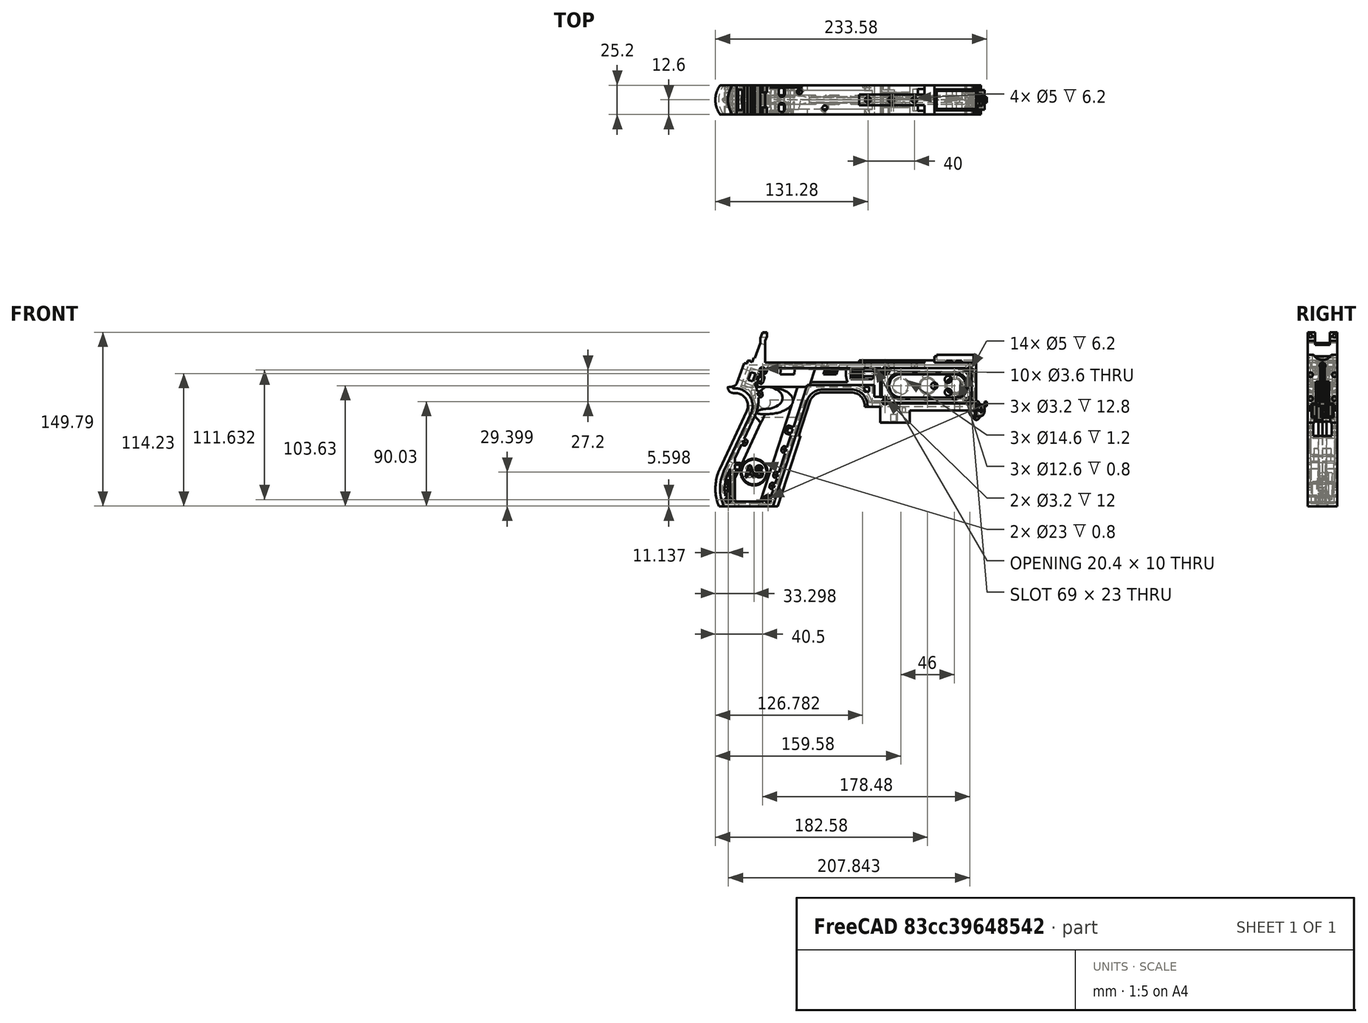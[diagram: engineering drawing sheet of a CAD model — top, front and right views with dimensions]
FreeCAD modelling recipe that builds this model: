
FCSTD DOCUMENT  (FreeCAD 1.0R39319 (Git))
Label: PICON-OF_ver_55
License: All rights reserved
LicenseURL: https://en.wikipedia.org/wiki/All_rights_reserved
objects: Sketcher::SketchObject×124, Part::Extrusion×63, Part::Cut×48, PartDesign::Pad×29, PartDesign::Pocket×21, PartDesign::Chamfer×15, PartDesign::Body×10, PartDesign::Fillet×6, Part::MultiFuse×5, Part::Part2DObjectPython×4, PartDesign::SubtractivePipe×4, PartDesign::SubtractiveLoft×4, PartDesign::Plane×3, PartDesign::SubShapeBinder×2, Part::Sweep×1, PartDesign::ShapeBinder×1, Mesh::Feature×1, PartDesign::Point×1, PartDesign::Groove×1
note: 626 computed .brp shape members not serialized (recipe doc carries the construction recipe); baked Part::Feature solids carry a one-line shape summary decoded from their .brp

FEATURE [Sketcher::SketchObject] Sketch  label="corpo principale"
  ArcFitTolerance = 1e-06
  AttacherType = Attacher::AttachEngine3D
  AttachmentSupport = -> [XZ_Plane]
  FullyConstrained = true
  MakeInternals = false
  MapMode = 5
  Placement = pos=(0,0,0) rot=(1,0,0;1.5708rad)
  sketch-geometry (65):
    g0: LineSegment StartX=0 StartY=0 StartZ=0 EndX=-57.2 EndY=0 EndZ=0
    g1: LineSegment StartX=-57.2 StartY=0 StartZ=0 EndX=-57.2 EndY=-10.4 EndZ=0
    g2: LineSegment StartX=-57.2 StartY=-10.4 StartZ=0 EndX=-82.8 EndY=-10.4 EndZ=0
    g3: LineSegment StartX=-82.8 StartY=-10.4 StartZ=0 EndX=-82.8 EndY=3.2 EndZ=0
    g4: LineSegment StartX=-82.8 StartY=3.2 StartZ=0 EndX=-93.6 EndY=3.2 EndZ=0
    g5: LineSegment StartX=-93.6 StartY=3.2 StartZ=0 EndX=-93.6 EndY=4 EndZ=0
    g6: LineSegment StartX=-107.6 StartY=18 StartZ=0 EndX=-132.428 EndY=18 EndZ=0
    g7: LineSegment StartX=-145.743 StartY=8.32624 StartZ=0 EndX=-175.232 EndY=-82.4316 EndZ=0
    g8: LineSegment StartX=-175.232 StartY=-82.4316 StartZ=0 EndX=-217.232 EndY=-82.4316 EndZ=0
    g9: LineSegment StartX=-217.232 StartY=-52.1862 StartZ=0 EndX=-193.988 EndY=-2.33927 EndZ=0
    g10: LineSegment StartX=-206.196 StartY=23.0857 StartZ=0 EndX=-199.861 EndY=40.4914 EndZ=0
    g11: LineSegment StartX=-199.861 StartY=40.4914 StartZ=0 EndX=-197.061 EndY=40.4914 EndZ=0
    g12: LineSegment StartX=-197.061 StartY=40.4914 StartZ=0 EndX=-197.061 EndY=42.8914 EndZ=0
    g13: LineSegment StartX=-197.061 StartY=42.8914 StartZ=0 EndX=-194.261 EndY=42.8914 EndZ=0
    g14: LineSegment StartX=-194.261 StartY=42.8914 StartZ=0 EndX=-194.535 EndY=42.1397 EndZ=0
    g15: LineSegment StartX=-194.535 StartY=42.1397 StartZ=0 EndX=-193.031 EndY=41.5924 EndZ=0
    g16: LineSegment StartX=-193.031 StartY=41.5924 StartZ=0 EndX=-191.663 EndY=45.3512 EndZ=0
    g17: LineSegment StartX=-191.663 StartY=45.3512 StartZ=0 EndX=-190.536 EndY=44.9408 EndZ=0
    g18: LineSegment StartX=-190.536 StartY=44.9408 StartZ=0 EndX=-185.747 EndY=58.0965 EndZ=0
    g19: LineSegment StartX=-185.747 StartY=58.0965 StartZ=0 EndX=-185.747 EndY=62.0965 EndZ=0
    g20: LineSegment StartX=-185.747 StartY=62.0965 StartZ=0 EndX=-183.832 EndY=67.3588 EndZ=0
    g21: LineSegment StartX=-183.832 StartY=67.3588 StartZ=0 EndX=-180.232 EndY=67.3588 EndZ=0
    g22: LineSegment StartX=-180.232 StartY=67.3588 StartZ=0 EndX=-180.232 EndY=63.7588 EndZ=0
    g23: LineSegment StartX=-180.232 StartY=63.7588 StartZ=0 EndX=-181.6 EndY=60 EndZ=0
    g24: LineSegment StartX=-181.6 StartY=60 StartZ=0 EndX=-181.6 EndY=41.2 EndZ=0
    g25: LineSegment StartX=-181.6 StartY=41.2 StartZ=0 EndX=-100.8 EndY=41.2 EndZ=0
    g26: LineSegment StartX=-36 StartY=43.2 StartZ=0 EndX=-36 EndY=41.2 EndZ=0
    g27: LineSegment StartX=0 StartY=48 StartZ=0 EndX=0 EndY=0 EndZ=0
    g28: LineSegment StartX=-209.901 StartY=19.85 StartZ=0 EndX=-209.901 EndY=20.1 EndZ=0
    g29: LineSegment StartX=-208.001 StartY=22 StartZ=0 EndX=-207.747 EndY=22 EndZ=0
    g30: LineSegment StartX=-207.583 StartY=19 StartZ=0 EndX=-209.051 EndY=19 EndZ=0
    g31: ArcOfCircle CenterX=-208.001 CenterY=20.1 CenterZ=0 NormalX=0 NormalY=0 NormalZ=1 AngleXU=0 Radius=1.9 StartAngle=1.5708 EndAngle=3.14159
    g32: GeomPoint [constr] X=-209.901 Y=22 Z=0
    g33: ArcOfCircle CenterX=-209.051 CenterY=19.85 CenterZ=0 NormalX=0 NormalY=0 NormalZ=1 AngleXU=0 Radius=0.85 StartAngle=3.14159 EndAngle=4.71239
    g34: GeomPoint [constr] X=-209.901 Y=19 Z=0
    g35: ArcOfCircle CenterX=-207.747 CenterY=23.65 CenterZ=0 NormalX=0 NormalY=0 NormalZ=1 AngleXU=0 Radius=1.65 StartAngle=4.71239 EndAngle=5.93412
    g36: GeomPoint [constr] X=-206.591 Y=22 Z=0
    g37: LineSegment StartX=-4 StartY=6 StartZ=0 EndX=-4 EndY=36.4 EndZ=0
    g38: LineSegment StartX=-4 StartY=36.4 StartZ=0 EndX=-185.2 EndY=36.4 EndZ=0
    g39: LineSegment StartX=-185.2 StartY=36.4 StartZ=0 EndX=-190.441 EndY=22 EndZ=0
    g40: LineSegment StartX=-214.575 StartY=-78.4316 StartZ=0 EndX=-178.142 EndY=-78.4316 EndZ=0
    g41: LineSegment StartX=-178.142 StartY=-78.4316 StartZ=0 EndX=-145.51 EndY=22 EndZ=0
    g42: LineSegment StartX=-145.51 StartY=22 StartZ=0 EndX=-87.91 EndY=22 EndZ=0
    g43: LineSegment StartX=-87.91 StartY=22 StartZ=0 EndX=-87.91 EndY=11.6 EndZ=0
    g44: LineSegment StartX=-87.91 StartY=11.6 StartZ=0 EndX=-80.11 EndY=11.6 EndZ=0
    g45: LineSegment StartX=-80.11 StartY=11.6 StartZ=0 EndX=-80.11 EndY=6 EndZ=0
    g46: LineSegment StartX=-80.11 StartY=6 StartZ=0 EndX=-4 EndY=6 EndZ=0
    g47: LineSegment StartX=-190.363 StartY=-4.02975 StartZ=0 EndX=-213.607 EndY=-53.8767 EndZ=0
    g48: ArcOfCircle CenterX=-132.428 CenterY=4 CenterZ=0 NormalX=0 NormalY=0 NormalZ=1 AngleXU=0 Radius=14 StartAngle=1.5708 EndAngle=2.82743
    g49: GeomPoint [constr] X=-142.6 Y=18 Z=0
    g50: ArcOfCircle CenterX=-107.6 CenterY=4 CenterZ=0 NormalX=0 NormalY=0 NormalZ=1 AngleXU=0 Radius=14 StartAngle=0 EndAngle=1.5708
    g51: GeomPoint [constr] X=-93.6 Y=18 Z=0
    g52: ArcOfCircle CenterX=-184.801 CenterY=-67.3089 CenterZ=0 NormalX=0 NormalY=0 NormalZ=1 AngleXU=0 Radius=35.7833 StartAngle=2.70526 EndAngle=3.57792
    g53: ArcOfCircle CenterX=-207.583 CenterY=4 CenterZ=0 NormalX=0 NormalY=0 NormalZ=1 AngleXU=0 Radius=15 StartAngle=5.84685 EndAngle=7.85398
    g54: LineSegment [constr] StartX=-213.607 StartY=-53.8767 StartZ=0 EndX=-217.232 EndY=-52.1862 EndZ=0
    g55: ArcOfCircle CenterX=-184.801 CenterY=-67.3089 CenterZ=0 NormalX=0 NormalY=0 NormalZ=1 AngleXU=0 Radius=31.7833 StartAngle=2.70526 EndAngle=3.49911
    g56: ArcOfCircle CenterX=-218.095 CenterY=8.90192 CenterZ=0 NormalX=0 NormalY=0 NormalZ=1 AngleXU=0 Radius=30.5989 StartAngle=5.84685 EndAngle=6.72553
    g57: LineSegment StartX=-44.6 StartY=43.2 StartZ=0 EndX=-36 EndY=43.2 EndZ=0
    g58: LineSegment StartX=-100.8 StartY=41.2 StartZ=0 EndX=-44.6 EndY=41.2 EndZ=0
    g59: LineSegment StartX=-44.6 StartY=41.2 StartZ=0 EndX=-44.6 EndY=43.2 EndZ=0
    g60: LineSegment StartX=-2.4 StartY=48 StartZ=0 EndX=0 EndY=48 EndZ=0
    g61: LineSegment StartX=-36 StartY=41.2 StartZ=0 EndX=-2.4 EndY=41.2 EndZ=0
    g62: LineSegment StartX=-2.4 StartY=41.2 StartZ=0 EndX=-2.4 EndY=48 EndZ=0
    g63: LineSegment [constr] StartX=-181.6 StartY=36.4 StartZ=0 EndX=-152.209 EndY=36.4 EndZ=0
    g64: LineSegment [constr] StartX=-181.6 StartY=36.4 StartZ=0 EndX=-130.41 EndY=36.4 EndZ=0
  constraints (183):
    c: Coincident(g-1,g0)
    c: PointOnObject(g0,g-1)
    c: Coincident(g0,g1)
    c: Vertical(g1)
    c: Coincident(g1,g2)
    c: Horizontal(g2)
    c: Coincident(g2,g3)
    c: Vertical(g3)
    c: Coincident(g3,g4)
    c: Coincident(g4,g5)
    c: Vertical(g5)
    c: Horizontal(g6)
    c: Coincident(g7,g8)
    c: Horizontal(g8)
    c: Coincident(g10,g11)
    c: Horizontal(g11)
    c: Coincident(g11,g12)
    c: Vertical(g12)
    c: Coincident(g12,g13)
    c: Horizontal(g13)
    c: Coincident(g13,g14)
    c: Coincident(g14,g15)
    c: Coincident(g15,g16)
    c: Coincident(g16,g17)
    c: Coincident(g17,g18)
    c: Coincident(g18,g19)
    c: Vertical(g19)
    c: Coincident(g19,g20)
    c: Coincident(g20,g21)
    c: Horizontal(g21)
    c: Coincident(g21,g22)
    c: Vertical(g22)
    c: Coincident(g22,g23)
    c: Coincident(g23,g24)
    c: Vertical(g24)
    c: Coincident(g24,g25)
    c: Horizontal(g25)
    c: Coincident(g57,g26)
    c: Vertical(g26)
    c: Coincident(g26,g61)
    c: PointOnObject(g60,g-2)
    c: Coincident(g60,g27)
    c: Coincident(g27,g0)
    c: DistanceY(g27,g27) = 48
    c: DistanceY(g1,g1) = 10.4
    c: DistanceX(g0,g0) = 57.2
    c: DistanceX(g2,g2) = 25.6
    c: Horizontal(g4)
    c: DistanceY(g3,g3) = 13.6
    c: DistanceX(g4,g4) = 10.8
    c: DistanceY(g5,g51) = 14.8
    c: DistanceX(g49,g51) = 49
    c: Distance(g7,g49) = 105.6
    c: DistanceX(g61,g60) = 36
    c: DistanceX(g25,g25) = 80.8
    c: DistanceY(g24,g24) = 18.8
    c: DistanceY(g22,g22) = 3.6
    c: Distance(g23) = 4
    c: Angle(g-1,g23) = 1.22173
    c: DistanceX(g21,g21) = 3.6
    c: Distance(g20) = 5.6
    c: Angle(g-1,g20) = 1.22173
    c: DistanceY(g19,g19) = 4
    c: Distance(g18) = 14
    c: Angle(g-1,g18) = 1.22173
    c: Distance(g17) = 1.2
    c: Distance(g16) = 4
    c: Angle(g16) = 1.22173
    c: Perpendicular(g18,g17)
    c: Distance(g15) = 1.6
    c: Perpendicular(g16,g15)
    c: Distance(g14) = 0.8
    c: DistanceX(g13,g13) = 2.8
    c: Perpendicular(g15,g14)
    c: DistanceY(g12,g12) = 2.4
    c: DistanceX(g11,g11) = 2.8
    c: Distance(g9) = 55
    c: Angle(g9,g-1) = 2.00713
    c: Horizontal(g29)
    c: Vertical(g28)
    c: Horizontal(g30)
    c: PointOnObject(g32,g29)
    c: PointOnObject(g32,g28)
    c: Tangent(g29,g31) = 1.5708
    c: Tangent(g28,g31) = 1.5708
    c: PointOnObject(g34,g28)
    c: PointOnObject(g34,g30)
    c: Tangent(g28,g33) = 1.5708
    c: Tangent(g30,g33) = 1.5708
    c: PointOnObject(g36,g29)
    c: PointOnObject(g36,g10)
    c: Tangent(g29,g35) = -1.5708
    c: Tangent(g10,g35) = -1.5708
    c: Angle(g-1,g10) = 1.22173
    c: Radius(g35) = 1.65
    c: Vertical(g37)
    c: Coincident(g37,g38)
    c: Horizontal(g38)
    c: Coincident(g38,g39)
    c: Horizontal(g40)
    c: Coincident(g40,g41)
    c: Coincident(g41,g42)
    c: Horizontal(g42)
    c: Coincident(g42,g43)
    c: Vertical(g43)
    c: Coincident(g43,g44)
    c: Horizontal(g44)
    c: Coincident(g44,g45)
    c: Vertical(g45)
    c: Coincident(g45,g46)
    c: Coincident(g46,g37)
    c: Horizontal(g46)
    c: DistanceY(g0,g37) = 6
    c: DistanceX(g37,g0) = 4
    c: DistanceY(g37,g25) = 4.8
    c: DistanceX(g38,g38) = 181.2
    c: DistanceX(g42,g42) = 57.6
    c: DistanceY(g49,g41) = 4
    c: DistanceX(g41,g49) = 2.91
    c: DistanceY(g43,g43) = 10.4
    c: DistanceX(g44,g44) = 7.8
    c: DistanceY(g7,g40) = 4
    c: Distance(g47) = 55
    c: Angle(g-1,g39) = 1.22173
    c: PointOnObject(g49,g7)
    c: PointOnObject(g49,g6)
    c: Tangent(g7,g48) = -1.5708
    c: Tangent(g6,g48) = -1.5708
    c: PointOnObject(g51,g5)
    c: PointOnObject(g51,g6)
    c: Tangent(g5,g50) = -1.5708
    c: Tangent(g6,g50) = -1.5708
    c: Radius(g50) = 14
    c: Radius(g48) = 14
    c: DistanceX(g8,g8) = 42
    c: Angle(g7,g-1) = 1.88496
    c: Parallel(g41,g7)
    c: Parallel(g47,g9)
    c: Coincident(g52,g8)
    c: Tangent(g52,g9) = 1.5708
    c: DistanceX(g9,g8) = 0
    c: Tangent(g53,g9) = -1.5708
    c: Tangent(g53,g30) = -1.5708
    c: Diameter(g53) = 30
    c: DistanceY(g53,g0) = -4
    c: Coincident(g54,g47)
    c: Distance(g54) = 4
    c: Coincident(g54,g9)
    c: Coincident(g55,g40)
    c: Tangent(g55,g47) = -1.5708
    c: Coincident(g52,g55)
    c: Coincident(g56,g39)
    c: Tangent(g56,g47) = 1.5708
    c: Horizontal(g57)
    c: DistanceX(g57,g57) = 8.6
    c: Coincident(g58,g25)
    c: Horizontal(g58)
    c: Coincident(g59,g58)
    c: Vertical(g59)
    c: DistanceY(g58,g57) = 2
    c: DistanceX(g58,g58) = 56.2
    c: Coincident(g59,g57)
    c: DistanceY(g41,g36) = 0
    c: DistanceY(g36,g39) = 0
    c: DistanceY(g28,g28) = 0.25
    c: DistanceX(g30,g36) = 2.46
    c: DistanceX(g28,g29) = 1.9
    c: Coincident(g62,g60)
    c: Horizontal(g60)
    c: DistanceX(g62,g27) = 2.4
    c: Coincident(g61,g62)
    c: DistanceY(g26,g26) = 2
    c: Vertical(g62)
    c: DistanceY(g61,g60) = 6.8
    c: Horizontal(g61)
    c: Distance(g63) = 29.391
    c: PointOnObject(g63,g38)
    c: PointOnObject(g63,g38)
    c: Distance(g64) = 51.19
    c: PointOnObject(g64,g38)
    c: PointOnObject(g64,g38)
    c: DistanceX(g24,g63) = 0
    c: DistanceX(g24,g64) = 0
FEATURE [Part::Extrusion] Extrude  label="Extrude corpo principale"
  Base = -> Sketch
  Dir = (0,-1,2e-16)
  DirMode = 2
  FaceMakerClass = Part::FaceMakerBullseye
  FaceMakerMode = 3
  LengthFwd = 25.2
  LengthRev = 12.6
  Solid = true
  Symmetric = true
FEATURE [Sketcher::SketchObject] Sketch002  label="scavo grilletto"
  ArcFitTolerance = 1e-06
  AttachmentSupport = -> [XZ_Plane]
  ExternalGeometry = -> [Sketch]
  FullyConstrained = true
  MakeInternals = false
  MapMode = 5
  Placement = pos=(0,0,0) rot=(1,0,0;1.5708rad)
  sketch-geometry (4):
    g0: LineSegment StartX=-89.51 StartY=22 StartZ=0 EndX=-152.71 EndY=22 EndZ=0
    g1: LineSegment StartX=-152.71 StartY=22 StartZ=0 EndX=-167.006 EndY=-22 EndZ=0
    g2: LineSegment StartX=-167.006 StartY=-22 StartZ=0 EndX=-89.51 EndY=-22 EndZ=0
    g3: LineSegment StartX=-89.51 StartY=-22 StartZ=0 EndX=-89.51 EndY=22 EndZ=0
  constraints (12):
    c: Horizontal(g0)
    c: Coincident(g0,g1)
    c: Coincident(g1,g2)
    c: Horizontal(g2)
    c: Coincident(g2,g3)
    c: Coincident(g3,g0)
    c: Vertical(g3)
    c: Angle(g1,g0) = 1.88496
    c: DistanceY(g3,g3) = 44
    c: DistanceX(g0,g0) = 63.2
    c: DistanceX(g0,g-3) = 1.6
    c: DistanceY(g-3,g0) = 0
FEATURE [Sketcher::SketchObject] Sketch004  label="traiettoria arrotondamento impugnatura anteriore"
  ArcFitTolerance = 1e-06
  AttachmentSupport = -> [XZ_Plane]
  ExternalGeometry = -> [Sketch]
  FullyConstrained = true
  MakeInternals = false
  MapMode = 5
  Placement = pos=(0,0,0) rot=(1,0,0;1.5708rad)
  sketch-geometry (13):
    g0: LineSegment StartX=-175.232 StartY=-82.4316 StartZ=0 EndX=-145.743 EndY=8.32624 EndZ=0
    g1: LineSegment StartX=-93.6 StartY=3.2 StartZ=0 EndX=-93.6 EndY=4 EndZ=0
    g2: LineSegment StartX=-132.428 StartY=18 StartZ=0 EndX=-107.6 EndY=18 EndZ=0
    g3: ArcOfCircle CenterX=-132.428 CenterY=4 CenterZ=0 NormalX=0 NormalY=0 NormalZ=1 AngleXU=0 Radius=14 StartAngle=1.5708 EndAngle=2.82743
    g4: ArcOfCircle CenterX=-107.6 CenterY=4 CenterZ=0 NormalX=0 NormalY=0 NormalZ=1 AngleXU=0 Radius=14 StartAngle=0 EndAngle=1.5708
    g5: LineSegment StartX=-175.232 StartY=-82.4316 StartZ=0 EndX=-217.232 EndY=-82.4316 EndZ=0
    g6: LineSegment StartX=-217.232 StartY=-52.1862 StartZ=0 EndX=-193.988 EndY=-2.33927 EndZ=0
    g7: LineSegment StartX=-209.051 StartY=19 StartZ=0 EndX=-207.583 EndY=19 EndZ=0
    g8: LineSegment StartX=-209.901 StartY=20.1 StartZ=0 EndX=-209.901 EndY=19.85 EndZ=0
    g9: ArcOfCircle CenterX=-184.801 CenterY=-67.3089 CenterZ=0 NormalX=0 NormalY=0 NormalZ=1 AngleXU=0 Radius=35.7833 StartAngle=2.70526 EndAngle=3.57792
    g10: ArcOfCircle CenterX=-207.583 CenterY=4 CenterZ=0 NormalX=0 NormalY=0 NormalZ=1 AngleXU=0 Radius=15 StartAngle=5.84685 EndAngle=7.85398
    g11: ArcOfCircle CenterX=-209.051 CenterY=19.85 CenterZ=0 NormalX=0 NormalY=0 NormalZ=1 AngleXU=0 Radius=0.85 StartAngle=3.14159 EndAngle=4.71239
    g12: ArcOfCircle CenterX=-208.001 CenterY=20.1 CenterZ=0 NormalX=0 NormalY=0 NormalZ=1 AngleXU=0 Radius=1.9 StartAngle=1.5708 EndAngle=3.14159
  constraints (26):
    c: Coincident(g0,g-3)
    c: Coincident(g0,g-6)
    c: Coincident(g1,g-8)
    c: Coincident(g1,g-7)
    c: Coincident(g2,g-5)
    c: Coincident(g2,g-4)
    c: Coincident(g3,g2)
    c: Tangent(g3,g0) = 1.5708
    c: Coincident(g4,g1)
    c: Tangent(g4,g2) = 1.5708
    c: Coincident(g5,g0)
    c: Coincident(g5,g-9)
    c: Coincident(g6,g-12)
    c: Coincident(g6,g-11)
    c: Coincident(g7,g-15)
    c: Coincident(g7,g-14)
    c: Coincident(g8,g-16)
    c: Coincident(g8,g-17)
    c: Tangent(g9,g6) = 1.5708
    c: Coincident(g9,g5)
    c: Coincident(g10,g7)
    c: Tangent(g10,g6) = -1.5708
    c: Tangent(g11,g7) = -1.5708
    c: Coincident(g11,g8)
    c: Tangent(g12,g8) = -1.5708
    c: Coincident(g12,g-17)
FEATURE [PartDesign::Plane] DatumPlane  label="Piano per disegno arrotondamento impugnatura"
  AttachmentSupport = -> [Sketch]
  Length = 73.6581
  MapMode = 7
  Placement = pos=(-145.743,1.8e-15,8.32624) rot=(0.154555,0.154555,0.97582;1.59527rad)
  ResizeMode = 0
  Width = 303.511
FEATURE [Sketcher::SketchObject] Sketch005  label="forma arrotondamento impugnatura anteriore"
  ArcFitTolerance = 1e-06
  AttachmentSupport = -> [DatumPlane]
  FullyConstrained = true
  MakeInternals = false
  MapMode = 5
  Placement = pos=(-145.743,1.8e-15,8.32624) rot=(0.154555,0.154555,0.97582;1.59527rad)
  sketch-geometry (5):
    g0: GeomPoint [constr] X=0 Y=-4 Z=0
    g1: GeomPoint [constr] X=-12.6 Y=7.1e-15 Z=0
    g2: GeomPoint [constr] X=12.6 Y=4.97e-14 Z=0
    g3: LineSegment StartX=-12.6 StartY=7.1e-15 StartZ=0 EndX=12.6 EndY=4.97e-14 EndZ=0
    g4: ArcOfCircle CenterX=-3.88e-14 CenterY=17.845 CenterZ=0 NormalX=0 NormalY=0 NormalZ=1 AngleXU=0 Radius=21.845 StartAngle=4.09759 EndAngle=5.32718
  constraints (11):
    c: DistanceY(g0,g-1) = 4
    c: DistanceX(g-1,g0) = 0
    c: DistanceX(g1,g-1) = 12.6
    c: DistanceX(g-1,g2) = 12.6
    c: DistanceY(g-1,g2) = 0
    c: DistanceY(g-1,g1) = 0
    c: Coincident(g3,g1)
    c: Coincident(g3,g2)
    c: Coincident(g4,g1)
    c: Coincident(g4,g2)
    c: PointOnObject(g0,g4)
FEATURE [Part::Sweep] Sweep  label="Sweep impugnatura"
  Frenet = true
  Sections = -> [Sketch005]
  Solid = true
  Spine = -> Sketch [Edge32,Edge33,Edge34,Edge35,Edge36,Edge37,Edge38,Edge39,Edge40,Edge41,Edge42,Edge43,Edge44]
  Transition = 1
FEATURE [Sketcher::SketchObject] Sketch008  label="buchi e pulizie varie"
  ArcFitTolerance = 1e-06
  AttachmentSupport = -> [XZ_Plane]
  ExternalGeometry = -> [Sketch]
  FullyConstrained = true
  MakeInternals = false
  MapMode = 5
  Placement = pos=(0,0,0) rot=(1,0,0;1.5708rad)
  sketch-geometry (26):
    g0: LineSegment StartX=-96.278 StartY=20.155 StartZ=0 EndX=-92.278 EndY=20.155 EndZ=0
    g1: LineSegment StartX=-92.278 StartY=20.155 StartZ=0 EndX=-92.278 EndY=16.155 EndZ=0
    g2: LineSegment StartX=-92.278 StartY=16.155 StartZ=0 EndX=-96.278 EndY=16.155 EndZ=0
    g3: LineSegment StartX=-96.278 StartY=16.155 StartZ=0 EndX=-96.278 EndY=20.155 EndZ=0
    g4: LineSegment StartX=-222.232 StartY=-82.4316 StartZ=0 EndX=-170.232 EndY=-82.4316 EndZ=0
    g5: LineSegment StartX=-170.232 StartY=-82.4316 StartZ=0 EndX=-170.232 EndY=-86.4316 EndZ=0
    g6: LineSegment StartX=-170.232 StartY=-86.4316 StartZ=0 EndX=-222.232 EndY=-86.4316 EndZ=0
    g7: LineSegment StartX=-222.232 StartY=-86.4316 StartZ=0 EndX=-222.232 EndY=-82.4316 EndZ=0
    g8: LineSegment StartX=-213.901 StartY=20.1 StartZ=0 EndX=-213.901 EndY=26 EndZ=0
    g9: LineSegment StartX=-213.901 StartY=26 StartZ=0 EndX=-206.196 EndY=26 EndZ=0
    g10: LineSegment StartX=-17.4 StartY=42.8 StartZ=0 EndX=-12.4 EndY=42.8 EndZ=0
    g11: LineSegment StartX=-12.4 StartY=42.8 StartZ=0 EndX=-12.4 EndY=41.2 EndZ=0
    g12: LineSegment StartX=-12.4 StartY=41.2 StartZ=0 EndX=-17.4 EndY=41.2 EndZ=0
    g13: LineSegment StartX=-17.4 StartY=41.2 StartZ=0 EndX=-17.4 EndY=42.8 EndZ=0
    g14: LineSegment StartX=-25.9 StartY=42.8 StartZ=0 EndX=-20.9 EndY=42.8 EndZ=0
    g15: LineSegment StartX=-20.9 StartY=42.8 StartZ=0 EndX=-20.9 EndY=41.2 EndZ=0
    g16: LineSegment StartX=-20.9 StartY=41.2 StartZ=0 EndX=-25.9 EndY=41.2 EndZ=0
    g17: LineSegment StartX=-25.9 StartY=41.2 StartZ=0 EndX=-25.9 EndY=42.8 EndZ=0
    g18: GeomPoint [constr] X=-206.196 Y=23.0857 Z=0
    g19: GeomPoint [constr] X=-213.901 Y=20.1 Z=0
    g20: BSplineCurve PolesCount=4 KnotsCount=2 Degree=3 IsPeriodic=0
    g21-g24: Circle [constr] x4 (B-spline internal-alignment scaffolding for g20; pole/knot coordinates omitted)
    g25: LineSegment StartX=-206.196 StartY=26 StartZ=0 EndX=-206.196 EndY=23.0857 EndZ=0
  constraints (73):
    c: Horizontal(g0)
    c: Coincident(g1,g0)
    c: Vertical(g1)
    c: Coincident(g2,g1)
    c: Horizontal(g2)
    c: Coincident(g3,g2)
    c: Coincident(g3,g0)
    c: Vertical(g3)
    c: DistanceX(g0,g-4) = 4.368
    c: DistanceY(g0,g-4) = 1.845
    c: DistanceY(g1,g1) = 4
    c: DistanceX(g2,g2) = 4
    c: Horizontal(g4)
    c: Coincident(g5,g4)
    c: Vertical(g5)
    c: Coincident(g6,g5)
    c: Horizontal(g6)
    c: Coincident(g7,g6)
    c: Coincident(g7,g4)
    c: Vertical(g7)
    c: DistanceY(g7,g7) = 4
    c: DistanceX(g4,g-5) = 5
    c: DistanceX(g-5,g4) = 5
    c: DistanceY(g4,g-5) = 0
    c: Coincident(g9,g8)
    c: Parallel(g9,g-6)
    c: DistanceX(g8,g-8) = 4
    c: Horizontal(g10)
    c: Coincident(g11,g10)
    c: Vertical(g11)
    c: Coincident(g12,g11)
    c: Horizontal(g12)
    c: Coincident(g13,g12)
    c: Coincident(g13,g10)
    c: Vertical(g13)
    c: Horizontal(g14)
    c: Coincident(g15,g14)
    c: Vertical(g15)
    c: Coincident(g16,g15)
    c: Horizontal(g16)
    c: Coincident(g17,g16)
    c: Coincident(g17,g14)
    c: Vertical(g17)
    c: DistanceY(g11,g10) = 1.6
    c: DistanceX(g10,g10) = 5
    c: DistanceY(g15,g14) = 1.6
    c: DistanceX(g14,g14) = 5
    c: DistanceX(g15,g12) = 3.5
    c: DistanceX(g11,g-9) = 10
    c: DistanceY(g-9,g11) = 0
    c: DistanceY(g-9,g15) = 0
    c: Perpendicular(g8,g9)
    c: DistanceY(g-7,g9) = 4
    c: DistanceY(g8,g-8) = 0
    c: InternalAlignment(g18,g20)
    c: InternalAlignment(g19,g20)
    c: InternalAlignment(g21,g20)
    c: Weight(g21) = 1
    c: InternalAlignment(g22,g20)
    c: Equal(g22,g21)
    c: InternalAlignment(g23,g20)
    c: Equal(g23,g21)
    c: InternalAlignment(g24,g20)
    c: Equal(g24,g21)
    c: Coincident(g18,g-12)
    c: Coincident(g19,g8)
    c: Coincident(g25,g9)
    c: Coincident(g25,g20)
    c: Vertical(g25)
    c: DistanceY(g20,g23) = 0
    c: DistanceY(g22,g18) = 2.26
    c: DistanceX(g22,g18) = 0.93
    c: DistanceX(g20,g23) = 2.9
FEATURE [Part::Extrusion] Extrude004  label="Extrude Buchi e pulizie varie"
  Base = -> Sketch008
  Dir = (0,-1,2e-16)
  DirMode = 2
  FaceMakerClass = Part::FaceMakerBullseye
  FaceMakerMode = 3
  LengthFwd = 25.2
  LengthRev = 0
  Solid = true
  Symmetric = true
FEATURE [Sketcher::SketchObject] Sketch009  label="rinforzi"
  ArcFitTolerance = 1e-06
  AttachmentSupport = -> [XZ_Plane]
  ExternalGeometry = -> [Sketch]
  FullyConstrained = true
  MakeInternals = false
  MapMode = 5
  Placement = pos=(0,0,0) rot=(1,0,0;1.5708rad)
  sketch-geometry (9):
    g0: LineSegment StartX=-87.91 StartY=22 StartZ=0 EndX=-87.91 EndY=36.4 EndZ=0
    g1: LineSegment StartX=-87.91 StartY=36.4 StartZ=0 EndX=-97.91 EndY=36.4 EndZ=0
    g2: LineSegment StartX=-97.91 StartY=36.4 StartZ=0 EndX=-97.91 EndY=22 EndZ=0
    g3: LineSegment StartX=-97.91 StartY=22 StartZ=0 EndX=-87.91 EndY=22 EndZ=0
    g4: LineSegment StartX=-149.713 StartY=9.06563 StartZ=0 EndX=-154.586 EndY=-5.93437 EndZ=0
    g5: LineSegment StartX=-154.586 StartY=-5.93437 StartZ=0 EndX=-191.863 EndY=-5.93437 EndZ=0
    g6: LineSegment StartX=-191.863 StartY=-5.93437 StartZ=0 EndX=-191.863 EndY=9.06563 EndZ=0
    g7: LineSegment StartX=-191.863 StartY=9.06563 StartZ=0 EndX=-149.713 EndY=9.06563 EndZ=0
    g8: LineSegment [constr] StartX=-145.51 StartY=22 StartZ=0 EndX=-149.713 EndY=9.06563 EndZ=0
  constraints (25):
    c: Vertical(g0)
    c: Coincident(g1,g0)
    c: Horizontal(g1)
    c: Coincident(g2,g1)
    c: Vertical(g2)
    c: Coincident(g3,g2)
    c: Coincident(g3,g0)
    c: Horizontal(g3)
    c: Coincident(g0,g-4)
    c: DistanceX(g3,g3) = 10
    c: DistanceY(g0,g-3) = 0
    c: Coincident(g5,g4)
    c: Horizontal(g5)
    c: Coincident(g6,g5)
    c: Vertical(g6)
    c: Coincident(g7,g6)
    c: Coincident(g7,g4)
    c: Horizontal(g7)
    c: Distance(g8) = 13.6
    c: Parallel(g-6,g8)
    c: Coincident(g-6,g8)
    c: Parallel(g4,g-6)
    c: DistanceY(g4,g4) = 15
    c: Coincident(g4,g8)
    c: DistanceX(g-5,g5) = -1.5
FEATURE [Part::Extrusion] Extrude001  label="Extrude scavo grilletto"
  Base = -> Sketch002
  Dir = (0,-1,2e-16)
  DirMode = 2
  FaceMakerClass = Part::FaceMakerBullseye
  FaceMakerMode = 3
  LengthFwd = 16
  LengthRev = 0
  Solid = true
  Symmetric = true
FEATURE [Part::Extrusion] Extrude005  label="Extrude Rinforzi"
  Base = -> Sketch009
  Dir = (0,-1,2e-16)
  DirMode = 2
  FaceMakerClass = Part::FaceMakerBullseye
  FaceMakerMode = 3
  LengthFwd = 2
  LengthRev = 0
  Placement = pos=(0,12.6,0) rot=(0,0,1;0rad)
  Solid = true
  Symmetric = false
FEATURE [PartDesign::ShapeBinder] CopyCut
  TraceSupport = false
FEATURE [PartDesign::Plane] DatumPlane001
  AttachmentSupport = -> [CopyCut]
  Length = 283.944
  MapMode = 5
  Placement = pos=(0,12.6,0) rot=(0,0.707107,0.707107;3.14159rad)
  ResizeMode = 0
  Width = 188.15
FEATURE [Sketcher::SketchObject] Sketch010  label="buco neopixel"
  ArcFitTolerance = 1e-06
  AttachmentSupport = -> [XZ_Plane]
  ExternalGeometry = -> [Sketch]
  FullyConstrained = true
  MakeInternals = false
  MapMode = 5
  Placement = pos=(0,0,0) rot=(1,0,0;1.5708rad)
  sketch-geometry (5):
    g0: LineSegment [constr] StartX=-199.861 StartY=40.4914 StartZ=0 EndX=-201.368 EndY=36.3521 EndZ=0
    g1: LineSegment StartX=-201.368 StartY=36.3521 StartZ=0 EndX=-204.932 EndY=26.5605 EndZ=0
    g2: LineSegment StartX=-201.368 StartY=36.3521 StartZ=0 EndX=-180.2 EndY=28.6477 EndZ=0
    g3: LineSegment StartX=-180.2 StartY=28.6477 StartZ=0 EndX=-183.764 EndY=18.8561 EndZ=0
    g4: LineSegment StartX=-183.764 StartY=18.8561 StartZ=0 EndX=-204.932 EndY=26.5605 EndZ=0
  constraints (14):
    c: Parallel(g0,g-3)
    c: Distance(g0) = 4.405
    c: Coincident(g0,g-3)
    c: Coincident(g2,g1)
    c: Coincident(g3,g2)
    c: Coincident(g4,g3)
    c: Coincident(g4,g1)
    c: Parallel(g1,g-3)
    c: Distance(g1) = 10.42
    c: Coincident(g1,g0)
    c: Parallel(g2,g4)
    c: Perpendicular(g1,g2)
    c: DistanceX(g-4,g2) = 5
    c: Parallel(g3,g1)
FEATURE [Part::Extrusion] Extrude006  label="Extrude buco neopixel"
  Base = -> Sketch010
  Dir = (0,-1,2e-16)
  DirMode = 2
  FaceMakerClass = Part::FaceMakerBullseye
  FaceMakerMode = 3
  LengthFwd = 17.2
  LengthRev = 0
  Solid = true
  Symmetric = true
FEATURE [Sketcher::SketchObject] Sketch011  label="fermo grilletto"
  ArcFitTolerance = 1e-06
  AttachmentSupport = -> [XZ_Plane]
  ExternalGeometry = -> [Sketch]
  FullyConstrained = true
  MakeInternals = false
  MapMode = 5
  Placement = pos=(0,0,0) rot=(1,0,0;1.5708rad)
  sketch-geometry (18):
    g0: LineSegment [constr] StartX=-145.51 StartY=22 StartZ=0 EndX=-157.347 EndY=-14.4293 EndZ=0
    g1: LineSegment [constr] StartX=-157.347 StartY=-14.4293 StartZ=0 EndX=-157.841 EndY=-15.951 EndZ=0
    g2: LineSegment StartX=-161.151 StartY=-13.1932 StartZ=0 EndX=-155.825 EndY=-14.9237 EndZ=0
    g3: LineSegment StartX=-163.167 StartY=-14.2205 StartZ=0 EndX=-164.403 EndY=-18.0247 EndZ=0
    g4: LineSegment StartX=-163.376 StartY=-20.0408 StartZ=0 EndX=-158.05 EndY=-21.7713 EndZ=0
    g5: LineSegment StartX=-158.05 StartY=-21.7713 StartZ=0 EndX=-155.825 EndY=-14.9237 EndZ=0
    g6: LineSegment StartX=-161.645 StartY=-14.7149 StartZ=0 EndX=-157.841 EndY=-15.951 EndZ=0
    g7: LineSegment StartX=-157.841 StartY=-15.951 StartZ=0 EndX=-159.077 EndY=-19.7552 EndZ=0
    g8: LineSegment StartX=-159.077 StartY=-19.7552 StartZ=0 EndX=-162.881 EndY=-18.5191 EndZ=0
    g9: LineSegment StartX=-162.881 StartY=-18.5191 StartZ=0 EndX=-161.645 EndY=-14.7149 EndZ=0
    g10: LineSegment [constr] StartX=-161.645 StartY=-14.7149 StartZ=0 EndX=-161.151 EndY=-13.1932 EndZ=0
    g11: LineSegment [constr] StartX=-159.077 StartY=-19.7552 StartZ=0 EndX=-157.555 EndY=-20.2496 EndZ=0
    g12: LineSegment [constr] StartX=-159.077 StartY=-19.7552 StartZ=0 EndX=-159.572 EndY=-21.2769 EndZ=0
    g13: LineSegment [constr] StartX=-161.645 StartY=-14.7149 StartZ=0 EndX=-163.167 EndY=-14.2205 EndZ=0
    g14: ArcOfCircle CenterX=-161.645 CenterY=-14.7149 CenterZ=0 NormalX=0 NormalY=0 NormalZ=1 AngleXU=0 Radius=1.6 StartAngle=1.25664 EndAngle=2.82743
    g15: GeomPoint [constr] X=-162.673 Y=-12.6988 Z=0
    g16: ArcOfCircle CenterX=-162.881 CenterY=-18.5191 CenterZ=0 NormalX=0 NormalY=0 NormalZ=1 AngleXU=0 Radius=1.6 StartAngle=2.82743 EndAngle=4.39823
    g17: GeomPoint [constr] X=-164.897 Y=-19.5464 Z=0
  constraints (48):
    c: Parallel(g0,g-3)
    c: Distance(g0) = 38.304
    c: Coincident(g0,g-3)
    c: Parallel(g1,g-3)
    c: Distance(g1) = 1.6
    c: Coincident(g1,g0)
    c: Coincident(g5,g4)
    c: Coincident(g5,g2)
    c: Coincident(g7,g6)
    c: Coincident(g8,g7)
    c: Coincident(g9,g8)
    c: Coincident(g9,g6)
    c: Parallel(g7,g-3)
    c: Parallel(g9,g7)
    c: Perpendicular(g6,g7)
    c: Parallel(g6,g8)
    c: Distance(g6) = 4
    c: Distance(g9) = 4
    c: Parallel(g5,g7)
    c: Parallel(g9,g3)
    c: Parallel(g2,g6)
    c: Parallel(g4,g8)
    c: Parallel(g13,g6)
    c: Parallel(g10,g9)
    c: Parallel(g11,g8)
    c: Parallel(g12,g7)
    c: Distance(g10) = 1.6
    c: Distance(g13) = 1.6
    c: Distance(g12) = 1.6
    c: Distance(g11) = 1.6
    c: Coincident(g10,g6)
    c: Coincident(g13,g6)
    c: Coincident(g12,g7)
    c: Coincident(g11,g7)
    c: Distance(g10,g15) = 1.6
    c: Distance(g15,g13) = 1.6
    c: Distance(g4,g12) = 1.6
    c: Distance(g4,g11) = 1.6
    c: PointOnObject(g15,g2)
    c: Tangent(g3,g14) = -1.5708
    c: Tangent(g2,g14) = 1.5708
    c: PointOnObject(g17,g4)
    c: PointOnObject(g17,g3)
    c: Tangent(g4,g16) = -1.5708
    c: Tangent(g3,g16) = -1.5708
    c: Equal(g16,g14)
    c: Coincident(g16,g8)
    c: Coincident(g6,g1)
FEATURE [Part::Extrusion] Extrude007  label="Extrude fermo grilletto"
  Base = -> Sketch011
  Dir = (0,-1,2e-16)
  DirMode = 2
  FaceMakerClass = Part::FaceMakerBullseye
  FaceMakerMode = 3
  LengthFwd = 25.2
  LengthRev = 0
  Solid = true
  Symmetric = true
FEATURE [Sketcher::SketchObject] Sketch012  label="buco oled"
  ArcFitTolerance = 1e-06
  AttachmentSupport = -> [XZ_Plane]
  ExternalGeometry = -> [Sketch]
  FullyConstrained = true
  MakeInternals = false
  MapMode = 5
  Placement = pos=(0,0,0) rot=(1,0,0;1.5708rad)
  sketch-geometry (4):
    g0: LineSegment StartX=-185.747 StartY=58.0965 StartZ=0 EndX=-180.232 EndY=56.0891 EndZ=0
    g1: LineSegment StartX=-185.747 StartY=58.0965 StartZ=0 EndX=-185.747 EndY=67.3588 EndZ=0
    g2: LineSegment StartX=-185.747 StartY=67.3588 StartZ=0 EndX=-180.232 EndY=67.3588 EndZ=0
    g3: LineSegment StartX=-180.232 StartY=67.3588 StartZ=0 EndX=-180.232 EndY=56.0891 EndZ=0
  constraints (10):
    c: Coincident(g1,g0)
    c: Coincident(g2,g1)
    c: Coincident(g3,g2)
    c: Coincident(g3,g0)
    c: Parallel(g1,g-5)
    c: Perpendicular(g-3,g0)
    c: Parallel(g2,g-6)
    c: Parallel(g3,g-4)
    c: Coincident(g0,g-5)
    c: Coincident(g2,g-6)
FEATURE [Part::Extrusion] Extrude008  label="Extrude buco oled"
  Base = -> Sketch012
  Dir = (0,-1,2e-16)
  DirMode = 2
  FaceMakerClass = Part::FaceMakerBullseye
  FaceMakerMode = 3
  LengthFwd = 12.8
  LengthRev = 0
  Solid = true
  Symmetric = true
FEATURE [Sketcher::SketchObject] Sketch013  label="buco pompa"
  ArcFitTolerance = 1e-06
  AttachmentSupport = -> [XZ_Plane]
  ExternalGeometry = -> [Sketch]
  FullyConstrained = true
  MakeInternals = false
  MapMode = 5
  Placement = pos=(0,0,0) rot=(1,0,0;1.5708rad)
  sketch-geometry (8):
    g0: LineSegment StartX=-82.8 StartY=-10.4 StartZ=0 EndX=-82.8 EndY=-9.6 EndZ=0
    g1: LineSegment StartX=-82.8 StartY=-9.6 StartZ=0 EndX=-67.9 EndY=-9.6 EndZ=0
    g2: LineSegment StartX=-67.9 StartY=-9.6 StartZ=0 EndX=-67.9 EndY=6 EndZ=0
    g3: LineSegment StartX=-67.9 StartY=6 StartZ=0 EndX=-65.9 EndY=6 EndZ=0
    g4: LineSegment StartX=-65.9 StartY=6 StartZ=0 EndX=-65.9 EndY=-1.7 EndZ=0
    g5: LineSegment StartX=-65.9 StartY=-1.7 StartZ=0 EndX=-57.2 EndY=-1.7 EndZ=0
    g6: LineSegment StartX=-57.2 StartY=-1.7 StartZ=0 EndX=-57.2 EndY=-10.4 EndZ=0
    g7: LineSegment StartX=-57.2 StartY=-10.4 StartZ=0 EndX=-82.8 EndY=-10.4 EndZ=0
  constraints (22):
    c: Vertical(g0)
    c: Coincident(g1,g0)
    c: Horizontal(g1)
    c: Coincident(g2,g1)
    c: Vertical(g2)
    c: Coincident(g3,g2)
    c: Horizontal(g3)
    c: Coincident(g4,g3)
    c: Vertical(g4)
    c: Coincident(g5,g4)
    c: Horizontal(g5)
    c: Coincident(g6,g5)
    c: Vertical(g6)
    c: Coincident(g7,g6)
    c: Coincident(g7,g0)
    c: DistanceY(g0,g0) = 0.8
    c: DistanceY(g6,g6) = 8.7
    c: DistanceX(g1,g1) = 14.9
    c: DistanceX(g3,g3) = 2
    c: Coincident(g0,g-4)
    c: DistanceY(g2,g-6) = 0
    c: Coincident(g6,g-5)
FEATURE [Part::Extrusion] Extrude009  label="Extrude buco pompa"
  Base = -> Sketch013
  Dir = (0,-1,2e-16)
  DirMode = 2
  FaceMakerClass = Part::FaceMakerBullseye
  FaceMakerMode = 3
  LengthFwd = 13.2
  LengthRev = 0
  Solid = true
  Symmetric = true
FEATURE [Sketcher::SketchObject] Sketch014  label="buco frontale"
  ArcFitTolerance = 1e-06
  AttachmentSupport = -> [XZ_Plane]
  ExternalGeometry = -> [Sketch]
  FullyConstrained = true
  MakeInternals = false
  MapMode = 5
  Placement = pos=(0,0,0) rot=(1,0,0;1.5708rad)
  sketch-geometry (10):
    g0: LineSegment StartX=0 StartY=0 StartZ=0 EndX=0 EndY=24.671 EndZ=0
    g1: LineSegment StartX=0 StartY=24.671 StartZ=0 EndX=-4 EndY=24.671 EndZ=0
    g2: LineSegment StartX=-4 StartY=24.671 StartZ=0 EndX=-4 EndY=16 EndZ=0
    g3: LineSegment StartX=-4 StartY=16 StartZ=0 EndX=-2.4 EndY=16 EndZ=0
    g4: LineSegment StartX=-2.4 StartY=16 StartZ=0 EndX=-2.4 EndY=10 EndZ=0
    g5: LineSegment StartX=-2.4 StartY=10 StartZ=0 EndX=-12 EndY=10 EndZ=0
    g6: LineSegment StartX=-12 StartY=10 StartZ=0 EndX=-12 EndY=6 EndZ=0
    g7: LineSegment StartX=-12 StartY=6 StartZ=0 EndX=-2.4 EndY=6 EndZ=0
    g8: LineSegment StartX=-2.4 StartY=6 StartZ=0 EndX=-2.4 EndY=0 EndZ=0
    g9: LineSegment StartX=-2.4 StartY=0 StartZ=0 EndX=0 EndY=0 EndZ=0
  constraints (29):
    c: Vertical(g0)
    c: Coincident(g1,g0)
    c: Horizontal(g1)
    c: Coincident(g2,g1)
    c: Vertical(g2)
    c: Coincident(g3,g2)
    c: Horizontal(g3)
    c: Coincident(g4,g3)
    c: Vertical(g4)
    c: Coincident(g5,g4)
    c: Horizontal(g5)
    c: Coincident(g6,g5)
    c: Vertical(g6)
    c: Coincident(g7,g6)
    c: Coincident(g8,g7)
    c: Vertical(g8)
    c: Coincident(g9,g8)
    c: Coincident(g9,g0)
    c: Horizontal(g9)
    c: DistanceY(g0,g0) = 24.671
    c: Horizontal(g7)
    c: DistanceY(g6,g6) = 4
    c: DistanceY(g4,g4) = 6
    c: DistanceX(g9,g9) = 2.4
    c: Coincident(g0,g-1)
    c: DistanceY(g-3,g7) = 0
    c: DistanceX(g8,g4) = 0
    c: DistanceX(g-3,g1) = 0
    c: DistanceX(g6,g-3) = 8
FEATURE [Part::Extrusion] Extrude010  label="Extrude buco frontale"
  Base = -> Sketch014
  Dir = (0,-1,2e-16)
  DirMode = 2
  FaceMakerClass = Part::FaceMakerBullseye
  FaceMakerMode = 3
  LengthFwd = 11.2
  LengthRev = 0
  Solid = true
  Symmetric = true
FEATURE [Sketcher::SketchObject] Sketch015  label="guida rail"
  ArcFitTolerance = 1e-06
  AttachmentSupport = -> [XZ_Plane]
  ExternalGeometry = -> [Sketch]
  FullyConstrained = true
  MakeInternals = false
  MapMode = 5
  Placement = pos=(0,0,0) rot=(1,0,0;1.5708rad)
  sketch-geometry (4):
    g0: LineSegment StartX=-100.8 StartY=43.2 StartZ=0 EndX=-44.6 EndY=43.2 EndZ=0
    g1: LineSegment StartX=-44.6 StartY=43.2 StartZ=0 EndX=-44.6 EndY=41.2 EndZ=0
    g2: LineSegment StartX=-44.6 StartY=41.2 StartZ=0 EndX=-100.8 EndY=41.2 EndZ=0
    g3: LineSegment StartX=-100.8 StartY=41.2 StartZ=0 EndX=-100.8 EndY=43.2 EndZ=0
  constraints (9):
    c: Horizontal(g0)
    c: Coincident(g1,g0)
    c: Coincident(g2,g1)
    c: Coincident(g3,g2)
    c: Coincident(g3,g0)
    c: Vertical(g3)
    c: Coincident(g2,g-3)
    c: Coincident(g1,g-3)
    c: Coincident(g0,g-4)
FEATURE [Part::Extrusion] Extrude011  label="Extrude guida rail"
  Base = -> Sketch015
  Dir = (0,-1,2e-16)
  DirMode = 2
  FaceMakerClass = Part::FaceMakerBullseye
  FaceMakerMode = 3
  LengthFwd = 9
  LengthRev = 0
  Solid = true
  Symmetric = true
FEATURE [Sketcher::SketchObject] Sketch016  label="guide per coperture laterali"
  ArcFitTolerance = 1e-06
  AttachmentSupport = -> [XZ_Plane]
  ExternalGeometry = -> [Sketch]
  FullyConstrained = true
  MakeInternals = false
  MapMode = 5
  Placement = pos=(0,0,0) rot=(1,0,0;1.5708rad)
  sketch-geometry (14):
    g0: Circle CenterX=-5.6 CenterY=7.6 CenterZ=0 NormalX=0 NormalY=0 NormalZ=1 AngleXU=0 Radius=1.6
    g1: Circle CenterX=-5.6 CenterY=7.6 CenterZ=0 NormalX=0 NormalY=0 NormalZ=1 AngleXU=0 Radius=4
    g2: Circle CenterX=-5.6 CenterY=34.8 CenterZ=0 NormalX=0 NormalY=0 NormalZ=1 AngleXU=0 Radius=1.6
    g3: Circle CenterX=-5.6 CenterY=34.8 CenterZ=0 NormalX=0 NormalY=0 NormalZ=1 AngleXU=0 Radius=4
    g4: Circle CenterX=-184.08 CenterY=34.8 CenterZ=0 NormalX=0 NormalY=0 NormalZ=1 AngleXU=0 Radius=1.6
    g5: Circle CenterX=-184.08 CenterY=34.8 CenterZ=0 NormalX=0 NormalY=0 NormalZ=1 AngleXU=0 Radius=4
    g6: Circle CenterX=-179.305 CenterY=-76.8316 CenterZ=0 NormalX=0 NormalY=0 NormalZ=1 AngleXU=0 Radius=1.6
    g7: Circle CenterX=-179.305 CenterY=-76.8316 CenterZ=0 NormalX=0 NormalY=0 NormalZ=1 AngleXU=0 Radius=4
    g8: Circle CenterX=-213.443 CenterY=-76.8316 CenterZ=0 NormalX=0 NormalY=0 NormalZ=1 AngleXU=0 Radius=1.6
    g9: Circle CenterX=-213.443 CenterY=-76.8316 CenterZ=0 NormalX=0 NormalY=0 NormalZ=1 AngleXU=0 Radius=4
    g10: Circle CenterX=-78.51 CenterY=7.6 CenterZ=0 NormalX=0 NormalY=0 NormalZ=1 AngleXU=0 Radius=1.6
    g11: Circle CenterX=-78.51 CenterY=7.6 CenterZ=0 NormalX=0 NormalY=0 NormalZ=1 AngleXU=0 Radius=4
    g12: Circle CenterX=-78.51 CenterY=34.8 CenterZ=0 NormalX=0 NormalY=0 NormalZ=1 AngleXU=0 Radius=1.6
    g13: Circle CenterX=-78.51 CenterY=34.8 CenterZ=0 NormalX=0 NormalY=0 NormalZ=1 AngleXU=0 Radius=4
  constraints (35):
    c: Diameter(g0) = 3.2
    c: Diameter(g1) = 8
    c: Coincident(g0,g1)
    c: Diameter(g2) = 3.2
    c: Diameter(g3) = 8
    c: Coincident(g3,g2)
    c: Tangent(g2,g-7)
    c: Diameter(g4) = 3.2
    c: Diameter(g5) = 8
    c: Coincident(g5,g4)
    c: Tangent(g4,g-7)
    c: Tangent(g4,g-8)
    c: Diameter(g6) = 3.2
    c: Diameter(g7) = 8
    c: Coincident(g7,g6)
    c: Tangent(g6,g-9)
    c: Tangent(g6,g-10)
    c: Diameter(g8) = 3.2
    c: Diameter(g9) = 8
    c: Coincident(g9,g8)
    c: Tangent(g8,g-10)
    c: Tangent(g8,g-11)
    c: Diameter(g10) = 3.2
    c: Diameter(g11) = 8
    c: Diameter(g12) = 3.2
    c: Diameter(g13) = 8
    c: Coincident(g12,g13)
    c: Coincident(g10,g11)
    c: Tangent(g12,g-7)
    c: DistanceX(g12,g10) = 0
    c: Tangent(g2,g-6)
    c: Tangent(g0,g-6)
    c: Tangent(g0,g-3)
    c: Tangent(g10,g-3)
    c: Tangent(g10,g-4)
FEATURE [Part::Extrusion] Extrude012  label="extrude guide per coperture laterali"
  Base = -> Sketch016
  Dir = (0,-1,2e-16)
  DirMode = 2
  FaceMakerClass = Part::FaceMakerBullseye
  FaceMakerMode = 3
  LengthFwd = 25.2
  LengthRev = 0
  Solid = true
  Symmetric = true
FEATURE [Sketcher::SketchObject] Sketch017  label="supporto CAM"
  ArcFitTolerance = 1e-06
  AttachmentSupport = -> [XZ_Plane]
  ExternalGeometry = -> [Sketch]
  FullyConstrained = true
  MakeInternals = false
  MapMode = 5
  Placement = pos=(0,0,0) rot=(1,0,0;1.5708rad)
  sketch-geometry (6):
    g0: LineSegment StartX=-2.4 StartY=48 StartZ=0 EndX=-2.4 EndY=41.2 EndZ=0
    g1: LineSegment StartX=-2.4 StartY=48 StartZ=0 EndX=-34 EndY=48 EndZ=0
    g2: LineSegment StartX=-34 StartY=48 StartZ=0 EndX=-34 EndY=46.72 EndZ=0
    g3: LineSegment StartX=-34 StartY=46.72 StartZ=0 EndX=-36 EndY=46.72 EndZ=0
    g4: LineSegment StartX=-36 StartY=46.72 StartZ=0 EndX=-36 EndY=41.2 EndZ=0
    g5: LineSegment StartX=-36 StartY=41.2 StartZ=0 EndX=-2.4 EndY=41.2 EndZ=0
  constraints (15):
    c: Coincident(g1,g0)
    c: Horizontal(g1)
    c: Coincident(g2,g1)
    c: Vertical(g2)
    c: Coincident(g3,g2)
    c: Horizontal(g3)
    c: Coincident(g4,g3)
    c: Coincident(g5,g4)
    c: DistanceX(g1,g0) = 31.6
    c: Coincident(g5,g0)
    c: Vertical(g4)
    c: DistanceY(g2,g1) = 1.28
    c: Coincident(g0,g-3)
    c: Coincident(g0,g-3)
    c: Coincident(g4,g-4)
FEATURE [Part::Extrusion] Extrude013  label="Extrude supporto CAM"
  Base = -> Sketch017
  Dir = (0,-1,2e-16)
  DirMode = 2
  FaceMakerClass = Part::FaceMakerBullseye
  FaceMakerMode = 3
  LengthFwd = 17.8
  LengthRev = 0
  Solid = true
  Symmetric = true
FEATURE [Sketcher::SketchObject] Sketch018  label="Scavo CAM"
  ArcFitTolerance = 1e-06
  AttachmentSupport = -> [YZ_Plane]
  ExternalGeometry = -> [Sketch]
  FullyConstrained = true
  MakeInternals = false
  MapMode = 5
  Placement = pos=(0,0,0) rot=(0.57735,0.57735,0.57735;2.0944rad)
  sketch-geometry (4):
    g0: LineSegment StartX=-7.73 StartY=48 StartZ=0 EndX=7.73 EndY=48 EndZ=0
    g1: LineSegment [constr] StartX=1.07e-14 StartY=48 StartZ=0 EndX=0 EndY=43.5155 EndZ=0
    g2: ArcOfCircle CenterX=9e-15 CenterY=52.42 CenterZ=0 NormalX=0 NormalY=0 NormalZ=1 AngleXU=0 Radius=8.90445 StartAngle=3.66102 EndAngle=5.76376
    g3: Circle [constr] CenterX=9e-15 CenterY=52.42 CenterZ=0 NormalX=0 NormalY=0 NormalZ=1 AngleXU=0 Radius=8.9
  constraints (13):
    c: Horizontal(g0)
    c: DistanceY(g-3,g0) = 0
    c: DistanceX(g0,g0) = 15.46
    c: DistanceX(g0,g-3) = 7.73
    c: DistanceX(g-3) = 0
    c: Coincident(g1,g-3)
    c: PointOnObject(g1,g-2)
    c: Coincident(g2,g0)
    c: Coincident(g2,g0)
    c: PointOnObject(g1,g2)
    c: Diameter(g3) = 17.8
    c: DistanceY(g1,g3) = 4.42
    c: Coincident(g2,g3)
FEATURE [Part::Extrusion] Extrude014  label="Extrude Scavo CAM"
  Base = -> Sketch018
  Dir = (1,0,0)
  DirMode = 2
  FaceMakerClass = Part::FaceMakerBullseye
  FaceMakerMode = 3
  LengthFwd = -34
  LengthRev = 0
  Solid = true
  Symmetric = false
FEATURE [Sketcher::SketchObject] Sketch019  label="scavo rumble"
  ArcFitTolerance = 1e-06
  AttachmentSupport = -> [XZ_Plane]
  ExternalGeometry = -> [Sketch]
  FullyConstrained = true
  MakeInternals = false
  MapMode = 5
  Placement = pos=(0,0,0) rot=(1,0,0;1.5708rad)
  sketch-geometry (6):
    g0: LineSegment StartX=-169.087 StartY=-38.264 StartZ=0 EndX=-163.951 EndY=-39.9327 EndZ=0
    g1: LineSegment StartX=-163.951 StartY=-39.9327 StartZ=0 EndX=-171.058 EndY=-61.807 EndZ=0
    g2: LineSegment StartX=-171.058 StartY=-61.807 StartZ=0 EndX=-176.194 EndY=-60.1383 EndZ=0
    g3: LineSegment StartX=-176.194 StartY=-60.1383 StartZ=0 EndX=-169.087 EndY=-38.264 EndZ=0
    g4: LineSegment [constr] StartX=-145.51 StartY=22 StartZ=0 EndX=-165.472 EndY=-39.4383 EndZ=0
    g5: LineSegment [constr] StartX=-163.951 StartY=-39.9327 StartZ=0 EndX=-165.472 EndY=-39.4383 EndZ=0
  constraints (17):
    c: Coincident(g1,g0)
    c: Coincident(g2,g1)
    c: Coincident(g3,g2)
    c: Coincident(g3,g0)
    c: Parallel(g3,g-3)
    c: Parallel(g3,g1)
    c: Perpendicular(g3,g0)
    c: Perpendicular(g2,g3)
    c: Distance(g2,g0) = 23
    c: Parallel(g4,g-3)
    c: Distance(g4) = 64.6
    c: Coincident(g4,g-3)
    c: Parallel(g5,g0)
    c: Coincident(g5,g0)
    c: Coincident(g5,g4)
    c: Distance(g4,g0) = 3.8
    c: Distance(g4,g0) = 1.6
FEATURE [Part::Extrusion] Extrude015  label="scavo rumble001"
  Base = -> Sketch019
  Dir = (0,-1,2e-16)
  DirMode = 2
  FaceMakerClass = Part::FaceMakerBullseye
  FaceMakerMode = 3
  LengthFwd = 21
  LengthRev = 0
  Solid = true
  Symmetric = true
FEATURE [Sketcher::SketchObject] Sketch020  label="fermo rumble"
  ArcFitTolerance = 1e-06
  AttachmentSupport = -> [XZ_Plane]
  ExternalGeometry = -> [Sketch019,Sketch]
  FullyConstrained = true
  MakeInternals = false
  MapMode = 5
  Placement = pos=(0,0,0) rot=(1,0,0;1.5708rad)
  sketch-geometry (16):
    g0: LineSegment [constr] StartX=-171.22 StartY=-57.1279 StartZ=0 EndX=-172.58 EndY=-61.3126 EndZ=0
    g1: LineSegment [constr] StartX=-172.58 StartY=-61.3126 StartZ=0 EndX=-171.058 EndY=-61.807 EndZ=0
    g2: LineSegment StartX=-172.633 StartY=-54.3557 StartZ=0 EndX=-170.54 EndY=-55.0356 EndZ=0
    g3: LineSegment StartX=-170.54 StartY=-55.0356 StartZ=0 EndX=-171.22 EndY=-57.1279 EndZ=0
    g4: LineSegment StartX=-171.22 StartY=-57.1279 StartZ=0 EndX=-173.313 EndY=-56.4481 EndZ=0
    g5: LineSegment StartX=-173.313 StartY=-56.4481 StartZ=0 EndX=-172.633 EndY=-54.3557 EndZ=0
    g6: LineSegment StartX=-172.138 StartY=-52.8341 StartZ=0 EndX=-168.714 EndY=-53.9465 EndZ=0
    g7: LineSegment StartX=-168.714 StartY=-53.9465 StartZ=0 EndX=-170.321 EndY=-58.892 EndZ=0
    g8: LineSegment StartX=-170.321 StartY=-58.892 StartZ=0 EndX=-173.745 EndY=-57.7795 EndZ=0
    g9: LineSegment StartX=-174.772 StartY=-55.7634 StartZ=0 EndX=-174.154 EndY=-53.8613 EndZ=0
    g10: LineSegment [constr] StartX=-174.154 StartY=-53.8613 StartZ=0 EndX=-173.66 EndY=-52.3396 EndZ=0
    g11: LineSegment [constr] StartX=-173.66 StartY=-52.3396 StartZ=0 EndX=-172.138 EndY=-52.8341 EndZ=0
    g12: ArcOfCircle CenterX=-173.251 CenterY=-56.2579 CenterZ=0 NormalX=0 NormalY=0 NormalZ=1 AngleXU=0 Radius=1.6 StartAngle=2.82743 EndAngle=4.39823
    g13: GeomPoint [constr] X=-175.267 Y=-57.2851 Z=0
    g14: ArcOfCircle CenterX=-172.633 CenterY=-54.3557 CenterZ=0 NormalX=0 NormalY=0 NormalZ=1 AngleXU=0 Radius=1.6 StartAngle=1.25664 EndAngle=2.82743
    g15: GeomPoint [constr] X=-173.66 Y=-52.3396 Z=0
  constraints (42):
    c: Parallel(g0,g-4)
    c: Distance(g0) = 4.4
    c: Coincident(g1,g0)
    c: Perpendicular(g0,g1)
    c: Distance(g1) = 1.6
    c: Coincident(g1,g-5)
    c: Coincident(g3,g2)
    c: Coincident(g4,g3)
    c: Coincident(g5,g4)
    c: Coincident(g5,g2)
    c: Parallel(g3,g-4)
    c: Parallel(g3,g5)
    c: Perpendicular(g2,g3)
    c: Parallel(g4,g2)
    c: Distance(g2) = 2.2
    c: Distance(g3) = 2.2
    c: Coincident(g7,g6)
    c: Coincident(g8,g7)
    c: Parallel(g7,g-4)
    c: Parallel(g7,g9)
    c: Perpendicular(g6,g7)
    c: Parallel(g6,g8)
    c: Distance(g6,g15) = 5.2
    c: Distance(g7) = 5.2
    c: Coincident(g11,g10)
    c: Parallel(g10,g9)
    c: Parallel(g11,g6)
    c: Distance(g10) = 1.6
    c: Distance(g11) = 1.6
    c: Coincident(g10,g15)
    c: Distance(g11,g2) = 1.6
    c: Distance(g2,g10) = 1.6
    c: PointOnObject(g13,g8)
    c: PointOnObject(g13,g9)
    c: Tangent(g8,g12) = 1.5708
    c: Tangent(g9,g12) = 1.5708
    c: PointOnObject(g15,g9)
    c: Tangent(g6,g14) = 1.5708
    c: Tangent(g9,g14) = 1.5708
    c: Equal(g12,g14)
    c: Coincident(g6,g11)
    c: Coincident(g3,g0)
FEATURE [Part::Extrusion] Extrude016  label="Extrude fermo rumble"
  Base = -> Sketch020
  Dir = (0,-1,2e-16)
  DirMode = 2
  FaceMakerClass = Part::FaceMakerBullseye
  FaceMakerMode = 3
  LengthFwd = 25.2
  LengthRev = 0
  Solid = true
  Symmetric = true
FEATURE [Sketcher::SketchObject] Sketch021  label="perno fermo rumble001"
  ArcFitTolerance = 1e-06
  AttachmentSupport = -> [XZ_Plane001]
  FullyConstrained = true
  MakeInternals = false
  MapMode = 5
  Placement = pos=(0,0,0) rot=(1,0,0;1.5708rad)
  sketch-geometry (16):
    g0: LineSegment StartX=0 StartY=0.45 StartZ=0 EndX=0 EndY=1.55 EndZ=0
    g1: LineSegment StartX=0.45 StartY=2 StartZ=0 EndX=1.55 EndY=2 EndZ=0
    g2: LineSegment StartX=2 StartY=1.55 StartZ=0 EndX=2 EndY=0.45 EndZ=0
    g3: LineSegment StartX=1.55 StartY=0 StartZ=0 EndX=0.45 EndY=0 EndZ=0
    g4: ArcOfCircle [constr] CenterX=0.45 CenterY=1.55 CenterZ=0 NormalX=0 NormalY=0 NormalZ=1 AngleXU=0 Radius=0.45 StartAngle=1.5708 EndAngle=3.14159
    g5: GeomPoint [constr] X=0 Y=2 Z=0
    g6: LineSegment StartX=0.45 StartY=2 StartZ=0 EndX=0 EndY=1.55 EndZ=0
    g7: ArcOfCircle [constr] CenterX=1.55 CenterY=1.55 CenterZ=0 NormalX=0 NormalY=0 NormalZ=1 AngleXU=0 Radius=0.45 StartAngle=0 EndAngle=1.5708
    g8: GeomPoint [constr] X=2 Y=2 Z=0
    g9: LineSegment StartX=2 StartY=1.55 StartZ=0 EndX=1.55 EndY=2 EndZ=0
    g10: ArcOfCircle [constr] CenterX=1.55 CenterY=0.45 CenterZ=0 NormalX=0 NormalY=0 NormalZ=1 AngleXU=0 Radius=0.45 StartAngle=4.71239 EndAngle=6.28319
    g11: GeomPoint [constr] X=2 Y=0 Z=0
    g12: LineSegment StartX=1.55 StartY=0 StartZ=0 EndX=2 EndY=0.45 EndZ=0
    g13: ArcOfCircle [constr] CenterX=0.45 CenterY=0.45 CenterZ=0 NormalX=0 NormalY=0 NormalZ=1 AngleXU=0 Radius=0.45 StartAngle=3.14159 EndAngle=4.71239
    g14: GeomPoint [constr] X=0 Y=0 Z=0
    g15: LineSegment StartX=0 StartY=0.45 StartZ=0 EndX=0.45 EndY=0 EndZ=0
  constraints (35):
    c: Coincident(g14,g-1)
    c: PointOnObject(g5,g-2)
    c: Horizontal(g1)
    c: Vertical(g2)
    c: Horizontal(g3)
    c: DistanceX(g5,g8) = 2
    c: DistanceY(g11,g8) = 2
    c: PointOnObject(g5,g0)
    c: PointOnObject(g5,g1)
    c: Tangent(g0,g4) = 1.5708
    c: Tangent(g1,g4) = 1.5708
    c: Coincident(g6,g0)
    c: Coincident(g6,g1)
    c: PointOnObject(g8,g2)
    c: PointOnObject(g8,g1)
    c: Tangent(g2,g7) = 1.5708
    c: Tangent(g1,g7) = 1.5708
    c: Coincident(g9,g2)
    c: Coincident(g9,g1)
    c: PointOnObject(g11,g2)
    c: PointOnObject(g11,g3)
    c: Tangent(g2,g10) = 1.5708
    c: Tangent(g3,g10) = 1.5708
    c: Coincident(g12,g2)
    c: Coincident(g12,g3)
    c: PointOnObject(g14,g0)
    c: PointOnObject(g14,g3)
    c: Tangent(g0,g13) = 1.5708
    c: Tangent(g3,g13) = 1.5708
    c: Coincident(g15,g0)
    c: Coincident(g15,g3)
    c: Equal(g6,g9)
    c: Equal(g9,g12)
    c: Equal(g12,g15)
    c: DistanceX(g14,g3) = 0.45
FEATURE [Sketcher::SketchObject] Sketch022  label="fori per M3x5(OD)x6(L)"
  ArcFitTolerance = 1e-06
  AttachmentSupport = -> [XZ_Plane]
  ExternalGeometry = -> [Sketch016]
  FullyConstrained = true
  MakeInternals = false
  MapMode = 5
  Placement = pos=(0,0,0) rot=(1,0,0;1.5708rad)
  sketch-geometry (7):
    g0: Circle CenterX=-5.6 CenterY=34.8 CenterZ=0 NormalX=0 NormalY=0 NormalZ=1 AngleXU=0 Radius=2.5
    g1: Circle CenterX=-5.6 CenterY=7.6 CenterZ=0 NormalX=0 NormalY=0 NormalZ=1 AngleXU=0 Radius=2.5
    g2: Circle CenterX=-78.51 CenterY=34.8 CenterZ=0 NormalX=0 NormalY=0 NormalZ=1 AngleXU=0 Radius=2.5
    g3: Circle CenterX=-78.51 CenterY=7.6 CenterZ=0 NormalX=0 NormalY=0 NormalZ=1 AngleXU=0 Radius=2.5
    g4: Circle CenterX=-184.08 CenterY=34.8 CenterZ=0 NormalX=0 NormalY=0 NormalZ=1 AngleXU=0 Radius=2.5
    g5: Circle CenterX=-179.305 CenterY=-76.8316 CenterZ=0 NormalX=0 NormalY=0 NormalZ=1 AngleXU=0 Radius=2.5
    g6: Circle CenterX=-213.443 CenterY=-76.8316 CenterZ=0 NormalX=0 NormalY=0 NormalZ=1 AngleXU=0 Radius=2.5
  constraints (14):
    c: Diameter(g0) = 5
    c: Diameter(g1) = 5
    c: Diameter(g2) = 5
    c: Diameter(g3) = 5
    c: Diameter(g4) = 5
    c: Diameter(g5) = 5
    c: Diameter(g6) = 5
    c: Coincident(g0,g-8)
    c: Coincident(g1,g-9)
    c: Coincident(g2,g-6)
    c: Coincident(g3,g-7)
    c: Coincident(g4,g-5)
    c: Coincident(g5,g-4)
    c: Coincident(g6,g-3)
FEATURE [Part::Extrusion] Extrude018  label="Extrude fori M3x5x6 - dx"
  Base = -> Sketch022
  Dir = (0,-1,2e-16)
  DirMode = 2
  FaceMakerClass = Part::FaceMakerBullseye
  FaceMakerMode = 3
  LengthFwd = 6.2
  LengthRev = 0
  Placement = pos=(0,-9.5,0) rot=(0,0,1;0rad)
  Solid = true
  Symmetric = true
FEATURE [Part::Extrusion] Extrude019  label="Extrude fori M3x5x6 - sx"
  Base = -> Sketch022
  Dir = (0,-1,2e-16)
  DirMode = 2
  FaceMakerClass = Part::FaceMakerBullseye
  FaceMakerMode = 3
  LengthFwd = 6.2
  LengthRev = 0
  Placement = pos=(0,9.5,0) rot=(0,0,1;0rad)
  Solid = true
  Symmetric = true
FEATURE [Sketcher::SketchObject] Sketch023  label="foro anteriore M3x5x6"
  ArcFitTolerance = 1e-06
  AttachmentSupport = -> [YZ_Plane]
  FullyConstrained = true
  MakeInternals = false
  MapMode = 5
  Placement = pos=(0,0,0) rot=(0.57735,0.57735,0.57735;2.0944rad)
  sketch-geometry (2):
    g0: LineSegment [constr] StartX=0 StartY=0 StartZ=0 EndX=0 EndY=38.6 EndZ=0
    g1: Circle CenterX=0 CenterY=38.6 CenterZ=0 NormalX=0 NormalY=0 NormalZ=1 AngleXU=0 Radius=2.5
  constraints (5):
    c: Coincident(g0,g-1)
    c: PointOnObject(g0,g-2)
    c: DistanceY(g0,g0) = 38.6
    c: Diameter(g1) = 5
    c: Coincident(g1,g0)
FEATURE [Part::Extrusion] Extrude020  label="Extrude foro anteriore M3x5x6"
  Base = -> Sketch023
  Dir = (1,0,0)
  DirMode = 2
  FaceMakerClass = Part::FaceMakerBullseye
  FaceMakerMode = 3
  LengthFwd = -6.2
  LengthRev = 0
  Solid = true
  Symmetric = false
FEATURE [Sketcher::SketchObject] Sketch024  label="fori per viti frontale"
  ArcFitTolerance = 1e-06
  AttachmentSupport = -> [YZ_Plane]
  FullyConstrained = true
  MakeInternals = false
  MapMode = 5
  Placement = pos=(0,0,0) rot=(0.57735,0.57735,0.57735;2.0944rad)
  sketch-geometry (9):
    g0: LineSegment [constr] StartX=-10.3 StartY=30.721 StartZ=0 EndX=10.3 EndY=30.721 EndZ=0
    g1: LineSegment [constr] StartX=10.3 StartY=30.721 StartZ=0 EndX=10.3 EndY=10.121 EndZ=0
    g2: LineSegment [constr] StartX=10.3 StartY=10.121 StartZ=0 EndX=-10.3 EndY=10.121 EndZ=0
    g3: LineSegment [constr] StartX=-10.3 StartY=10.121 StartZ=0 EndX=-10.3 EndY=30.721 EndZ=0
    g4: LineSegment [constr] StartX=0 StartY=0 StartZ=0 EndX=0 EndY=10.121 EndZ=0
    g5: Circle CenterX=-10.3 CenterY=30.721 CenterZ=0 NormalX=0 NormalY=0 NormalZ=1 AngleXU=0 Radius=2
    g6: Circle CenterX=10.3 CenterY=30.721 CenterZ=0 NormalX=0 NormalY=0 NormalZ=1 AngleXU=0 Radius=2
    g7: Circle CenterX=-10.3 CenterY=10.121 CenterZ=0 NormalX=0 NormalY=0 NormalZ=1 AngleXU=0 Radius=2
    g8: Circle CenterX=10.3 CenterY=10.121 CenterZ=0 NormalX=0 NormalY=0 NormalZ=1 AngleXU=0 Radius=2
  constraints (22):
    c: Horizontal(g0)
    c: Coincident(g1,g0)
    c: Vertical(g1)
    c: Coincident(g2,g1)
    c: Horizontal(g2)
    c: Coincident(g3,g2)
    c: Coincident(g3,g0)
    c: Vertical(g3)
    c: DistanceX(g0,g0) = 20.6
    c: DistanceY(g3,g3) = 20.6
    c: Coincident(g4,g-1)
    c: PointOnObject(g4,g-2)
    c: DistanceY(g4,g4) = 10.121
    c: Symmetric(g2,g2,g4)
    c: Diameter(g5) = 4
    c: Diameter(g6) = 4
    c: Diameter(g7) = 4
    c: Diameter(g8) = 4
    c: Coincident(g5,g0)
    c: Coincident(g6,g0)
    c: Coincident(g7,g2)
    c: Coincident(g8,g1)
FEATURE [Part::Extrusion] Extrude021  label="Extrude fori per viti frontale"
  Base = -> Sketch024
  Dir = (1,0,0)
  DirMode = 2
  FaceMakerClass = Part::FaceMakerBullseye
  FaceMakerMode = 3
  LengthFwd = -2.4
  LengthRev = 0
  Solid = true
  Symmetric = false
FEATURE [Sketcher::SketchObject] Sketch025  label="foro per filo CAM"
  ArcFitTolerance = 1e-06
  AttachmentSupport = -> [XZ_Plane]
  ExternalGeometry = -> [Sketch]
  FullyConstrained = true
  MakeInternals = false
  MapMode = 5
  Placement = pos=(0,0,0) rot=(1,0,0;1.5708rad)
  sketch-geometry (4):
    g0: LineSegment StartX=-44.6 StartY=41.2 StartZ=0 EndX=-44.6 EndY=36.4 EndZ=0
    g1: LineSegment StartX=-44.6 StartY=36.4 StartZ=0 EndX=-54.6 EndY=36.4 EndZ=0
    g2: LineSegment StartX=-54.6 StartY=36.4 StartZ=0 EndX=-50.4 EndY=41.2 EndZ=0
    g3: LineSegment StartX=-50.4 StartY=41.2 StartZ=0 EndX=-44.6 EndY=41.2 EndZ=0
  constraints (11):
    c: Vertical(g0)
    c: Coincident(g1,g0)
    c: Horizontal(g1)
    c: Coincident(g2,g1)
    c: Coincident(g3,g2)
    c: Coincident(g3,g0)
    c: Horizontal(g3)
    c: Coincident(g0,g-3)
    c: DistanceY(g0,g-4) = 0
    c: DistanceX(g3,g3) = 5.8
    c: DistanceX(g1,g1) = 10
FEATURE [Part::Extrusion] Extrude022  label="Extrude foro per filo CAM dx"
  Base = -> Sketch025
  Dir = (0,-1,2e-16)
  DirMode = 2
  FaceMakerClass = Part::FaceMakerBullseye
  FaceMakerMode = 3
  LengthFwd = 4.9
  LengthRev = 0
  Placement = pos=(0,6.95,0) rot=(0,0,1;0rad)
  Solid = true
  Symmetric = true
FEATURE [Part::Extrusion] Extrude023  label="Extrude foro per filo CAM sx"
  Base = -> Sketch025
  Dir = (0,-1,2e-16)
  DirMode = 2
  FaceMakerClass = Part::FaceMakerBullseye
  FaceMakerMode = 3
  LengthFwd = 4.9
  LengthRev = 0
  Placement = pos=(0,-6.95,0) rot=(0,0,1;0rad)
  Solid = true
  Symmetric = true
FEATURE [Sketcher::SketchObject] Sketch026  label="foro sotto anteriore M3x5x6"
  ArcFitTolerance = 1e-06
  AttachmentSupport = -> [XY_Plane]
  FullyConstrained = true
  MakeInternals = false
  MapMode = 5
  sketch-geometry (2):
    g0: LineSegment [constr] StartX=0 StartY=0 StartZ=0 EndX=-16.5 EndY=0 EndZ=0
    g1: Circle CenterX=-16.5 CenterY=0 CenterZ=0 NormalX=0 NormalY=0 NormalZ=1 AngleXU=0 Radius=2.5
  constraints (5):
    c: Distance(g0) = 16.5
    c: Coincident(g0,g-1)
    c: PointOnObject(g0,g-1)
    c: Diameter(g1) = 5
    c: Coincident(g0,g1)
FEATURE [Sketcher::SketchObject] Sketch027  label="foro sotto posteriore M3x5x6"
  ArcFitTolerance = 1e-06
  AttachmentSupport = -> [XY_Plane]
  ExternalGeometry = -> [Sketch]
  FullyConstrained = true
  MakeInternals = false
  MapMode = 5
  sketch-geometry (2):
    g0: LineSegment [constr] StartX=-82.8 StartY=2e-16 StartZ=0 EndX=-71.3 EndY=2e-16 EndZ=0
    g1: Circle CenterX=-71.3 CenterY=2e-16 CenterZ=0 NormalX=0 NormalY=0 NormalZ=1 AngleXU=0 Radius=2.5
  constraints (5):
    c: Distance(g0) = 11.5
    c: Coincident(g0,g-3)
    c: PointOnObject(g0,g-3)
    c: Diameter(g1) = 5
    c: Coincident(g1,g0)
FEATURE [Sketcher::SketchObject] Sketch029  label="fori sotto impugnatura"
  ArcFitTolerance = 1e-06
  AttachmentSupport = -> [XY_Plane]
  ExternalGeometry = -> [Sketch]
  FullyConstrained = true
  MakeInternals = false
  MapMode = 5
  sketch-geometry (15):
    g0: LineSegment [constr] StartX=-175.232 StartY=-1.83e-14 StartZ=0 EndX=-191.232 EndY=0 EndZ=0
    g1: Circle CenterX=-191.232 CenterY=0 CenterZ=0 NormalX=0 NormalY=0 NormalZ=1 AngleXU=0 Radius=3.95
    g2: LineSegment [constr] StartX=-175.232 StartY=-1.83e-14 StartZ=0 EndX=-204.275 EndY=0 EndZ=0
    g3: LineSegment StartX=-204.275 StartY=3.525 StartZ=0 EndX=-204.275 EndY=-3.525 EndZ=0
    g4: LineSegment StartX=-205.4 StartY=-4.65 StartZ=0 EndX=-206.65 EndY=-4.65 EndZ=0
    g5: LineSegment StartX=-207.775 StartY=-3.525 StartZ=0 EndX=-207.775 EndY=3.525 EndZ=0
    g6: LineSegment StartX=-206.65 StartY=4.65 StartZ=0 EndX=-205.4 EndY=4.65 EndZ=0
    g7: ArcOfCircle CenterX=-206.65 CenterY=3.525 CenterZ=0 NormalX=0 NormalY=0 NormalZ=1 AngleXU=0 Radius=1.125 StartAngle=1.5708 EndAngle=3.14159
    g8: GeomPoint [constr] X=-207.775 Y=4.65 Z=0
    g9: ArcOfCircle CenterX=-205.4 CenterY=3.525 CenterZ=0 NormalX=0 NormalY=0 NormalZ=1 AngleXU=0 Radius=1.125 StartAngle=0 EndAngle=1.5708
    g10: GeomPoint [constr] X=-204.275 Y=4.65 Z=0
    g11: ArcOfCircle CenterX=-205.4 CenterY=-3.525 CenterZ=0 NormalX=0 NormalY=0 NormalZ=1 AngleXU=0 Radius=1.125 StartAngle=4.71239 EndAngle=6.28319
    g12: GeomPoint [constr] X=-204.275 Y=-4.65 Z=0
    g13: ArcOfCircle CenterX=-206.65 CenterY=-3.525 CenterZ=0 NormalX=0 NormalY=0 NormalZ=1 AngleXU=0 Radius=1.125 StartAngle=3.14159 EndAngle=4.71239
    g14: GeomPoint [constr] X=-207.775 Y=-4.65 Z=0
  constraints (35):
    c: Distance(g0) = 16
    c: Coincident(g0,g-3)
    c: PointOnObject(g0,g-1)
    c: Diameter(g1) = 7.9
    c: Coincident(g1,g0)
    c: Coincident(g2,g0)
    c: PointOnObject(g2,g-1)
    c: Vertical(g3)
    c: Horizontal(g4)
    c: Vertical(g5)
    c: Horizontal(g6)
    c: DistanceY(g12,g10) = 9.3
    c: DistanceX(g8,g10) = 3.5
    c: Symmetric(g10,g12,g2)
    c: PointOnObject(g8,g5)
    c: PointOnObject(g8,g6)
    c: Tangent(g5,g7) = 1.5708
    c: Tangent(g6,g7) = 1.5708
    c: PointOnObject(g10,g3)
    c: PointOnObject(g10,g6)
    c: Tangent(g3,g9) = 1.5708
    c: Tangent(g6,g9) = 1.5708
    c: PointOnObject(g12,g3)
    c: PointOnObject(g12,g4)
    c: Tangent(g3,g11) = 1.5708
    c: Tangent(g4,g11) = 1.5708
    c: PointOnObject(g14,g4)
    c: PointOnObject(g14,g5)
    c: Tangent(g4,g13) = 1.5708
    c: Tangent(g5,g13) = 1.5708
    c: Equal(g7,g9)
    c: Equal(g9,g11)
    c: Equal(g11,g13)
    c: DistanceX(g6,g6) = 1.25
    c: DistanceX(g-5,g5) = 6.8
FEATURE [Sketcher::SketchObject] Sketch030  label="fori superiori per solenoide e oled"
  ArcFitTolerance = 1e-06
  AttachmentSupport = -> [XY_Plane]
  ExternalGeometry = -> [Sketch]
  FullyConstrained = true
  MakeInternals = false
  MapMode = 5
  sketch-geometry (33):
    g0: LineSegment [constr] StartX=-181.6 StartY=1.12e-14 StartZ=0 EndX=-169.91 EndY=0 EndZ=0
    g1: LineSegment [constr] StartX=-169.91 StartY=0 StartZ=0 EndX=-169.91 EndY=-2.6 EndZ=0
    g2: LineSegment [constr] StartX=-169.91 StartY=0 StartZ=0 EndX=-169.91 EndY=2.6 EndZ=0
    g3: LineSegment StartX=-169.91 StartY=4.975 StartZ=0 EndX=-169.91 EndY=8.225 EndZ=0
    g4: LineSegment StartX=-167.535 StartY=10.6 StartZ=0 EndX=-167.285 EndY=10.6 EndZ=0
    g5: LineSegment StartX=-164.91 StartY=8.225 StartZ=0 EndX=-164.91 EndY=4.975 EndZ=0
    g6: LineSegment StartX=-167.285 StartY=2.6 StartZ=0 EndX=-167.535 EndY=2.6 EndZ=0
    g7: LineSegment StartX=-169.91 StartY=-4.975 StartZ=0 EndX=-169.91 EndY=-8.225 EndZ=0
    g8: LineSegment StartX=-167.535 StartY=-10.6 StartZ=0 EndX=-167.285 EndY=-10.6 EndZ=0
    g9: LineSegment StartX=-164.91 StartY=-8.225 StartZ=0 EndX=-164.91 EndY=-4.975 EndZ=0
    g10: LineSegment StartX=-167.285 StartY=-2.6 StartZ=0 EndX=-167.535 EndY=-2.6 EndZ=0
    g11: ArcOfCircle CenterX=-167.535 CenterY=8.225 CenterZ=0 NormalX=0 NormalY=0 NormalZ=1 AngleXU=0 Radius=2.375 StartAngle=1.5708 EndAngle=3.14159
    g12: GeomPoint [constr] X=-169.91 Y=10.6 Z=0
    g13: ArcOfCircle CenterX=-167.285 CenterY=8.225 CenterZ=0 NormalX=0 NormalY=0 NormalZ=1 AngleXU=0 Radius=2.375 StartAngle=0 EndAngle=1.5708
    g14: GeomPoint [constr] X=-164.91 Y=10.6 Z=0
    g15: ArcOfCircle CenterX=-167.285 CenterY=4.975 CenterZ=0 NormalX=0 NormalY=0 NormalZ=1 AngleXU=0 Radius=2.375 StartAngle=4.71239 EndAngle=6.28319
    g16: GeomPoint [constr] X=-164.91 Y=2.6 Z=0
    g17: ArcOfCircle CenterX=-167.535 CenterY=4.975 CenterZ=0 NormalX=0 NormalY=0 NormalZ=1 AngleXU=0 Radius=2.375 StartAngle=3.14159 EndAngle=4.71239
    g18: GeomPoint [constr] X=-169.91 Y=2.6 Z=0
    g19: ArcOfCircle CenterX=-167.535 CenterY=-4.975 CenterZ=0 NormalX=0 NormalY=0 NormalZ=1 AngleXU=0 Radius=2.375 StartAngle=1.5708 EndAngle=3.14159
    g20: GeomPoint [constr] X=-169.91 Y=-2.6 Z=0
    g21: ArcOfCircle CenterX=-167.285 CenterY=-4.975 CenterZ=0 NormalX=0 NormalY=0 NormalZ=1 AngleXU=0 Radius=2.375 StartAngle=0 EndAngle=1.5708
    g22: GeomPoint [constr] X=-164.91 Y=-2.6 Z=0
    g23: ArcOfCircle CenterX=-167.285 CenterY=-8.225 CenterZ=0 NormalX=0 NormalY=0 NormalZ=1 AngleXU=0 Radius=2.375 StartAngle=4.71239 EndAngle=6.28319
    g24: GeomPoint [constr] X=-164.91 Y=-10.6 Z=0
    g25: ArcOfCircle CenterX=-167.535 CenterY=-8.225 CenterZ=0 NormalX=0 NormalY=0 NormalZ=1 AngleXU=0 Radius=2.375 StartAngle=3.14159 EndAngle=4.71239
    g26: GeomPoint [constr] X=-169.91 Y=-10.6 Z=0
    g27: LineSegment [constr] StartX=-181.6 StartY=1.12e-14 StartZ=0 EndX=-152.209 EndY=0 EndZ=0
    g28: LineSegment [constr] StartX=-181.6 StartY=1.12e-14 StartZ=0 EndX=-130.41 EndY=0 EndZ=0
    g29: LineSegment [constr] StartX=-152.209 StartY=0 StartZ=0 EndX=-152.209 EndY=6.95 EndZ=0
    g30: LineSegment [constr] StartX=-130.41 StartY=0 StartZ=0 EndX=-130.41 EndY=-6.95 EndZ=0
    g31: Circle CenterX=-152.209 CenterY=6.95 CenterZ=0 NormalX=0 NormalY=0 NormalZ=1 AngleXU=0 Radius=2.1
    g32: Circle CenterX=-130.41 CenterY=-6.95 CenterZ=0 NormalX=0 NormalY=0 NormalZ=1 AngleXU=0 Radius=2.1
  constraints (79):
    c: Distance(g0) = 11.69
    c: PointOnObject(g0,g-1)
    c: Coincident(g-4,g0)
    c: Distance(g1) = 2.6
    c: Coincident(g1,g0)
    c: Vertical(g1)
    c: Distance(g2) = 2.6
    c: Coincident(g2,g0)
    c: Vertical(g2)
    c: Distance(g18,g12) = 8
    c: Coincident(g18,g2)
    c: Vertical(g3)
    c: Distance(g14,g12) = 5
    c: Horizontal(g4)
    c: Distance(g16,g14) = 8
    c: Vertical(g5)
    c: Distance(g26,g20) = 8
    c: Coincident(g20,g1)
    c: Vertical(g7)
    c: Distance(g26,g24) = 5
    c: Horizontal(g8)
    c: Distance(g24,g22) = 8
    c: Vertical(g9)
    c: PointOnObject(g12,g3)
    c: PointOnObject(g12,g4)
    c: Tangent(g3,g11) = 1.5708
    c: Tangent(g4,g11) = 1.5708
    c: PointOnObject(g14,g5)
    c: PointOnObject(g14,g4)
    c: Tangent(g5,g13) = 1.5708
    c: Tangent(g4,g13) = 1.5708
    c: PointOnObject(g16,g5)
    c: PointOnObject(g16,g6)
    c: Tangent(g5,g15) = 1.5708
    c: Tangent(g6,g15) = 1.5708
    c: PointOnObject(g18,g3)
    c: PointOnObject(g18,g6)
    c: Tangent(g3,g17) = 1.5708
    c: Tangent(g6,g17) = 1.5708
    c: Equal(g11,g13)
    c: Equal(g13,g15)
    c: Equal(g15,g17)
    c: DistanceX(g4,g4) = 0.25
    c: PointOnObject(g20,g7)
    c: PointOnObject(g20,g10)
    c: Tangent(g7,g19) = -1.5708
    c: Tangent(g10,g19) = -1.5708
    c: PointOnObject(g22,g9)
    c: PointOnObject(g22,g10)
    c: Tangent(g9,g21) = -1.5708
    c: Tangent(g10,g21) = -1.5708
    c: PointOnObject(g24,g9)
    c: PointOnObject(g24,g8)
    c: Tangent(g9,g23) = -1.5708
    c: Tangent(g8,g23) = -1.5708
    c: PointOnObject(g26,g8)
    c: PointOnObject(g26,g7)
    c: Tangent(g8,g25) = -1.5708
    c: Tangent(g7,g25) = -1.5708
    c: Equal(g19,g21)
    c: Equal(g21,g23)
    c: Equal(g23,g25)
    c: DistanceX(g10,g10) = 0.25
    c: Distance(g27) = 29.391
    c: Coincident(g27,g0)
    c: PointOnObject(g27,g-1)
    c: Distance(g28) = 51.19
    c: Coincident(g28,g0)
    c: PointOnObject(g28,g-1)
    c: Distance(g29) = 6.95
    c: Coincident(g29,g27)
    c: Vertical(g29)
    c: Distance(g30) = 6.95
    c: Coincident(g30,g28)
    c: Vertical(g30)
    c: Diameter(g31) = 4.2
    c: Diameter(g32) = 4.2
    c: Coincident(g32,g30)
    c: Coincident(g31,g29)
FEATURE [Sketcher::SketchObject] Sketch031  label="fori inferiori switch pompa"
  ArcFitTolerance = 1e-06
  AttachmentSupport = -> [XY_Plane]
  ExternalGeometry = -> [Sketch]
  FullyConstrained = true
  MakeInternals = false
  MapMode = 5
  sketch-geometry (4):
    g0: LineSegment [constr] StartX=-57.2 StartY=1.9e-15 StartZ=0 EndX=-62.45 EndY=1.9e-15 EndZ=0
    g1: LineSegment [constr] StartX=-62.45 StartY=3.25 StartZ=0 EndX=-62.45 EndY=-3.25 EndZ=0
    g2: Circle CenterX=-62.45 CenterY=3.25 CenterZ=0 NormalX=0 NormalY=0 NormalZ=1 AngleXU=0 Radius=1.6
    g3: Circle CenterX=-62.45 CenterY=-3.25 CenterZ=0 NormalX=0 NormalY=0 NormalZ=1 AngleXU=0 Radius=1.6
  constraints (10):
    c: Distance(g0) = 5.25
    c: Coincident(g0,g-3)
    c: PointOnObject(g0,g-3)
    c: Vertical(g1)
    c: DistanceY(g1,g1) = 6.5
    c: Symmetric(g1,g1,g0)
    c: Diameter(g2) = 3.2
    c: Diameter(g3) = 3.2
    c: Coincident(g2,g1)
    c: Coincident(g3,g1)
FEATURE [Sketcher::SketchObject] Sketch032  label="spazio per PILA 18650"
  ArcFitTolerance = 1e-06
  AttachmentSupport = -> [XY_Plane]
  ExternalGeometry = -> [Sketch]
  FullyConstrained = true
  MakeInternals = false
  MapMode = 5
  sketch-geometry (2):
    g0: LineSegment [constr] StartX=-178.142 StartY=-1.74e-14 StartZ=0 EndX=-191.142 EndY=-1.83e-14 EndZ=0
    g1: Circle CenterX=-191.142 CenterY=-1.83e-14 CenterZ=0 NormalX=0 NormalY=0 NormalZ=1 AngleXU=0 Radius=10.5
  constraints (5):
    c: Distance(g0) = 13
    c: Coincident(g0,g-3)
    c: PointOnObject(g0,g-4)
    c: Diameter(g1) = 21
    c: Coincident(g1,g0)
FEATURE [Part::Extrusion] Extrude030  label="Extrude spazio per PILA 18650"
  Base = -> Sketch032
  Dir = (0,0,1)
  DirLink = -> Sketch [Edge45]
  DirMode = 2
  FaceMakerClass = Part::FaceMakerBullseye
  FaceMakerMode = 3
  LengthFwd = 76
  LengthRev = 0
  Placement = pos=(6,0,-72) rot=(0,0,1;0rad)
  Solid = true
  Symmetric = false
FEATURE [Sketcher::SketchObject] Sketch033  label="fermo per scheda micro"
  ArcFitTolerance = 1e-06
  AttachmentSupport = -> [XZ_Plane]
  ExternalGeometry = -> [Sketch]
  FullyConstrained = true
  MakeInternals = false
  MapMode = 5
  Placement = pos=(0,0,0) rot=(1,0,0;1.5708rad)
  sketch-geometry (12):
    g0: LineSegment StartX=-11.6 StartY=6 StartZ=0 EndX=-4 EndY=6 EndZ=0
    g1: LineSegment StartX=-4 StartY=6 StartZ=0 EndX=-4 EndY=36.4 EndZ=0
    g2: LineSegment StartX=-4 StartY=36.4 StartZ=0 EndX=-11.6 EndY=36.4 EndZ=0
    g3: LineSegment StartX=-11.6 StartY=36.4 StartZ=0 EndX=-11.6 EndY=6 EndZ=0
    g4: LineSegment StartX=-80.11 StartY=11.6 StartZ=0 EndX=-70.51 EndY=11.6 EndZ=0
    g5: LineSegment StartX=-70.51 StartY=11.6 StartZ=0 EndX=-70.51 EndY=6 EndZ=0
    g6: LineSegment StartX=-70.51 StartY=6 StartZ=0 EndX=-80.11 EndY=6 EndZ=0
    g7: LineSegment StartX=-80.11 StartY=6 StartZ=0 EndX=-80.11 EndY=11.6 EndZ=0
    g8: LineSegment StartX=-78.51 StartY=36.4 StartZ=0 EndX=-70.51 EndY=36.4 EndZ=0
    g9: LineSegment StartX=-70.51 StartY=36.4 StartZ=0 EndX=-70.51 EndY=30.8 EndZ=0
    g10: LineSegment StartX=-70.51 StartY=30.8 StartZ=0 EndX=-78.51 EndY=30.8 EndZ=0
    g11: LineSegment StartX=-78.51 StartY=30.8 StartZ=0 EndX=-78.51 EndY=36.4 EndZ=0
  constraints (33):
    c: Horizontal(g0)
    c: Coincident(g1,g0)
    c: Coincident(g2,g1)
    c: Horizontal(g2)
    c: Coincident(g3,g2)
    c: Coincident(g3,g0)
    c: Vertical(g3)
    c: DistanceX(g2,g2) = 7.6
    c: Coincident(g1,g-3)
    c: Coincident(g0,g-3)
    c: Horizontal(g4)
    c: Coincident(g5,g4)
    c: Vertical(g5)
    c: Coincident(g6,g5)
    c: Horizontal(g6)
    c: Coincident(g7,g6)
    c: Coincident(g7,g4)
    c: Vertical(g7)
    c: DistanceY(g5,g5) = 5.6
    c: DistanceX(g4,g4) = 9.6
    c: Coincident(g9,g8)
    c: Vertical(g9)
    c: Coincident(g10,g9)
    c: Horizontal(g10)
    c: Coincident(g11,g10)
    c: Coincident(g11,g8)
    c: Vertical(g11)
    c: DistanceY(g9,g9) = 5.6
    c: DistanceX(g10,g10) = 8
    c: Coincident(g4,g-4)
    c: DistanceX(g4,g10) = 1.6
    c: Horizontal(g8)
    c: DistanceY(g8,g1) = 0
FEATURE [Sketcher::SketchObject] Sketch034  label="buchi guida rail"
  ArcFitTolerance = 1e-06
  AttachmentSupport = -> [XY_Plane]
  ExternalGeometry = -> [Sketch]
  FullyConstrained = true
  MakeInternals = false
  MapMode = 5
  sketch-geometry (6):
    g0: LineSegment [constr] StartX=-100.8 StartY=9.1e-15 StartZ=0 EndX=-93.3 EndY=0 EndZ=0
    g1: LineSegment [constr] StartX=-93.3 StartY=0 StartZ=0 EndX=-73.3 EndY=0 EndZ=0
    g2: LineSegment [constr] StartX=-73.3 StartY=0 StartZ=0 EndX=-53.3 EndY=0 EndZ=0
    g3: Circle CenterX=-93.3 CenterY=0 CenterZ=0 NormalX=0 NormalY=0 NormalZ=1 AngleXU=0 Radius=2.5
    g4: Circle CenterX=-73.3 CenterY=0 CenterZ=0 NormalX=0 NormalY=0 NormalZ=1 AngleXU=0 Radius=2.5
    g5: Circle CenterX=-53.3 CenterY=0 CenterZ=0 NormalX=0 NormalY=0 NormalZ=1 AngleXU=0 Radius=2.5
  constraints (15):
    c: Distance(g0) = 7.5
    c: Coincident(g0,g-3)
    c: PointOnObject(g0,g-1)
    c: Distance(g1) = 20
    c: Coincident(g1,g0)
    c: PointOnObject(g1,g-1)
    c: Distance(g2) = 20
    c: Coincident(g2,g1)
    c: PointOnObject(g2,g-1)
    c: Diameter(g3) = 5
    c: Diameter(g4) = 5
    c: Diameter(g5) = 5
    c: Coincident(g3,g0)
    c: Coincident(g4,g1)
    c: Coincident(g5,g2)
FEATURE [Part::Extrusion] Extrude032  label="Extrude buchi guida rail"
  Base = -> Sketch034
  Dir = (0,0,1)
  DirMode = 2
  FaceMakerClass = Part::FaceMakerBullseye
  FaceMakerMode = 3
  LengthFwd = -6.2
  LengthRev = 0
  Placement = pos=(0,0,43.2) rot=(0,0,1;0rad)
  Solid = true
  Symmetric = false
FEATURE [Part::Extrusion] Extrude033  label="Extrude fori superiori per solenoide e oled001"
  Base = -> Sketch030
  Dir = (0,0,1)
  DirMode = 2
  FaceMakerClass = Part::FaceMakerBullseye
  FaceMakerMode = 3
  LengthFwd = -4.8
  LengthRev = 0
  Placement = pos=(0,0,41.2) rot=(0,0,1;0rad)
  Solid = true
  Symmetric = false
FEATURE [Part::Extrusion] Extrude034  label="Extrude fori sotto impugnatura001"
  Base = -> Sketch029
  Dir = (0,0,1)
  DirMode = 2
  FaceMakerClass = Part::FaceMakerBullseye
  FaceMakerMode = 3
  LengthFwd = 5
  LengthRev = 0
  Placement = pos=(0,0,-83) rot=(0,0,1;0rad)
  Solid = true
  Symmetric = false
FEATURE [Part::Extrusion] Extrude035  label="Extrude fori inferiori switch pompa001"
  Base = -> Sketch031
  Dir = (0,0,1)
  DirMode = 2
  FaceMakerClass = Part::FaceMakerBullseye
  FaceMakerMode = 3
  LengthFwd = 4
  LengthRev = 0
  Placement = pos=(0,0,-1.7) rot=(0,0,1;0rad)
  Solid = true
  Symmetric = false
FEATURE [Part::Extrusion] Extrude036  label="Extrude foro sotto posteriore M3x5x007"
  Base = -> Sketch027
  Dir = (0,0,1)
  DirMode = 2
  FaceMakerClass = Part::FaceMakerBullseye
  FaceMakerMode = 3
  LengthFwd = 6.2
  LengthRev = 0
  Placement = pos=(0,0,-9.6) rot=(0,0,1;0rad)
  Solid = true
  Symmetric = false
FEATURE [Part::Extrusion] Extrude037  label="Extrude foro sotto anteriore M3x5x007"
  Base = -> Sketch026
  Dir = (0,0,1)
  DirMode = 2
  FaceMakerClass = Part::FaceMakerBullseye
  FaceMakerMode = 3
  LengthFwd = 6.2
  LengthRev = 0
  Solid = true
  Symmetric = false
FEATURE [Sketcher::SketchObject] Sketch035  label="foro per fissaggio micro"
  ArcFitTolerance = 1e-06
  AttachmentSupport = -> [XZ_Plane]
  ExternalGeometry = -> [Sketch,Sketch033]
  FullyConstrained = true
  MakeInternals = false
  MapMode = 5
  Placement = pos=(0,0,0) rot=(1,0,0;1.5708rad)
  sketch-geometry (3):
    g0: Circle CenterX=-7.8 CenterY=21.2 CenterZ=0 NormalX=0 NormalY=0 NormalZ=1 AngleXU=0 Radius=1.6
    g1: GeomPoint [constr] X=-4 Y=21.2 Z=0
    g2: LineSegment [constr] StartX=-4 StartY=21.2 StartZ=0 EndX=-11.6 EndY=21.2 EndZ=0
  constraints (6):
    c: Diameter(g0) = 3.2
    c: Symmetric(g-3,g-3,g1)
    c: Coincident(g2,g1)
    c: Horizontal(g2)
    c: DistanceX(g-4,g2) = 0
    c: Symmetric(g2,g1,g0)
FEATURE [Part::Extrusion] Extrude038  label="Extrude foro per fissaggio micro"
  Base = -> Sketch035
  Dir = (0,-1,2e-16)
  DirMode = 2
  FaceMakerClass = Part::FaceMakerBullseye
  FaceMakerMode = 3
  LengthFwd = 3
  LengthRev = 0
  Placement = pos=(0,8.6,0) rot=(0,0,1;0rad)
  Solid = true
  Symmetric = false
FEATURE [Sketcher::SketchObject] Sketch036  label="supporto per alimentatore"
  ArcFitTolerance = 1e-06
  AttachmentSupport = -> [XZ_Plane]
  ExternalGeometry = -> [Sketch,Sketch016,Sketch022]
  FullyConstrained = true
  MakeInternals = false
  MapMode = 5
  Placement = pos=(0,0,0) rot=(1,0,0;1.5708rad)
  sketch-geometry (5):
    g0: LineSegment StartX=-211.843 StartY=-50.0944 StartZ=0 EndX=-211.843 EndY=-80.4316 EndZ=0
    g1: LineSegment StartX=-211.843 StartY=-50.0944 StartZ=0 EndX=-207.775 EndY=-41.3701 EndZ=0
    g2: LineSegment [constr] StartX=-209.443 StartY=-50.0944 StartZ=0 EndX=-209.443 EndY=-80.4316 EndZ=0
    g3: LineSegment StartX=-207.775 StartY=-41.3701 StartZ=0 EndX=-207.775 EndY=-80.4316 EndZ=0
    g4: LineSegment StartX=-211.843 StartY=-80.4316 StartZ=0 EndX=-207.775 EndY=-80.4316 EndZ=0
  constraints (15):
    c: Vertical(g0)
    c: Coincident(g1,g0)
    c: Vertical(g2)
    c: Tangent(g2,g-5)
    c: Coincident(g3,g1)
    c: Vertical(g3)
    c: DistanceY(g-3,g3) = -2
    c: Tangent(g1,g-8)
    c: DistanceY(g-3,g0) = -2
    c: Coincident(g4,g0)
    c: Coincident(g4,g3)
    c: Tangent(g0,g-6)
    c: DistanceY(g-3,g2) = -2
    c: DistanceY(g2,g0) = 0
    c: DistanceX(g-3,g3) = 6.8
FEATURE [Part::Extrusion] Extrude039  label="Extrude039 supporto alimentatore"
  Base = -> Sketch036
  Dir = (0,-1,2e-16)
  DirMode = 2
  FaceMakerClass = Part::FaceMakerBullseye
  FaceMakerMode = 3
  LengthFwd = 25.2
  LengthRev = 0
  Solid = true
  Symmetric = true
FEATURE [Sketcher::SketchObject] Sketch037  label="scavo per alimentatore"
  ArcFitTolerance = 1e-06
  AttachmentSupport = -> [XZ_Plane]
  ExternalGeometry = -> [Sketch036]
  FullyConstrained = true
  MakeInternals = false
  MapMode = 5
  Placement = pos=(0,0,0) rot=(1,0,0;1.5708rad)
  sketch-geometry (4):
    g0: LineSegment StartX=-209.575 StartY=-50.4316 StartZ=0 EndX=-209.575 EndY=-80.4316 EndZ=0
    g1: LineSegment StartX=-209.575 StartY=-50.4316 StartZ=0 EndX=-207.775 EndY=-50.4316 EndZ=0
    g2: LineSegment StartX=-207.775 StartY=-50.4316 StartZ=0 EndX=-207.775 EndY=-80.4316 EndZ=0
    g3: LineSegment StartX=-207.775 StartY=-80.4316 StartZ=0 EndX=-209.575 EndY=-80.4316 EndZ=0
  constraints (11):
    c: Vertical(g0)
    c: Coincident(g1,g0)
    c: Horizontal(g1)
    c: Coincident(g2,g1)
    c: Vertical(g2)
    c: Coincident(g3,g2)
    c: Coincident(g3,g0)
    c: Horizontal(g3)
    c: DistanceX(g1,g1) = 1.8
    c: Coincident(g2,g-3)
    c: DistanceY(g2,g2) = 30
FEATURE [Part::Extrusion] Extrude040  label="Extrude040 scavo alimentatore"
  Base = -> Sketch037
  Dir = (0,-1,2e-16)
  DirMode = 2
  FaceMakerClass = Part::FaceMakerBullseye
  FaceMakerMode = 3
  LengthFwd = 19.5
  LengthRev = 0
  Solid = true
  Symmetric = true
FEATURE [Part::Extrusion] Extrude031  label="Extrude fermo per scheda micro"
  Base = -> Sketch033
  Dir = (0,-1,2e-16)
  DirMode = 2
  FaceMakerClass = Part::FaceMakerBullseye
  FaceMakerMode = 3
  LengthFwd = 3
  LengthRev = 0
  Placement = pos=(0,8.6,0) rot=(0,0,1;0rad)
  Solid = true
  Symmetric = false
FEATURE [Sketcher::SketchObject] Sketch038  label="scavo driver solenoide"
  ArcFitTolerance = 1e-06
  AttachmentSupport = -> [XZ_Plane]
  ExternalGeometry = -> [Sketch,Sketch036]
  FullyConstrained = true
  MakeInternals = false
  MapMode = 5
  Placement = pos=(0,0,0) rot=(1,0,0;1.5708rad)
  sketch-geometry (7):
    g0: LineSegment StartX=-192.222 StartY=-8.0175 StartZ=0 EndX=-194.941 EndY=-6.74965 EndZ=0
    g1: LineSegment StartX=-194.941 StartY=-6.74965 StartZ=0 EndX=-212.269 EndY=-43.9083 EndZ=0
    g2: LineSegment StartX=-192.222 StartY=-8.0175 StartZ=0 EndX=-188.779 EndY=-9.62345 EndZ=0
    g3: LineSegment StartX=-188.779 StartY=-9.62345 StartZ=0 EndX=-205.357 EndY=-45.1761 EndZ=0
    g4: LineSegment StartX=-205.357 StartY=-45.1761 StartZ=0 EndX=-209.55 EndY=-45.1761 EndZ=0
    g5: LineSegment [constr] StartX=-212.269 StartY=-43.9083 StartZ=0 EndX=-209.55 EndY=-45.1761 EndZ=0
    g6: LineSegment StartX=-212.269 StartY=-43.9083 StartZ=0 EndX=-209.55 EndY=-45.1761 EndZ=0
  constraints (20):
    c: Coincident(g1,g0)
    c: Coincident(g3,g2)
    c: Coincident(g4,g3)
    c: Distance(g2) = 3.8
    c: Distance(g1) = 41
    c: Coincident(g5,g1)
    c: Distance(g5) = 3
    c: Perpendicular(g5,g-3)
    c: Parallel(g1,g-3)
    c: Perpendicular(g1,g0)
    c: Distance(g0) = 3
    c: Coincident(g6,g1)
    c: Parallel(g3,g-3)
    c: Perpendicular(g2,g3)
    c: Coincident(g2,g0)
    c: Perpendicular(g-4,g4)
    c: PointOnObject(g5,g-3)
    c: Distance(g-3,g5) = 9.6
    c: Coincident(g4,g5)
    c: Coincident(g6,g4)
FEATURE [Part::Extrusion] Extrude041  label="Extrude scavo driver solenoide"
  Base = -> Sketch038
  Dir = (0,-1,2e-16)
  DirMode = 2
  FaceMakerClass = Part::FaceMakerBullseye
  FaceMakerMode = 3
  LengthFwd = 20.6
  LengthRev = 0
  Solid = true
  Symmetric = true
FEATURE [Sketcher::SketchObject] Sketch039  label="scavo per cavo usb per micro"
  ArcFitTolerance = 1e-06
  AttachmentSupport = -> [XZ_Plane]
  ExternalGeometry = -> [Sketch,Sketch016]
  FullyConstrained = true
  MakeInternals = false
  MapMode = 5
  Placement = pos=(0,0,0) rot=(1,0,0;1.5708rad)
  sketch-geometry (4):
    g0: LineSegment StartX=-82.51 StartY=36.4 StartZ=0 EndX=-74.51 EndY=36.4 EndZ=0
    g1: LineSegment StartX=-74.51 StartY=36.4 StartZ=0 EndX=-74.51 EndY=30.8 EndZ=0
    g2: LineSegment StartX=-74.51 StartY=30.8 StartZ=0 EndX=-82.51 EndY=30.8 EndZ=0
    g3: LineSegment StartX=-82.51 StartY=30.8 StartZ=0 EndX=-82.51 EndY=36.4 EndZ=0
  constraints (11):
    c: Coincident(g1,g0)
    c: Vertical(g1)
    c: Coincident(g2,g1)
    c: Horizontal(g2)
    c: Coincident(g3,g2)
    c: Coincident(g3,g0)
    c: Vertical(g3)
    c: Tangent(g0,g-3)
    c: Tangent(g2,g-4)
    c: Tangent(g3,g-4)
    c: Tangent(g1,g-4)
FEATURE [Part::Extrusion] Extrude042  label="Extrude scavo per cavo usb per micro"
  Base = -> Sketch039
  Dir = (0,-1,2e-16)
  DirMode = 2
  FaceMakerClass = Part::FaceMakerBullseye
  FaceMakerMode = 3
  LengthFwd = 11.2
  LengthRev = 0
  Solid = true
  Symmetric = true
FEATURE [Sketcher::SketchObject] Sketch040  label="scavo saldature alimentatore connettore 5v"
  ArcFitTolerance = 1e-06
  AttachmentSupport = -> [XZ_Plane]
  ExternalGeometry = -> [Sketch037]
  FullyConstrained = true
  MakeInternals = false
  MapMode = 5
  Placement = pos=(0,0,0) rot=(1,0,0;1.5708rad)
  sketch-geometry (4):
    g0: LineSegment StartX=-211.175 StartY=-52.4316 StartZ=0 EndX=-211.175 EndY=-56.4316 EndZ=0
    g1: LineSegment StartX=-211.175 StartY=-52.4316 StartZ=0 EndX=-209.575 EndY=-52.4316 EndZ=0
    g2: LineSegment StartX=-209.575 StartY=-52.4316 StartZ=0 EndX=-209.575 EndY=-56.4316 EndZ=0
    g3: LineSegment StartX=-209.575 StartY=-56.4316 StartZ=0 EndX=-211.175 EndY=-56.4316 EndZ=0
  constraints (11):
    c: Vertical(g0)
    c: Coincident(g1,g0)
    c: Horizontal(g1)
    c: Coincident(g2,g1)
    c: Coincident(g3,g2)
    c: Coincident(g3,g0)
    c: Horizontal(g3)
    c: DistanceX(g1,g1) = 1.6
    c: DistanceY(g2,g2) = 4
    c: Tangent(g2,g-3)
    c: DistanceY(g1,g-3) = 2
FEATURE [Part::Extrusion] Extrude043  label="Extrude scavo saldature alimentatore connettore 5v"
  Base = -> Sketch040
  Dir = (0,-1,2e-16)
  DirMode = 2
  FaceMakerClass = Part::FaceMakerBullseye
  FaceMakerMode = 3
  LengthFwd = 8
  LengthRev = 0
  Solid = true
  Symmetric = true
FEATURE [Sketcher::SketchObject] Sketch041  label="scavo saldature alimentatore connettore 5v verticali"
  ArcFitTolerance = 1e-06
  AttachmentSupport = -> [XZ_Plane]
  ExternalGeometry = -> [Sketch037]
  FullyConstrained = true
  MakeInternals = false
  MapMode = 5
  Placement = pos=(0,0,0) rot=(1,0,0;1.5708rad)
  sketch-geometry (4):
    g0: LineSegment StartX=-211.175 StartY=-53.6316 StartZ=0 EndX=-209.575 EndY=-53.6316 EndZ=0
    g1: LineSegment StartX=-209.575 StartY=-53.6316 StartZ=0 EndX=-209.575 EndY=-76.6316 EndZ=0
    g2: LineSegment StartX=-209.575 StartY=-76.6316 StartZ=0 EndX=-211.175 EndY=-76.6316 EndZ=0
    g3: LineSegment StartX=-211.175 StartY=-76.6316 StartZ=0 EndX=-211.175 EndY=-53.6316 EndZ=0
  constraints (11):
    c: Horizontal(g0)
    c: Coincident(g1,g0)
    c: Coincident(g2,g1)
    c: Horizontal(g2)
    c: Coincident(g3,g2)
    c: Coincident(g3,g0)
    c: Vertical(g3)
    c: DistanceY(g3,g3) = 23
    c: DistanceX(g0,g0) = 1.6
    c: Tangent(g1,g-3)
    c: DistanceY(g0,g-3) = 3.2
FEATURE [Part::Extrusion] Extrude044  label="Extrude scavo saldature alimentatore connettore 5v verticali"
  Base = -> Sketch041
  Dir = (0,-1,2e-16)
  DirMode = 2
  FaceMakerClass = Part::FaceMakerBullseye
  FaceMakerMode = 3
  LengthFwd = 3.2
  LengthRev = 0
  Placement = pos=(0,8.3,0) rot=(0,0,1;0rad)
  Solid = true
  Symmetric = false
FEATURE [Sketcher::SketchObject] Sketch042  label="fermi per driver solenoide e alimentatore"
  ArcFitTolerance = 1e-06
  AttachmentSupport = -> [XZ_Plane]
  ExternalGeometry = -> [Sketch036,Sketch037,Sketch,Sketch038]
  FullyConstrained = true
  MakeInternals = false
  MapMode = 5
  Placement = pos=(0,0,0) rot=(1,0,0;1.5708rad)
  sketch-geometry (27):
    g0: LineSegment StartX=-200.506 StartY=-25.7811 StartZ=0 EndX=-201.436 EndY=-27.775 EndZ=0
    g1: LineSegment StartX=-201.436 StartY=-27.775 StartZ=0 EndX=-199.442 EndY=-28.7048 EndZ=0
    g2: LineSegment StartX=-199.442 StartY=-28.7048 StartZ=0 EndX=-198.512 EndY=-26.7109 EndZ=0
    g3: LineSegment StartX=-198.512 StartY=-26.7109 StartZ=0 EndX=-200.506 EndY=-25.7811 EndZ=0
    g4: LineSegment StartX=-201.28 StartY=-23.6549 StartZ=0 EndX=-203.562 EndY=-28.5489 EndZ=0
    g5: LineSegment StartX=-203.562 StartY=-28.5489 StartZ=0 EndX=-200.118 EndY=-30.1549 EndZ=0
    g6: LineSegment StartX=-197.992 StartY=-29.381 StartZ=0 EndX=-197.062 EndY=-27.3871 EndZ=0
    g7: LineSegment StartX=-197.836 StartY=-25.2608 StartZ=0 EndX=-201.28 EndY=-23.6549 EndZ=0
    g8: LineSegment [constr] StartX=-198.668 StartY=-30.8311 StartZ=0 EndX=-197.992 EndY=-29.381 EndZ=0
    g9: LineSegment [constr] StartX=-198.668 StartY=-30.8311 StartZ=0 EndX=-200.118 EndY=-30.1549 EndZ=0
    g10: ArcOfCircle CenterX=-198.512 CenterY=-26.7109 CenterZ=0 NormalX=0 NormalY=0 NormalZ=1 AngleXU=0 Radius=1.6 StartAngle=5.84685 EndAngle=7.41765
    g11: GeomPoint [constr] X=-196.386 Y=-25.937 Z=0
    g12: ArcOfCircle CenterX=-199.442 CenterY=-28.7048 CenterZ=0 NormalX=0 NormalY=0 NormalZ=1 AngleXU=0 Radius=1.6 StartAngle=4.27606 EndAngle=5.84685
    g13: GeomPoint [constr] X=-198.668 Y=-30.8311 Z=0
    g14: LineSegment StartX=-207.775 StartY=-46.8316 StartZ=0 EndX=-207.775 EndY=-50.8316 EndZ=0
    g15: LineSegment StartX=-207.775 StartY=-46.8316 StartZ=0 EndX=-203.775 EndY=-46.8316 EndZ=0
    g16: LineSegment StartX=-203.775 StartY=-46.8316 StartZ=0 EndX=-203.775 EndY=-50.8316 EndZ=0
    g17: LineSegment StartX=-207.775 StartY=-50.8316 StartZ=0 EndX=-203.775 EndY=-50.8316 EndZ=0
    g18: LineSegment StartX=-209.375 StartY=-52.4316 StartZ=0 EndX=-203.775 EndY=-52.4316 EndZ=0
    g19: LineSegment StartX=-202.175 StartY=-50.8316 StartZ=0 EndX=-202.175 EndY=-46.8316 EndZ=0
    g20: LineSegment StartX=-203.775 StartY=-45.2316 StartZ=0 EndX=-209.375 EndY=-45.2316 EndZ=0
    g21: LineSegment StartX=-209.375 StartY=-45.2316 StartZ=0 EndX=-209.375 EndY=-52.4316 EndZ=0
    g22: ArcOfCircle CenterX=-203.775 CenterY=-46.8316 CenterZ=0 NormalX=0 NormalY=0 NormalZ=1 AngleXU=0 Radius=1.6 StartAngle=1.8e-15 EndAngle=1.5708
    g23: GeomPoint [constr] X=-202.175 Y=-45.2316 Z=0
    g24: ArcOfCircle CenterX=-203.775 CenterY=-50.8316 CenterZ=0 NormalX=0 NormalY=0 NormalZ=1 AngleXU=0 Radius=1.6 StartAngle=4.71239 EndAngle=6.28319
    g25: GeomPoint [constr] X=-202.175 Y=-52.4316 Z=0
    g26: LineSegment [constr] StartX=-207.775 StartY=-50.4316 StartZ=0 EndX=-207.775 EndY=-50.8316 EndZ=0
  constraints (69):
    c: Coincident(g1,g0)
    c: Coincident(g2,g1)
    c: Coincident(g3,g2)
    c: Coincident(g3,g0)
    c: Parallel(g0,g2)
    c: Perpendicular(g3,g0)
    c: Perpendicular(g1,g0)
    c: Coincident(g5,g4)
    c: Coincident(g7,g4)
    c: Distance(g3) = 2.2
    c: Distance(g2) = 2.2
    c: Parallel(g6,g2)
    c: Parallel(g6,g4)
    c: Perpendicular(g5,g6)
    c: Perpendicular(g7,g6)
    c: Distance(g13,g11) = 5.4
    c: Distance(g5,g13) = 5.4
    c: Coincident(g9,g8)
    c: Distance(g8) = 1.6
    c: Distance(g9) = 1.6
    c: Perpendicular(g9,g8)
    c: Parallel(g8,g6)
    c: Coincident(g8,g13)
    c: Distance(g8,g1) = 1.6
    c: Distance(g9,g1) = 1.6
    c: Tangent(g0,g-5)
    c: Distance(g0,g-6) = 19.2
    c: PointOnObject(g11,g7)
    c: PointOnObject(g11,g6)
    c: Tangent(g7,g10) = -1.5708
    c: Tangent(g6,g10) = -1.5708
    c: PointOnObject(g13,g5)
    c: Tangent(g5,g12) = -1.5708
    c: Tangent(g6,g12) = -1.5708
    c: Equal(g10,g12)
    c: Coincident(g10,g2)
    c: Vertical(g14)
    c: Coincident(g15,g14)
    c: Horizontal(g15)
    c: Coincident(g16,g15)
    c: Vertical(g16)
    c: Coincident(g17,g14)
    c: Coincident(g17,g16)
    c: Horizontal(g17)
    c: Distance(g16) = 4
    c: Distance(g15) = 4
    c: Horizontal(g18)
    c: Vertical(g19)
    c: Horizontal(g20)
    c: Coincident(g21,g20)
    c: Coincident(g21,g18)
    c: Vertical(g21)
    c: Distance(g20,g23) = 7.2
    c: Distance(g25,g23) = 7.2
    c: DistanceY(g18,g14) = 1.6
    c: DistanceX(g18,g14) = 1.6
    c: PointOnObject(g23,g20)
    c: PointOnObject(g23,g19)
    c: Tangent(g20,g22) = -1.5708
    c: Tangent(g19,g22) = -1.5708
    c: PointOnObject(g25,g19)
    c: Tangent(g18,g24) = -1.5708
    c: Tangent(g19,g24) = -1.5708
    c: Equal(g22,g24)
    c: Coincident(g22,g15)
    c: Vertical(g26)
    c: Distance(g26) = 0.4
    c: Coincident(g26,g-4)
    c: Coincident(g14,g26)
FEATURE [Part::Extrusion] Extrude045  label="Extrude fermi per driver solenoide e alimentatore"
  Base = -> Sketch042
  Dir = (0,-1,2e-16)
  DirMode = 2
  FaceMakerClass = Part::FaceMakerBullseye
  FaceMakerMode = 3
  LengthFwd = 25.2
  LengthRev = 0
  Solid = true
  Symmetric = true
FEATURE [Sketcher::SketchObject] Sketch043  label="scavo pulizia fermo alimentatore"
  ArcFitTolerance = 1e-06
  AttachmentSupport = -> [XZ_Plane]
  ExternalGeometry = -> [Sketch042,Sketch036,Sketch037]
  FullyConstrained = true
  MakeInternals = false
  MapMode = 5
  Placement = pos=(0,0,0) rot=(1,0,0;1.5708rad)
  sketch-geometry (6):
    g0: LineSegment StartX=-209.375 StartY=-52.4316 StartZ=0 EndX=-209.375 EndY=-50.4316 EndZ=0
    g1: LineSegment StartX=-209.375 StartY=-50.4316 StartZ=0 EndX=-207.775 EndY=-50.4316 EndZ=0
    g2: LineSegment StartX=-207.775 StartY=-50.4316 StartZ=0 EndX=-207.775 EndY=-45.2316 EndZ=0
    g3: LineSegment StartX=-207.775 StartY=-45.2316 StartZ=0 EndX=-202.175 EndY=-45.2316 EndZ=0
    g4: LineSegment StartX=-202.175 StartY=-45.2316 StartZ=0 EndX=-202.175 EndY=-52.4316 EndZ=0
    g5: LineSegment StartX=-202.175 StartY=-52.4316 StartZ=0 EndX=-209.375 EndY=-52.4316 EndZ=0
  constraints (13):
    c: Vertical(g0)
    c: Coincident(g1,g0)
    c: Coincident(g2,g1)
    c: Coincident(g3,g2)
    c: Coincident(g4,g3)
    c: Coincident(g5,g4)
    c: Coincident(g5,g0)
    c: Horizontal(g5)
    c: Coincident(g0,g-6)
    c: Tangent(g1,g-8)
    c: Tangent(g2,g-4)
    c: Tangent(g3,g-7)
    c: Tangent(g4,g-3)
FEATURE [Part::Extrusion] Extrude046  label="Extrude scavo pulizia fermo alimentatore"
  Base = -> Sketch043
  Dir = (0,-1,2e-16)
  DirMode = 2
  FaceMakerClass = Part::FaceMakerBullseye
  FaceMakerMode = 3
  LengthFwd = 19.5
  LengthRev = 0
  Solid = true
  Symmetric = true
FEATURE [Sketcher::SketchObject] Sketch044  label="buchini per fissaggio oled"
  ArcFitTolerance = 1e-06
  AttachmentSupport = -> [YZ_Plane]
  ExternalGeometry = -> [Sketch]
  FullyConstrained = true
  MakeInternals = false
  MapMode = 5
  Placement = pos=(0,0,0) rot=(0.57735,0.57735,0.57735;2.0944rad)
  sketch-geometry (5):
    g0: LineSegment [constr] StartX=1.5e-14 StartY=67.3588 StartZ=0 EndX=0 EndY=64.3588 EndZ=0
    g1: LineSegment [constr] StartX=0 StartY=64.3588 StartZ=0 EndX=10.4 EndY=64.3588 EndZ=0
    g2: LineSegment [constr] StartX=0 StartY=64.3588 StartZ=0 EndX=-10.4 EndY=64.3588 EndZ=0
    g3: Circle CenterX=10.4 CenterY=64.3588 CenterZ=0 NormalX=0 NormalY=0 NormalZ=1 AngleXU=0 Radius=1.5
    g4: Circle CenterX=-10.4 CenterY=64.3588 CenterZ=0 NormalX=0 NormalY=0 NormalZ=1 AngleXU=0 Radius=1.5
  constraints (13):
    c: Distance(g0) = 3
    c: PointOnObject(g0,g-2)
    c: Coincident(g1,g0)
    c: Horizontal(g1)
    c: Coincident(g2,g0)
    c: Horizontal(g2)
    c: DistanceX(g1,g1) = 10.4
    c: Coincident(g3,g1)
    c: Diameter(g4) = 3
    c: Coincident(g4,g2)
    c: Coincident(g0,g-7)
    c: Equal(g1,g2)
    c: Equal(g4,g3)
FEATURE [Part::Extrusion] Extrude047  label="Extrude buchini per fissaggio oled"
  Base = -> Sketch044
  Dir = (1,0,0)
  DirMode = 2
  FaceMakerClass = Part::FaceMakerBullseye
  FaceMakerMode = 3
  LengthFwd = 10
  LengthRev = 0
  Placement = pos=(-186,0,0) rot=(0,0,1;0rad)
  Solid = true
  Symmetric = false
FEATURE [Sketcher::SketchObject] Sketch046  label="scavo 5x5 neopixel"
  ArcFitTolerance = 1e-06
  AttachmentSupport = -> [YZ_Plane002]
  FullyConstrained = true
  MakeInternals = false
  MapMode = 5
  Placement = pos=(0,0,0) rot=(0.57735,0.57735,0.57735;2.0944rad)
  sketch-geometry (4):
    g0: LineSegment StartX=-2.7 StartY=2.7 StartZ=0 EndX=2.7 EndY=2.7 EndZ=0
    g1: LineSegment StartX=2.7 StartY=2.7 StartZ=0 EndX=2.7 EndY=-2.7 EndZ=0
    g2: LineSegment StartX=2.7 StartY=-2.7 StartZ=0 EndX=-2.7 EndY=-2.7 EndZ=0
    g3: LineSegment StartX=-2.7 StartY=-2.7 StartZ=0 EndX=-2.7 EndY=2.7 EndZ=0
  constraints (11):
    c: Horizontal(g0)
    c: Coincident(g1,g0)
    c: Vertical(g1)
    c: Coincident(g2,g1)
    c: Horizontal(g2)
    c: Coincident(g3,g2)
    c: Coincident(g3,g0)
    c: Vertical(g3)
    c: DistanceX(g0,g0) = 5.4
    c: DistanceY(g1,g1) = 5.4
    c: Symmetric(g0,g1,g-1)
FEATURE [Sketcher::SketchObject] Sketch047  label="scavo 10x10 neopixel corpo"
  ArcFitTolerance = 1e-06
  AttachmentOffset = pos=(0,0,1) rot=(0,0,1;0rad)
  AttachmentSupport = -> [YZ_Plane002]
  FullyConstrained = true
  MakeInternals = false
  MapMode = 5
  Placement = pos=(1,0,0) rot=(0.57735,0.57735,0.57735;2.0944rad)
  sketch-geometry (4):
    g0: LineSegment StartX=-5 StartY=5.1 StartZ=0 EndX=5 EndY=5.1 EndZ=0
    g1: LineSegment StartX=5 StartY=5.1 StartZ=0 EndX=5 EndY=-5.1 EndZ=0
    g2: LineSegment StartX=5 StartY=-5.1 StartZ=0 EndX=-5 EndY=-5.1 EndZ=0
    g3: LineSegment StartX=-5 StartY=-5.1 StartZ=0 EndX=-5 EndY=5.1 EndZ=0
  constraints (11):
    c: Horizontal(g0)
    c: Coincident(g1,g0)
    c: Vertical(g1)
    c: Coincident(g2,g1)
    c: Horizontal(g2)
    c: Coincident(g3,g2)
    c: Coincident(g3,g0)
    c: Vertical(g3)
    c: DistanceX(g0,g0) = 10
    c: DistanceY(g1,g1) = 10.2
    c: Symmetric(g0,g2,g-1)
FEATURE [Sketcher::SketchObject] Sketch048  label="buco per perno blocco neopixel"
  ArcFitTolerance = 1e-06
  AttachmentSupport = -> [XZ_Plane002]
  FullyConstrained = true
  MakeInternals = false
  MapMode = 5
  Placement = pos=(0,0,0) rot=(1,0,0;1.5708rad)
  sketch-geometry (4):
    g0: LineSegment StartX=3 StartY=1.2 StartZ=0 EndX=3 EndY=-1.2 EndZ=0
    g1: LineSegment StartX=3 StartY=-1.2 StartZ=0 EndX=5.4 EndY=-1.2 EndZ=0
    g2: LineSegment StartX=5.4 StartY=-1.2 StartZ=0 EndX=5.4 EndY=1.2 EndZ=0
    g3: LineSegment StartX=5.4 StartY=1.2 StartZ=0 EndX=3 EndY=1.2 EndZ=0
  constraints (11):
    c: Coincident(g1,g0)
    c: Horizontal(g1)
    c: Coincident(g2,g1)
    c: Vertical(g2)
    c: Coincident(g3,g2)
    c: Coincident(g3,g0)
    c: Horizontal(g3)
    c: DistanceX(g1,g1) = 2.4
    c: DistanceY(g2,g2) = 2.4
    c: Symmetric(g0,g0,g-1)
    c: DistanceX(g-1,g0) = 3
FEATURE [Sketcher::SketchObject] Sketch045  label="blocco principale per neopixel"
  ArcFitTolerance = 1e-06
  AttachmentSupport = -> [XZ_Plane002]
  ExternalGeometry = -> [Sketch048]
  FullyConstrained = true
  MakeInternals = false
  MapMode = 5
  Placement = pos=(0,0,0) rot=(1,0,0;1.5708rad)
  sketch-geometry (6):
    g0: LineSegment StartX=0 StartY=5.1 StartZ=0 EndX=0 EndY=-5.1 EndZ=0
    g1: LineSegment StartX=0 StartY=-5.1 StartZ=0 EndX=3 EndY=-5.1 EndZ=0
    g2: LineSegment StartX=7 StartY=-1.1 StartZ=0 EndX=7 EndY=5.1 EndZ=0
    g3: LineSegment StartX=7 StartY=5.1 StartZ=0 EndX=0 EndY=5.1 EndZ=0
    g4: ArcOfCircle CenterX=3 CenterY=-1.1 CenterZ=0 NormalX=0 NormalY=0 NormalZ=1 AngleXU=0 Radius=4 StartAngle=4.71239 EndAngle=6.28319
    g5: GeomPoint [constr] X=7 Y=-5.1 Z=0
  constraints (15):
    c: Vertical(g0)
    c: Coincident(g1,g0)
    c: Horizontal(g1)
    c: Vertical(g2)
    c: Coincident(g3,g2)
    c: Coincident(g3,g0)
    c: Horizontal(g3)
    c: DistanceY(g0,g0) = 10.2
    c: Symmetric(g0,g0,g-1)
    c: DistanceX(g3,g3) = 7
    c: PointOnObject(g5,g2)
    c: PointOnObject(g5,g1)
    c: Tangent(g2,g4) = -1.5708
    c: Tangent(g1,g4) = -1.5708
    c: DistanceX(g-3,g1) = 0
FEATURE [Sketcher::SketchObject] Sketch049  label="rinforzi esterni per corpo neopoixel"
  ArcFitTolerance = 1e-06
  AttachmentSupport = -> [XZ_Plane002]
  ExternalGeometry = -> [Sketch045]
  FullyConstrained = true
  MakeInternals = false
  MapMode = 5
  Placement = pos=(0,0,0) rot=(1,0,0;1.5708rad)
  sketch-geometry (8):
    g0: LineSegment StartX=1 StartY=-4.1 StartZ=0 EndX=2 EndY=-4.1 EndZ=0
    g1: LineSegment StartX=2 StartY=-4.1 StartZ=0 EndX=2 EndY=-5.1 EndZ=0
    g2: LineSegment StartX=2 StartY=-5.1 StartZ=0 EndX=1 EndY=-5.1 EndZ=0
    g3: LineSegment StartX=1 StartY=-5.1 StartZ=0 EndX=1 EndY=-4.1 EndZ=0
    g4: LineSegment StartX=1 StartY=5.1 StartZ=0 EndX=2 EndY=5.1 EndZ=0
    g5: LineSegment StartX=2 StartY=5.1 StartZ=0 EndX=2 EndY=4.1 EndZ=0
    g6: LineSegment StartX=2 StartY=4.1 StartZ=0 EndX=1 EndY=4.1 EndZ=0
    g7: LineSegment StartX=1 StartY=4.1 StartZ=0 EndX=1 EndY=5.1 EndZ=0
  constraints (24):
    c: Horizontal(g0)
    c: Coincident(g1,g0)
    c: Vertical(g1)
    c: Coincident(g2,g1)
    c: Horizontal(g2)
    c: Coincident(g3,g2)
    c: Coincident(g3,g0)
    c: Vertical(g3)
    c: Horizontal(g4)
    c: Coincident(g5,g4)
    c: Vertical(g5)
    c: Coincident(g6,g5)
    c: Horizontal(g6)
    c: Coincident(g7,g6)
    c: Coincident(g7,g4)
    c: Vertical(g7)
    c: DistanceX(g4,g4) = 1
    c: DistanceY(g5,g5) = 1
    c: DistanceX(g0,g0) = 1
    c: DistanceY(g1,g1) = 1
    c: DistanceX(g-3,g4) = 1
    c: DistanceY(g-3,g4) = 0
    c: DistanceX(g-4,g2) = 1
    c: DistanceY(g2,g-4) = 0
FEATURE [Sketcher::SketchObject] Sketch052  label="scavo saldature driver solenoide"
  ArcFitTolerance = 1e-06
  AttachmentSupport = -> [XZ_Plane]
  ExternalGeometry = -> [Sketch038]
  FullyConstrained = true
  MakeInternals = false
  MapMode = 5
  Placement = pos=(0,0,0) rot=(1,0,0;1.5708rad)
  sketch-geometry (4):
    g0: LineSegment StartX=-195.304 StartY=-6.5806 StartZ=0 EndX=-196.994 EndY=-10.2058 EndZ=0
    g1: LineSegment StartX=-196.994 StartY=-10.2058 StartZ=0 EndX=-196.632 EndY=-10.3749 EndZ=0
    g2: LineSegment StartX=-196.632 StartY=-10.3749 StartZ=0 EndX=-194.941 EndY=-6.74965 EndZ=0
    g3: LineSegment StartX=-194.941 StartY=-6.74965 StartZ=0 EndX=-195.304 EndY=-6.5806 EndZ=0
  constraints (11):
    c: Coincident(g1,g0)
    c: Coincident(g2,g1)
    c: Coincident(g3,g2)
    c: Coincident(g3,g0)
    c: Parallel(g2,g0)
    c: Perpendicular(g2,g3)
    c: Perpendicular(g1,g2,g1) = 1.5708
    c: Parallel(g2,g-3)
    c: Distance(g2) = 4
    c: Distance(g3) = 0.4
    c: Coincident(g2,g-3)
FEATURE [Part::Extrusion] Extrude055  label="Extrude scavo saldature driver solenoide"
  Base = -> Sketch052
  Dir = (0,-1,2e-16)
  DirMode = 2
  FaceMakerClass = Part::FaceMakerBullseye
  FaceMakerMode = 3
  LengthFwd = 6
  LengthRev = 0
  Solid = true
  Symmetric = true
FEATURE [Sketcher::SketchObject] Sketch053  label="scavo saldature rumble"
  ArcFitTolerance = 1e-06
  AttachmentSupport = -> [XZ_Plane]
  ExternalGeometry = -> [Sketch019]
  FullyConstrained = true
  MakeInternals = false
  MapMode = 5
  Placement = pos=(0,0,0) rot=(1,0,0;1.5708rad)
  sketch-geometry (4):
    g0: LineSegment StartX=-169.822 StartY=-58.0028 StartZ=0 EndX=-171.058 EndY=-61.807 EndZ=0
    g1: LineSegment StartX=-171.058 StartY=-61.807 StartZ=0 EndX=-169.917 EndY=-62.1778 EndZ=0
    g2: LineSegment StartX=-169.917 StartY=-62.1778 StartZ=0 EndX=-168.681 EndY=-58.3736 EndZ=0
    g3: LineSegment StartX=-168.681 StartY=-58.3736 StartZ=0 EndX=-169.822 EndY=-58.0028 EndZ=0
  constraints (11):
    c: Coincident(g1,g0)
    c: Coincident(g2,g1)
    c: Coincident(g3,g2)
    c: Coincident(g3,g0)
    c: Parallel(g0,g2)
    c: Perpendicular(g3,g0)
    c: Perpendicular(g1,g0)
    c: Parallel(g0,g-3)
    c: Distance(g0) = 4
    c: Coincident(g0,g-3)
    c: Distance(g1) = 1.2
FEATURE [Part::Extrusion] Extrude056  label="Extrude scavo saldature rumble"
  Base = -> Sketch053
  Dir = (0,-1,2e-16)
  DirMode = 2
  FaceMakerClass = Part::FaceMakerBullseye
  FaceMakerMode = 3
  LengthFwd = 8.4
  LengthRev = 0
  Solid = true
  Symmetric = true
FEATURE [Sketcher::SketchObject] Sketch054  label="scavo saldature alimentatore connettore USB"
  ArcFitTolerance = 1e-06
  AttachmentSupport = -> [XZ_Plane]
  ExternalGeometry = -> [Sketch037]
  FullyConstrained = true
  MakeInternals = false
  MapMode = 5
  Placement = pos=(0,0,0) rot=(1,0,0;1.5708rad)
  sketch-geometry (4):
    g0: LineSegment StartX=-209.575 StartY=-80.4316 StartZ=0 EndX=-210.375 EndY=-80.4316 EndZ=0
    g1: LineSegment StartX=-210.375 StartY=-80.4316 StartZ=0 EndX=-210.375 EndY=-72.4316 EndZ=0
    g2: LineSegment StartX=-210.375 StartY=-72.4316 StartZ=0 EndX=-209.575 EndY=-72.4316 EndZ=0
    g3: LineSegment StartX=-209.575 StartY=-72.4316 StartZ=0 EndX=-209.575 EndY=-80.4316 EndZ=0
  constraints (11):
    c: Horizontal(g0)
    c: Coincident(g1,g0)
    c: Vertical(g1)
    c: Coincident(g2,g1)
    c: Horizontal(g2)
    c: Coincident(g3,g2)
    c: Coincident(g3,g0)
    c: Vertical(g3)
    c: DistanceX(g0,g0) = 0.8
    c: DistanceY(g3,g3) = 8
    c: Coincident(g0,g-4)
FEATURE [Part::Extrusion] Extrude057  label="Extrude scavo saldature alimentatore connettore USB"
  Base = -> Sketch054
  Dir = (0,-1,2e-16)
  DirMode = 2
  FaceMakerClass = Part::FaceMakerBullseye
  FaceMakerMode = 3
  LengthFwd = 11
  LengthRev = 0
  Solid = true
  Symmetric = true
FEATURE [Sketcher::SketchObject] Sketch055  label="buco interno per micro switch"
  ArcFitTolerance = 1e-06
  AttachmentSupport = -> [XZ_Plane]
  ExternalGeometry = -> [Sketch]
  FullyConstrained = true
  MakeInternals = false
  MapMode = 5
  Placement = pos=(0,0,0) rot=(1,0,0;1.5708rad)
  sketch-geometry (11):
    g0: LineSegment [constr] StartX=-194.483 StartY=34.2854 StartZ=0 EndX=-196.022 EndY=30.0568 EndZ=0
    g1: LineSegment [constr] StartX=-196.022 StartY=30.0568 StartZ=0 EndX=-197.561 EndY=25.8282 EndZ=0
    g2: LineSegment [constr] StartX=-196.022 StartY=30.0568 StartZ=0 EndX=-194.143 EndY=29.3727 EndZ=0
    g3: LineSegment [constr] StartX=-196.022 StartY=30.0568 StartZ=0 EndX=-197.902 EndY=30.7408 EndZ=0
    g4: LineSegment StartX=-196.362 StartY=34.9694 StartZ=0 EndX=-192.604 EndY=33.6014 EndZ=0
    g5: LineSegment StartX=-199.441 StartY=26.5122 StartZ=0 EndX=-195.682 EndY=25.1441 EndZ=0
    g6: LineSegment StartX=-192.604 StartY=33.6014 StartZ=0 EndX=-195.682 EndY=25.1441 EndZ=0
    g7: LineSegment StartX=-196.362 StartY=34.9694 StartZ=0 EndX=-199.441 EndY=26.5122 EndZ=0
    g8: GeomPoint [constr] X=-187.821 Y=29.2 Z=0
    g9: LineSegment [constr] StartX=-188.505 StartY=27.3206 StartZ=0 EndX=-196.022 EndY=30.0568 EndZ=0
    g10: LineSegment [constr] StartX=-187.821 StartY=29.2 StartZ=0 EndX=-188.505 EndY=27.3206 EndZ=0
  constraints (27):
    c: Coincident(g2,g0)
    c: Parallel(g0,g-3)
    c: Tangent(g1,g0) = -1.5708
    c: Perpendicular(g0,g2)
    c: Tangent(g2,g3)
    c: Distance(g0,g1) = 9
    c: Equal(g0,g1)
    c: Distance(g3,g2) = 4
    c: Equal(g2,g3)
    c: Parallel(g3,g4)
    c: Symmetric(g4,g4,g0)
    c: Parallel(g6,g1)
    c: Parallel(g7,g1)
    c: Symmetric(g6,g6,g2)
    c: Symmetric(g5,g5,g1)
    c: Symmetric(g7,g7,g3)
    c: Coincident(g7,g4)
    c: Coincident(g6,g4)
    c: Coincident(g5,g6)
    c: Symmetric(g-3,g-3,g8)
    c: Perpendicular(g-3,g9)
    c: Distance(g9) = 8
    c: Coincident(g3,g9)
    c: Coincident(g10,g8)
    c: Parallel(g10,g-3)
    c: Distance(g10) = 2
    c: Coincident(g10,g9)
FEATURE [Sketcher::SketchObject] Sketch056  label="buco esterno per micro switch"
  ArcFitTolerance = 1e-06
  AttachmentSupport = -> [XZ_Plane]
  ExternalGeometry = -> [Sketch055]
  FullyConstrained = true
  MakeInternals = false
  MapMode = 5
  Placement = pos=(0,0,0) rot=(1,0,0;1.5708rad)
  sketch-geometry (17):
    g0: GeomPoint [constr] X=-194.143 Y=29.3727 Z=0
    g1: GeomPoint [constr] X=-194.483 Y=34.2854 Z=0
    g2: GeomPoint [constr] X=-197.902 Y=30.7408 Z=0
    g3: GeomPoint [constr] X=-197.561 Y=25.8282 Z=0
    g4: GeomPoint [constr] X=-196.022 Y=30.0568 Z=0
    g5: LineSegment [constr] StartX=-194.483 StartY=34.2854 StartZ=0 EndX=-196.022 EndY=30.0568 EndZ=0
    g6: LineSegment [constr] StartX=-196.022 StartY=30.0568 StartZ=0 EndX=-197.561 EndY=25.8282 EndZ=0
    g7: LineSegment [constr] StartX=-197.902 StartY=30.7408 StartZ=0 EndX=-196.022 EndY=30.0568 EndZ=0
    g8: LineSegment [constr] StartX=-196.022 StartY=30.0568 StartZ=0 EndX=-194.143 EndY=29.3727 EndZ=0
    g9: LineSegment [constr] StartX=-195.338 StartY=31.9362 StartZ=0 EndX=-196.022 EndY=30.0568 EndZ=0
    g10: LineSegment [constr] StartX=-196.022 StartY=30.0568 StartZ=0 EndX=-196.706 EndY=28.1774 EndZ=0
    g11: LineSegment [constr] StartX=-196.022 StartY=30.0568 StartZ=0 EndX=-196.821 EndY=30.3475 EndZ=0
    g12: LineSegment [constr] StartX=-196.022 StartY=30.0568 StartZ=0 EndX=-195.223 EndY=29.7661 EndZ=0
    g13: LineSegment StartX=-194.539 StartY=31.6454 StartZ=0 EndX=-195.907 EndY=27.8867 EndZ=0
    g14: LineSegment StartX=-196.137 StartY=32.2269 StartZ=0 EndX=-197.505 EndY=28.4681 EndZ=0
    g15: LineSegment StartX=-196.137 StartY=32.2269 StartZ=0 EndX=-194.539 EndY=31.6454 EndZ=0
    g16: LineSegment StartX=-197.505 StartY=28.4681 StartZ=0 EndX=-195.907 EndY=27.8867 EndZ=0
  constraints (34):
    c: Symmetric(g-5,g-5,g1)
    c: Symmetric(g-5,g-6,g0)
    c: Symmetric(g-6,g-6,g3)
    c: Symmetric(g-5,g-6,g2)
    c: Coincident(g5,g1)
    c: Coincident(g5,g4)
    c: Coincident(g6,g4)
    c: Coincident(g6,g3)
    c: Equal(g5,g6)
    c: Coincident(g7,g2)
    c: Coincident(g7,g4)
    c: Coincident(g8,g4)
    c: Coincident(g8,g0)
    c: Equal(g7,g8)
    c: Coincident(g11,g9)
    c: Coincident(g12,g9)
    c: Tangent(g10,g9) = -1.5708
    c: Perpendicular(g11,g9)
    c: Parallel(g9,g-4)
    c: Equal(g9,g10)
    c: Parallel(g12,g11)
    c: Equal(g11,g12)
    c: Distance(g11,g12) = 1.7
    c: Distance(g9,g10) = 4
    c: Symmetric(g13,g13,g12)
    c: Parallel(g13,g9)
    c: Symmetric(g14,g14,g11)
    c: Symmetric(g15,g15,g9)
    c: Parallel(g15,g11)
    c: Symmetric(g16,g16,g10)
    c: Coincident(g16,g14)
    c: Coincident(g15,g14)
    c: Coincident(g13,g15)
    c: Coincident(g9,g4)
FEATURE [Sketcher::SketchObject] Sketch057  label="buco interno per SWITCH"
  ArcFitTolerance = 1e-06
  AttachmentSupport = -> [XZ_Plane]
  ExternalGeometry = -> [Sketch]
  FullyConstrained = true
  MakeInternals = false
  MapMode = 5
  Placement = pos=(0,0,0) rot=(1,0,0;1.5708rad)
  sketch-geometry (10):
    g0: GeomPoint [constr] X=-187.821 Y=29.2 Z=0
    g1: LineSegment [constr] StartX=-188.505 StartY=27.3206 StartZ=0 EndX=-193.203 EndY=29.0307 EndZ=0
    g2: LineSegment [constr] StartX=-190.809 StartY=35.6086 StartZ=0 EndX=-195.597 EndY=22.4529 EndZ=0
    g3: GeomPoint [constr] X=-193.203 Y=29.0307 Z=0
    g4: LineSegment [constr] StartX=-196.492 StartY=30.2278 StartZ=0 EndX=-189.914 EndY=27.8336 EndZ=0
    g5: LineSegment StartX=-194.098 StartY=36.8056 StartZ=0 EndX=-187.52 EndY=34.4115 EndZ=0
    g6: LineSegment StartX=-194.098 StartY=36.8056 StartZ=0 EndX=-198.886 EndY=23.6499 EndZ=0
    g7: LineSegment StartX=-187.52 StartY=34.4115 StartZ=0 EndX=-192.308 EndY=21.2558 EndZ=0
    g8: LineSegment StartX=-198.886 StartY=23.6499 StartZ=0 EndX=-192.308 EndY=21.2558 EndZ=0
    g9: LineSegment [constr] StartX=-187.821 StartY=29.2 StartZ=0 EndX=-188.505 EndY=27.3206 EndZ=0
  constraints (23):
    c: Symmetric(g-3,g-3,g0)
    c: Perpendicular(g1,g-3)
    c: Parallel(g2,g-3)
    c: Symmetric(g2,g2,g3)
    c: Perpendicular(g2,g4)
    c: Symmetric(g4,g4,g3)
    c: Distance(g2) = 14
    c: Distance(g4) = 7
    c: Distance(g1) = 5
    c: Parallel(g5,g4)
    c: Parallel(g7,g2)
    c: Symmetric(g5,g5,g2)
    c: Symmetric(g6,g6,g4)
    c: Symmetric(g7,g7,g4)
    c: Symmetric(g8,g8,g2)
    c: Coincident(g6,g5)
    c: Coincident(g7,g5)
    c: Coincident(g8,g7)
    c: Coincident(g3,g1)
    c: Coincident(g9,g0)
    c: Parallel(g9,g-3)
    c: Distance(g9) = 2
    c: Coincident(g1,g9)
FEATURE [Sketcher::SketchObject] Sketch058  label="buco esterno per SWITCH"
  ArcFitTolerance = 1e-06
  AttachmentSupport = -> [XZ_Plane]
  ExternalGeometry = -> [Sketch057]
  FullyConstrained = true
  MakeInternals = false
  MapMode = 5
  Placement = pos=(0,0,0) rot=(1,0,0;1.5708rad)
  sketch-geometry (12):
    g0: GeomPoint [constr] X=-190.809 Y=35.6086 Z=0
    g1: GeomPoint [constr] X=-196.492 Y=30.2278 Z=0
    g2: GeomPoint [constr] X=-189.914 Y=27.8336 Z=0
    g3: GeomPoint [constr] X=-195.597 Y=22.4529 Z=0
    g4: GeomPoint [constr] X=-193.203 Y=29.0307 Z=0
    g5: LineSegment [constr] StartX=-192.006 StartY=32.3196 StartZ=0 EndX=-194.4 EndY=25.7418 EndZ=0
    g6: GeomPoint [constr] X=-193.203 Y=29.0307 Z=0
    g7: LineSegment [constr] StartX=-195.082 StartY=29.7148 StartZ=0 EndX=-191.324 EndY=28.3467 EndZ=0
    g8: LineSegment StartX=-193.885 StartY=33.0037 StartZ=0 EndX=-190.127 EndY=31.6356 EndZ=0
    g9: LineSegment StartX=-190.127 StartY=31.6356 StartZ=0 EndX=-192.521 EndY=25.0578 EndZ=0
    g10: LineSegment StartX=-196.28 StartY=26.4258 StartZ=0 EndX=-192.521 EndY=25.0578 EndZ=0
    g11: LineSegment StartX=-193.885 StartY=33.0037 StartZ=0 EndX=-196.28 EndY=26.4258 EndZ=0
  constraints (21):
    c: Symmetric(g-6,g-6,g3)
    c: Symmetric(g-4,g-6,g2)
    c: Symmetric(g-5,g-4,g0)
    c: Symmetric(g-5,g-6,g1)
    c: Symmetric(g1,g2,g4)
    c: Parallel(g5,g-4)
    c: Symmetric(g5,g5,g6)
    c: Perpendicular(g7,g5)
    c: Symmetric(g7,g7,g6)
    c: Distance(g5) = 7
    c: Distance(g7) = 4
    c: Parallel(g8,g7)
    c: Parallel(g11,g5)
    c: Symmetric(g8,g8,g5)
    c: Symmetric(g9,g9,g7)
    c: Symmetric(g10,g10,g5)
    c: Symmetric(g11,g11,g7)
    c: Coincident(g11,g8)
    c: Coincident(g9,g8)
    c: Coincident(g9,g10)
    c: Coincident(g6,g4)
FEATURE [Part::Extrusion] Extrude060  label="Extrude buco interno per SWITCH destro"
  Base = -> Sketch057
  Dir = (0,-1,2e-16)
  DirMode = 2
  FaceMakerClass = Part::FaceMakerBullseye
  FaceMakerMode = 3
  LengthFwd = 13.2
  LengthRev = 0
  Placement = pos=(0,2.6,0) rot=(0,0,1;0rad)
  Solid = true
  Symmetric = false
FEATURE [Part::Extrusion] Extrude061  label="Extrude buco esterno per SWITCH destro"
  Base = -> Sketch058
  Dir = (0,-1,2e-16)
  DirMode = 2
  FaceMakerClass = Part::FaceMakerBullseye
  FaceMakerMode = 3
  LengthFwd = 2
  LengthRev = 0
  Placement = pos=(0,-10.6,0) rot=(0,0,1;0rad)
  Solid = true
  Symmetric = false
FEATURE [Sketcher::SketchObject] Sketch059  label="buco per spazio introduzione SWITCH"
  ArcFitTolerance = 1e-06
  AttachmentSupport = -> [XZ_Plane]
  ExternalGeometry = -> [Sketch057,Sketch010]
  FullyConstrained = true
  MakeInternals = false
  MapMode = 5
  Placement = pos=(0,0,0) rot=(1,0,0;1.5708rad)
  sketch-geometry (8):
    g0: LineSegment [constr] StartX=-201.368 StartY=36.3521 StartZ=0 EndX=-195.094 EndY=34.0687 EndZ=0
    g1: LineSegment [constr] StartX=-194.098 StartY=36.8056 StartZ=0 EndX=-195.094 EndY=34.0687 EndZ=0
    g2: LineSegment StartX=-198.658 StartY=24.2771 StartZ=0 EndX=-199.654 EndY=21.5401 EndZ=0
    g3: LineSegment StartX=-199.654 StartY=21.5401 StartZ=0 EndX=-181.196 EndY=14.822 EndZ=0
    g4: LineSegment StartX=-181.196 StartY=14.822 StartZ=0 EndX=-180.2 EndY=17.559 EndZ=0
    g5: LineSegment StartX=-180.2 StartY=17.559 StartZ=0 EndX=-198.658 EndY=24.2771 EndZ=0
    g6: LineSegment [constr] StartX=-204.932 StartY=26.5605 StartZ=0 EndX=-198.658 EndY=24.2771 EndZ=0
    g7: LineSegment [constr] StartX=-198.658 StartY=24.2771 StartZ=0 EndX=-199.654 EndY=21.5401 EndZ=0
  constraints (20):
    c: Parallel(g1,g-3)
    c: Parallel(g0,g-4)
    c: Coincident(g0,g-4)
    c: Coincident(g1,g-3)
    c: Coincident(g0,g1)
    c: Coincident(g3,g2)
    c: Coincident(g4,g3)
    c: Coincident(g5,g4)
    c: Coincident(g5,g2)
    c: Parallel(g5,g-5)
    c: Parallel(g3,g-5)
    c: Parallel(g4,g-6)
    c: DistanceX(g-6,g4) = 0
    c: Coincident(g6,g-5)
    c: Equal(g6,g0)
    c: Coincident(g7,g6)
    c: Equal(g7,g1)
    c: Tangent(g7,g-3)
    c: Coincident(g2,g6)
    c: Coincident(g2,g7)
FEATURE [Part::Extrusion] Extrude062  label="Extrude buco per spazio introduzione SWITCH"
  Base = -> Sketch059
  Dir = (0,-1,2e-16)
  DirMode = 2
  FaceMakerClass = Part::FaceMakerBullseye
  FaceMakerMode = 3
  LengthFwd = 13.2
  LengthRev = 0
  Solid = true
  Symmetric = true
FEATURE [Part::Extrusion] Extrude063  label="Extrude buco interno per SWITCH sinistro"
  Base = -> Sketch057
  Dir = (0,-1,2e-16)
  DirMode = 2
  FaceMakerClass = Part::FaceMakerBullseye
  FaceMakerMode = 3
  LengthFwd = 13.2
  LengthRev = 0
  Placement = pos=(0,10.6,0) rot=(0,0,1;0rad)
  Solid = true
  Symmetric = false
FEATURE [Part::Extrusion] Extrude064  label="Extrude buco esterno per SWITCH sinistro"
  Base = -> Sketch058
  Dir = (0,-1,2e-16)
  DirMode = 2
  FaceMakerClass = Part::FaceMakerBullseye
  FaceMakerMode = 3
  LengthFwd = 2
  LengthRev = 0
  Placement = pos=(0,12.6,0) rot=(0,0,1;0rad)
  Solid = true
  Symmetric = false
FEATURE [Sketcher::SketchObject] Sketch061  label="struttura esterna blocco switch"
  ArcFitTolerance = 1e-06
  AttachmentSupport = -> [XZ_Plane003]
  FullyConstrained = true
  MakeInternals = false
  MapMode = 5
  Placement = pos=(0,0,0) rot=(1,0,0;1.5708rad)
  sketch-geometry (5):
    g0: LineSegment StartX=-1 StartY=-5.1 StartZ=0 EndX=1 EndY=-5.1 EndZ=0
    g1: LineSegment StartX=1 StartY=-5.1 StartZ=0 EndX=1 EndY=5.1 EndZ=0
    g2: LineSegment StartX=1 StartY=5.1 StartZ=0 EndX=-1 EndY=5.1 EndZ=0
    g3: LineSegment StartX=-1 StartY=5.1 StartZ=0 EndX=-1 EndY=-5.1 EndZ=0
    g4: GeomPoint [constr] X=0 Y=0 Z=0
  constraints (12):
    c: Coincident(g0,g1)
    c: Coincident(g1,g2)
    c: Coincident(g2,g3)
    c: Coincident(g3,g0)
    c: Horizontal(g0)
    c: Horizontal(g2)
    c: Vertical(g1)
    c: Vertical(g3)
    c: Symmetric(g2,g0,g4)
    c: Distance(g1,g3) = 2
    c: Distance(g0,g2) = 10.2
    c: Coincident(g4,g-1)
FEATURE [Sketcher::SketchObject] Sketch062  label="struttura interna blocco switch"
  ArcFitTolerance = 1e-06
  AttachmentSupport = -> [XZ_Plane003]
  ExternalGeometry = -> [Sketch061]
  FullyConstrained = true
  MakeInternals = false
  MapMode = 5
  Placement = pos=(0,0,0) rot=(1,0,0;1.5708rad)
  sketch-geometry (5):
    g0: LineSegment StartX=-1 StartY=3.1 StartZ=0 EndX=-1 EndY=-3.1 EndZ=0
    g1: LineSegment StartX=-1 StartY=-3.1 StartZ=0 EndX=1 EndY=-3.1 EndZ=0
    g2: LineSegment StartX=1 StartY=-3.1 StartZ=0 EndX=1 EndY=3.1 EndZ=0
    g3: LineSegment StartX=1 StartY=3.1 StartZ=0 EndX=-1 EndY=3.1 EndZ=0
    g4: GeomPoint [constr] X=0 Y=0 Z=0
  constraints (12):
    c: Coincident(g0,g1)
    c: Coincident(g1,g2)
    c: Coincident(g2,g3)
    c: Coincident(g3,g0)
    c: Vertical(g0)
    c: Vertical(g2)
    c: Horizontal(g1)
    c: Horizontal(g3)
    c: Symmetric(g2,g0,g4)
    c: Coincident(g4,g-1)
    c: Distance(g0) = 6.2
    c: Equal(g3,g-3)
FEATURE [Sketcher::SketchObject] Sketch063  label="blocchi tra switch"
  ArcFitTolerance = 1e-06
  AttachmentSupport = -> [XZ_Plane003]
  ExternalGeometry = -> [Sketch061,Sketch062]
  FullyConstrained = true
  MakeInternals = false
  MapMode = 5
  Placement = pos=(0,0,0) rot=(1,0,0;1.5708rad)
  sketch-geometry (8):
    g0: LineSegment StartX=-3 StartY=5.1 StartZ=0 EndX=-1 EndY=5.1 EndZ=0
    g1: LineSegment StartX=-1 StartY=5.1 StartZ=0 EndX=-1 EndY=3.1 EndZ=0
    g2: LineSegment StartX=-1 StartY=3.1 StartZ=0 EndX=-3 EndY=3.1 EndZ=0
    g3: LineSegment StartX=-3 StartY=3.1 StartZ=0 EndX=-3 EndY=5.1 EndZ=0
    g4: LineSegment StartX=-3 StartY=-3.1 StartZ=0 EndX=-1 EndY=-3.1 EndZ=0
    g5: LineSegment StartX=-1 StartY=-3.1 StartZ=0 EndX=-1 EndY=-5.1 EndZ=0
    g6: LineSegment StartX=-1 StartY=-5.1 StartZ=0 EndX=-3 EndY=-5.1 EndZ=0
    g7: LineSegment StartX=-3 StartY=-5.1 StartZ=0 EndX=-3 EndY=-3.1 EndZ=0
  constraints (20):
    c: Horizontal(g0)
    c: Coincident(g1,g0)
    c: Coincident(g2,g1)
    c: Horizontal(g2)
    c: Coincident(g3,g2)
    c: Coincident(g3,g0)
    c: Vertical(g3)
    c: Horizontal(g4)
    c: Coincident(g5,g4)
    c: Coincident(g6,g5)
    c: Horizontal(g6)
    c: Coincident(g7,g6)
    c: Coincident(g7,g4)
    c: Vertical(g7)
    c: Coincident(g0,g-4)
    c: Coincident(g1,g-5)
    c: Coincident(g4,g-6)
    c: Coincident(g5,g-7)
    c: Distance(g0) = 2
    c: Distance(g4) = 2
FEATURE [Sketcher::SketchObject] Sketch066  label="piano per rampino"
  ArcFitTolerance = 1e-06
  AttachmentSupport = -> [XZ_Plane002]
  ExternalGeometry = -> [Sketch045]
  FullyConstrained = true
  MakeInternals = false
  MapMode = 5
  Placement = pos=(0,0,0) rot=(1,0,0;1.5708rad)
  sketch-geometry (4):
    g0: LineSegment StartX=5.4 StartY=5.1 StartZ=0 EndX=5.4 EndY=3.9 EndZ=0
    g1: LineSegment StartX=5.4 StartY=3.9 StartZ=0 EndX=7 EndY=3.9 EndZ=0
    g2: LineSegment StartX=7 StartY=3.9 StartZ=0 EndX=7 EndY=5.1 EndZ=0
    g3: LineSegment StartX=7 StartY=5.1 StartZ=0 EndX=5.4 EndY=5.1 EndZ=0
  constraints (11):
    c: Coincident(g0,g1)
    c: Coincident(g1,g2)
    c: Coincident(g2,g3)
    c: Coincident(g3,g0)
    c: Vertical(g0)
    c: Vertical(g2)
    c: Horizontal(g1)
    c: Horizontal(g3)
    c: Distance(g0,g2) = 1.6
    c: Distance(g1,g3) = 1.2
    c: Coincident(g2,g-3)
FEATURE [Sketcher::SketchObject] Sketch064  label="rampini_per_serraggio_struttura"
  ArcFitTolerance = 1e-06
  AttachmentSupport = -> [XZ_Plane002]
  ExternalGeometry = -> [Sketch066,Sketch045]
  FullyConstrained = true
  MakeInternals = false
  MapMode = 5
  Placement = pos=(0,0,0) rot=(1,0,0;1.5708rad)
  sketch-geometry (7):
    g0: LineSegment StartX=7 StartY=5.1 StartZ=0 EndX=7 EndY=3.9 EndZ=0
    g1: LineSegment StartX=7 StartY=3.9 StartZ=0 EndX=9 EndY=3.9 EndZ=0
    g2: LineSegment StartX=7 StartY=5.1 StartZ=0 EndX=7 EndY=5.1 EndZ=0
    g3: LineSegment StartX=7 StartY=5.1 StartZ=0 EndX=7 EndY=7.5 EndZ=0
    g4: LineSegment StartX=9 StartY=5.1 StartZ=0 EndX=9 EndY=3.9 EndZ=0
    g5: LineSegment StartX=7 StartY=7.5 StartZ=0 EndX=9 EndY=7.5 EndZ=0
    g6: LineSegment StartX=9 StartY=7.5 StartZ=0 EndX=9 EndY=5.1 EndZ=0
  constraints (20):
    c: Vertical(g0)
    c: Coincident(g1,g0)
    c: Horizontal(g1)
    c: Coincident(g2,g0)
    c: Horizontal(g2)
    c: Coincident(g3,g2)
    c: Vertical(g3)
    c: Coincident(g5,g3)
    c: Coincident(g4,g6)
    c: Coincident(g4,g1)
    c: Vertical(g4)
    c: Coincident(g0,g-3)
    c: DistanceY(g-4,g3) = 2.4
    c: DistanceX(g1,g1) = 2
    c: DistanceY(g2,g6) = 0
    c: DistanceX(g2,g2) = 0
    c: DistanceY(g0,g0) = 1.2
    c: Coincident(g5,g6)
    c: Horizontal(g5)
    c: Vertical(g6)
FEATURE [Sketcher::SketchObject] Sketch067  label="perno per blocco switch"
  ArcFitTolerance = 1e-06
  AttachmentSupport = -> [XZ_Plane]
  ExternalGeometry = -> [Sketch,Sketch010]
  FullyConstrained = true
  MakeInternals = false
  MapMode = 5
  Placement = pos=(0,0,0) rot=(1,0,0;1.5708rad)
  sketch-geometry (14):
    g0: LineSegment StartX=-191.073 StartY=24.9429 StartZ=0 EndX=-185.81 EndY=23.0276 EndZ=0
    g1: LineSegment StartX=-183.76 StartY=23.9839 StartZ=0 EndX=-182.392 EndY=27.7427 EndZ=0
    g2: LineSegment StartX=-183.348 StartY=29.7934 StartZ=0 EndX=-188.61 EndY=31.7087 EndZ=0
    g3: LineSegment StartX=-188.61 StartY=31.7087 StartZ=0 EndX=-191.073 EndY=24.9429 EndZ=0
    g4: GeomPoint [constr] X=-186.459 Y=27.0946 Z=0
    g5: LineSegment StartX=-189.022 StartY=25.8992 StartZ=0 EndX=-185.263 EndY=24.5311 EndZ=0
    g6: LineSegment StartX=-185.263 StartY=24.5311 StartZ=0 EndX=-183.895 EndY=28.2899 EndZ=0
    g7: LineSegment StartX=-183.895 StartY=28.2899 StartZ=0 EndX=-187.654 EndY=29.658 EndZ=0
    g8: LineSegment StartX=-187.654 StartY=29.658 StartZ=0 EndX=-189.022 EndY=25.8992 EndZ=0
    g9: GeomPoint [constr] X=-186.459 Y=27.0946 Z=0
    g10: ArcOfCircle CenterX=-185.263 CenterY=24.5311 CenterZ=0 NormalX=0 NormalY=0 NormalZ=1 AngleXU=0 Radius=1.6 StartAngle=4.36332 EndAngle=5.93412
    g11: GeomPoint [constr] X=-184.307 Y=22.4804 Z=0
    g12: ArcOfCircle CenterX=-183.895 CenterY=28.2899 CenterZ=0 NormalX=0 NormalY=0 NormalZ=1 AngleXU=0 Radius=1.6 StartAngle=5.93412 EndAngle=7.50492
    g13: GeomPoint [constr] X=-181.844 Y=29.2462 Z=0
  constraints (30):
    c: Coincident(g2,g3)
    c: Coincident(g3,g0)
    c: Symmetric(g13,g0,g4)
    c: Distance(g11,g3) = 7.2
    c: Distance(g0,g2) = 7.2
    c: Parallel(g3,g1)
    c: Parallel(g2,g0)
    c: Perpendicular(g2,g3)
    c: Coincident(g5,g6)
    c: Coincident(g6,g7)
    c: Coincident(g7,g8)
    c: Coincident(g8,g5)
    c: Symmetric(g7,g5,g9)
    c: Distance(g6,g8) = 4
    c: Distance(g5,g7) = 4
    c: Coincident(g9,g4)
    c: Parallel(g8,g6)
    c: Parallel(g7,g5)
    c: Perpendicular(g7,g8)
    c: Tangent(g8,g-3)
    c: Tangent(g2,g-4)
    c: PointOnObject(g11,g1)
    c: PointOnObject(g11,g0)
    c: Tangent(g1,g10) = -1.5708
    c: Tangent(g0,g10) = -1.5708
    c: PointOnObject(g13,g1)
    c: Tangent(g1,g12) = -1.5708
    c: Tangent(g2,g12) = -1.5708
    c: Equal(g10,g12)
    c: Coincident(g10,g5)
FEATURE [Part::Extrusion] Extrude072  label="Extrude perno per blocco switch"
  Base = -> Sketch067
  Dir = (0,-1,2e-16)
  DirMode = 2
  FaceMakerClass = Part::FaceMakerBullseye
  FaceMakerMode = 3
  LengthFwd = 25.2
  LengthRev = 0
  Solid = true
  Symmetric = true
FEATURE [Part::MultiFuse] Fusion
  Refine = true
  Shapes = -> [Extrude,Sweep,Extrude007,Extrude011,Extrude005,Extrude012,Extrude013,Extrude016,Extrude031,Extrude039,Extrude045,Extrude072]
FEATURE [Part::Cut] Cut
  Base = -> Fusion
  Refine = true
  Tool = -> Extrude001
FEATURE [Part::Cut] Cut001
  Base = -> Cut
  Refine = true
  Tool = -> Extrude004
FEATURE [Part::Cut] Cut002
  Base = -> Cut001
  Refine = true
  Tool = -> Extrude006
FEATURE [Part::Cut] Cut003
  Base = -> Cut002
  Refine = true
  Tool = -> Extrude008
FEATURE [Part::Cut] Cut004
  Base = -> Cut003
  Refine = true
  Tool = -> Extrude009
FEATURE [Part::Cut] Cut005
  Base = -> Cut004
  Refine = true
  Tool = -> Extrude010
FEATURE [Part::Cut] Cut006
  Base = -> Cut005
  Refine = true
  Tool = -> Extrude014
FEATURE [Part::Cut] Cut007
  Base = -> Cut006
  Refine = true
  Tool = -> Extrude015
FEATURE [Part::Cut] Cut008
  Base = -> Cut007
  Refine = true
  Tool = -> Extrude018
FEATURE [Part::Cut] Cut009
  Base = -> Cut008
  Refine = true
  Tool = -> Extrude019
FEATURE [Part::Cut] Cut010
  Base = -> Cut009
  Refine = true
  Tool = -> Extrude020
FEATURE [Part::Cut] Cut011
  Base = -> Cut010
  Refine = true
  Tool = -> Extrude021
FEATURE [Part::Cut] Cut012
  Base = -> Cut011
  Refine = true
  Tool = -> Extrude022
FEATURE [Part::Cut] Cut013
  Base = -> Cut012
  Refine = true
  Tool = -> Extrude023
FEATURE [Part::Cut] Cut014
  Base = -> Cut013
  Refine = true
  Tool = -> Extrude032
FEATURE [Part::Cut] Cut015
  Base = -> Cut014
  Refine = true
  Tool = -> Extrude033
FEATURE [Part::Cut] Cut016
  Base = -> Cut015
  Refine = true
  Tool = -> Extrude034
FEATURE [Part::Cut] Cut017
  Base = -> Cut016
  Refine = true
  Tool = -> Extrude035
FEATURE [Part::Cut] Cut018
  Base = -> Cut017
  Refine = true
  Tool = -> Extrude036
FEATURE [Part::Cut] Cut019
  Base = -> Cut018
  Refine = true
  Tool = -> Extrude037
FEATURE [Part::Cut] Cut020
  Base = -> Cut019
  Refine = true
  Tool = -> Extrude030
FEATURE [Part::Cut] Cut022
  Base = -> Cut020
  Refine = true
  Tool = -> Extrude038
FEATURE [Part::Cut] Cut023
  Base = -> Cut022
  Refine = true
  Tool = -> Extrude041
FEATURE [Part::Cut] Cut024
  Base = -> Cut023
  Refine = true
  Tool = -> Extrude040
FEATURE [Part::Cut] Cut025
  Base = -> Cut024
  Refine = true
  Tool = -> Extrude042
FEATURE [Part::Cut] Cut026
  Base = -> Cut025
  Refine = true
  Tool = -> Extrude043
FEATURE [Part::Cut] Cut027
  Base = -> Cut026
  Refine = true
  Tool = -> Extrude044
FEATURE [Part::Cut] Cut028
  Base = -> Cut027
  Refine = true
  Tool = -> Extrude046
FEATURE [Part::Cut] Cut029
  Base = -> Cut028
  Refine = true
  Tool = -> Extrude047
FEATURE [Part::Cut] Cut033
  Base = -> Cut029
  Refine = true
  Tool = -> Extrude055
FEATURE [Part::Cut] Cut034
  Base = -> Cut033
  Refine = true
  Tool = -> Extrude056
FEATURE [Part::Cut] Cut035
  Base = -> Cut034
  Refine = true
  Tool = -> Extrude057
FEATURE [Part::Cut] Cut037
  Base = -> Cut035
  Refine = true
  Tool = -> Extrude060
FEATURE [Part::Cut] Cut038
  Base = -> Cut037
  Refine = true
  Tool = -> Extrude061
FEATURE [Part::Cut] Cut039
  Base = -> Cut038
  Refine = true
  Tool = -> Extrude063
FEATURE [Part::Cut] Cut040
  Base = -> Cut039
  Refine = true
  Tool = -> Extrude064
FEATURE [Part::Cut] Cut041
  Base = -> Cut040
  Refine = true
  Tool = -> Extrude062
FEATURE [Sketcher::SketchObject] Sketch068  label="base con smusso sopra neopixel"
  ArcFitTolerance = 1e-06
  AttachmentSupport = -> [YZ_Plane002]
  FullyConstrained = true
  MakeInternals = false
  MapMode = 5
  Placement = pos=(0,0,0) rot=(0.57735,0.57735,0.57735;2.0944rad)
  sketch-geometry (5):
    g0: LineSegment StartX=-9.5 StartY=-6.1 StartZ=0 EndX=9.5 EndY=-6.1 EndZ=0
    g1: LineSegment StartX=9.5 StartY=-6.1 StartZ=0 EndX=9.5 EndY=6.1 EndZ=0
    g2: LineSegment StartX=9.5 StartY=6.1 StartZ=0 EndX=-9.5 EndY=6.1 EndZ=0
    g3: LineSegment StartX=-9.5 StartY=6.1 StartZ=0 EndX=-9.5 EndY=-6.1 EndZ=0
    g4: GeomPoint [constr] X=0 Y=0 Z=0
  constraints (12):
    c: Coincident(g0,g1)
    c: Coincident(g1,g2)
    c: Coincident(g2,g3)
    c: Coincident(g3,g0)
    c: Horizontal(g0)
    c: Horizontal(g2)
    c: Vertical(g1)
    c: Vertical(g3)
    c: Symmetric(g2,g0,g4)
    c: Distance(g1,g3) = 19
    c: Distance(g0,g2) = 12.2
    c: Coincident(g4,g-1)
FEATURE [Sketcher::SketchObject] Sketch069  label="cilindro minore"
  ArcFitTolerance = 1e-06
  AttachmentSupport = -> [XZ_Plane004]
  FullyConstrained = true
  MakeInternals = false
  MapMode = 5
  Placement = pos=(0,0,0) rot=(1,0,0;1.5708rad)
  sketch-geometry (1):
    g0: Circle CenterX=0 CenterY=0 CenterZ=0 NormalX=0 NormalY=0 NormalZ=1 AngleXU=0 Radius=5.8
  constraints (2):
    c: Diameter(g0) = 11.6
    c: Coincident(g0,g-1)
FEATURE [Sketcher::SketchObject] Sketch070  label="cilindro maggiore"
  ArcFitTolerance = 1e-06
  AttachmentSupport = -> [XZ_Plane004]
  ExternalGeometry = -> [Sketch069]
  FullyConstrained = true
  MakeInternals = false
  MapMode = 5
  Placement = pos=(0,0,0) rot=(1,0,0;1.5708rad)
  sketch-geometry (1):
    g0: Circle CenterX=0 CenterY=0 CenterZ=0 NormalX=0 NormalY=0 NormalZ=1 AngleXU=0 Radius=6.5
  constraints (2):
    c: Coincident(g0,g-1)
    c: Diameter(g0) = 13
FEATURE [Sketcher::SketchObject] Sketch071  label="buco interno"
  ArcFitTolerance = 1e-06
  AttachmentSupport = -> [XZ_Plane004]
  ExternalGeometry = -> [Sketch069]
  FullyConstrained = true
  MakeInternals = false
  MapMode = 5
  Placement = pos=(0,0,0) rot=(1,0,0;1.5708rad)
  sketch-geometry (1):
    g0: Circle CenterX=0 CenterY=0 CenterZ=0 NormalX=0 NormalY=0 NormalZ=1 AngleXU=0 Radius=5
  constraints (2):
    c: Coincident(g0,g-1)
    c: Diameter(g0) = 10
FEATURE [PartDesign::Pad] Pad
  Direction = (0,-1,2e-16)
  Length = 1.2
  Length2 = 10
  Placement = pos=(0,0,0) rot=(1,0,0;1.5708rad)
  Profile = -> Sketch070
  ReferenceAxis = -> Sketch070 [N_Axis]
  Refine = true
  Suppressed = false
  Type = 0
FEATURE [PartDesign::Pad] Pad001
  BaseFeature = -> Pad
  Direction = (0,-1,2e-16)
  Length = 5.6
  Length2 = 10
  Placement = pos=(0,0,0) rot=(1,0,0;1.5708rad)
  Profile = -> Sketch069
  ReferenceAxis = -> Sketch069 [N_Axis]
  Refine = true
  Suppressed = false
  Type = 0
FEATURE [PartDesign::Pocket] Pocket
  BaseFeature = -> Pad001
  Direction = (0,1,-2e-16)
  Length = 7
  Length2 = 5
  Midplane = true
  Placement = pos=(0,0,0) rot=(1,0,0;1.5708rad)
  Profile = -> Sketch071
  ReferenceAxis = -> Sketch071 [N_Axis]
  Refine = true
  Suppressed = false
  Type = 0
FEATURE [PartDesign::Fillet] Fillet
  Base = -> Pocket [Face7]
  BaseFeature = -> Pocket
  Placement = pos=(0,0,0) rot=(1,0,0;1.5708rad)
  Radius = 1
  Refine = true
  SupportTransform = false
  Suppressed = false
  UseAllEdges = false
FEATURE [PartDesign::Body] Body004  label="pulsanti lato sinistro"
  AllowCompound = false
  Group = -> [Sketch069,Sketch070,Sketch071,Pad,Pad001,Pocket,Fillet]
  Origin = -> Origin004
  Tip = -> Fillet
FEATURE [Sketcher::SketchObject] Sketch072  label="buco per saldature e diodo driver solenoide"
  ArcFitTolerance = 1e-06
  AttachmentSupport = -> [XZ_Plane]
  ExternalGeometry = -> [Sketch038]
  FullyConstrained = true
  MakeInternals = false
  MapMode = 5
  Placement = pos=(0,0,0) rot=(1,0,0;1.5708rad)
  sketch-geometry (4):
    g0: LineSegment StartX=-212.269 StartY=-43.9083 StartZ=0 EndX=-207.197 EndY=-33.0326 EndZ=0
    g1: LineSegment StartX=-207.197 StartY=-33.0326 StartZ=0 EndX=-207.56 EndY=-32.8635 EndZ=0
    g2: LineSegment StartX=-207.56 StartY=-32.8635 StartZ=0 EndX=-212.631 EndY=-43.7392 EndZ=0
    g3: LineSegment StartX=-212.631 StartY=-43.7392 StartZ=0 EndX=-212.269 EndY=-43.9083 EndZ=0
  constraints (11):
    c: Coincident(g1,g0)
    c: Coincident(g2,g1)
    c: Coincident(g3,g2)
    c: Coincident(g3,g0)
    c: Parallel(g-3,g0)
    c: Parallel(g0,g2)
    c: Perpendicular(g0,g3)
    c: Perpendicular(g1,g0)
    c: Distance(g3) = 0.4
    c: Distance(g2) = 12
    c: Coincident(g0,g-3)
FEATURE [Part::Extrusion] Extrude074  label="Extrude buco per saldature e diodo driver solenoide"
  Base = -> Sketch072
  Dir = (0,-1,2e-16)
  DirMode = 2
  FaceMakerClass = Part::FaceMakerBullseye
  FaceMakerMode = 3
  LengthFwd = 14.6
  LengthRev = 0
  Solid = true
  Symmetric = true
FEATURE [Part::Cut] Cut042
  Base = -> Cut041
  Refine = true
  Tool = -> Extrude074
FEATURE [Sketcher::SketchObject] Sketch073  label="fori slargati blocco solenoide"
  ArcFitTolerance = 1e-06
  AttachmentSupport = -> [XY_Plane]
  ExternalGeometry = -> [Sketch030]
  FullyConstrained = true
  MakeInternals = false
  MapMode = 5
  sketch-geometry (2):
    g0: Circle CenterX=-152.209 CenterY=6.95 CenterZ=0 NormalX=0 NormalY=0 NormalZ=1 AngleXU=0 Radius=3.7
    g1: Circle CenterX=-130.41 CenterY=-6.95 CenterZ=0 NormalX=0 NormalY=0 NormalZ=1 AngleXU=0 Radius=3.7
  constraints (4):
    c: Diameter(g0) = 7.4
    c: Coincident(g0,g-3)
    c: Diameter(g1) = 7.4
    c: Coincident(g1,g-4)
FEATURE [Part::Extrusion] Extrude075  label="Extrude fori slargati blocco solenoide"
  Base = -> Sketch073
  Dir = (0,0,1)
  DirMode = 2
  FaceMakerClass = Part::FaceMakerBullseye
  FaceMakerMode = 3
  LengthFwd = 1.5
  LengthRev = 0
  Placement = pos=(0,0,36.4) rot=(0,0,1;0rad)
  Solid = true
  Symmetric = false
FEATURE [Part::Cut] Cut043
  Base = -> Cut042
  Refine = true
  Tool = -> Extrude075
FEATURE [Sketcher::SketchObject] Sketch074  label="lato sx pistola"
  ArcFitTolerance = 1e-06
  AttachmentSupport = -> [XZ_Plane]
  ExternalGeometry = -> [Sketch016,Sketch,Sketch058]
  FullyConstrained = true
  MakeInternals = false
  MapMode = 5
  Placement = pos=(0,0,0) rot=(1,0,0;1.5708rad)
  sketch-geometry (37):
    g0: LineSegment StartX=-82.8 StartY=3.2 StartZ=0 EndX=0 EndY=3.2 EndZ=0
    g1: LineSegment StartX=-82.8 StartY=3.2 StartZ=0 EndX=-82.8 EndY=6.2 EndZ=0
    g2: LineSegment [constr] StartX=-107.6 StartY=18 StartZ=0 EndX=-107.6 EndY=20 EndZ=0
    g3: LineSegment [constr] StartX=-132.428 StartY=18 StartZ=0 EndX=-132.428 EndY=20 EndZ=0
    g4: LineSegment StartX=-132.428 StartY=20 StartZ=0 EndX=-107.6 EndY=20 EndZ=0
    g5: ArcOfCircle CenterX=-107.6 CenterY=4 CenterZ=0 NormalX=0 NormalY=0 NormalZ=1 AngleXU=0 Radius=16 StartAngle=0.137937 EndAngle=1.5708
    g6: LineSegment StartX=-82.8 StartY=6.2 StartZ=0 EndX=-91.752 EndY=6.2 EndZ=0
    g7: LineSegment [constr] StartX=-145.743 StartY=8.32624 StartZ=0 EndX=-147.645 EndY=8.94427 EndZ=0
    g8: ArcOfCircle CenterX=-132.428 CenterY=4 CenterZ=0 NormalX=0 NormalY=0 NormalZ=1 AngleXU=0 Radius=16 StartAngle=1.5708 EndAngle=2.82743
    g9: LineSegment StartX=-215.932 StartY=-80.4316 StartZ=0 EndX=-176.685 EndY=-80.4316 EndZ=0
    g10: LineSegment StartX=-147.645 StartY=8.94427 StartZ=0 EndX=-176.685 EndY=-80.4316 EndZ=0
    g11: LineSegment [constr] StartX=-193.988 StartY=-2.33927 StartZ=0 EndX=-192.176 EndY=-3.18451 EndZ=0
    g12: LineSegment [constr] StartX=-217.232 StartY=-52.1862 StartZ=0 EndX=-215.42 EndY=-53.0314 EndZ=0
    g13: LineSegment StartX=-192.176 StartY=-3.18451 StartZ=0 EndX=-215.42 EndY=-53.0314 EndZ=0
    g14: ArcOfCircle CenterX=-184.801 CenterY=-67.3089 CenterZ=0 NormalX=0 NormalY=0 NormalZ=1 AngleXU=0 Radius=33.7833 StartAngle=2.70526 EndAngle=3.54053
    g15: ArcOfCircle CenterX=-207.583 CenterY=4 CenterZ=0 NormalX=0 NormalY=0 NormalZ=1 AngleXU=0 Radius=17 StartAngle=5.84685 EndAngle=7.56663
    g16: LineSegment StartX=-202.765 StartY=20.303 StartZ=0 EndX=-195.887 EndY=39.2 EndZ=0
    g17: LineSegment [constr] StartX=-193.885 StartY=33.0037 StartZ=0 EndX=-197.644 EndY=34.3718 EndZ=0
    g18: LineSegment StartX=-195.887 StartY=39.2 StartZ=0 EndX=0 EndY=39.2 EndZ=0
    g19: LineSegment StartX=0 StartY=3.2 StartZ=0 EndX=0 EndY=39.2 EndZ=0
    g20: LineSegment StartX=-189.939 StartY=31.5672 StartZ=0 EndX=-192.333 EndY=24.9893 EndZ=0
    g21: LineSegment StartX=-196.467 StartY=26.4942 StartZ=0 EndX=-194.073 EndY=33.0721 EndZ=0
    g22: Circle CenterX=-213.443 CenterY=-76.8316 CenterZ=0 NormalX=0 NormalY=0 NormalZ=1 AngleXU=0 Radius=1.8
    g23: Circle CenterX=-179.305 CenterY=-76.8316 CenterZ=0 NormalX=0 NormalY=0 NormalZ=1 AngleXU=0 Radius=1.8
    g24: Circle CenterX=-184.08 CenterY=34.8 CenterZ=0 NormalX=0 NormalY=0 NormalZ=1 AngleXU=0 Radius=1.8
    g25: Circle CenterX=-78.51 CenterY=34.8 CenterZ=0 NormalX=0 NormalY=0 NormalZ=1 AngleXU=0 Radius=1.8
    g26: Circle CenterX=-78.51 CenterY=7.6 CenterZ=0 NormalX=0 NormalY=0 NormalZ=1 AngleXU=0 Radius=1.8
    g27: Circle CenterX=-5.6 CenterY=34.8 CenterZ=0 NormalX=0 NormalY=0 NormalZ=1 AngleXU=0 Radius=1.8
    g28: Circle CenterX=-5.6 CenterY=7.6 CenterZ=0 NormalX=0 NormalY=0 NormalZ=1 AngleXU=0 Radius=1.8
    g29: LineSegment StartX=-190.127 StartY=31.6356 StartZ=0 EndX=-189.939 EndY=31.5672 EndZ=0
    g30: LineSegment StartX=-194.073 StartY=33.0721 StartZ=0 EndX=-193.885 EndY=33.0037 EndZ=0
    g31: LineSegment StartX=-193.885 StartY=33.0037 StartZ=0 EndX=-190.127 EndY=31.6356 EndZ=0
    g32: LineSegment StartX=-196.467 StartY=26.4942 StartZ=0 EndX=-192.333 EndY=24.9893 EndZ=0
    g33: Circle CenterX=-19 CenterY=21.2 CenterZ=0 NormalX=0 NormalY=0 NormalZ=1 AngleXU=0 Radius=6.3
    g34: Circle CenterX=-42 CenterY=21.2 CenterZ=0 NormalX=0 NormalY=0 NormalZ=1 AngleXU=0 Radius=6.3
    g35: Circle CenterX=-65 CenterY=21.2 CenterZ=0 NormalX=0 NormalY=0 NormalZ=1 AngleXU=0 Radius=6.3
    g36: LineSegment [constr] StartX=-4 StartY=21.2 StartZ=0 EndX=-65 EndY=21.2 EndZ=0
  constraints (96):
    c: Coincident(g0,g-41)
    c: Horizontal(g0)
    c: PointOnObject(g0,g-39)
    c: Coincident(g1,g0)
    c: Vertical(g1)
    c: DistanceY(g1,g1) = 3
    c: Coincident(g2,g-17)
    c: Vertical(g2)
    c: Coincident(g3,g-16)
    c: Vertical(g3)
    c: DistanceY(g2,g2) = 2
    c: DistanceY(g3,g3) = 2
    c: Coincident(g4,g3)
    c: Coincident(g4,g2)
    c: Coincident(g5,g-17)
    c: Coincident(g5,g2)
    c: Coincident(g6,g1)
    c: Horizontal(g6)
    c: Coincident(g6,g5)
    c: Coincident(g7,g-15)
    c: Coincident(g8,g7)
    c: Coincident(g8,g3)
    c: Coincident(g8,g-15)
    c: Horizontal(g9)
    c: DistanceY(g-13,g9) = 2
    c: Coincident(g10,g7)
    c: Parallel(g10,g-14)
    c: Coincident(g9,g10)
    c: Distance(g11) = 2
    c: Coincident(g11,g-11)
    c: Perpendicular(g-11,g11)
    c: Distance(g12) = 2
    c: Coincident(g12,g-12)
    c: Perpendicular(g-11,g12)
    c: Coincident(g13,g11)
    c: Coincident(g13,g12)
    c: Coincident(g14,g-32)
    c: Coincident(g14,g12)
    c: Coincident(g14,g9)
    c: Coincident(g15,g-10)
    c: Coincident(g15,g11)
    c: Parallel(g16,g-22)
    c: Distance(g17) = 4
    c: PointOnObject(g17,g16)
    c: Coincident(g15,g16)
    c: Horizontal(g18)
    c: Coincident(g18,g16)
    c: Coincident(g19,g0)
    c: PointOnObject(g19,g-39)
    c: DistanceY(g19,g-36) = 2
    c: Coincident(g18,g19)
    c: Diameter(g22) = 3.6
    c: Coincident(g22,g-9)
    c: Diameter(g23) = 3.6
    c: Coincident(g23,g-8)
    c: Diameter(g24) = 3.6
    c: Diameter(g25) = 3.6
    c: Diameter(g26) = 3.6
    c: Diameter(g27) = 3.6
    c: Diameter(g28) = 3.6
    c: Coincident(g27,g-4)
    c: Coincident(g28,g-3)
    c: Coincident(g25,g-6)
    c: Coincident(g26,g-5)
    c: Coincident(g24,g-7)
    c: Parallel(g20,g-21)
    c: Equal(g20,g-21)
    c: Parallel(g21,g-19)
    c: Equal(g21,g-19)
    c: Distance(g29) = 0.2
    c: Distance(g30) = 0.2
    c: Parallel(g29,g-20)
    c: Parallel(g31,g-20)
    c: Equal(g31,g-20)
    c: Coincident(g30,g31)
    c: Coincident(g31,g29)
    c: Coincident(g29,g-21)
    c: Parallel(g30,g31)
    c: Coincident(g17,g30)
    c: Coincident(g20,g29)
    c: Coincident(g21,g30)
    c: Perpendicular(g16,g17)
    c: Coincident(g32,g21)
    c: Coincident(g32,g20)
    c: Perpendicular(g10,g7)
    c: Diameter(g33) = 12.6
    c: Diameter(g34) = 12.6
    c: Diameter(g35) = 12.6
    c: Horizontal(g36)
    c: PointOnObject(g33,g36)
    c: PointOnObject(g34,g36)
    c: DistanceX(g34,g33) = 23
    c: DistanceX(g35,g34) = 23
    c: DistanceX(g33,g36) = 15
    c: Symmetric(g-24,g-24,g36)
    c: Coincident(g36,g35)
FEATURE [Sketcher::SketchObject] Sketch075  label="lato dx pistola"
  ArcFitTolerance = 1e-06
  AttachmentSupport = -> [XZ_Plane]
  ExternalGeometry = -> [Sketch016,Sketch,Sketch058,Sketch074]
  FullyConstrained = true
  MakeInternals = false
  MapMode = 5
  Placement = pos=(0,0,0) rot=(1,0,0;1.5708rad)
  sketch-geometry (61):
    g0: LineSegment StartX=-82.8 StartY=3.2 StartZ=0 EndX=0 EndY=3.2 EndZ=0
    g1: LineSegment StartX=-82.8 StartY=3.2 StartZ=0 EndX=-82.8 EndY=6.2 EndZ=0
    g2: LineSegment [constr] StartX=-107.6 StartY=18 StartZ=0 EndX=-107.6 EndY=20 EndZ=0
    g3: LineSegment [constr] StartX=-132.428 StartY=18 StartZ=0 EndX=-132.428 EndY=20 EndZ=0
    g4: LineSegment StartX=-132.428 StartY=20 StartZ=0 EndX=-107.6 EndY=20 EndZ=0
    g5: ArcOfCircle CenterX=-107.6 CenterY=4 CenterZ=0 NormalX=0 NormalY=0 NormalZ=1 AngleXU=0 Radius=16 StartAngle=0.137937 EndAngle=1.5708
    g6: LineSegment StartX=-82.8 StartY=6.2 StartZ=0 EndX=-91.752 EndY=6.2 EndZ=0
    g7: LineSegment [constr] StartX=-145.743 StartY=8.32624 StartZ=0 EndX=-147.645 EndY=8.94427 EndZ=0
    g8: ArcOfCircle CenterX=-132.428 CenterY=4 CenterZ=0 NormalX=0 NormalY=0 NormalZ=1 AngleXU=0 Radius=16 StartAngle=1.5708 EndAngle=2.82743
    g9: LineSegment StartX=-215.932 StartY=-80.4316 StartZ=0 EndX=-176.685 EndY=-80.4316 EndZ=0
    g10: LineSegment StartX=-147.645 StartY=8.94427 StartZ=0 EndX=-176.685 EndY=-80.4316 EndZ=0
    g11: LineSegment [constr] StartX=-193.988 StartY=-2.33927 StartZ=0 EndX=-192.176 EndY=-3.18451 EndZ=0
    g12: LineSegment [constr] StartX=-217.232 StartY=-52.1862 StartZ=0 EndX=-215.42 EndY=-53.0314 EndZ=0
    g13: LineSegment StartX=-192.176 StartY=-3.18451 StartZ=0 EndX=-215.42 EndY=-53.0314 EndZ=0
    g14: ArcOfCircle CenterX=-184.801 CenterY=-67.3089 CenterZ=0 NormalX=0 NormalY=0 NormalZ=1 AngleXU=0 Radius=33.7833 StartAngle=2.70526 EndAngle=3.54053
    g15: ArcOfCircle CenterX=-207.583 CenterY=4 CenterZ=0 NormalX=0 NormalY=0 NormalZ=1 AngleXU=0 Radius=17 StartAngle=5.84685 EndAngle=7.56663
    g16: LineSegment StartX=-202.765 StartY=20.303 StartZ=0 EndX=-195.887 EndY=39.2 EndZ=0
    g17: LineSegment [constr] StartX=-193.885 StartY=33.0037 StartZ=0 EndX=-197.644 EndY=34.3718 EndZ=0
    g18: LineSegment StartX=-195.887 StartY=39.2 StartZ=0 EndX=0 EndY=39.2 EndZ=0
    g19: LineSegment StartX=0 StartY=3.2 StartZ=0 EndX=0 EndY=39.2 EndZ=0
    g20: LineSegment StartX=-189.939 StartY=31.5672 StartZ=0 EndX=-192.333 EndY=24.9893 EndZ=0
    g21: LineSegment StartX=-196.467 StartY=26.4942 StartZ=0 EndX=-194.073 EndY=33.0721 EndZ=0
    g22: Circle CenterX=-213.443 CenterY=-76.8316 CenterZ=0 NormalX=0 NormalY=0 NormalZ=1 AngleXU=0 Radius=1.8
    g23: Circle CenterX=-179.305 CenterY=-76.8316 CenterZ=0 NormalX=0 NormalY=0 NormalZ=1 AngleXU=0 Radius=1.8
    g24: Circle CenterX=-184.08 CenterY=34.8 CenterZ=0 NormalX=0 NormalY=0 NormalZ=1 AngleXU=0 Radius=1.8
    g25: Circle CenterX=-78.51 CenterY=34.8 CenterZ=0 NormalX=0 NormalY=0 NormalZ=1 AngleXU=0 Radius=1.8
    g26: Circle CenterX=-78.51 CenterY=7.6 CenterZ=0 NormalX=0 NormalY=0 NormalZ=1 AngleXU=0 Radius=1.8
    g27: Circle CenterX=-5.6 CenterY=34.8 CenterZ=0 NormalX=0 NormalY=0 NormalZ=1 AngleXU=0 Radius=1.8
    g28: Circle CenterX=-5.6 CenterY=7.6 CenterZ=0 NormalX=0 NormalY=0 NormalZ=1 AngleXU=0 Radius=1.8
    g29: LineSegment StartX=-190.127 StartY=31.6356 StartZ=0 EndX=-189.939 EndY=31.5672 EndZ=0
    g30: LineSegment StartX=-194.073 StartY=33.0721 StartZ=0 EndX=-193.885 EndY=33.0037 EndZ=0
    g31: LineSegment StartX=-193.885 StartY=33.0037 StartZ=0 EndX=-190.127 EndY=31.6356 EndZ=0
    g32: LineSegment StartX=-196.467 StartY=26.4942 StartZ=0 EndX=-192.333 EndY=24.9893 EndZ=0
    g33: LineSegment [constr] StartX=-4 StartY=21.2 StartZ=0 EndX=-87.91 EndY=21.2 EndZ=0
    g34: GeomPoint [constr] X=-4 Y=21.2 Z=0
    g35: LineSegment [constr] StartX=-15.2 StartY=33.7 StartZ=0 EndX=-15.2 EndY=8.7 EndZ=0
    g36: LineSegment [constr] StartX=-15.2 StartY=33.7 StartZ=0 EndX=-56.2 EndY=33.7 EndZ=0
    g37: LineSegment [constr] StartX=-15.2 StartY=8.7 StartZ=0 EndX=-56.2 EndY=8.7 EndZ=0
    g38: LineSegment [constr] StartX=-56.2 StartY=33.7 StartZ=0 EndX=-56.2 EndY=8.7 EndZ=0
    g39: Circle CenterX=-18.6 CenterY=30.3 CenterZ=0 NormalX=0 NormalY=0 NormalZ=1 AngleXU=0 Radius=3.4
    g40: Circle CenterX=-18.6 CenterY=12.1 CenterZ=0 NormalX=0 NormalY=0 NormalZ=1 AngleXU=0 Radius=3.4
    g41: Circle CenterX=-43.2 CenterY=30.3 CenterZ=0 NormalX=0 NormalY=0 NormalZ=1 AngleXU=0 Radius=3.4
    g42: Circle CenterX=-43.2 CenterY=12.1 CenterZ=0 NormalX=0 NormalY=0 NormalZ=1 AngleXU=0 Radius=3.4
    g43: LineSegment [constr] StartX=-4 StartY=21.2 StartZ=0 EndX=-15.2 EndY=21.2 EndZ=0
    g44: LineSegment [constr] StartX=-15.2 StartY=21.2 StartZ=0 EndX=-36.2 EndY=21.2 EndZ=0
    g45: LineSegment [constr] StartX=-41.5 StartY=16.2 StartZ=0 EndX=-30.9 EndY=16.2 EndZ=0
    g46: LineSegment [constr] StartX=-30.9 StartY=16.2 StartZ=0 EndX=-30.9 EndY=26.2 EndZ=0
    g47: LineSegment [constr] StartX=-30.9 StartY=26.2 StartZ=0 EndX=-41.5 EndY=26.2 EndZ=0
    g48: LineSegment [constr] StartX=-41.5 StartY=26.2 StartZ=0 EndX=-41.5 EndY=16.2 EndZ=0
    g49: GeomPoint [constr] X=-36.2 Y=21.2 Z=0
    g50: Circle CenterX=-36.2 CenterY=21.2 CenterZ=0 NormalX=0 NormalY=0 NormalZ=1 AngleXU=0 Radius=2.8
    g51: LineSegment [constr] StartX=-24.2 StartY=26.7 StartZ=0 EndX=-24.2 EndY=15.7 EndZ=0
    g52: Circle CenterX=-24.2 CenterY=26.7 CenterZ=0 NormalX=0 NormalY=0 NormalZ=1 AngleXU=0 Radius=3
    g53: Circle CenterX=-24.2 CenterY=15.7 CenterZ=0 NormalX=0 NormalY=0 NormalZ=1 AngleXU=0 Radius=3
    g54: GeomPoint X=-18.6 Y=30.3 Z=0
    g55: GeomPoint X=-18.6 Y=12.1 Z=0
    g56: GeomPoint X=-43.2 Y=12.1 Z=0
    g57: GeomPoint X=-43.2 Y=30.3 Z=0
    g58: Circle CenterX=-65 CenterY=21.2 CenterZ=0 NormalX=0 NormalY=0 NormalZ=1 AngleXU=0 Radius=1.5
    g59: Circle CenterX=-42 CenterY=21.2 CenterZ=0 NormalX=0 NormalY=0 NormalZ=1 AngleXU=0 Radius=1.5
    g60: Circle CenterX=-19 CenterY=21.2 CenterZ=0 NormalX=0 NormalY=0 NormalZ=1 AngleXU=0 Radius=1.5
  constraints (149):
    c: Coincident(g0,g-41)
    c: Horizontal(g0)
    c: PointOnObject(g0,g-39)
    c: Coincident(g1,g0)
    c: Vertical(g1)
    c: DistanceY(g1,g1) = 3
    c: Coincident(g2,g-17)
    c: Vertical(g2)
    c: Coincident(g3,g-16)
    c: Vertical(g3)
    c: DistanceY(g2,g2) = 2
    c: DistanceY(g3,g3) = 2
    c: Coincident(g4,g3)
    c: Coincident(g4,g2)
    c: Coincident(g5,g-17)
    c: Coincident(g5,g2)
    c: Coincident(g6,g1)
    c: Horizontal(g6)
    c: Coincident(g6,g5)
    c: Coincident(g7,g-15)
    c: Coincident(g8,g7)
    c: Coincident(g8,g3)
    c: Coincident(g8,g-15)
    c: Horizontal(g9)
    c: DistanceY(g-13,g9) = 2
    c: Coincident(g10,g7)
    c: Parallel(g10,g-14)
    c: Coincident(g9,g10)
    c: Distance(g11) = 2
    c: Coincident(g11,g-11)
    c: Perpendicular(g-11,g11)
    c: Distance(g12) = 2
    c: Coincident(g12,g-12)
    c: Perpendicular(g-11,g12)
    c: Coincident(g13,g11)
    c: Coincident(g13,g12)
    c: Coincident(g14,g-32)
    c: Coincident(g14,g12)
    c: Coincident(g14,g9)
    c: Coincident(g15,g-10)
    c: Coincident(g15,g11)
    c: Parallel(g16,g-22)
    c: Distance(g17) = 4
    c: PointOnObject(g17,g16)
    c: Coincident(g15,g16)
    c: Horizontal(g18)
    c: Coincident(g18,g16)
    c: Coincident(g19,g0)
    c: PointOnObject(g19,g-39)
    c: DistanceY(g19,g-36) = 2
    c: Coincident(g18,g19)
    c: Diameter(g22) = 3.6
    c: Coincident(g22,g-9)
    c: Diameter(g23) = 3.6
    c: Coincident(g23,g-8)
    c: Diameter(g24) = 3.6
    c: Diameter(g25) = 3.6
    c: Diameter(g26) = 3.6
    c: Diameter(g27) = 3.6
    c: Diameter(g28) = 3.6
    c: Coincident(g27,g-4)
    c: Coincident(g28,g-3)
    c: Coincident(g25,g-6)
    c: Coincident(g26,g-5)
    c: Coincident(g24,g-7)
    c: Parallel(g20,g-21)
    c: Equal(g20,g-21)
    c: Parallel(g21,g-19)
    c: Equal(g21,g-19)
    c: Distance(g29) = 0.2
    c: Distance(g30) = 0.2
    c: Parallel(g29,g-20)
    c: Parallel(g31,g-20)
    c: Equal(g31,g-20)
    c: Coincident(g30,g31)
    c: Coincident(g31,g29)
    c: Coincident(g29,g-21)
    c: Parallel(g30,g31)
    c: Coincident(g17,g30)
    c: Coincident(g20,g29)
    c: Coincident(g21,g30)
    c: Perpendicular(g16,g17)
    c: Coincident(g32,g21)
    c: Coincident(g32,g20)
    c: Perpendicular(g10,g7)
    c: Horizontal(g33)
    c: Symmetric(g-24,g-24,g33)
    c: PointOnObject(g33,g-28)
    c: Symmetric(g-24,g-24,g34)
    c: DistanceY(g35,g35) = 25
    c: Symmetric(g35,g35,g33)
    c: Distance(g36) = 41
    c: Coincident(g36,g35)
    c: Horizontal(g36)
    c: Coincident(g37,g35)
    c: Horizontal(g37)
    c: Coincident(g38,g36)
    c: Vertical(g38)
    c: Coincident(g37,g38)
    c: Diameter(g39) = 6.8
    c: Diameter(g40) = 6.8
    c: Tangent(g39,g36)
    c: Tangent(g40,g37)
    c: Tangent(g39,g35)
    c: Tangent(g40,g35)
    c: Diameter(g41) = 6.8
    c: Diameter(g42) = 6.8
    c: Tangent(g41,g36)
    c: Tangent(g42,g37)
    c: DistanceX(g41,g39) = 24.6
    c: DistanceX(g42,g40) = 24.6
    c: Distance(g43) = 11.2
    c: Coincident(g43,g33)
    c: PointOnObject(g43,g33)
    c: PointOnObject(g43,g35)
    c: Distance(g44) = 21
    c: Coincident(g44,g43)
    c: PointOnObject(g44,g33)
    c: Coincident(g45,g46)
    c: Coincident(g46,g47)
    c: Coincident(g47,g48)
    c: Coincident(g48,g45)
    c: Horizontal(g45)
    c: Horizontal(g47)
    c: Vertical(g46)
    c: Vertical(g48)
    c: Symmetric(g47,g45,g49)
    c: Distance(g46,g48) = 10.6
    c: Distance(g45,g47) = 10
    c: Coincident(g49,g44)
    c: Diameter(g50) = 5.6
    c: Coincident(g50,g44)
    c: Distance(g51) = 11
    c: Symmetric(g51,g51,g33)
    c: DistanceX(g51,g43) = 9
    c: Diameter(g52) = 6
    c: Coincident(g52,g51)
    c: Diameter(g53) = 6
    c: Coincident(g53,g51)
    c: Coincident(g40,g55)
    c: Coincident(g39,g54)
    c: Coincident(g41,g57)
    c: Coincident(g42,g56)
    c: Diameter(g58) = 3
    c: Diameter(g59) = 3
    c: Diameter(g60) = 3
    c: Coincident(g58,g-44)
    c: Coincident(g59,g-46)
    c: Coincident(g60,g-45)
FEATURE [Sketcher::SketchObject] Sketch078
  ArcFitTolerance = 1e-06
  AttachmentSupport = -> [XZ_Plane005]
  FullyConstrained = true
  MakeInternals = false
  MapMode = 5
  Placement = pos=(0,0,0) rot=(1,0,0;1.5708rad)
  sketch-geometry (5):
    g0: LineSegment [constr] StartX=0 StartY=5.5 StartZ=0 EndX=0 EndY=-5.5 EndZ=0
    g1: ArcOfCircle CenterX=0 CenterY=5.5 CenterZ=0 NormalX=0 NormalY=0 NormalZ=1 AngleXU=0 Radius=2.7 StartAngle=0 EndAngle=3.14159
    g2: ArcOfCircle CenterX=0 CenterY=-5.5 CenterZ=0 NormalX=0 NormalY=0 NormalZ=1 AngleXU=0 Radius=2.7 StartAngle=3.1416 EndAngle=6.28318
    g3: LineSegment StartX=-2.7 StartY=5.5 StartZ=0 EndX=-2.7 EndY=-5.50001 EndZ=0
    g4: LineSegment StartX=2.7 StartY=5.5 StartZ=0 EndX=2.7 EndY=-5.50001 EndZ=0
  constraints (13):
    c: Distance(g0) = 11
    c: Vertical(g0)
    c: Symmetric(g0,g0,g-1)
    c: Radius(g1) = 2.7
    c: Coincident(g1,g0)
    c: Radius(g2) = 2.7
    c: Coincident(g2,g0)
    c: Vertical(g3)
    c: Vertical(g4)
    c: Coincident(g2,g4)
    c: Coincident(g2,g3)
    c: Tangent(g3,g1) = -1.5708
    c: Tangent(g4,g1) = 1.5708
FEATURE [PartDesign::Pad] Pad002
  Direction = (0,-1,2e-16)
  Length = 0.8
  Length2 = 10
  Placement = pos=(0,0,0) rot=(1,0,0;1.5708rad)
  Profile = -> Sketch078
  ReferenceAxis = -> Sketch078 [N_Axis]
  Refine = true
  Suppressed = false
  Type = 0
FEATURE [Sketcher::SketchObject] Sketch079
  ArcFitTolerance = 1e-06
  AttachmentSupport = -> [XZ_Plane005]
  ExternalGeometry = -> [Sketch078]
  FullyConstrained = true
  MakeInternals = false
  MapMode = 5
  Placement = pos=(0,0,0) rot=(1,0,0;1.5708rad)
  sketch-geometry (2):
    g0: Circle CenterX=-1e-16 CenterY=5.5 CenterZ=0 NormalX=0 NormalY=0 NormalZ=1 AngleXU=0 Radius=2.7
    g1: Circle CenterX=0 CenterY=-5.5 CenterZ=0 NormalX=0 NormalY=0 NormalZ=1 AngleXU=0 Radius=2.7
  constraints (4):
    c: Coincident(g0,g-3)
    c: PointOnObject(g-3,g0)
    c: Coincident(g1,g-4)
    c: Equal(g1,g-4)
FEATURE [PartDesign::Pad] Pad003
  BaseFeature = -> Pad002
  Direction = (0,-1,2e-16)
  Length = 5
  Length2 = 10
  Placement = pos=(0,0,0) rot=(1,0,0;1.5708rad)
  Profile = -> Sketch079
  ReferenceAxis = -> Sketch079 [N_Axis]
  Refine = true
  Suppressed = false
  Type = 0
FEATURE [PartDesign::Fillet] Fillet001
  Base = -> Pad003 [Edge16,Edge14]
  BaseFeature = -> Pad003
  Placement = pos=(0,0,0) rot=(1,0,0;1.5708rad)
  Radius = 0.4
  Refine = true
  SupportTransform = false
  Suppressed = false
  UseAllEdges = false
FEATURE [PartDesign::Body] Body005  label="pulsanti lato destro"
  AllowCompound = false
  Group = -> [Sketch078,Pad002,Sketch079,Pad003,Fillet001]
  Origin = -> Origin005
  Tip = -> Fillet001
FEATURE [PartDesign::SubShapeBinder] Binder
  BindCopyOnChange = 0
  BindMode = 0
  ClaimChildren = false
  Context = -> Body006 [Binder.]
  Fuse = false
  MakeFace = true
  OffsetFill = false
  OffsetIntersection = false
  OffsetJoinType = 0
  OffsetOpenResult = false
  PartialLoad = false
  Refine = true
  Relative = true
  Support = -> [Body[Sketch074.]]
  _Version = 2
FEATURE [PartDesign::SubShapeBinder] Binder001
  BindCopyOnChange = 0
  BindMode = 0
  ClaimChildren = false
  Context = -> Body007 [Binder001.]
  Fuse = false
  MakeFace = true
  OffsetFill = false
  OffsetIntersection = false
  OffsetJoinType = 0
  OffsetOpenResult = false
  PartialLoad = false
  Refine = true
  Relative = true
  Support = -> [Body[Sketch075.]]
  _Version = 2
FEATURE [Mesh::Feature] logo_per_PCB_definitivo_positivo
  Placement = pos=(-191,17,-66) rot=(0,1,1;0rad)
FEATURE [Sketcher::SketchObject] Sketch114  label="Sketch114 - base lato DX"
  ArcFitTolerance = 1e-06
  AttachmentSupport = -> [Binder001]
  ExternalGeometry = -> [Binder001]
  FullyConstrained = true
  MakeInternals = false
  MapMode = 5
  Placement = pos=(0,1e-15,0) rot=(0,0.707107,0.707107;3.14159rad)
  sketch-geometry (30):
    g0: Circle CenterX=5.6 CenterY=34.8 CenterZ=0 NormalX=0 NormalY=0 NormalZ=1 AngleXU=0 Radius=1.8
    g1: Circle CenterX=5.6 CenterY=7.6 CenterZ=0 NormalX=0 NormalY=0 NormalZ=1 AngleXU=0 Radius=1.8
    g2: Circle CenterX=24.2 CenterY=26.7 CenterZ=0 NormalX=0 NormalY=0 NormalZ=1 AngleXU=0 Radius=3
    g3: Circle CenterX=24.2 CenterY=15.7 CenterZ=0 NormalX=0 NormalY=0 NormalZ=1 AngleXU=0 Radius=3
    g4: Circle CenterX=36.2 CenterY=21.2 CenterZ=0 NormalX=0 NormalY=0 NormalZ=1 AngleXU=0 Radius=2.8
    g5: Circle CenterX=78.51 CenterY=34.8 CenterZ=0 NormalX=0 NormalY=0 NormalZ=1 AngleXU=0 Radius=1.8
    g6: Circle CenterX=78.51 CenterY=7.6 CenterZ=0 NormalX=0 NormalY=0 NormalZ=1 AngleXU=0 Radius=1.8
    g7: Circle CenterX=184.08 CenterY=34.8 CenterZ=0 NormalX=0 NormalY=0 NormalZ=1 AngleXU=0 Radius=1.8
    g8: Circle CenterX=213.443 CenterY=-76.8316 CenterZ=0 NormalX=0 NormalY=0 NormalZ=1 AngleXU=0 Radius=1.8
    g9: Circle CenterX=179.305 CenterY=-76.8316 CenterZ=0 NormalX=0 NormalY=0 NormalZ=1 AngleXU=0 Radius=1.8
    g10: ArcOfCircle [constr] CenterX=132.428 CenterY=4 CenterZ=0 NormalX=0 NormalY=0 NormalZ=1 AngleXU=0 Radius=16 StartAngle=0.314159 EndAngle=1.5708
    g11: ArcOfCircle CenterX=107.6 CenterY=4 CenterZ=0 NormalX=0 NormalY=0 NormalZ=1 AngleXU=0 Radius=16 StartAngle=1.5708 EndAngle=3.00366
    g12: ArcOfCircle CenterX=207.583 CenterY=4 CenterZ=0 NormalX=0 NormalY=0 NormalZ=1 AngleXU=0 Radius=17 StartAngle=1.85815 EndAngle=3.57792
    g13: ArcOfCircle CenterX=184.801 CenterY=-67.3089 CenterZ=0 NormalX=0 NormalY=0 NormalZ=1 AngleXU=0 Radius=33.7833 StartAngle=5.88425 EndAngle=6.71952
    g14: LineSegment StartX=0 StartY=39.2 StartZ=0 EndX=0 EndY=3.2 EndZ=0
    g15: LineSegment StartX=0 StartY=3.2 StartZ=0 EndX=82.8 EndY=3.2 EndZ=0
    g16: LineSegment StartX=82.8 StartY=3.2 StartZ=0 EndX=82.8 EndY=6.2 EndZ=0
    g17: LineSegment StartX=82.8 StartY=6.2 StartZ=0 EndX=91.752 EndY=6.2 EndZ=0
    g18: LineSegment StartX=107.6 StartY=20 StartZ=0 EndX=132.428 EndY=20 EndZ=0
    g19: LineSegment StartX=147.645 StartY=8.94427 StartZ=0 EndX=176.685 EndY=-80.4316 EndZ=0
    g20: LineSegment StartX=176.685 StartY=-80.4316 StartZ=0 EndX=215.932 EndY=-80.4316 EndZ=0
    g21: LineSegment StartX=215.42 StartY=-53.0314 StartZ=0 EndX=192.176 EndY=-3.18451 EndZ=0
    g22: LineSegment StartX=202.765 StartY=20.303 StartZ=0 EndX=195.887 EndY=39.2 EndZ=0
    g23: LineSegment StartX=195.887 StartY=39.2 StartZ=0 EndX=0 EndY=39.2 EndZ=0
    g24: LineSegment StartX=196.467 StartY=26.4942 StartZ=0 EndX=194.073 EndY=33.0721 EndZ=0
    g25: LineSegment StartX=194.073 StartY=33.0721 StartZ=0 EndX=189.939 EndY=31.5672 EndZ=0
    g26: LineSegment StartX=189.939 StartY=31.5672 StartZ=0 EndX=192.333 EndY=24.9893 EndZ=0
    g27: LineSegment StartX=192.333 StartY=24.9893 StartZ=0 EndX=196.467 EndY=26.4942 EndZ=0
    g28: LineSegment StartX=132.428 StartY=20 StartZ=0 EndX=144.053 EndY=20 EndZ=0
    g29: LineSegment StartX=144.053 StartY=20 StartZ=0 EndX=147.645 EndY=8.94427 EndZ=0
  constraints (65):
    c: Equal(g0,g-25)
    c: Equal(g2,g-29)
    c: Equal(g3,g-30)
    c: Equal(g4,g-28)
    c: Equal(g1,g-26)
    c: Coincident(g0,g-25)
    c: Coincident(g1,g-26)
    c: Coincident(g2,g-29)
    c: Coincident(g3,g-30)
    c: Coincident(g4,g-28)
    c: Equal(g5,g-23)
    c: Equal(g6,g-24)
    c: Coincident(g5,g-23)
    c: Coincident(g6,g-24)
    c: Equal(g7,g-20)
    c: Coincident(g7,g-20)
    c: Equal(g9,g-22)
    c: Coincident(g9,g-22)
    c: Equal(g8,g-21)
    c: Coincident(g8,g-21)
    c: Equal(g13,g-12)
    c: Equal(g12,g-14)
    c: Equal(g10,g-9)
    c: Equal(g11,g-7)
    c: Coincident(g14,g-27)
    c: Coincident(g14,g-27)
    c: Coincident(g15,g14)
    c: Coincident(g15,g-5)
    c: Coincident(g16,g15)
    c: Coincident(g16,g-6)
    c: Coincident(g17,g16)
    c: Coincident(g17,g-7)
    c: Coincident(g11,g17)
    c: Coincident(g11,g-8)
    c: Coincident(g18,g11)
    c: Coincident(g18,g-9)
    c: Coincident(g10,g18)
    c: Coincident(g10,g-10)
    c: Coincident(g19,g10)
    c: Coincident(g19,g-11)
    c: Coincident(g20,g19)
    c: Coincident(g20,g-12)
    c: Coincident(g13,g20)
    c: Coincident(g13,g-13)
    c: Coincident(g21,g13)
    c: Coincident(g21,g-14)
    c: Coincident(g12,g21)
    c: Coincident(g12,g-15)
    c: Coincident(g22,g12)
    c: Coincident(g22,g-15)
    c: Coincident(g23,g22)
    c: Coincident(g23,g14)
    c: Coincident(g24,g-18)
    c: Coincident(g24,g-16)
    c: Coincident(g25,g24)
    c: Coincident(g25,g-19)
    c: Coincident(g26,g25)
    c: Coincident(g26,g-19)
    c: Coincident(g27,g26)
    c: Coincident(g27,g24)
    c: Coincident(g29,g10)
    c: Coincident(g28,g10)
    c: Coincident(g29,g28)
    c: Parallel(g28,g18)
    c: Parallel(g29,g19)
FEATURE [PartDesign::Pad] Pad011
  Direction = (0,1,-2e-16)
  Length = 2
  Length2 = 10
  Profile = -> Sketch114
  ReferenceAxis = -> Sketch114 [N_Axis]
  Refine = true
  Reversed = true
  Suppressed = false
  Type = 0
FEATURE [Sketcher::SketchObject] Sketch115
  ArcFitTolerance = 1e-06
  AttachmentSupport = -> [Pad011]
  ExternalGeometry = -> [Binder001]
  FullyConstrained = true
  MakeInternals = false
  MapMode = 5
  Placement = pos=(0,1.7e-15,0) rot=(0,0.707107,0.707107;3.14159rad)
  sketch-geometry (4):
    g0: ArcOfCircle CenterX=24.2 CenterY=26.7 CenterZ=0 NormalX=0 NormalY=0 NormalZ=1 AngleXU=0 Radius=3 StartAngle=4.48384e-08 EndAngle=3.14159
    g1: ArcOfCircle CenterX=24.2 CenterY=15.7 CenterZ=0 NormalX=0 NormalY=0 NormalZ=1 AngleXU=0 Radius=3 StartAngle=3.14159 EndAngle=6.28318
    g2: LineSegment StartX=21.2 StartY=26.7 StartZ=0 EndX=21.2 EndY=15.7 EndZ=0
    g3: LineSegment StartX=27.2 StartY=26.7 StartZ=0 EndX=27.2 EndY=15.7 EndZ=0
  constraints (12):
    c: Equal(g1,g-4)
    c: Equal(g0,g-3)
    c: Coincident(g0,g-3)
    c: Coincident(g1,g-4)
    c: Vertical(g2)
    c: Vertical(g3)
    c: Tangent(g3,g-3)
    c: Tangent(g2,g-3)
    c: Coincident(g0,g2)
    c: Coincident(g0,g3)
    c: Coincident(g1,g2)
    c: Coincident(g3,g1)
FEATURE [Sketcher::SketchObject] Sketch117  label="Sketch117 - fori per inserto M3 x 3 x 4.5"
  ArcFitTolerance = 1e-06
  AttachmentSupport = -> [Pad011]
  ExternalGeometry = -> [Binder001]
  FullyConstrained = true
  MakeInternals = false
  MapMode = 5
  Placement = pos=(0,1.7e-15,0) rot=(0,0.707107,0.707107;3.14159rad)
  sketch-geometry (4):
    g0: Circle CenterX=43.2 CenterY=30.3 CenterZ=0 NormalX=0 NormalY=0 NormalZ=1 AngleXU=0 Radius=2.25
    g1: Circle CenterX=43.2 CenterY=12.1 CenterZ=0 NormalX=0 NormalY=0 NormalZ=1 AngleXU=0 Radius=2.25
    g2: Circle CenterX=18.6 CenterY=30.3 CenterZ=0 NormalX=0 NormalY=0 NormalZ=1 AngleXU=0 Radius=2.25
    g3: Circle CenterX=18.6 CenterY=12.1 CenterZ=0 NormalX=0 NormalY=0 NormalZ=1 AngleXU=0 Radius=2.25
  constraints (8):
    c: Diameter(g0) = 4.5
    c: Diameter(g1) = 4.5
    c: Diameter(g2) = 4.5
    c: Diameter(g3) = 4.5
    c: Coincident(g2,g-3)
    c: Coincident(g3,g-6)
    c: Coincident(g0,g-4)
    c: Coincident(g1,g-5)
FEATURE [Sketcher::SketchObject] Sketch118
  ArcFitTolerance = 1e-06
  AttachmentSupport = -> [Pad011]
  ExternalGeometry = -> [Binder001]
  FullyConstrained = true
  MakeInternals = false
  MapMode = 5
  Placement = pos=(0,-2,0) rot=(1,0,0;1.5708rad)
  sketch-geometry (12):
    g0: Circle CenterX=-78.51 CenterY=34.8 CenterZ=0 NormalX=0 NormalY=0 NormalZ=1 AngleXU=0 Radius=1.8
    g1: Circle CenterX=-78.51 CenterY=7.6 CenterZ=0 NormalX=0 NormalY=0 NormalZ=1 AngleXU=0 Radius=1.8
    g2: Circle CenterX=-5.6 CenterY=34.8 CenterZ=0 NormalX=0 NormalY=0 NormalZ=1 AngleXU=0 Radius=1.8
    g3: Circle CenterX=-5.6 CenterY=7.6 CenterZ=0 NormalX=0 NormalY=0 NormalZ=1 AngleXU=0 Radius=1.8
    g4: LineSegment StartX=0 StartY=39.2 StartZ=0 EndX=0 EndY=3.2 EndZ=0
    g5: LineSegment StartX=0 StartY=3.2 StartZ=0 EndX=-82.8 EndY=3.2 EndZ=0
    g6: LineSegment StartX=-82.8 StartY=3.2 StartZ=0 EndX=-82.8 EndY=39.2 EndZ=0
    g7: LineSegment StartX=-82.8 StartY=39.2 StartZ=0 EndX=0 EndY=39.2 EndZ=0
    g8: ArcOfCircle CenterX=-65 CenterY=21.2 CenterZ=0 NormalX=0 NormalY=0 NormalZ=1 AngleXU=0 Radius=10 StartAngle=1.5708 EndAngle=4.71239
    g9: ArcOfCircle CenterX=-19 CenterY=21.2 CenterZ=0 NormalX=0 NormalY=0 NormalZ=1 AngleXU=0 Radius=10 StartAngle=4.71239 EndAngle=7.85398
    g10: LineSegment StartX=-65 StartY=31.2 StartZ=0 EndX=-19 EndY=31.2 EndZ=0
    g11: LineSegment StartX=-65 StartY=11.2 StartZ=0 EndX=-19 EndY=11.2 EndZ=0
  constraints (25):
    c: Equal(g2,g-5)
    c: Equal(g3,g-7)
    c: Equal(g1,g-6)
    c: Equal(g0,g-4)
    c: Coincident(g0,g-4)
    c: Coincident(g1,g-6)
    c: Coincident(g3,g-7)
    c: Coincident(g2,g-5)
    c: Coincident(g4,g-8)
    c: Coincident(g4,g-9)
    c: Coincident(g5,g4)
    c: Coincident(g5,g-10)
    c: Coincident(g6,g5)
    c: PointOnObject(g6,g-3)
    c: Vertical(g6)
    c: Coincident(g7,g6)
    c: Coincident(g7,g4)
    c: Tangent(g8,g10) = 1.5708
    c: Tangent(g8,g11) = -1.5708
    c: Tangent(g9,g10) = 1.5708
    c: Tangent(g9,g11) = -1.5708
    c: Equal(g8,g9)
    c: Radius(g8) = 10
    c: Coincident(g8,g-11)
    c: Coincident(g9,g-12)
FEATURE [Sketcher::SketchObject] Sketch120
  ArcFitTolerance = 1e-06
  AttachmentSupport = -> [Pad011]
  ExternalGeometry = -> [Binder001]
  FullyConstrained = true
  MakeInternals = false
  MapMode = 5
  Placement = pos=(0,-2,0) rot=(1,0,0;1.5708rad)
  sketch-geometry (4):
    g0: LineSegment StartX=-137.815 StartY=39.2 StartZ=0 EndX=-142.655 EndY=24.303 EndZ=0
    g1: LineSegment StartX=-137.815 StartY=39.2 StartZ=0 EndX=-110.815 EndY=39.2 EndZ=0
    g2: LineSegment StartX=-142.655 StartY=24.303 StartZ=0 EndX=-110.815 EndY=24.303 EndZ=0
    g3: ArcOfCircle CenterX=-92.2534 CenterY=31.7515 CenterZ=0 NormalX=0 NormalY=0 NormalZ=1 AngleXU=0 Radius=20 StartAngle=2.75997 EndAngle=3.52321
  constraints (12):
    c: PointOnObject(g0,g-3)
    c: Coincident(g1,g0)
    c: PointOnObject(g1,g-3)
    c: Coincident(g2,g0)
    c: Horizontal(g2)
    c: Tangent(g0,g-4)
    c: Vertical(g2,g1)
    c: DistanceX(g1,g1) = 27
    c: DistanceY(g-6,g0) = 4
    c: Radius(g3) = 20
    c: Coincident(g3,g1)
    c: Coincident(g3,g2)
FEATURE [Sketcher::SketchObject] Sketch121
  ArcFitTolerance = 1e-06
  AttachmentSupport = -> [Pad011]
  ExternalGeometry = -> [Binder001]
  FullyConstrained = true
  MakeInternals = false
  MapMode = 5
  Placement = pos=(0,-2,0) rot=(1,0,0;1.5708rad)
  sketch-geometry (15):
    g0: LineSegment StartX=-137.815 StartY=39.2 StartZ=0 EndX=-143.955 EndY=20.303 EndZ=0
    g1: LineSegment StartX=-143.955 StartY=20.303 StartZ=0 EndX=-190.141 EndY=20.303 EndZ=0
    g2: LineSegment StartX=-190.141 StartY=20.303 StartZ=0 EndX=-186.139 EndY=31.3 EndZ=0
    g3: LineSegment StartX=-178.754 StartY=39.2 StartZ=0 EndX=-180.791 EndY=33.6029 EndZ=0
    g4: ArcOfCircle CenterX=-184.08 CenterY=34.8 CenterZ=0 NormalX=0 NormalY=0 NormalZ=1 AngleXU=0 Radius=3.5 StartAngle=4.71239 EndAngle=5.93412
    g5: LineSegment StartX=-184.08 StartY=31.3 StartZ=0 EndX=-186.139 EndY=31.3 EndZ=0
    g6: LineSegment StartX=-137.815 StartY=39.2 StartZ=0 EndX=-156.815 EndY=39.2 EndZ=0
    g7: LineSegment StartX=-168.815 StartY=39.2 StartZ=0 EndX=-178.754 EndY=39.2 EndZ=0
    g8: LineSegment StartX=-157.815 StartY=39.2 StartZ=0 EndX=-167.815 EndY=39.2 EndZ=0
    g9: LineSegment StartX=-168.815 StartY=31.2 StartZ=0 EndX=-156.815 EndY=31.2 EndZ=0
    g10: LineSegment StartX=-167.436 StartY=36.2 StartZ=0 EndX=-157.436 EndY=36.2 EndZ=0
    g11: ArcOfCircle CenterX=-176.411 CenterY=35.2 CenterZ=0 NormalX=0 NormalY=0 NormalZ=1 AngleXU=0 Radius=20 StartAngle=6.08183 EndAngle=6.48454
    g12: ArcOfCircle CenterX=-188.411 CenterY=35.2 CenterZ=0 NormalX=0 NormalY=0 NormalZ=1 AngleXU=0 Radius=20 StartAngle=6.08183 EndAngle=6.48454
    g13: ArcOfCircle CenterX=-177.411 CenterY=35.2 CenterZ=0 NormalX=0 NormalY=0 NormalZ=1 AngleXU=0 Radius=20 StartAngle=0.0500209 EndAngle=0.201358
    g14: ArcOfCircle CenterX=-187.411 CenterY=35.2 CenterZ=0 NormalX=0 NormalY=0 NormalZ=1 AngleXU=0 Radius=20 StartAngle=0.0500209 EndAngle=0.201358
  constraints (46):
    c: PointOnObject(g0,g-3)
    c: Tangent(g0,g-5)
    c: Coincident(g1,g0)
    c: Horizontal(g1)
    c: Coincident(g2,g1)
    c: PointOnObject(g3,g-3)
    c: Parallel(g3,g-6)
    c: Parallel(g2,g-6)
    c: Radius(g4) = 3.5
    c: Coincident(g4,g-7)
    c: Tangent(g3,g4) = 1.5708
    c: Horizontal(g5)
    c: Tangent(g5,g4) = 1.5708
    c: DistanceX(g-8,g5) = 3.8
    c: Coincident(g2,g5)
    c: Coincident(g6,g0)
    c: PointOnObject(g6,g-3)
    c: DistanceX(g6,g6) = 19
    c: PointOnObject(g7,g-3)
    c: DistanceX(g7,g6) = 12
    c: Coincident(g7,g3)
    c: PointOnObject(g8,g-3)
    c: PointOnObject(g8,g-3)
    c: DistanceX(g8,g8) = 10
    c: DistanceX(g8,g6) = 1
    c: Horizontal(g9)
    c: Vertical(g7,g9)
    c: Vertical(g6,g9)
    c: DistanceY(g9,g7) = 8
    c: Horizontal(g10)
    c: Equal(g8,g10)
    c: DistanceY(g10,g8) = 3
    c: Radius(g11) = 20
    c: Coincident(g11,g6)
    c: Coincident(g11,g9)
    c: Radius(g12) = 20
    c: Coincident(g12,g7)
    c: Coincident(g12,g9)
    c: Equal(g13,g11)
    c: Coincident(g13,g8)
    c: Coincident(g13,g10)
    c: Horizontal(g13,g11)
    c: Equal(g14,g12)
    c: Coincident(g14,g8)
    c: Coincident(g14,g10)
    c: Horizontal(g1,g-6)
FEATURE [Sketcher::SketchObject] Sketch122
  ArcFitTolerance = 1e-06
  AttachmentSupport = -> [Pad011]
  ExternalGeometry = -> [Binder001]
  FullyConstrained = true
  MakeInternals = false
  MapMode = 5
  Placement = pos=(0,-2,0) rot=(1,0,0;1.5708rad)
  sketch-geometry (8):
    g0: ArcOfCircle CenterX=-184.801 CenterY=-67.3089 CenterZ=0 NormalX=0 NormalY=0 NormalZ=1 AngleXU=0 Radius=33.7833 StartAngle=2.70526 EndAngle=3.54053
    g1: LineSegment StartX=-176.685 StartY=-80.4316 StartZ=0 EndX=-215.932 EndY=-80.4316 EndZ=0
    g2: LineSegment StartX=-215.42 StartY=-53.0314 StartZ=0 EndX=-192.176 EndY=-3.18454 EndZ=0
    g3: ArcOfCircle CenterX=-207.583 CenterY=4 CenterZ=0 NormalX=0 NormalY=0 NormalZ=1 AngleXU=0 Radius=17 StartAngle=5.84685 EndAngle=7.56663
    g4: Circle CenterX=-213.443 CenterY=-76.8316 CenterZ=0 NormalX=0 NormalY=0 NormalZ=1 AngleXU=0 Radius=3
    g5: Circle CenterX=-179.305 CenterY=-76.8316 CenterZ=0 NormalX=0 NormalY=0 NormalZ=1 AngleXU=0 Radius=3
    g6: LineSegment StartX=-143.955 StartY=20.303 StartZ=0 EndX=-176.685 EndY=-80.4316 EndZ=0
    g7: LineSegment StartX=-202.765 StartY=20.303 StartZ=0 EndX=-143.955 EndY=20.303 EndZ=0
  constraints (18):
    c: Coincident(g0,g-7)
    c: Coincident(g0,g-8)
    c: Coincident(g1,g0)
    c: Tangent(g2,g-5)
    c: Coincident(g3,g-6)
    c: Coincident(g2,g3)
    c: Coincident(g0,g2)
    c: Diameter(g4) = 6
    c: Diameter(g5) = 6
    c: Coincident(g4,g-9)
    c: Coincident(g5,g-10)
    c: Horizontal(g1)
    c: Coincident(g6,g1)
    c: Tangent(g6,g-4)
    c: Coincident(g3,g-6)
    c: Coincident(g7,g3)
    c: Horizontal(g7)
    c: Coincident(g7,g6)
FEATURE [Sketcher::SketchObject] Sketch123
  ArcFitTolerance = 1e-06
  AttachmentSupport = -> [Pad011]
  ExternalGeometry = -> [Binder001]
  FullyConstrained = true
  MakeInternals = false
  MapMode = 5
  Placement = pos=(0,-2,0) rot=(1,0,0;1.5708rad)
  sketch-geometry (4):
    g0: LineSegment StartX=-108 StartY=36.8 StartZ=0 EndX=-90 EndY=36.8 EndZ=0
    g1: LineSegment StartX=-108 StartY=36.8 StartZ=0 EndX=-108 EndY=26.8 EndZ=0
    g2: LineSegment StartX=-108 StartY=26.8 StartZ=0 EndX=-90 EndY=26.8 EndZ=0
    g3: ArcOfCircle CenterX=-94 CenterY=31.8 CenterZ=0 NormalX=0 NormalY=0 NormalZ=1 AngleXU=0 Radius=6.40312 StartAngle=5.38713 EndAngle=7.17924
  constraints (13):
    c: Horizontal(g0)
    c: Coincident(g1,g0)
    c: Vertical(g1)
    c: Coincident(g2,g1)
    c: Horizontal(g2)
    c: DistanceX(g0,g0) = 18
    c: DistanceY(g1,g1) = 10
    c: Equal(g0,g2)
    c: DistanceX(g0,g-3) = 90
    c: DistanceY(g0,g-3) = 2.4
    c: Coincident(g3,g0)
    c: Coincident(g3,g2)
    c: DistanceX(g3,g0) = 4
FEATURE [PartDesign::Chamfer] Chamfer014
  Angle = 45
  Base = -> Pad011 [Edge80,Edge4,Edge7]
  BaseFeature = -> Pad011
  ChamferType = 0
  FlipDirection = false
  Refine = true
  Size = 1.9
  Size2 = 1
  SupportTransform = false
  Suppressed = false
  UseAllEdges = false
FEATURE [PartDesign::Pocket] Pocket006
  BaseFeature = -> Chamfer014
  Direction = (0,-1,2e-16)
  Length = 1.2
  Length2 = 5
  Profile = -> Sketch115
  ReferenceAxis = -> Sketch115 [N_Axis]
  Refine = true
  Suppressed = false
  Type = 0
FEATURE [Sketcher::SketchObject] Sketch116  label="Sketch116 - pieno per inserto M3 x 3 x 4,5"
  ArcFitTolerance = 1e-06
  AttachmentSupport = -> [Pocket006]
  ExternalGeometry = -> [Binder001]
  FullyConstrained = true
  MakeInternals = false
  MapMode = 5
  Placement = pos=(0,1.7e-15,0) rot=(0,0.707107,0.707107;3.14159rad)
  sketch-geometry (4):
    g0: Circle CenterX=43.2 CenterY=30.3 CenterZ=0 NormalX=0 NormalY=0 NormalZ=1 AngleXU=0 Radius=3.4
    g1: Circle CenterX=43.2 CenterY=12.1 CenterZ=0 NormalX=0 NormalY=0 NormalZ=1 AngleXU=0 Radius=3.4
    g2: Circle CenterX=18.6 CenterY=30.3 CenterZ=0 NormalX=0 NormalY=0 NormalZ=1 AngleXU=0 Radius=3.4
    g3: Circle CenterX=18.6 CenterY=12.1 CenterZ=0 NormalX=0 NormalY=0 NormalZ=1 AngleXU=0 Radius=3.4
  constraints (8):
    c: Diameter(g0) = 6.8
    c: Diameter(g1) = 6.8
    c: Diameter(g2) = 6.8
    c: Diameter(g3) = 6.8
    c: Coincident(g2,g-3)
    c: Coincident(g0,g-4)
    c: Coincident(g3,g-6)
    c: Coincident(g1,g-5)
FEATURE [PartDesign::Pad] Pad012
  BaseFeature = -> Pocket006
  Direction = (0,1,-2e-16)
  Length = 2.4
  Length2 = 10
  Profile = -> Sketch116
  ReferenceAxis = -> Sketch116 [N_Axis]
  Refine = true
  Suppressed = false
  Type = 0
FEATURE [PartDesign::Pocket] Pocket007
  BaseFeature = -> Pad012
  Direction = (0,-1,2e-16)
  Length = 0.6
  Length2 = 2.4
  Profile = -> Sketch117
  ReferenceAxis = -> Sketch117 [N_Axis]
  Refine = true
  Suppressed = false
  Type = 4
FEATURE [PartDesign::Pad] Pad013
  BaseFeature = -> Pocket007
  Direction = (0,-1,2e-16)
  Length = 1.6
  Length2 = 10
  Profile = -> Sketch118
  ReferenceAxis = -> Sketch118 [N_Axis]
  Refine = true
  Suppressed = false
  Type = 0
FEATURE [Sketcher::SketchObject] Sketch119
  ArcFitTolerance = 1e-06
  AttachmentSupport = -> [Pad013]
  ExternalGeometry = -> [Binder001]
  FullyConstrained = true
  MakeInternals = false
  MapMode = 5
  Placement = pos=(0,-3.6,0) rot=(1,0,0;1.5708rad)
  sketch-geometry (21):
    g0: LineSegment [constr] StartX=-82.8 StartY=3.2 StartZ=0 EndX=-82.8 EndY=39.2 EndZ=0
    g1: ArcOfCircle CenterX=-78.51 CenterY=34.8 CenterZ=0 NormalX=0 NormalY=0 NormalZ=1 AngleXU=0 Radius=3.5 StartAngle=4.71239 EndAngle=6.28319
    g2: ArcOfCircle CenterX=-78.51 CenterY=7.6 CenterZ=0 NormalX=0 NormalY=0 NormalZ=1 AngleXU=0 Radius=3.5 StartAngle=0 EndAngle=1.5708
    g3: ArcOfCircle CenterX=-5.6 CenterY=34.8 CenterZ=0 NormalX=0 NormalY=0 NormalZ=1 AngleXU=0 Radius=3.5 StartAngle=3.14159 EndAngle=4.71239
    g4: ArcOfCircle CenterX=-5.6 CenterY=7.6 CenterZ=0 NormalX=0 NormalY=0 NormalZ=1 AngleXU=0 Radius=3.5 StartAngle=1.5708 EndAngle=3.14159
    g5: LineSegment StartX=0 StartY=39.2 StartZ=0 EndX=0 EndY=31.3 EndZ=0
    g6: LineSegment StartX=0 StartY=39.2 StartZ=0 EndX=-9.1 EndY=39.2 EndZ=0
    g7: LineSegment StartX=0 StartY=3.2 StartZ=0 EndX=0 EndY=11.1 EndZ=0
    g8: LineSegment StartX=0 StartY=3.2 StartZ=0 EndX=-9.1 EndY=3.2 EndZ=0
    g9: LineSegment StartX=-82.8 StartY=3.2 StartZ=0 EndX=-75.01 EndY=3.2 EndZ=0
    g10: LineSegment StartX=-82.8 StartY=3.2 StartZ=0 EndX=-82.8 EndY=11.1 EndZ=0
    g11: LineSegment StartX=-82.8 StartY=39.2 StartZ=0 EndX=-82.8 EndY=31.3 EndZ=0
    g12: LineSegment StartX=-82.8 StartY=39.2 StartZ=0 EndX=-75.01 EndY=39.2 EndZ=0
    g13: LineSegment StartX=-82.8 StartY=31.3 StartZ=0 EndX=-78.51 EndY=31.3 EndZ=0
    g14: LineSegment StartX=-75.01 StartY=39.2 StartZ=0 EndX=-75.01 EndY=34.8 EndZ=0
    g15: LineSegment StartX=-82.8 StartY=11.1 StartZ=0 EndX=-78.51 EndY=11.1 EndZ=0
    g16: LineSegment StartX=-75.01 StartY=3.2 StartZ=0 EndX=-75.01 EndY=7.6 EndZ=0
    g17: LineSegment StartX=-9.1 StartY=39.2 StartZ=0 EndX=-9.1 EndY=34.8 EndZ=0
    g18: LineSegment StartX=0 StartY=31.3 StartZ=0 EndX=-5.6 EndY=31.3 EndZ=0
    g19: LineSegment StartX=0 StartY=11.1 StartZ=0 EndX=-5.6 EndY=11.1 EndZ=0
    g20: LineSegment StartX=-9.1 StartY=3.2 StartZ=0 EndX=-9.1 EndY=7.6 EndZ=0
  constraints (51):
    c: Coincident(g0,g-10)
    c: PointOnObject(g0,g-8)
    c: Vertical(g0)
    c: Coincident(g1,g-3)
    c: Coincident(g2,g-4)
    c: Coincident(g3,g-5)
    c: Coincident(g4,g-6)
    c: Radius(g4) = 3.5
    c: Radius(g3) = 3.5
    c: Radius(g1) = 3.5
    c: Radius(g2) = 3.5
    c: Coincident(g5,g-9)
    c: PointOnObject(g5,g-9)
    c: Coincident(g6,g5)
    c: PointOnObject(g6,g-8)
    c: Coincident(g7,g-9)
    c: PointOnObject(g7,g-9)
    c: Coincident(g8,g7)
    c: PointOnObject(g8,g-7)
    c: Coincident(g9,g0)
    c: PointOnObject(g9,g-7)
    c: Coincident(g10,g0)
    c: PointOnObject(g10,g0)
    c: Coincident(g11,g0)
    c: PointOnObject(g11,g0)
    c: Coincident(g12,g0)
    c: PointOnObject(g12,g-8)
    c: Coincident(g13,g11)
    c: Horizontal(g13)
    c: Coincident(g14,g12)
    c: Vertical(g14)
    c: Coincident(g15,g10)
    c: Horizontal(g15)
    c: Coincident(g16,g9)
    c: Vertical(g16)
    c: Coincident(g17,g6)
    c: Vertical(g17)
    c: Coincident(g18,g5)
    c: Horizontal(g18)
    c: Coincident(g19,g7)
    c: Horizontal(g19)
    c: Coincident(g20,g8)
    c: Vertical(g20)
    c: Tangent(g20,g4) = 1.5708
    c: Tangent(g4,g19) = -1.5708
    c: Tangent(g18,g3) = 1.5708
    c: Tangent(g3,g17) = -1.5708
    c: Tangent(g13,g1) = -1.5708
    c: Tangent(g1,g14) = 1.5708
    c: Tangent(g16,g2) = -1.5708
    c: Tangent(g2,g15) = 1.5708
FEATURE [PartDesign::Pocket] Pocket008
  BaseFeature = -> Pad013
  Direction = (0,1,-2e-16)
  Length = 1.6
  Length2 = 5
  Profile = -> Sketch119
  ReferenceAxis = -> Sketch119 [N_Axis]
  Refine = true
  Suppressed = false
  Type = 0
FEATURE [PartDesign::Pad] Pad017
  BaseFeature = -> Pocket008
  Direction = (0,-1,2e-16)
  Length = 1.6
  Length2 = 10
  Profile = -> Sketch123
  ReferenceAxis = -> Sketch123 [N_Axis]
  Refine = true
  Suppressed = false
  Type = 0
FEATURE [Sketcher::SketchObject] Sketch125
  ArcFitTolerance = 1e-06
  AttachmentSupport = -> [Pad017]
  ExternalGeometry = -> [Pad017]
  FullyConstrained = true
  MakeInternals = false
  MapMode = 5
  Placement = pos=(0,-3.6,8e-16) rot=(1,0,0;1.5708rad)
  sketch-geometry (20):
    g0: LineSegment StartX=-108 StartY=35.8 StartZ=0 EndX=-108 EndY=35 EndZ=0
    g1: LineSegment StartX=-108 StartY=35 StartZ=0 EndX=-97 EndY=35 EndZ=0
    g2: LineSegment StartX=-97 StartY=35 StartZ=0 EndX=-97 EndY=35.8 EndZ=0
    g3: LineSegment StartX=-97 StartY=35.8 StartZ=0 EndX=-108 EndY=35.8 EndZ=0
    g4: LineSegment StartX=-108 StartY=28.6 StartZ=0 EndX=-108 EndY=27.8 EndZ=0
    g5: LineSegment StartX=-108 StartY=27.8 StartZ=0 EndX=-97 EndY=27.8 EndZ=0
    g6: LineSegment StartX=-97 StartY=27.8 StartZ=0 EndX=-97 EndY=28.6 EndZ=0
    g7: LineSegment StartX=-97 StartY=28.6 StartZ=0 EndX=-108 EndY=28.6 EndZ=0
    g8: LineSegment StartX=-108 StartY=30.4 StartZ=0 EndX=-108 EndY=29.6 EndZ=0
    g9: LineSegment StartX=-108 StartY=29.6 StartZ=0 EndX=-97 EndY=29.6 EndZ=0
    g10: LineSegment StartX=-97 StartY=29.6 StartZ=0 EndX=-97 EndY=30.4 EndZ=0
    g11: LineSegment StartX=-97 StartY=30.4 StartZ=0 EndX=-108 EndY=30.4 EndZ=0
    g12: LineSegment StartX=-108 StartY=32.2 StartZ=0 EndX=-108 EndY=31.4 EndZ=0
    g13: LineSegment StartX=-108 StartY=31.4 StartZ=0 EndX=-97 EndY=31.4 EndZ=0
    g14: LineSegment StartX=-97 StartY=31.4 StartZ=0 EndX=-97 EndY=32.2 EndZ=0
    g15: LineSegment StartX=-97 StartY=32.2 StartZ=0 EndX=-108 EndY=32.2 EndZ=0
    g16: LineSegment StartX=-108 StartY=34 StartZ=0 EndX=-108 EndY=33.2 EndZ=0
    g17: LineSegment StartX=-108 StartY=33.2 StartZ=0 EndX=-97 EndY=33.2 EndZ=0
    g18: LineSegment StartX=-97 StartY=33.2 StartZ=0 EndX=-97 EndY=34 EndZ=0
    g19: LineSegment StartX=-97 StartY=34 StartZ=0 EndX=-108 EndY=34 EndZ=0
  constraints (55):
    c: Coincident(g1,g0)
    c: Horizontal(g1)
    c: Coincident(g2,g1)
    c: Vertical(g2)
    c: Coincident(g3,g2)
    c: Horizontal(g3)
    c: Coincident(g3,g0)
    c: DistanceX(g1,g1) = 11
    c: DistanceY(g2,g2) = 0.8
    c: Coincident(g5,g4)
    c: Horizontal(g5)
    c: Coincident(g6,g5)
    c: Vertical(g6)
    c: Coincident(g7,g6)
    c: Horizontal(g7)
    c: Coincident(g7,g4)
    c: Coincident(g9,g8)
    c: Horizontal(g9)
    c: Coincident(g10,g9)
    c: Vertical(g10)
    c: Coincident(g11,g10)
    c: Horizontal(g11)
    c: Coincident(g11,g8)
    c: Coincident(g13,g12)
    c: Horizontal(g13)
    c: Coincident(g14,g13)
    c: Vertical(g14)
    c: Coincident(g15,g14)
    c: Horizontal(g15)
    c: Coincident(g15,g12)
    c: Coincident(g17,g16)
    c: Horizontal(g17)
    c: Coincident(g18,g17)
    c: Vertical(g18)
    c: Coincident(g19,g18)
    c: Horizontal(g19)
    c: Coincident(g19,g16)
    c: Equal(g3,g19)
    c: Equal(g3,g15)
    c: Equal(g3,g11)
    c: Equal(g3,g7)
    c: Equal(g2,g18)
    c: Equal(g2,g14)
    c: Equal(g2,g10)
    c: Equal(g2,g6)
    c: DistanceY(g-4,g4) = 1
    c: DistanceY(g4,g8) = 1
    c: DistanceY(g8,g12) = 1
    c: DistanceY(g12,g16) = 1
    c: DistanceY(g16,g0) = 1
    c: Tangent(g0,g-5)
    c: Tangent(g16,g-5)
    c: Tangent(g12,g-5)
    c: Tangent(g8,g-5)
    c: Tangent(g4,g-5)
FEATURE [PartDesign::Chamfer] Chamfer009
  Angle = 45
  Base = -> Pad017 [Edge151,Edge154]
  BaseFeature = -> Pad017
  ChamferType = 1
  FlipDirection = false
  Refine = true
  Size = 1.5
  Size2 = 2.8
  SupportTransform = false
  Suppressed = false
  UseAllEdges = false
FEATURE [PartDesign::Pocket] Pocket009
  BaseFeature = -> Chamfer009
  Direction = (0,1,-2e-16)
  Length = 1
  Length2 = 5
  Profile = -> Sketch125
  ReferenceAxis = -> Sketch125 [N_Axis]
  Refine = true
  Suppressed = false
  Type = 0
FEATURE [PartDesign::Pad] Pad014
  BaseFeature = -> Pocket009
  Direction = (0,-1,2e-16)
  Length = 0.8
  Length2 = 10
  Profile = -> Sketch120
  ReferenceAxis = -> Sketch120 [N_Axis]
  Refine = true
  Suppressed = false
  Type = 0
FEATURE [Sketcher::SketchObject] Sketch124
  ArcFitTolerance = 1e-06
  AttachmentSupport = -> [Pad014]
  ExternalGeometry = -> [Binder001]
  FullyConstrained = true
  MakeInternals = false
  MapMode = 5
  Placement = pos=(0,-2.8,6e-16) rot=(1,0,0;1.5708rad)
  sketch-geometry (4):
    g0: LineSegment StartX=-129 StartY=39.2 StartZ=0 EndX=-131.599 EndY=31.2 EndZ=0
    g1: LineSegment StartX=-118 StartY=39.2 StartZ=0 EndX=-120.599 EndY=31.2 EndZ=0
    g2: LineSegment StartX=-129 StartY=39.2 StartZ=0 EndX=-118 EndY=39.2 EndZ=0
    g3: LineSegment StartX=-120.599 StartY=31.2 StartZ=0 EndX=-131.599 EndY=31.2 EndZ=0
  constraints (12):
    c: PointOnObject(g0,g-3)
    c: PointOnObject(g1,g-3)
    c: Parallel(g-4,g0)
    c: Parallel(g-4,g1)
    c: Coincident(g2,g0)
    c: Coincident(g2,g1)
    c: DistanceX(g2,g2) = 11
    c: DistanceY(g1,g1) = 8
    c: Coincident(g3,g1)
    c: Horizontal(g3)
    c: Coincident(g3,g0)
    c: DistanceX(g1,g-3) = 118
FEATURE [PartDesign::Pad] Pad018
  BaseFeature = -> Pad014
  Direction = (0,-1,2e-16)
  Length = 1.2
  Length2 = 10
  Profile = -> Sketch124
  ReferenceAxis = -> Sketch124 [N_Axis]
  Refine = true
  Suppressed = false
  Type = 0
FEATURE [Sketcher::SketchObject] Sketch126
  ArcFitTolerance = 1e-06
  AttachmentSupport = -> [Pad018]
  ExternalGeometry = -> [Pad018]
  FullyConstrained = true
  MakeInternals = false
  MapMode = 5
  Placement = pos=(0,-4,0) rot=(1,0,0;1.5708rad)
  sketch-geometry (8):
    g0: LineSegment StartX=-129.877 StartY=36.5 StartZ=0 EndX=-130.137 EndY=35.7 EndZ=0
    g1: LineSegment StartX=-130.69 StartY=34 StartZ=0 EndX=-130.95 EndY=33.2 EndZ=0
    g2: LineSegment StartX=-129.877 StartY=36.5 StartZ=0 EndX=-118.877 EndY=36.5 EndZ=0
    g3: LineSegment StartX=-130.137 StartY=35.7 StartZ=0 EndX=-119.137 EndY=35.7 EndZ=0
    g4: LineSegment StartX=-130.69 StartY=34 StartZ=0 EndX=-119.69 EndY=34 EndZ=0
    g5: LineSegment StartX=-130.95 StartY=33.2 StartZ=0 EndX=-119.95 EndY=33.2 EndZ=0
    g6: LineSegment StartX=-118.877 StartY=36.5 StartZ=0 EndX=-119.137 EndY=35.7 EndZ=0
    g7: LineSegment StartX=-119.69 StartY=34 StartZ=0 EndX=-119.95 EndY=33.2 EndZ=0
  constraints (20):
    c: Coincident(g2,g0)
    c: Horizontal(g2)
    c: Coincident(g3,g0)
    c: Horizontal(g3)
    c: Coincident(g4,g1)
    c: Horizontal(g4)
    c: Coincident(g5,g1)
    c: Horizontal(g5)
    c: Coincident(g6,g2)
    c: Coincident(g6,g3)
    c: Coincident(g7,g4)
    c: Coincident(g7,g5)
    c: Tangent(g0,g-4)
    c: Tangent(g6,g-5)
    c: Tangent(g1,g-4)
    c: Tangent(g7,g-5)
    c: DistanceY(g3,g2) = 0.8
    c: DistanceY(g5,g4) = 0.8
    c: DistanceY(g-6,g1) = 2
    c: DistanceY(g-6,g0) = 4.5
FEATURE [PartDesign::Chamfer] Chamfer008
  Angle = 45
  Base = -> Pad018 [Edge257]
  BaseFeature = -> Pad018
  ChamferType = 1
  FlipDirection = false
  Refine = true
  Size = 1
  Size2 = 6
  SupportTransform = false
  Suppressed = false
  UseAllEdges = false
FEATURE [PartDesign::Pocket] Pocket010
  BaseFeature = -> Chamfer008
  Direction = (0,1,-2e-16)
  Length = 1
  Length2 = 5
  Profile = -> Sketch126
  ReferenceAxis = -> Sketch126 [N_Axis]
  Refine = true
  Suppressed = false
  Type = 0
FEATURE [PartDesign::Pad] Pad015
  BaseFeature = -> Pocket010
  Direction = (0,-1,2e-16)
  Length = 2
  Length2 = 10
  Profile = -> Sketch121
  ReferenceAxis = -> Sketch121 [N_Axis]
  Refine = true
  Suppressed = false
  Type = 0
FEATURE [PartDesign::Pad] Pad016
  BaseFeature = -> Pad015
  Direction = (0,-1,2e-16)
  Length = 1.6
  Length2 = 10
  Profile = -> Sketch122
  ReferenceAxis = -> Sketch122 [N_Axis]
  Refine = true
  Suppressed = false
  Type = 0
FEATURE [Sketcher::SketchObject] Sketch129
  ArcFitTolerance = 1e-06
  AttachmentSupport = -> [Pad016]
  ExternalGeometry = -> [Binder001]
  FullyConstrained = true
  MakeInternals = false
  MapMode = 5
  Placement = pos=(0,-3.6,0) rot=(1,0,0;1.5708rad)
  sketch-geometry (12):
    g0: LineSegment [constr] StartX=-192.176 StartY=-3.18451 StartZ=0 EndX=-181.223 EndY=20.303 EndZ=0
    g1: LineSegment [constr] StartX=-202.765 StartY=20.303 StartZ=0 EndX=-181.223 EndY=20.303 EndZ=0
    g2: LineSegment StartX=-202.765 StartY=20.303 StartZ=0 EndX=-181.223 EndY=20.303 EndZ=0
    g3: LineSegment StartX=-192.176 StartY=-3.18451 StartZ=0 EndX=-196.804 EndY=-13.1107 EndZ=0
    g4: ArcOfCircle CenterX=-207.583 CenterY=4 CenterZ=0 NormalX=0 NormalY=0 NormalZ=1 AngleXU=0 Radius=17 StartAngle=5.84685 EndAngle=7.56663
    g5: ArcOfEllipse CenterX=-181.223 CenterY=8.55923 CenterZ=0 NormalX=0 NormalY=0 NormalZ=1 MajorRadius=23.4779 MinorRadius=11.7437 AngleXU=2e-16 StartAngle=4.71239 EndAngle=7.85398
    g6: LineSegment [constr] StartX=-157.745 StartY=8.55923 StartZ=0 EndX=-204.701 EndY=8.55923 EndZ=0
    g7: LineSegment [constr] StartX=-181.223 StartY=20.303 StartZ=0 EndX=-181.223 EndY=-3.18451 EndZ=0
    g8: GeomPoint [constr] X=-160.894 Y=8.55923 Z=0
    g9: GeomPoint [constr] X=-201.553 Y=8.55923 Z=0
    g10: ArcOfCircle CenterX=-181.223 CenterY=-20.3763 CenterZ=0 NormalX=0 NormalY=0 NormalZ=1 AngleXU=0 Radius=17.1918 StartAngle=1.57079 EndAngle=2.70526
    g11: GeomPoint [constr] X=-181.223 Y=-3.18451 Z=0
  constraints (23):
    c: Coincident(g0,g-5)
    c: Coincident(g1,g-6)
    c: Horizontal(g1)
    c: Coincident(g1,g0)
    c: Parallel(g0,g-4)
    c: Coincident(g2,g1)
    c: Coincident(g2,g0)
    c: Coincident(g3,g0)
    c: Equal(g4,g-5)
    c: Coincident(g4,g1)
    c: Coincident(g4,g0)
    c: InternalAlignment(g6-g9 -> g5) x4
    c: Vertical(g5,g0)
    c: Horizontal(g6)
    c: Coincident(g5,g0)
    c: DistanceX(g6,g-3) = 10.1
    c: Tangent(g10,g3) = -1.5708
    c: PointOnObject(g11,g10)
    c: Tangent(g5,g10,g11) = 1.5708
    c: Coincident(g10,g5)
    c: Coincident(g11,g7)
    c: Parallel(g3,g-4)
    c: Horizontal(g5,g0)
FEATURE [Sketcher::SketchObject] Sketch130
  ArcFitTolerance = 1e-06
  AttachmentOffset = pos=(0,0,-1.6) rot=(0,0,1;0rad)
  AttachmentSupport = -> [Pad016]
  ExternalGeometry = -> [Binder001]
  FullyConstrained = true
  MakeInternals = false
  MapMode = 5
  Placement = pos=(0,-2,-4e-16) rot=(1,0,0;1.5708rad)
  sketch-geometry (12):
    g0: LineSegment [constr] StartX=-192.176 StartY=-3.18451 StartZ=0 EndX=-181.223 EndY=20.303 EndZ=0
    g1: LineSegment [constr] StartX=-202.765 StartY=20.303 StartZ=0 EndX=-181.223 EndY=20.303 EndZ=0
    g2: LineSegment StartX=-202.765 StartY=20.303 StartZ=0 EndX=-181.223 EndY=20.303 EndZ=0
    g3: LineSegment StartX=-192.176 StartY=-3.18451 StartZ=0 EndX=-193.827 EndY=-6.72678 EndZ=0
    g4: ArcOfCircle CenterX=-207.583 CenterY=4 CenterZ=0 NormalX=0 NormalY=0 NormalZ=1 AngleXU=0 Radius=17 StartAngle=5.84685 EndAngle=7.56663
    g5: ArcOfEllipse CenterX=-181.223 CenterY=10.803 CenterZ=0 NormalX=0 NormalY=0 NormalZ=1 MajorRadius=14.4779 MinorRadius=9.5 AngleXU=0 StartAngle=4.71239 EndAngle=7.85398
    g6: LineSegment [constr] StartX=-166.745 StartY=10.803 StartZ=0 EndX=-195.701 EndY=10.803 EndZ=0
    g7: LineSegment [constr] StartX=-181.223 StartY=20.303 StartZ=0 EndX=-181.223 EndY=1.30297 EndZ=0
    g8: GeomPoint [constr] X=-170.298 Y=10.803 Z=0
    g9: GeomPoint [constr] X=-192.148 Y=10.803 Z=0
    g10: ArcOfCircle CenterX=-181.223 CenterY=-12.6042 CenterZ=0 NormalX=0 NormalY=0 NormalZ=1 AngleXU=0 Radius=13.9072 StartAngle=1.5708 EndAngle=2.70526
    g11: GeomPoint [constr] X=-181.223 Y=1.30297 Z=0
  constraints (23):
    c: Coincident(g0,g-5)
    c: Coincident(g1,g-6)
    c: Horizontal(g1)
    c: Coincident(g1,g0)
    c: Parallel(g0,g-4)
    c: Coincident(g2,g1)
    c: Coincident(g2,g0)
    c: Coincident(g3,g0)
    c: Equal(g4,g-5)
    c: Coincident(g4,g1)
    c: Coincident(g4,g0)
    c: InternalAlignment(g6-g9 -> g5) x4
    c: Vertical(g5,g0)
    c: Horizontal(g6)
    c: Coincident(g5,g0)
    c: DistanceX(g6,g-3) = 19.1
    c: Tangent(g10,g3) = -1.5708
    c: PointOnObject(g11,g10)
    c: Tangent(g5,g10,g11) = 1.5708
    c: Coincident(g10,g5)
    c: Coincident(g11,g7)
    c: Parallel(g3,g-4)
    c: DistanceY(g5,g0) = 19
FEATURE [Part::Part2DObjectPython] Clone2D001  label="Sketch130 (2D)"  # Draft 2D object (typed FeaturePython)
  Fuse = false
  Objects = -> [Sketch130]
  Placement = pos=(0,-2,-4e-16) rot=(1,0,0;1.5708rad)
  Scale = (1,1,1)
FEATURE [Sketcher::SketchObject] Sketch131
  ArcFitTolerance = 1e-06
  AttachmentOffset = pos=(0,0,-3.5) rot=(0,0,1;0rad)
  AttachmentSupport = -> [Pad016]
  ExternalGeometry = -> [Binder001]
  FullyConstrained = true
  MakeInternals = false
  MapMode = 5
  Placement = pos=(0,-0.1,-8e-16) rot=(1,0,0;1.5708rad)
  sketch-geometry (1):
    g0: GeomPoint X=-197.47 Y=8.55923 Z=0
  constraints (1):
    c: Symmetric(g-6,g-4,g0)
FEATURE [Sketcher::SketchObject] Sketch132
  ArcFitTolerance = 1e-06
  AttachmentSupport = -> [Pad016]
  ExternalGeometry = -> [Binder001]
  FullyConstrained = true
  MakeInternals = false
  MapMode = 5
  Placement = pos=(0,-3.6,0) rot=(1,0,0;1.5708rad)
  sketch-geometry (3):
    g0: LineSegment [constr] StartX=-215.42 StartY=-53.0314 StartZ=0 EndX=-167.782 EndY=-53.0314 EndZ=0
    g1: Circle CenterX=-191.282 CenterY=-53.0314 CenterZ=0 NormalX=0 NormalY=0 NormalZ=1 AngleXU=0 Radius=11.5
    g2: Circle CenterX=-191.282 CenterY=-53.0314 CenterZ=0 NormalX=0 NormalY=0 NormalZ=1 AngleXU=0 Radius=10.7
  constraints (8):
    c: Coincident(g0,g-3)
    c: PointOnObject(g0,g-4)
    c: Horizontal(g0)
    c: Diameter(g1) = 23
    c: PointOnObject(g1,g0)
    c: DistanceX(g1,g0) = 23.5
    c: Diameter(g2) = 21.4
    c: Coincident(g2,g1)
FEATURE [Part::Part2DObjectPython] ShapeString  # Draft 2D object (typed FeaturePython)
  FontFile = <path>
  Fuse = false
  Justification = 6
  JustificationReference = 0
  KeepLeftMargin = false
  MakeFace = true
  ObliqueAngle = 0
  Placement = pos=(-199,-3.6,-57.5) rot=(1,0,0;1.5708rad)
  ScaleToSize = true
  Size = 10
  String = AS
  Tracking = 0
FEATURE [Sketcher::SketchObject] Sketch133
  ArcFitTolerance = 1e-06
  AttachmentSupport = -> [Binder]
  ExternalGeometry = -> [Binder]
  FullyConstrained = true
  MakeInternals = false
  MapMode = 5
  Placement = pos=(0,9e-16,0) rot=(0,0.707107,0.707107;3.14159rad)
  sketch-geometry (30):
    g0: LineSegment StartX=0 StartY=39.2 StartZ=0 EndX=0 EndY=3.2 EndZ=0
    g1: LineSegment StartX=0 StartY=3.2 StartZ=0 EndX=82.8 EndY=3.2 EndZ=0
    g2: LineSegment StartX=82.8 StartY=3.2 StartZ=0 EndX=82.8 EndY=6.2 EndZ=0
    g3: LineSegment StartX=82.8 StartY=6.2 StartZ=0 EndX=91.752 EndY=6.2 EndZ=0
    g4: LineSegment StartX=0 StartY=39.2 StartZ=0 EndX=195.887 EndY=39.2 EndZ=0
    g5: LineSegment StartX=195.887 StartY=39.2 StartZ=0 EndX=202.765 EndY=20.303 EndZ=0
    g6: LineSegment StartX=192.333 StartY=24.9893 StartZ=0 EndX=196.467 EndY=26.4942 EndZ=0
    g7: LineSegment StartX=196.467 StartY=26.4942 StartZ=0 EndX=194.073 EndY=33.0721 EndZ=0
    g8: LineSegment StartX=194.073 StartY=33.0721 StartZ=0 EndX=189.939 EndY=31.5672 EndZ=0
    g9: LineSegment StartX=189.939 StartY=31.5672 StartZ=0 EndX=192.333 EndY=24.9893 EndZ=0
    g10: ArcOfCircle CenterX=107.6 CenterY=4 CenterZ=0 NormalX=0 NormalY=0 NormalZ=1 AngleXU=0 Radius=16 StartAngle=1.5708 EndAngle=3.00366
    g11: LineSegment StartX=107.6 StartY=20 StartZ=0 EndX=132.428 EndY=20 EndZ=0
    g12: ArcOfCircle [constr] CenterX=132.428 CenterY=4 CenterZ=0 NormalX=0 NormalY=0 NormalZ=1 AngleXU=0 Radius=16 StartAngle=0.314159 EndAngle=1.5708
    g13: LineSegment StartX=147.645 StartY=8.94427 StartZ=0 EndX=176.685 EndY=-80.4316 EndZ=0
    g14: LineSegment StartX=176.685 StartY=-80.4316 StartZ=0 EndX=215.932 EndY=-80.4316 EndZ=0
    g15: ArcOfCircle CenterX=207.583 CenterY=4 CenterZ=0 NormalX=0 NormalY=0 NormalZ=1 AngleXU=0 Radius=17 StartAngle=1.85815 EndAngle=3.57792
    g16: ArcOfCircle CenterX=184.801 CenterY=-67.3089 CenterZ=0 NormalX=0 NormalY=0 NormalZ=1 AngleXU=0 Radius=33.7833 StartAngle=5.88425 EndAngle=6.71952
    g17: LineSegment StartX=192.176 StartY=-3.18451 StartZ=0 EndX=215.42 EndY=-53.0314 EndZ=0
    g18: Circle CenterX=5.6 CenterY=34.8 CenterZ=0 NormalX=0 NormalY=0 NormalZ=1 AngleXU=0 Radius=1.8
    g19: Circle CenterX=5.6 CenterY=7.6 CenterZ=0 NormalX=0 NormalY=0 NormalZ=1 AngleXU=0 Radius=1.8
    g20: Circle CenterX=78.51 CenterY=34.8 CenterZ=0 NormalX=0 NormalY=0 NormalZ=1 AngleXU=0 Radius=1.8
    g21: Circle CenterX=78.51 CenterY=7.6 CenterZ=0 NormalX=0 NormalY=0 NormalZ=1 AngleXU=0 Radius=1.8
    g22: Circle CenterX=184.08 CenterY=34.8 CenterZ=0 NormalX=0 NormalY=0 NormalZ=1 AngleXU=0 Radius=1.8
    g23: Circle CenterX=179.305 CenterY=-76.8316 CenterZ=0 NormalX=0 NormalY=0 NormalZ=1 AngleXU=0 Radius=1.8
    g24: Circle CenterX=213.443 CenterY=-76.8316 CenterZ=0 NormalX=0 NormalY=0 NormalZ=1 AngleXU=0 Radius=1.8
    g25: Circle CenterX=19 CenterY=21.2 CenterZ=0 NormalX=0 NormalY=0 NormalZ=1 AngleXU=0 Radius=6.3
    g26: Circle CenterX=42 CenterY=21.2 CenterZ=0 NormalX=0 NormalY=0 NormalZ=1 AngleXU=0 Radius=6.3
    g27: Circle CenterX=65 CenterY=21.2 CenterZ=0 NormalX=0 NormalY=0 NormalZ=1 AngleXU=0 Radius=6.3
    g28: LineSegment StartX=132.428 StartY=20 StartZ=0 EndX=144.053 EndY=20 EndZ=0
    g29: LineSegment StartX=147.645 StartY=8.94427 StartZ=0 EndX=144.053 EndY=20 EndZ=0
  constraints (65):
    c: Coincident(g0,g-4)
    c: Coincident(g0,g-5)
    c: Coincident(g1,g0)
    c: Coincident(g1,g-6)
    c: Coincident(g2,g1)
    c: Coincident(g2,g-7)
    c: Coincident(g3,g2)
    c: Coincident(g3,g-8)
    c: Coincident(g4,g0)
    c: Coincident(g4,g-16)
    c: Coincident(g5,g4)
    c: Coincident(g5,g-16)
    c: Coincident(g6,g-20)
    c: Coincident(g6,g-21)
    c: Coincident(g7,g6)
    c: Coincident(g7,g-23)
    c: Coincident(g8,g7)
    c: Coincident(g8,g-22)
    c: Coincident(g9,g8)
    c: Coincident(g9,g6)
    c: Equal(g10,g-8)
    c: Coincident(g10,g3)
    c: Coincident(g10,g-9)
    c: Coincident(g11,g10)
    c: Coincident(g11,g-10)
    c: Equal(g12,g-10)
    c: Coincident(g12,g11)
    c: Coincident(g12,g-11)
    c: Coincident(g13,g12)
    c: Coincident(g13,g-12)
    c: Coincident(g14,g13)
    c: Coincident(g14,g-13)
    c: Equal(g15,g-15)
    c: Coincident(g15,g5)
    c: Coincident(g15,g-15)
    c: Equal(g16,g-13)
    c: Coincident(g16,g14)
    c: Coincident(g16,g-14)
    c: Coincident(g17,g15)
    c: Coincident(g17,g16)
    c: Equal(g18,g-28)
    c: Equal(g19,g-29)
    c: Equal(g20,g-26)
    c: Equal(g21,g-27)
    c: Equal(g22,g-17)
    c: Equal(g24,g-25)
    c: Equal(g23,g-24)
    c: Coincident(g23,g-24)
    c: Coincident(g24,g-25)
    c: Coincident(g22,g-17)
    c: Coincident(g20,g-26)
    c: Coincident(g21,g-27)
    c: Coincident(g18,g-28)
    c: Coincident(g19,g-29)
    c: Equal(g25,g-30)
    c: Equal(g26,g-31)
    c: Equal(g27,g-32)
    c: Coincident(g25,g-30)
    c: Coincident(g26,g-31)
    c: Coincident(g27,g-32)
    c: Parallel(g28,g11)
    c: Parallel(g29,g13)
    c: Coincident(g28,g11)
    c: Coincident(g29,g12)
    c: Coincident(g29,g28)
FEATURE [PartDesign::Pad] Pad019
  Direction = (0,1,-2e-16)
  Length = 2
  Length2 = 10
  Profile = -> Sketch133
  ReferenceAxis = -> Sketch133 [N_Axis]
  Refine = true
  Suppressed = false
  Type = 0
FEATURE [Sketcher::SketchObject] Sketch091  label="Sketch091 - forma anteriore"
  ArcFitTolerance = 1e-06
  AttachmentSupport = -> [Pad019]
  ExternalGeometry = -> [Binder]
  FullyConstrained = true
  MakeInternals = false
  MapMode = 5
  Placement = pos=(0,2,0) rot=(0,0.707107,0.707107;3.14159rad)
  sketch-geometry (12):
    g0: Circle CenterX=5.6 CenterY=34.8 CenterZ=0 NormalX=0 NormalY=0 NormalZ=1 AngleXU=0 Radius=1.8
    g1: Circle CenterX=5.6 CenterY=7.6 CenterZ=0 NormalX=0 NormalY=0 NormalZ=1 AngleXU=0 Radius=1.8
    g2: Circle CenterX=78.51 CenterY=34.8 CenterZ=0 NormalX=0 NormalY=0 NormalZ=1 AngleXU=0 Radius=1.8
    g3: Circle CenterX=78.51 CenterY=7.6 CenterZ=0 NormalX=0 NormalY=0 NormalZ=1 AngleXU=0 Radius=1.8
    g4: LineSegment StartX=0 StartY=39.2 StartZ=0 EndX=0 EndY=3.2 EndZ=0
    g5: LineSegment StartX=0 StartY=3.2 StartZ=0 EndX=82.8 EndY=3.2 EndZ=0
    g6: LineSegment StartX=82.8 StartY=3.2 StartZ=0 EndX=82.8 EndY=39.2 EndZ=0
    g7: LineSegment StartX=82.8 StartY=39.2 StartZ=0 EndX=0 EndY=39.2 EndZ=0
    g8: ArcOfCircle CenterX=19 CenterY=21.2 CenterZ=0 NormalX=0 NormalY=0 NormalZ=1 AngleXU=0 Radius=10 StartAngle=1.5708 EndAngle=4.71239
    g9: ArcOfCircle CenterX=65 CenterY=21.2 CenterZ=0 NormalX=0 NormalY=0 NormalZ=1 AngleXU=0 Radius=10 StartAngle=4.71239 EndAngle=7.85398
    g10: LineSegment StartX=19 StartY=31.2 StartZ=0 EndX=65 EndY=31.2 EndZ=0
    g11: LineSegment StartX=19 StartY=11.2 StartZ=0 EndX=65 EndY=11.2 EndZ=0
  constraints (25):
    c: Equal(g2,g-7)
    c: Equal(g3,g-8)
    c: Equal(g1,g-13)
    c: Equal(g0,g-12)
    c: Coincident(g0,g-12)
    c: Coincident(g1,g-13)
    c: Coincident(g3,g-8)
    c: Coincident(g2,g-7)
    c: Coincident(g4,g-4)
    c: Coincident(g4,g-5)
    c: Coincident(g5,g4)
    c: Coincident(g5,g-6)
    c: Coincident(g6,g5)
    c: PointOnObject(g6,g-3)
    c: Vertical(g6)
    c: Coincident(g7,g6)
    c: Coincident(g7,g4)
    c: Tangent(g8,g10) = 1.5708
    c: Tangent(g8,g11) = -1.5708
    c: Tangent(g9,g10) = 1.5708
    c: Tangent(g9,g11) = -1.5708
    c: Equal(g8,g9)
    c: Radius(g8) = 10
    c: Coincident(g8,g-11)
    c: Coincident(g9,g-9)
FEATURE [Sketcher::SketchObject] Sketch093  label="Sketch093 - scavi interni pulsanti"
  ArcFitTolerance = 1e-06
  AttachmentSupport = -> [Pad019]
  ExternalGeometry = -> [Binder]
  FullyConstrained = true
  MakeInternals = false
  MapMode = 5
  Placement = pos=(0,1.8e-15,0) rot=(1,0,0;1.5708rad)
  sketch-geometry (3):
    g0: Circle CenterX=-65 CenterY=21.2 CenterZ=0 NormalX=0 NormalY=0 NormalZ=1 AngleXU=0 Radius=7.3
    g1: Circle CenterX=-42 CenterY=21.2 CenterZ=0 NormalX=0 NormalY=0 NormalZ=1 AngleXU=0 Radius=7.3
    g2: Circle CenterX=-19 CenterY=21.2 CenterZ=0 NormalX=0 NormalY=0 NormalZ=1 AngleXU=0 Radius=7.3
  constraints (6):
    c: Coincident(g0,g-3)
    c: Coincident(g1,g-4)
    c: Coincident(g2,g-5)
    c: Diameter(g0) = 14.6
    c: Diameter(g1) = 14.6
    c: Diameter(g2) = 14.6
FEATURE [Sketcher::SketchObject] Sketch094  label="Sketch094 - forma centrale"
  ArcFitTolerance = 1e-06
  AttachmentSupport = -> [Pad019]
  ExternalGeometry = -> [Binder]
  FullyConstrained = true
  MakeInternals = false
  MapMode = 5
  Placement = pos=(0,2,0) rot=(0,0.707107,0.707107;3.14159rad)
  sketch-geometry (4):
    g0: LineSegment StartX=137.815 StartY=39.2 StartZ=0 EndX=142.655 EndY=24.303 EndZ=0
    g1: LineSegment StartX=110.815 StartY=24.303 StartZ=0 EndX=142.655 EndY=24.303 EndZ=0
    g2: LineSegment StartX=137.815 StartY=39.2 StartZ=0 EndX=110.815 EndY=39.2 EndZ=0
    g3: ArcOfCircle CenterX=92.2534 CenterY=31.7515 CenterZ=0 NormalX=0 NormalY=0 NormalZ=1 AngleXU=0 Radius=20 StartAngle=5.90156 EndAngle=6.66481
  constraints (12):
    c: PointOnObject(g0,g-3)
    c: Tangent(g0,g-5)
    c: Horizontal(g1)
    c: Coincident(g1,g0)
    c: Coincident(g2,g0)
    c: PointOnObject(g2,g-3)
    c: DistanceX(g2,g2) = 27
    c: Vertical(g1,g2)
    c: Coincident(g3,g2)
    c: Radius(g3) = 20
    c: Coincident(g3,g1)
    c: DistanceY(g-6,g0) = 4
FEATURE [Sketcher::SketchObject] Sketch095  label="Sketch095 - forma posteriore"
  ArcFitTolerance = 1e-06
  AttachmentSupport = -> [Pad019]
  ExternalGeometry = -> [Binder]
  FullyConstrained = true
  MakeInternals = false
  MapMode = 5
  Placement = pos=(0,2,0) rot=(0,0.707107,0.707107;3.14159rad)
  sketch-geometry (15):
    g0: LineSegment StartX=137.815 StartY=39.2 StartZ=0 EndX=143.955 EndY=20.303 EndZ=0
    g1: LineSegment StartX=143.955 StartY=20.303 StartZ=0 EndX=190.141 EndY=20.303 EndZ=0
    g2: ArcOfCircle CenterX=184.08 CenterY=34.8 CenterZ=0 NormalX=0 NormalY=0 NormalZ=1 AngleXU=0 Radius=3.5 StartAngle=3.49066 EndAngle=4.71239
    g3: LineSegment StartX=180.791 StartY=33.6029 StartZ=0 EndX=178.754 EndY=39.2 EndZ=0
    g4: LineSegment StartX=184.08 StartY=31.3 StartZ=0 EndX=186.139 EndY=31.3 EndZ=0
    g5: LineSegment StartX=190.141 StartY=20.303 StartZ=0 EndX=186.139 EndY=31.3 EndZ=0
    g6: LineSegment StartX=137.815 StartY=39.2 StartZ=0 EndX=156.815 EndY=39.2 EndZ=0
    g7: LineSegment StartX=178.754 StartY=39.2 StartZ=0 EndX=168.815 EndY=39.2 EndZ=0
    g8: LineSegment StartX=156.815 StartY=31.2 StartZ=0 EndX=168.815 EndY=31.2 EndZ=0
    g9: ArcOfCircle CenterX=176.411 CenterY=35.2 CenterZ=0 NormalX=0 NormalY=0 NormalZ=1 AngleXU=0 Radius=20 StartAngle=2.94023 EndAngle=3.34295
    g10: ArcOfCircle CenterX=188.411 CenterY=35.2 CenterZ=0 NormalX=0 NormalY=0 NormalZ=1 AngleXU=0 Radius=20 StartAngle=2.94023 EndAngle=3.34295
    g11: LineSegment StartX=157.815 StartY=39.2 StartZ=0 EndX=167.815 EndY=39.2 EndZ=0
    g12: LineSegment StartX=157.436 StartY=36.2 StartZ=0 EndX=167.436 EndY=36.2 EndZ=0
    g13: ArcOfCircle CenterX=177.411 CenterY=35.2 CenterZ=0 NormalX=0 NormalY=0 NormalZ=1 AngleXU=0 Radius=20 StartAngle=2.94023 EndAngle=3.09157
    g14: ArcOfCircle CenterX=187.411 CenterY=35.2 CenterZ=0 NormalX=0 NormalY=0 NormalZ=1 AngleXU=0 Radius=20 StartAngle=2.94023 EndAngle=3.09157
  constraints (46):
    c: PointOnObject(g0,g-3)
    c: Tangent(g0,g-6)
    c: Coincident(g1,g0)
    c: Horizontal(g1)
    c: Radius(g2) = 3.5
    c: Coincident(g2,g-5)
    c: PointOnObject(g3,g-3)
    c: Parallel(g3,g-4)
    c: Tangent(g3,g2) = 1.5708
    c: Horizontal(g4)
    c: Tangent(g4,g2) = -1.5708
    c: Coincident(g5,g1)
    c: Parallel(g5,g-4)
    c: Coincident(g5,g4)
    c: DistanceX(g4,g-8) = 3.8
    c: Coincident(g6,g0)
    c: PointOnObject(g6,g-3)
    c: Coincident(g7,g3)
    c: PointOnObject(g7,g-3)
    c: Horizontal(g8)
    c: DistanceX(g6,g7) = 12
    c: Vertical(g8,g6)
    c: Vertical(g7,g8)
    c: DistanceY(g8,g6) = 8
    c: Coincident(g9,g8)
    c: Coincident(g9,g6)
    c: Coincident(g10,g7)
    c: Coincident(g10,g8)
    c: Radius(g9) = 20
    c: Radius(g10) = 20
    c: PointOnObject(g11,g-3)
    c: PointOnObject(g11,g-3)
    c: DistanceX(g11,g11) = 10
    c: DistanceX(g6,g11) = 1
    c: Horizontal(g12)
    c: Equal(g12,g11)
    c: DistanceY(g12,g11) = 3
    c: Coincident(g13,g11)
    c: Coincident(g13,g12)
    c: Radius(g13) = 20
    c: Coincident(g14,g11)
    c: Coincident(g14,g12)
    c: Radius(g14) = 20
    c: DistanceX(g0,g6) = 19
    c: Horizontal(g9,g13)
    c: Horizontal(g0,g-4)
FEATURE [Sketcher::SketchObject] Sketch096  label="Sketch096 - forma impugnatura"
  ArcFitTolerance = 1e-06
  AttachmentSupport = -> [Pad019]
  ExternalGeometry = -> [Binder]
  FullyConstrained = true
  MakeInternals = false
  MapMode = 5
  Placement = pos=(0,2,0) rot=(0,0.707107,0.707107;3.14159rad)
  sketch-geometry (8):
    g0: LineSegment StartX=176.685 StartY=-80.4316 StartZ=0 EndX=143.955 EndY=20.303 EndZ=0
    g1: LineSegment StartX=176.685 StartY=-80.4316 StartZ=0 EndX=215.932 EndY=-80.4316 EndZ=0
    g2: Circle CenterX=179.305 CenterY=-76.8316 CenterZ=0 NormalX=0 NormalY=0 NormalZ=1 AngleXU=0 Radius=3
    g3: Circle CenterX=213.443 CenterY=-76.8316 CenterZ=0 NormalX=0 NormalY=0 NormalZ=1 AngleXU=0 Radius=3
    g4: LineSegment StartX=143.955 StartY=20.303 StartZ=0 EndX=202.765 EndY=20.303 EndZ=0
    g5: LineSegment StartX=215.42 StartY=-53.0314 StartZ=0 EndX=192.176 EndY=-3.18451 EndZ=0
    g6: ArcOfCircle CenterX=184.801 CenterY=-67.3089 CenterZ=0 NormalX=0 NormalY=0 NormalZ=1 AngleXU=0 Radius=33.7833 StartAngle=5.88425 EndAngle=6.71952
    g7: ArcOfCircle CenterX=207.583 CenterY=4 CenterZ=0 NormalX=0 NormalY=0 NormalZ=1 AngleXU=0 Radius=17 StartAngle=1.85815 EndAngle=3.57792
  constraints (19):
    c: Coincident(g0,g-4)
    c: PointOnObject(g0,g-3)
    c: Horizontal(g0,g-7)
    c: Coincident(g1,g0)
    c: Coincident(g1,g-5)
    c: Diameter(g2) = 6
    c: Diameter(g3) = 6
    c: Coincident(g2,g-9)
    c: Coincident(g3,g-10)
    c: Coincident(g4,g0)
    c: Coincident(g5,g-6)
    c: Coincident(g6,g1)
    c: Coincident(g6,g5)
    c: Equal(g-5,g6)
    c: Coincident(g5,g-7)
    c: Coincident(g4,g-7)
    c: Tangent(g7,g-7)
    c: Coincident(g7,g4)
    c: Coincident(g7,g5)
FEATURE [Sketcher::SketchObject] Sketch097
  ArcFitTolerance = 1e-06
  AttachmentSupport = -> [Pad019]
  ExternalGeometry = -> [Binder]
  FullyConstrained = true
  MakeInternals = false
  MapMode = 5
  Placement = pos=(0,2,0) rot=(0,0.707107,0.707107;3.14159rad)
  sketch-geometry (4):
    g0: LineSegment StartX=90 StartY=36.8 StartZ=0 EndX=108 EndY=36.8 EndZ=0
    g1: LineSegment StartX=108 StartY=36.8 StartZ=0 EndX=108 EndY=26.8 EndZ=0
    g2: LineSegment StartX=108 StartY=26.8 StartZ=0 EndX=90 EndY=26.8 EndZ=0
    g3: ArcOfCircle CenterX=94 CenterY=31.8 CenterZ=0 NormalX=0 NormalY=0 NormalZ=1 AngleXU=0 Radius=6.40312 StartAngle=2.24554 EndAngle=4.03765
  constraints (13):
    c: Horizontal(g0)
    c: Coincident(g1,g0)
    c: Vertical(g1)
    c: DistanceX(g0,g0) = 18
    c: DistanceY(g1,g1) = 10
    c: Coincident(g2,g1)
    c: Horizontal(g2)
    c: Equal(g2,g0)
    c: DistanceY(g0,g-3) = 2.4
    c: Coincident(g3,g0)
    c: Coincident(g3,g2)
    c: DistanceX(g2,g3) = 4
    c: DistanceX(g-3,g0) = 90
FEATURE [PartDesign::Chamfer] Chamfer015
  Angle = 45
  Base = -> Pad019 [Edge19,Edge22,Edge79]
  BaseFeature = -> Pad019
  ChamferType = 0
  FlipDirection = false
  Refine = true
  Size = 1.9
  Size2 = 1
  SupportTransform = false
  Suppressed = false
  UseAllEdges = false
FEATURE [PartDesign::Pocket] Pocket002
  BaseFeature = -> Chamfer015
  Direction = (0,1,-2e-16)
  Length = 1.2
  Length2 = 5
  Profile = -> Sketch093
  ReferenceAxis = -> Sketch093 [N_Axis]
  Refine = true
  Suppressed = false
  Type = 0
FEATURE [PartDesign::Pad] Pad005
  BaseFeature = -> Pocket002
  Direction = (0,1,-2e-16)
  Length = 1.6
  Length2 = 10
  Profile = -> Sketch091
  ReferenceAxis = -> Sketch091 [N_Axis]
  Refine = true
  Suppressed = false
  Type = 0
FEATURE [Sketcher::SketchObject] Sketch092  label="Sketch092 - scavi per viti anteriori"
  ArcFitTolerance = 1e-06
  AttachmentSupport = -> [Pad005]
  ExternalGeometry = -> [Binder]
  FullyConstrained = true
  MakeInternals = false
  MapMode = 5
  Placement = pos=(0,3.6,0) rot=(0,0.707107,0.707107;3.14159rad)
  sketch-geometry (20):
    g0: ArcOfCircle CenterX=5.6 CenterY=7.6 CenterZ=0 NormalX=0 NormalY=0 NormalZ=1 AngleXU=0 Radius=3.5 StartAngle=0 EndAngle=1.5708
    g1: ArcOfCircle CenterX=5.6 CenterY=34.8 CenterZ=0 NormalX=0 NormalY=0 NormalZ=1 AngleXU=0 Radius=3.5 StartAngle=4.71239 EndAngle=6.28319
    g2: ArcOfCircle CenterX=78.51 CenterY=34.8 CenterZ=0 NormalX=0 NormalY=0 NormalZ=1 AngleXU=0 Radius=3.5 StartAngle=3.14159 EndAngle=4.71239
    g3: ArcOfCircle CenterX=78.51 CenterY=7.6 CenterZ=0 NormalX=0 NormalY=0 NormalZ=1 AngleXU=0 Radius=3.5 StartAngle=1.5708 EndAngle=3.14159
    g4: LineSegment StartX=0 StartY=3.2 StartZ=0 EndX=0 EndY=11.1 EndZ=0
    g5: LineSegment StartX=0 StartY=11.1 StartZ=0 EndX=5.6 EndY=11.1 EndZ=0
    g6: LineSegment StartX=0 StartY=3.2 StartZ=0 EndX=9.1 EndY=3.2 EndZ=0
    g7: LineSegment StartX=9.1 StartY=3.2 StartZ=0 EndX=9.1 EndY=7.6 EndZ=0
    g8: LineSegment StartX=0 StartY=39.2 StartZ=0 EndX=0 EndY=31.3 EndZ=0
    g9: LineSegment StartX=0 StartY=31.3 StartZ=0 EndX=5.6 EndY=31.3 EndZ=0
    g10: LineSegment StartX=0 StartY=39.2 StartZ=0 EndX=9.1 EndY=39.2 EndZ=0
    g11: LineSegment StartX=9.1 StartY=39.2 StartZ=0 EndX=9.1 EndY=34.8 EndZ=0
    g12: LineSegment StartX=82.8 StartY=39.2 StartZ=0 EndX=75.01 EndY=39.2 EndZ=0
    g13: LineSegment StartX=82.8 StartY=39.2 StartZ=0 EndX=82.8 EndY=31.3 EndZ=0
    g14: LineSegment StartX=82.8 StartY=31.3 StartZ=0 EndX=78.51 EndY=31.3 EndZ=0
    g15: LineSegment StartX=82.8 StartY=3.2 StartZ=0 EndX=75.01 EndY=3.2 EndZ=0
    g16: LineSegment StartX=75.01 StartY=3.2 StartZ=0 EndX=75.01 EndY=7.6 EndZ=0
    g17: LineSegment StartX=82.8 StartY=3.2 StartZ=0 EndX=82.8 EndY=11.1 EndZ=0
    g18: LineSegment StartX=82.8 StartY=11.1 StartZ=0 EndX=78.51 EndY=11.1 EndZ=0
    g19: LineSegment StartX=75.01 StartY=39.2 StartZ=0 EndX=75.01 EndY=34.8 EndZ=0
  constraints (48):
    c: Radius(g0) = 3.5
    c: Coincident(g0,g-10)
    c: Radius(g1) = 3.5
    c: Coincident(g1,g-9)
    c: Radius(g2) = 3.5
    c: Coincident(g2,g-8)
    c: Radius(g3) = 3.5
    c: Coincident(g3,g-7)
    c: Coincident(g4,g-5)
    c: PointOnObject(g4,g-4)
    c: Coincident(g5,g4)
    c: Horizontal(g5)
    c: Coincident(g6,g4)
    c: PointOnObject(g6,g-5)
    c: Coincident(g7,g6)
    c: Vertical(g7)
    c: Coincident(g8,g-4)
    c: PointOnObject(g8,g-4)
    c: Coincident(g9,g8)
    c: Horizontal(g9)
    c: Coincident(g10,g8)
    c: PointOnObject(g10,g-3)
    c: Coincident(g11,g10)
    c: Vertical(g11)
    c: PointOnObject(g12,g-3)
    c: PointOnObject(g12,g-3)
    c: Coincident(g13,g12)
    c: Vertical(g13)
    c: Coincident(g14,g13)
    c: Horizontal(g14)
    c: Coincident(g15,g-6)
    c: PointOnObject(g15,g-5)
    c: Coincident(g16,g15)
    c: Vertical(g16)
    c: Coincident(g17,g15)
    c: Coincident(g18,g17)
    c: Horizontal(g18)
    c: Tangent(g3,g18) = -1.5708
    c: Tangent(g16,g3) = 1.5708
    c: Coincident(g19,g12)
    c: Vertical(g19)
    c: Tangent(g2,g19) = -1.5708
    c: Tangent(g2,g14) = 1.5708
    c: Tangent(g0,g7) = -1.5708
    c: Tangent(g0,g5) = 1.5708
    c: Tangent(g9,g1) = -1.5708
    c: Tangent(g1,g11) = 1.5708
    c: Tangent(g17,g13)
FEATURE [PartDesign::Pocket] Pocket001
  BaseFeature = -> Pad005
  Direction = (0,-1,2e-16)
  Length = 1.6
  Length2 = 5
  Profile = -> Sketch092
  ReferenceAxis = -> Sketch092 [N_Axis]
  Refine = true
  Suppressed = false
  Type = 0
FEATURE [PartDesign::Pad] Pad006
  BaseFeature = -> Pocket001
  Direction = (0,1,-2e-16)
  Length = 0.8
  Length2 = 10
  Profile = -> Sketch094
  ReferenceAxis = -> Sketch094 [N_Axis]
  Refine = true
  Suppressed = false
  Type = 0
FEATURE [PartDesign::Pad] Pad007
  BaseFeature = -> Pad006
  Direction = (0,1,-2e-16)
  Length = 2
  Length2 = 10
  Profile = -> Sketch095
  ReferenceAxis = -> Sketch095 [N_Axis]
  Refine = true
  Suppressed = false
  Type = 0
FEATURE [PartDesign::Pad] Pad008  label="Pad008 - forma impugnatura"
  BaseFeature = -> Pad007
  Direction = (0,1,-2e-16)
  Length = 1.6
  Length2 = 10
  Profile = -> Sketch096
  ReferenceAxis = -> Sketch096 [N_Axis]
  Refine = true
  Suppressed = false
  Type = 0
FEATURE [PartDesign::Pad] Pad009
  BaseFeature = -> Pad008
  Direction = (0,1,-2e-16)
  Length = 1.6
  Length2 = 10
  Profile = -> Sketch097
  ReferenceAxis = -> Sketch097 [N_Axis]
  Refine = true
  Suppressed = false
  Type = 0
FEATURE [Sketcher::SketchObject] Sketch098
  ArcFitTolerance = 1e-06
  AttachmentSupport = -> [Pad006]
  ExternalGeometry = -> [Binder]
  FullyConstrained = true
  MakeInternals = false
  MapMode = 5
  Placement = pos=(0,2.8,-7e-16) rot=(0,0.707107,0.707107;3.14159rad)
  sketch-geometry (4):
    g0: LineSegment StartX=118 StartY=39.2 StartZ=0 EndX=129 EndY=39.2 EndZ=0
    g1: LineSegment StartX=120.599 StartY=31.2 StartZ=0 EndX=131.599 EndY=31.2 EndZ=0
    g2: LineSegment StartX=129 StartY=39.2 StartZ=0 EndX=131.599 EndY=31.2 EndZ=0
    g3: LineSegment StartX=118 StartY=39.2 StartZ=0 EndX=120.599 EndY=31.2 EndZ=0
  constraints (12):
    c: PointOnObject(g0,g-3)
    c: PointOnObject(g0,g-3)
    c: DistanceX(g0,g0) = 11
    c: Horizontal(g1)
    c: Equal(g1,g0)
    c: Coincident(g2,g0)
    c: Coincident(g3,g0)
    c: Parallel(g-4,g2)
    c: Coincident(g1,g2)
    c: Coincident(g1,g3)
    c: DistanceY(g1,g0) = 8
    c: DistanceX(g-3,g0) = 118
FEATURE [Sketcher::SketchObject] Sketch099
  ArcFitTolerance = 1e-06
  AttachmentSupport = -> [Pad008]
  ExternalGeometry = -> [Binder]
  FullyConstrained = true
  MakeInternals = false
  MapMode = 5
  Placement = pos=(0,3.6,0) rot=(0,0.707107,0.707107;3.14159rad)
  sketch-geometry (13):
    g0: LineSegment StartX=192.176 StartY=-3.18451 StartZ=0 EndX=196.804 EndY=-13.1108 EndZ=0
    g1: LineSegment [constr] StartX=202.765 StartY=20.303 StartZ=0 EndX=181.223 EndY=20.303 EndZ=0
    g2: LineSegment [constr] StartX=181.223 StartY=20.303 StartZ=0 EndX=181.223 EndY=-3.18451 EndZ=0
    g3: ArcOfCircle CenterX=181.223 CenterY=-20.3764 CenterZ=0 NormalX=0 NormalY=0 NormalZ=1 AngleXU=0 Radius=17.1918 StartAngle=0.436332 EndAngle=1.57079
    g4: ArcOfEllipse CenterX=181.223 CenterY=8.55923 CenterZ=0 NormalX=0 NormalY=0 NormalZ=1 MajorRadius=23.4779 MinorRadius=11.7437 AngleXU=0 StartAngle=1.5708 EndAngle=4.71239
    g5: LineSegment [constr] StartX=204.701 StartY=8.55923 StartZ=0 EndX=157.745 EndY=8.55923 EndZ=0
    g6: LineSegment [constr] StartX=181.223 StartY=20.303 StartZ=0 EndX=181.223 EndY=-3.18451 EndZ=0
    g7: GeomPoint [constr] X=201.553 Y=8.55923 Z=0
    g8: GeomPoint [constr] X=160.894 Y=8.55923 Z=0
    g9: GeomPoint [constr] X=181.223 Y=-3.18451 Z=0
    g10: LineSegment StartX=181.223 StartY=20.303 StartZ=0 EndX=202.765 EndY=20.303 EndZ=0
    g11: ArcOfCircle CenterX=207.583 CenterY=4 CenterZ=0 NormalX=0 NormalY=0 NormalZ=1 AngleXU=0 Radius=17 StartAngle=1.85815 EndAngle=3.57792
    g12: LineSegment [constr] StartX=172.411 StartY=39.2 StartZ=0 EndX=192.176 EndY=-3.18451 EndZ=0
  constraints (27):
    c: Coincident(g1,g-7)
    c: Horizontal(g1)
    c: Coincident(g2,g1)
    c: Vertical(g2)
    c: Horizontal(g2,g0)
    c: Coincident(g3,g0)
    c: Coincident(g3,g2)
    c: InternalAlignment(g5-g8 -> g4) x4
    c: Horizontal(g5)
    c: PointOnObject(g4,g2)
    c: Coincident(g4,g1)
    c: DistanceX(g-3,g5) = 10.1
    c: Coincident(g4,g2)
    c: Tangent(g3,g-5)
    c: PointOnObject(g9,g4)
    c: PointOnObject(g9,g3)
    c: Tangent(g4,g3,g9) = 1.5708
    c: Coincident(g10,g1)
    c: Coincident(g10,g1)
    c: Equal(g11,g-4)
    c: Coincident(g11,g1)
    c: Coincident(g11,g0)
    c: PointOnObject(g12,g-6)
    c: PointOnObject(g1,g12)
    c: Tangent(g12,g-5) = -1.5708
    c: Tangent(g0,g-5) = -1.5708
    c: Horizontal(g9,g12)
FEATURE [Sketcher::SketchObject] Sketch106  label="Sketch106 - smusso impuniatura interno"
  ArcFitTolerance = 1e-06
  AttachmentSupport = -> [Pad008]
  ExternalGeometry = -> [Pad008]
  FullyConstrained = true
  MakeInternals = false
  MapMode = 5
  Placement = pos=(0,-1.586e-13,-80.4316) rot=(1,0,0;3.14159rad)
  sketch-geometry (9):
    g0: LineSegment StartX=-176.685 StartY=-3.6 StartZ=0 EndX=-176.685 EndY=-1.417e-13 EndZ=0
    g1: LineSegment [constr] StartX=-176.685 StartY=-1.416e-13 StartZ=0 EndX=-176.685 EndY=-1.416e-13 EndZ=0
    g2: LineSegment [constr] StartX=-186.685 StartY=-3.6 StartZ=0 EndX=-186.685 EndY=-1.417e-13 EndZ=0
    g3: ArcOfEllipse CenterX=-186.685 CenterY=-1.416e-13 CenterZ=0 NormalX=0 NormalY=0 NormalZ=1 MajorRadius=10 MinorRadius=3.6 AngleXU=-3.14159 StartAngle=1.5708 EndAngle=3.14159
    g4: LineSegment [constr] StartX=-196.685 StartY=-1.416e-13 StartZ=0 EndX=-176.685 EndY=-1.416e-13 EndZ=0
    g5: LineSegment [constr] StartX=-186.685 StartY=-3.6 StartZ=0 EndX=-186.685 EndY=3.6 EndZ=0
    g6: GeomPoint [constr] X=-196.015 Y=-1.416e-13 Z=0
    g7: GeomPoint [constr] X=-177.356 Y=-1.416e-13 Z=0
    g8: LineSegment StartX=-176.685 StartY=-3.6 StartZ=0 EndX=-186.685 EndY=-3.6 EndZ=0
  constraints (15):
    c: PointOnObject(g2,g-3)
    c: Coincident(g1,g-5)
    c: DistanceY(g1,g1) = 0
    c: Coincident(g0,g1)
    c: DistanceX(g2,g-5) = 10
    c: Vertical(g2)
    c: Horizontal(g2,g0)
    c: InternalAlignment(g4-g7 -> g3) x4
    c: Coincident(g3,g2)
    c: Horizontal(g4)
    c: Coincident(g3,g0)
    c: Tangent(g0,g-5) = 1.5708
    c: Coincident(g3,g2)
    c: Coincident(g8,g0)
    c: Coincident(g8,g2)
FEATURE [Sketcher::SketchObject] Sketch107  label="Sketch107 - smusso impugnatura esterno"
  ArcFitTolerance = 1e-06
  AttachmentSupport = -> [Pad008]
  ExternalGeometry = -> [Pad008]
  FullyConstrained = true
  MakeInternals = false
  MapMode = 5
  Placement = pos=(0,-1.586e-13,-80.4316) rot=(1,0,0;3.14159rad)
  sketch-geometry (9):
    g0: LineSegment [constr] StartX=-215.932 StartY=-1.416e-13 StartZ=0 EndX=-215.932 EndY=-4.71e-14 EndZ=0
    g1: LineSegment StartX=-215.932 StartY=-3.6 StartZ=0 EndX=-215.932 EndY=-4.71e-14 EndZ=0
    g2: LineSegment StartX=-215.932 StartY=-3.6 StartZ=0 EndX=-205.932 EndY=-3.6 EndZ=0
    g3: LineSegment [constr] StartX=-205.932 StartY=-3.6 StartZ=0 EndX=-205.932 EndY=-4.71e-14 EndZ=0
    g4: ArcOfEllipse CenterX=-205.932 CenterY=-4.71e-14 CenterZ=0 NormalX=0 NormalY=0 NormalZ=1 MajorRadius=10 MinorRadius=3.6 AngleXU=-3.14159 StartAngle=-2.66e-14 EndAngle=1.5708
    g5: LineSegment [constr] StartX=-215.932 StartY=-1.416e-13 StartZ=0 EndX=-195.932 EndY=-1.416e-13 EndZ=0
    g6: LineSegment [constr] StartX=-205.932 StartY=-3.6 StartZ=0 EndX=-205.932 EndY=3.6 EndZ=0
    g7: GeomPoint [constr] X=-215.262 Y=-1.366e-13 Z=0
    g8: GeomPoint [constr] X=-196.602 Y=-1.551e-13 Z=0
  constraints (16):
    c: Coincident(g0,g-6)
    c: PointOnObject(g0,g-6)
    c: DistanceY(g0,g0) = 0
    c: Coincident(g1,g-6)
    c: Coincident(g1,g0)
    c: Tangent(g2,g-3)
    c: DistanceX(g2,g2) = 10
    c: Coincident(g3,g2)
    c: Vertical(g3)
    c: Horizontal(g3,g0)
    c: InternalAlignment(g5-g8 -> g4) x4
    c: Coincident(g4,g3)
    c: Horizontal(g5)
    c: Coincident(g4,g0)
    c: Coincident(g4,g2)
    c: PointOnObject(g2,g1)
FEATURE [Sketcher::SketchObject] Sketch108
  ArcFitTolerance = 1e-06
  AttachmentOffset = pos=(0,0,-1.6) rot=(0,0,1;0rad)
  AttachmentSupport = -> [Pad008]
  ExternalGeometry = -> [Binder]
  FullyConstrained = true
  MakeInternals = false
  MapMode = 5
  Placement = pos=(0,2,4e-16) rot=(0,0.707107,0.707107;3.14159rad)
  sketch-geometry (14):
    g0: LineSegment StartX=192.176 StartY=-3.18451 StartZ=0 EndX=193.827 EndY=-6.72678 EndZ=0
    g1: LineSegment [constr] StartX=202.765 StartY=20.303 StartZ=0 EndX=181.223 EndY=20.303 EndZ=0
    g2: LineSegment [constr] StartX=181.223 StartY=20.303 StartZ=0 EndX=181.223 EndY=1.30297 EndZ=0
    g3: ArcOfCircle CenterX=181.223 CenterY=-12.6042 CenterZ=0 NormalX=0 NormalY=0 NormalZ=1 AngleXU=0 Radius=13.9072 StartAngle=0.436332 EndAngle=1.5708
    g4: ArcOfEllipse CenterX=181.223 CenterY=10.803 CenterZ=0 NormalX=0 NormalY=0 NormalZ=1 MajorRadius=14.4779 MinorRadius=9.5 AngleXU=0 StartAngle=1.5708 EndAngle=4.71239
    g5: LineSegment [constr] StartX=195.701 StartY=10.803 StartZ=0 EndX=166.745 EndY=10.803 EndZ=0
    g6: LineSegment [constr] StartX=181.223 StartY=20.303 StartZ=0 EndX=181.223 EndY=1.30297 EndZ=0
    g7: GeomPoint [constr] X=192.148 Y=10.803 Z=0
    g8: GeomPoint [constr] X=170.298 Y=10.803 Z=0
    g9: LineSegment StartX=181.223 StartY=20.303 StartZ=0 EndX=202.765 EndY=20.303 EndZ=0
    g10: ArcOfCircle CenterX=207.583 CenterY=4 CenterZ=0 NormalX=0 NormalY=0 NormalZ=1 AngleXU=0 Radius=17 StartAngle=1.85815 EndAngle=3.57792
    g11: LineSegment [constr] StartX=172.411 StartY=39.2 StartZ=0 EndX=192.176 EndY=-3.18451 EndZ=0
    g12: GeomPoint [constr] X=181.223 Y=1.30297 Z=0
    g13: GeomPoint [constr] X=181.223 Y=1.30297 Z=0
  constraints (28):
    c: Coincident(g1,g-7)
    c: Horizontal(g1)
    c: Coincident(g2,g1)
    c: Vertical(g2)
    c: Coincident(g3,g2)
    c: InternalAlignment(g5-g8 -> g4) x4
    c: Horizontal(g5)
    c: PointOnObject(g4,g2)
    c: Coincident(g4,g1)
    c: DistanceX(g-3,g5) = 19.1
    c: Coincident(g4,g2)
    c: Coincident(g9,g1)
    c: Coincident(g9,g1)
    c: Coincident(g10,g1)
    c: Coincident(g10,g0)
    c: PointOnObject(g11,g-6)
    c: PointOnObject(g1,g11)
    c: DistanceY(g2,g1) = 19
    c: Coincident(g10,g-4)
    c: PointOnObject(g12,g4)
    c: PointOnObject(g12,g3)
    c: Tangent(g11,g-5) = -1.5708
    c: Tangent(g0,g-5) = -1.5708
    c: Tangent(g3,g0) = 1.5708
    c: PointOnObject(g13,g4)
    c: PointOnObject(g13,g3)
    c: Tangent(g4,g3,g13) = 1.5708
    c: Horizontal(g11,g0)
FEATURE [Part::Part2DObjectPython] Clone2D  label="Sketch108 (2D)"  # Draft 2D object (typed FeaturePython)
  Fuse = false
  Objects = -> [Sketch108]
  Placement = pos=(0,2,4e-16) rot=(0,0.707107,0.707107;3.14159rad)
  Scale = (1,1,1)
FEATURE [Sketcher::SketchObject] Sketch109
  ArcFitTolerance = 1e-06
  AttachmentOffset = pos=(0,0,-3.5) rot=(0,0,1;0rad)
  AttachmentSupport = -> [Pad008]
  ExternalGeometry = -> [Binder]
  FullyConstrained = true
  MakeInternals = false
  MapMode = 5
  Placement = pos=(0,0.1,8e-16) rot=(0,0.707107,0.707107;3.14159rad)
  sketch-geometry (1):
    g0: GeomPoint X=197.47 Y=8.55923 Z=0
  constraints (1):
    c: Symmetric(g-7,g-5,g0)
FEATURE [PartDesign::Chamfer] Chamfer005
  Angle = 45
  Base = -> Pad009 [Edge215,Edge212]
  BaseFeature = -> Pad009
  ChamferType = 1
  FlipDirection = false
  Refine = true
  Size = 1.5
  Size2 = 2.8
  SupportTransform = false
  Suppressed = false
  UseAllEdges = false
FEATURE [Sketcher::SketchObject] Sketch111
  ArcFitTolerance = 1e-06
  AttachmentSupport = -> [Pad009]
  ExternalGeometry = -> [Pad009]
  FullyConstrained = true
  MakeInternals = false
  MapMode = 5
  Placement = pos=(0,3.6,-8e-16) rot=(0,0.707107,0.707107;3.14159rad)
  sketch-geometry (21):
    g0: LineSegment [constr] StartX=97 StartY=36.8 StartZ=0 EndX=97 EndY=26.8 EndZ=0
    g1: LineSegment StartX=97 StartY=28.6 StartZ=0 EndX=97 EndY=27.8 EndZ=0
    g2: LineSegment StartX=97 StartY=27.8 StartZ=0 EndX=108 EndY=27.8 EndZ=0
    g3: LineSegment StartX=108 StartY=27.8 StartZ=0 EndX=108 EndY=28.6 EndZ=0
    g4: LineSegment StartX=108 StartY=28.6 StartZ=0 EndX=97 EndY=28.6 EndZ=0
    g5: LineSegment StartX=97 StartY=35.8 StartZ=0 EndX=97 EndY=35 EndZ=0
    g6: LineSegment StartX=97 StartY=35 StartZ=0 EndX=108 EndY=35 EndZ=0
    g7: LineSegment StartX=108 StartY=35 StartZ=0 EndX=108 EndY=35.8 EndZ=0
    g8: LineSegment StartX=108 StartY=35.8 StartZ=0 EndX=97 EndY=35.8 EndZ=0
    g9: LineSegment StartX=97 StartY=30.4 StartZ=0 EndX=97 EndY=29.6 EndZ=0
    g10: LineSegment StartX=97 StartY=29.6 StartZ=0 EndX=108 EndY=29.6 EndZ=0
    g11: LineSegment StartX=108 StartY=29.6 StartZ=0 EndX=108 EndY=30.4 EndZ=0
    g12: LineSegment StartX=108 StartY=30.4 StartZ=0 EndX=97 EndY=30.4 EndZ=0
    g13: LineSegment StartX=97 StartY=34 StartZ=0 EndX=97 EndY=33.2 EndZ=0
    g14: LineSegment StartX=97 StartY=33.2 StartZ=0 EndX=108 EndY=33.2 EndZ=0
    g15: LineSegment StartX=108 StartY=33.2 StartZ=0 EndX=108 EndY=34 EndZ=0
    g16: LineSegment StartX=108 StartY=34 StartZ=0 EndX=97 EndY=34 EndZ=0
    g17: LineSegment StartX=97 StartY=32.2 StartZ=0 EndX=97 EndY=31.4 EndZ=0
    g18: LineSegment StartX=97 StartY=31.4 StartZ=0 EndX=108 EndY=31.4 EndZ=0
    g19: LineSegment StartX=108 StartY=31.4 StartZ=0 EndX=108 EndY=32.2 EndZ=0
    g20: LineSegment StartX=108 StartY=32.2 StartZ=0 EndX=97 EndY=32.2 EndZ=0
  constraints (54):
    c: Vertical(g0)
    c: PointOnObject(g0,g-3)
    c: PointOnObject(g0,g-4)
    c: DistanceX(g0,g-5) = 11
    c: Coincident(g1,g2)
    c: Coincident(g2,g3)
    c: Coincident(g3,g4)
    c: Coincident(g4,g1)
    c: Horizontal(g2)
    c: Horizontal(g4)
    c: Tangent(g1,g0)
    c: Tangent(g3,g-5)
    c: DistanceY(g2,g3) = 0.8
    c: Coincident(g5,g6)
    c: Coincident(g6,g7)
    c: Coincident(g7,g8)
    c: Coincident(g8,g5)
    c: Horizontal(g6)
    c: Horizontal(g8)
    c: DistanceY(g6,g7) = 0.8
    c: Coincident(g9,g10)
    c: Coincident(g10,g11)
    c: Coincident(g11,g12)
    c: Coincident(g12,g9)
    c: Horizontal(g10)
    c: Horizontal(g12)
    c: DistanceY(g10,g11) = 0.8
    c: Tangent(g5,g0)
    c: Tangent(g7,g-5)
    c: Tangent(g9,g0)
    c: Tangent(g11,g-5)
    c: Coincident(g13,g14)
    c: Coincident(g14,g15)
    c: Coincident(g15,g16)
    c: Coincident(g16,g13)
    c: Horizontal(g14)
    c: Horizontal(g16)
    c: DistanceY(g14,g15) = 0.8
    c: Tangent(g13,g0)
    c: Tangent(g15,g-5)
    c: Coincident(g17,g18)
    c: Coincident(g18,g19)
    c: Coincident(g19,g20)
    c: Coincident(g20,g17)
    c: Horizontal(g18)
    c: Horizontal(g20)
    c: DistanceY(g18,g19) = 0.8
    c: Tangent(g17,g0)
    c: Tangent(g19,g-5)
    c: DistanceY(g1,g9) = 1
    c: DistanceY(g9,g17) = 1
    c: DistanceY(g17,g13) = 1
    c: DistanceY(g13,g5) = 1
    c: DistanceY(g0,g1) = 1
FEATURE [PartDesign::Pocket] Pocket004
  BaseFeature = -> Chamfer005
  Direction = (0,-1,2e-16)
  Length = 1
  Length2 = 5
  Profile = -> Sketch111
  ReferenceAxis = -> Sketch111 [N_Axis]
  Refine = true
  Suppressed = false
  Type = 0
FEATURE [PartDesign::Pad] Pad010
  BaseFeature = -> Pocket004
  Direction = (0,1,-2e-16)
  Length = 1.2
  Length2 = 10
  Profile = -> Sketch098
  ReferenceAxis = -> Sketch098 [N_Axis]
  Refine = true
  Suppressed = false
  Type = 0
FEATURE [PartDesign::Chamfer] Chamfer006
  Angle = 45
  Base = -> Pad010 [Edge291]
  BaseFeature = -> Pad010
  ChamferType = 1
  FlipDirection = false
  Refine = true
  Size = 1
  Size2 = 6
  SupportTransform = false
  Suppressed = false
  UseAllEdges = false
FEATURE [Sketcher::SketchObject] Sketch110
  ArcFitTolerance = 1e-06
  AttachmentSupport = -> [Pad010]
  ExternalGeometry = -> [Sketch098]
  FullyConstrained = true
  MakeInternals = false
  MapMode = 5
  Placement = pos=(0,4,-9e-16) rot=(0,0.707107,0.707107;3.14159rad)
  sketch-geometry (8):
    g0: LineSegment StartX=119.69 StartY=34 StartZ=0 EndX=130.69 EndY=34 EndZ=0
    g1: LineSegment StartX=119.95 StartY=33.2 StartZ=0 EndX=130.95 EndY=33.2 EndZ=0
    g2: LineSegment StartX=119.137 StartY=35.7 StartZ=0 EndX=130.137 EndY=35.7 EndZ=0
    g3: LineSegment StartX=118.877 StartY=36.5 StartZ=0 EndX=129.877 EndY=36.5 EndZ=0
    g4: LineSegment StartX=118.877 StartY=36.5 StartZ=0 EndX=119.137 EndY=35.7 EndZ=0
    g5: LineSegment StartX=129.877 StartY=36.5 StartZ=0 EndX=130.137 EndY=35.7 EndZ=0
    g6: LineSegment StartX=119.69 StartY=34 StartZ=0 EndX=119.95 EndY=33.2 EndZ=0
    g7: LineSegment StartX=130.69 StartY=34 StartZ=0 EndX=130.95 EndY=33.2 EndZ=0
  constraints (24):
    c: Horizontal(g0)
    c: Horizontal(g1)
    c: Horizontal(g2)
    c: Horizontal(g3)
    c: Equal(g1,g-5)
    c: Equal(g0,g-5)
    c: Equal(g2,g-5)
    c: Equal(g3,g-5)
    c: PointOnObject(g0,g-3)
    c: PointOnObject(g1,g-3)
    c: PointOnObject(g2,g-3)
    c: PointOnObject(g3,g-3)
    c: Coincident(g4,g3)
    c: Coincident(g4,g2)
    c: Coincident(g5,g3)
    c: Coincident(g5,g2)
    c: Coincident(g6,g0)
    c: Coincident(g6,g1)
    c: Coincident(g7,g0)
    c: Coincident(g7,g1)
    c: DistanceY(g1,g0) = 0.8
    c: DistanceY(g2,g3) = 0.8
    c: DistanceY(g-5,g1) = 2
    c: DistanceY(g-5,g2) = 4.5
FEATURE [PartDesign::Pocket] Pocket003
  BaseFeature = -> Chamfer006
  Direction = (0,-1,2e-16)
  Length = 1
  Length2 = 5
  Profile = -> Sketch110
  ReferenceAxis = -> Sketch110 [N_Axis]
  Refine = true
  Suppressed = false
  Type = 0
FEATURE [PartDesign::SubtractivePipe] SubtractivePipe
  AuxilleryCurvelinear = true
  AuxillerySpineTangent = false
  BaseFeature = -> Pocket003
  Binormal = (0,0,0)
  Mode = 0
  Profile = -> Sketch106
  Refine = true
  Spine = -> Pad008 [Edge215]
  SpineTangent = false
  Suppressed = false
  Transformation = 0
  Transition = 0
FEATURE [PartDesign::SubtractivePipe] SubtractivePipe001
  AuxilleryCurvelinear = true
  AuxillerySpineTangent = false
  BaseFeature = -> SubtractivePipe
  Binormal = (0,0,0)
  Mode = 0
  Profile = -> Sketch107
  Refine = true
  Spine = -> Pad008 [Edge213,Edge216,Edge210]
  SpineTangent = false
  Suppressed = false
  Transformation = 0
  Transition = 0
FEATURE [PartDesign::SubtractiveLoft] SubtractiveLoft
  BaseFeature = -> SubtractivePipe001
  Closed = false
  Profile = -> Sketch099
  Refine = true
  Ruled = false
  Sections = -> [Sketch108]
  Suppressed = false
FEATURE [PartDesign::SubtractiveLoft] SubtractiveLoft001
  BaseFeature = -> SubtractiveLoft
  Closed = false
  Profile = -> Clone2D
  Refine = true
  Ruled = false
  Sections = -> [Sketch109]
  Suppressed = false
FEATURE [Sketcher::SketchObject] Sketch112
  ArcFitTolerance = 1e-06
  AttachmentSupport = -> [Pad008]
  ExternalGeometry = -> [Binder]
  FullyConstrained = true
  MakeInternals = false
  MapMode = 5
  Placement = pos=(0,3.6,0) rot=(0,0.707107,0.707107;3.14159rad)
  sketch-geometry (4):
    g0: LineSegment [constr] StartX=167.782 StartY=-53.0314 StartZ=0 EndX=215.42 EndY=-53.0314 EndZ=0
    g1: GeomPoint [constr] X=191.282 Y=-53.0314 Z=0
    g2: Circle CenterX=191.282 CenterY=-53.0314 CenterZ=0 NormalX=0 NormalY=0 NormalZ=1 AngleXU=0 Radius=11.5
    g3: Circle CenterX=191.282 CenterY=-53.0314 CenterZ=0 NormalX=0 NormalY=0 NormalZ=1 AngleXU=0 Radius=10.7
  constraints (9):
    c: Horizontal(g0)
    c: PointOnObject(g0,g-3)
    c: Diameter(g2) = 23
    c: Coincident(g2,g1)
    c: Diameter(g3) = 21.4
    c: Coincident(g3,g1)
    c: DistanceX(g0,g1) = 23.5
    c: PointOnObject(g1,g0)
    c: Coincident(g0,g-4)
FEATURE [PartDesign::Chamfer] Chamfer016
  Angle = 45
  Base = -> SubtractiveLoft001 [Edge118,Edge117,Edge119,Edge120,Edge109]
  BaseFeature = -> SubtractiveLoft001
  ChamferType = 0
  FlipDirection = false
  Refine = true
  Size = 1.5
  Size2 = 1
  SupportTransform = false
  Suppressed = false
  UseAllEdges = false
FEATURE [PartDesign::Chamfer] Chamfer017
  Angle = 45
  Base = -> Chamfer016 [Edge15]
  BaseFeature = -> Chamfer016
  ChamferType = 0
  FlipDirection = false
  Refine = true
  Size = 1.6
  Size2 = 1
  SupportTransform = false
  Suppressed = false
  UseAllEdges = false
FEATURE [PartDesign::Chamfer] Chamfer018
  Angle = 45
  Base = -> Chamfer017 [Edge10]
  BaseFeature = -> Chamfer017
  ChamferType = 0
  FlipDirection = false
  Refine = true
  Size = 3.5
  Size2 = 1
  SupportTransform = false
  Suppressed = false
  UseAllEdges = false
FEATURE [PartDesign::Chamfer] Chamfer019
  Angle = 45
  Base = -> Chamfer018 [Edge94]
  BaseFeature = -> Chamfer018
  ChamferType = 0
  FlipDirection = false
  Refine = true
  Size = 1.9
  Size2 = 1
  SupportTransform = false
  Suppressed = false
  UseAllEdges = false
FEATURE [PartDesign::Fillet] Fillet009
  Base = -> Chamfer019 [Edge83]
  BaseFeature = -> Chamfer019
  Radius = 1.1
  Refine = true
  SupportTransform = false
  Suppressed = false
  UseAllEdges = false
FEATURE [PartDesign::Fillet] Fillet010
  Base = -> Fillet009 [Edge77]
  BaseFeature = -> Fillet009
  Radius = 1.9
  Refine = true
  SupportTransform = false
  Suppressed = false
  UseAllEdges = false
FEATURE [PartDesign::Pocket] Pocket005
  BaseFeature = -> Fillet010
  Direction = (0,-1,2e-16)
  Length = 0.8
  Length2 = 5
  Profile = -> Sketch112
  ReferenceAxis = -> Sketch112 [N_Axis]
  Refine = true
  Suppressed = false
  Type = 0
FEATURE [Part::Part2DObjectPython] ShapeString001  # Draft 2D object (typed FeaturePython)
  FontFile = <path>
  Fuse = false
  Justification = 6
  JustificationReference = 0
  KeepLeftMargin = false
  MakeFace = true
  ObliqueAngle = 0
  Placement = pos=(-183.5,3.6,-57.5) rot=(0,0.707107,0.707107;3.14159rad)
  ScaleToSize = true
  Size = 10
  String = AS
  Tracking = 0
FEATURE [PartDesign::Pocket] Pocket013
  BaseFeature = -> Pocket005
  Direction = (-1e-16,-1,2e-16)
  Length = 1
  Length2 = 5
  Profile = -> ShapeString001
  ReferenceAxis = -> ShapeString001 [N_Axis]
  Refine = true
  Suppressed = false
  Type = 0
FEATURE [PartDesign::Pad] Pad020
  Direction = (0,-1,2e-16)
  Length = 25.2
  Length2 = 10
  Midplane = true
  Placement = pos=(0,0,0) rot=(1,0,0;1.5708rad)
  Profile = -> Sketch021
  ReferenceAxis = -> Sketch021 [N_Axis]
  Refine = true
  Suppressed = false
  Type = 0
FEATURE [PartDesign::Body] Body001  label="perno fermo rumble e driver solenoide"
  AllowCompound = false
  Group = -> [Sketch021,Pad020]
  Origin = -> Origin001
  Tip = -> Pad020
FEATURE [PartDesign::Pad] Pad021
  Direction = (0,-1,2e-16)
  Length = 16.8
  Length2 = 10
  Midplane = true
  Placement = pos=(0,0,0) rot=(1,0,0;1.5708rad)
  Profile = -> Sketch061
  ReferenceAxis = -> Sketch061 [N_Axis]
  Refine = true
  Suppressed = false
  Type = 0
FEATURE [PartDesign::Pocket] Pocket014
  BaseFeature = -> Pad021
  Direction = (0,1,-2e-16)
  Length = 12.8
  Length2 = 5
  Midplane = true
  Placement = pos=(0,0,0) rot=(1,0,0;1.5708rad)
  Profile = -> Sketch062
  ReferenceAxis = -> Sketch062 [N_Axis]
  Refine = true
  Suppressed = false
  Type = 0
FEATURE [PartDesign::Pad] Pad022
  BaseFeature = -> Pocket014
  Direction = (0,-1,2e-16)
  Length = 7.6
  Length2 = 10
  Midplane = true
  Placement = pos=(0,0,0) rot=(1,0,0;1.5708rad)
  Profile = -> Sketch063
  ReferenceAxis = -> Sketch063 [N_Axis]
  Refine = true
  Suppressed = false
  Type = 0
FEATURE [PartDesign::Body] Body003  label="blocco switch"
  AllowCompound = false
  Group = -> [Sketch061,Sketch062,Sketch063,Pad021,Pocket014,Pad022]
  Origin = -> Origin003
  Tip = -> Pad022
FEATURE [PartDesign::Pad] Pad024
  Direction = (0,-1,2e-16)
  Length = 17
  Length2 = 10
  Midplane = true
  Placement = pos=(0,0,0) rot=(1,0,0;1.5708rad)
  Profile = -> Sketch045
  ReferenceAxis = -> Sketch045 [N_Axis]
  Refine = true
  Suppressed = false
  Type = 0
FEATURE [PartDesign::Pocket] Pocket015
  BaseFeature = -> Pad024
  Direction = (-1,0,0)
  Length = 8
  Length2 = 5
  Placement = pos=(0,0,0) rot=(1,0,0;1.5708rad)
  Profile = -> Sketch047
  ReferenceAxis = -> Sketch047 [N_Axis]
  Refine = true
  Reversed = true
  Suppressed = false
  Type = 0
FEATURE [PartDesign::Pocket] Pocket016
  BaseFeature = -> Pocket015
  Direction = (-1,0,0)
  Length = 1
  Length2 = 5
  Placement = pos=(0,0,0) rot=(1,0,0;1.5708rad)
  Profile = -> Sketch046
  ReferenceAxis = -> Sketch046 [N_Axis]
  Refine = true
  Reversed = true
  Suppressed = false
  Type = 0
FEATURE [PartDesign::Pocket] Pocket017
  BaseFeature = -> Pocket016
  Direction = (0,1,-2e-16)
  Length = 17
  Length2 = 5
  Midplane = true
  Placement = pos=(0,0,0) rot=(1,0,0;1.5708rad)
  Profile = -> Sketch048
  ReferenceAxis = -> Sketch048 [N_Axis]
  Refine = true
  Suppressed = false
  Type = 0
FEATURE [PartDesign::Pad] Pad025
  BaseFeature = -> Pocket017
  Direction = (0,-1,2e-16)
  Length = 17
  Length2 = 10
  Midplane = true
  Placement = pos=(0,0,0) rot=(1,0,0;1.5708rad)
  Profile = -> Sketch049
  ReferenceAxis = -> Sketch049 [N_Axis]
  Refine = true
  Suppressed = false
  Type = 0
FEATURE [PartDesign::Pad] Pad026
  BaseFeature = -> Pad025
  Direction = (0,-1,2e-16)
  Length = 17
  Length2 = 10
  Midplane = true
  Placement = pos=(0,0,0) rot=(1,0,0;1.5708rad)
  Profile = -> Sketch066
  ReferenceAxis = -> Sketch066 [N_Axis]
  Refine = true
  Suppressed = false
  Type = 0
FEATURE [PartDesign::Pad] Pad027
  BaseFeature = -> Pad026
  Direction = (0,-1,2e-16)
  Length = 5
  Length2 = 10
  Midplane = true
  Placement = pos=(0,0,0) rot=(1,0,0;1.5708rad)
  Profile = -> Sketch064
  ReferenceAxis = -> Sketch064 [N_Axis]
  Refine = true
  Suppressed = false
  Type = 0
FEATURE [PartDesign::Pad] Pad028
  BaseFeature = -> Pad027
  Direction = (1,0,0)
  Length = 1
  Length2 = 10
  Placement = pos=(0,0,0) rot=(1,0,0;1.5708rad)
  Profile = -> Sketch068
  ReferenceAxis = -> Sketch068 [N_Axis]
  Refine = true
  Reversed = true
  Suppressed = false
  Type = 0
FEATURE [PartDesign::Chamfer] Chamfer020
  Angle = 45
  Base = -> Pad028 [Edge73,Edge75,Edge78,Edge77]
  BaseFeature = -> Pad028
  ChamferType = 0
  FlipDirection = false
  Placement = pos=(0,0,0) rot=(1,0,0;1.5708rad)
  Refine = true
  Size = 0.5
  Size2 = 1
  SupportTransform = false
  Suppressed = false
  UseAllEdges = false
FEATURE [PartDesign::Body] Body002  label="supporto per neopixel"
  AllowCompound = false
  Group = -> [Sketch045,Sketch047,Sketch046,Sketch048,Sketch049,Sketch066,Sketch064,Sketch068,Pad024,Pocket015,Pocket016,Pocket017,Pad025,Pad026,Pad027,Pad028,Chamfer020]
  Origin = -> Origin002
  Tip = -> Chamfer020
FEATURE [Sketcher::SketchObject] Sketch134  label="perno fermo rumble002"
  ArcFitTolerance = 1e-06
  AttachmentSupport = -> [XZ_Plane008]
  FullyConstrained = true
  MakeInternals = false
  MapMode = 5
  Placement = pos=(0,0,0) rot=(1,0,0;1.5708rad)
  sketch-geometry (16):
    g0: LineSegment StartX=0 StartY=0.45 StartZ=0 EndX=0 EndY=1.55 EndZ=0
    g1: LineSegment StartX=0.45 StartY=2 StartZ=0 EndX=1.55 EndY=2 EndZ=0
    g2: LineSegment StartX=2 StartY=1.55 StartZ=0 EndX=2 EndY=0.45 EndZ=0
    g3: LineSegment StartX=1.55 StartY=0 StartZ=0 EndX=0.45 EndY=0 EndZ=0
    g4: ArcOfCircle [constr] CenterX=0.45 CenterY=1.55 CenterZ=0 NormalX=0 NormalY=0 NormalZ=1 AngleXU=0 Radius=0.45 StartAngle=1.5708 EndAngle=3.14159
    g5: GeomPoint [constr] X=0 Y=2 Z=0
    g6: LineSegment StartX=0.45 StartY=2 StartZ=0 EndX=0 EndY=1.55 EndZ=0
    g7: ArcOfCircle [constr] CenterX=1.55 CenterY=1.55 CenterZ=0 NormalX=0 NormalY=0 NormalZ=1 AngleXU=0 Radius=0.45 StartAngle=0 EndAngle=1.5708
    g8: GeomPoint [constr] X=2 Y=2 Z=0
    g9: LineSegment StartX=2 StartY=1.55 StartZ=0 EndX=1.55 EndY=2 EndZ=0
    g10: ArcOfCircle [constr] CenterX=1.55 CenterY=0.45 CenterZ=0 NormalX=0 NormalY=0 NormalZ=1 AngleXU=0 Radius=0.45 StartAngle=4.71239 EndAngle=6.28319
    g11: GeomPoint [constr] X=2 Y=0 Z=0
    g12: LineSegment StartX=1.55 StartY=0 StartZ=0 EndX=2 EndY=0.45 EndZ=0
    g13: ArcOfCircle [constr] CenterX=0.45 CenterY=0.45 CenterZ=0 NormalX=0 NormalY=0 NormalZ=1 AngleXU=0 Radius=0.45 StartAngle=3.14159 EndAngle=4.71239
    g14: GeomPoint [constr] X=0 Y=0 Z=0
    g15: LineSegment StartX=0 StartY=0.45 StartZ=0 EndX=0.45 EndY=0 EndZ=0
  constraints (35):
    c: Coincident(g14,g-1)
    c: PointOnObject(g5,g-2)
    c: Horizontal(g1)
    c: Vertical(g2)
    c: Horizontal(g3)
    c: DistanceX(g5,g8) = 2
    c: DistanceY(g11,g8) = 2
    c: PointOnObject(g5,g0)
    c: PointOnObject(g5,g1)
    c: Tangent(g0,g4) = 1.5708
    c: Tangent(g1,g4) = 1.5708
    c: Coincident(g6,g0)
    c: Coincident(g6,g1)
    c: PointOnObject(g8,g2)
    c: PointOnObject(g8,g1)
    c: Tangent(g2,g7) = 1.5708
    c: Tangent(g1,g7) = 1.5708
    c: Coincident(g9,g2)
    c: Coincident(g9,g1)
    c: PointOnObject(g11,g2)
    c: PointOnObject(g11,g3)
    c: Tangent(g2,g10) = 1.5708
    c: Tangent(g3,g10) = 1.5708
    c: Coincident(g12,g2)
    c: Coincident(g12,g3)
    c: PointOnObject(g14,g0)
    c: PointOnObject(g14,g3)
    c: Tangent(g0,g13) = 1.5708
    c: Tangent(g3,g13) = 1.5708
    c: Coincident(g15,g0)
    c: Coincident(g15,g3)
    c: Equal(g6,g9)
    c: Equal(g9,g12)
    c: Equal(g12,g15)
    c: DistanceX(g14,g3) = 0.45
FEATURE [PartDesign::Pad] Pad029
  Direction = (0,-1,2e-16)
  Length = 17
  Length2 = 10
  Midplane = true
  Placement = pos=(0,0,0) rot=(1,0,0;1.5708rad)
  Profile = -> Sketch134
  ReferenceAxis = -> Sketch134 [N_Axis]
  Refine = true
  Suppressed = false
  Type = 0
FEATURE [PartDesign::Body] Body008  label="perno fermo neopixel"
  AllowCompound = false
  Group = -> [Sketch134,Pad029]
  Origin = -> Origin008
  Tip = -> Pad029
FEATURE [Sketcher::SketchObject] Sketch135  label="perno fermo rumble003"
  ArcFitTolerance = 1e-06
  AttachmentSupport = -> [XZ_Plane009]
  FullyConstrained = true
  MakeInternals = false
  MapMode = 5
  Placement = pos=(0,0,0) rot=(1,0,0;1.5708rad)
  sketch-geometry (16):
    g0: LineSegment StartX=4.69e-14 StartY=0.8 StartZ=0 EndX=-3.04e-14 EndY=3.1 EndZ=0
    g1: LineSegment StartX=0.8 StartY=3.9 StartZ=0 EndX=3.1 EndY=3.9 EndZ=0
    g2: LineSegment StartX=3.9 StartY=3.1 StartZ=0 EndX=3.9 EndY=0.8 EndZ=0
    g3: LineSegment StartX=3.1 StartY=0 StartZ=0 EndX=0.8 EndY=0 EndZ=0
    g4: ArcOfCircle [constr] CenterX=0.8 CenterY=3.1 CenterZ=0 NormalX=0 NormalY=0 NormalZ=1 AngleXU=0 Radius=0.8 StartAngle=1.5708 EndAngle=3.14159
    g5: GeomPoint [constr] X=0 Y=3.9 Z=0
    g6: LineSegment StartX=0.8 StartY=3.9 StartZ=0 EndX=-3.04e-14 EndY=3.1 EndZ=0
    g7: ArcOfCircle [constr] CenterX=3.1 CenterY=3.1 CenterZ=0 NormalX=0 NormalY=0 NormalZ=1 AngleXU=0 Radius=0.8 StartAngle=-2.4e-14 EndAngle=1.5708
    g8: GeomPoint [constr] X=3.9 Y=3.9 Z=0
    g9: LineSegment StartX=3.9 StartY=3.1 StartZ=0 EndX=3.1 EndY=3.9 EndZ=0
    g10: ArcOfCircle [constr] CenterX=3.1 CenterY=0.8 CenterZ=0 NormalX=0 NormalY=0 NormalZ=1 AngleXU=0 Radius=0.8 StartAngle=4.71239 EndAngle=6.28319
    g11: GeomPoint [constr] X=3.9 Y=0 Z=0
    g12: LineSegment StartX=3.1 StartY=0 StartZ=0 EndX=3.9 EndY=0.8 EndZ=0
    g13: ArcOfCircle [constr] CenterX=0.8 CenterY=0.8 CenterZ=0 NormalX=0 NormalY=0 NormalZ=1 AngleXU=0 Radius=0.8 StartAngle=3.14159 EndAngle=4.71239
    g14: GeomPoint [constr] X=0 Y=0 Z=0
    g15: LineSegment StartX=4.69e-14 StartY=0.8 StartZ=0 EndX=0.8 EndY=0 EndZ=0
  constraints (35):
    c: Coincident(g14,g-1)
    c: PointOnObject(g5,g-2)
    c: Horizontal(g1)
    c: Vertical(g2)
    c: Horizontal(g3)
    c: DistanceX(g5,g8) = 3.9
    c: DistanceY(g11,g8) = 3.9
    c: PointOnObject(g5,g0)
    c: PointOnObject(g5,g1)
    c: Tangent(g0,g4) = 1.5708
    c: Tangent(g1,g4) = 1.5708
    c: Coincident(g6,g0)
    c: Coincident(g6,g1)
    c: PointOnObject(g8,g2)
    c: PointOnObject(g8,g1)
    c: Tangent(g2,g7) = 1.5708
    c: Tangent(g1,g7) = 1.5708
    c: Coincident(g9,g2)
    c: Coincident(g9,g1)
    c: PointOnObject(g11,g2)
    c: PointOnObject(g11,g3)
    c: Tangent(g2,g10) = 1.5708
    c: Tangent(g3,g10) = 1.5708
    c: Coincident(g12,g2)
    c: Coincident(g12,g3)
    c: PointOnObject(g14,g0)
    c: PointOnObject(g14,g3)
    c: Tangent(g0,g13) = 1.5708
    c: Tangent(g3,g13) = 1.5708
    c: Coincident(g15,g0)
    c: Coincident(g15,g3)
    c: Equal(g6,g9)
    c: Equal(g9,g12)
    c: Equal(g12,g15)
    c: DistanceX(g14,g3) = 0.8
FEATURE [PartDesign::Pad] Pad030
  Direction = (0,-1,2e-16)
  Length = 25.2
  Length2 = 10
  Midplane = true
  Placement = pos=(0,0,0) rot=(1,0,0;1.5708rad)
  Profile = -> Sketch135
  ReferenceAxis = -> Sketch135 [N_Axis]
  Refine = true
  Suppressed = false
  Type = 0
FEATURE [PartDesign::Body] Body009  label="perno fermo switch - caricabatterie - grilletto"
  AllowCompound = false
  Group = -> [Sketch135,Pad030]
  Origin = -> Origin009
  Tip = -> Pad030
FEATURE [Sketcher::SketchObject] Sketch136  label="scavo_rele"
  ArcFitTolerance = 1e-06
  AttachmentSupport = -> [XZ_Plane]
  ExternalGeometry = -> [Sketch]
  FullyConstrained = true
  MakeInternals = false
  MapMode = 5
  Placement = pos=(0,0,0) rot=(1,0,0;1.5708rad)
  sketch-geometry (7):
    g0: LineSegment [constr] StartX=-173.013 StartY=-62.644 StartZ=0 EndX=-176.535 EndY=-73.4861 EndZ=0
    g1: LineSegment [constr] StartX=-173.013 StartY=-62.644 StartZ=0 EndX=-170.35 EndY=-63.5093 EndZ=0
    g2: LineSegment [constr] StartX=-173.013 StartY=-62.644 StartZ=0 EndX=-176.627 EndY=-61.4698 EndZ=0
    g3: LineSegment StartX=-176.627 StartY=-61.4698 StartZ=0 EndX=-170.35 EndY=-63.5093 EndZ=0
    g4: LineSegment StartX=-176.627 StartY=-61.4698 StartZ=0 EndX=-180.149 EndY=-72.3118 EndZ=0
    g5: LineSegment StartX=-170.35 StartY=-63.5093 StartZ=0 EndX=-173.872 EndY=-74.3513 EndZ=0
    g6: LineSegment StartX=-180.149 StartY=-72.3118 StartZ=0 EndX=-173.872 EndY=-74.3513 EndZ=0
  constraints (19):
    c: Tangent(g0,g-3)
    c: Distance(g0,g-3) = 89
    c: Distance(g0,g0) = 11.4
    c: Coincident(g1,g0)
    c: Coincident(g2,g0)
    c: Distance(g2) = 3.8
    c: Distance(g1) = 2.8
    c: Perpendicular(g0,g1)
    c: Perpendicular(g0,g2)
    c: Coincident(g3,g2)
    c: Coincident(g3,g1)
    c: Equal(g4,g0)
    c: Equal(g5,g0)
    c: Parallel(g4,g0)
    c: Parallel(g5,g0)
    c: Coincident(g4,g2)
    c: Coincident(g5,g1)
    c: Coincident(g6,g4)
    c: Coincident(g6,g5)
FEATURE [Part::Extrusion] Extrude076  label="Extrude076 - scavo_rele"
  Base = -> Sketch136
  Dir = (0,-1,2e-16)
  DirMode = 2
  FaceMakerClass = Part::FaceMakerBullseye
  FaceMakerMode = 3
  LengthFwd = 17.8
  LengthRev = 0
  Solid = true
  Symmetric = true
FEATURE [Sketcher::SketchObject] Sketch137  label="scavo_nuovo_driver"
  ArcFitTolerance = 1e-06
  AttachmentSupport = -> [XZ_Plane]
  ExternalGeometry = -> [Sketch]
  FullyConstrained = true
  MakeInternals = false
  MapMode = 5
  Placement = pos=(0,0,0) rot=(1,0,0;1.5708rad)
  sketch-geometry (7):
    g0: LineSegment [constr] StartX=-160.157 StartY=-23.0801 StartZ=0 EndX=-164.978 EndY=-37.9166 EndZ=0
    g1: LineSegment [constr] StartX=-160.157 StartY=-23.0801 StartZ=0 EndX=-157.114 EndY=-24.0689 EndZ=0
    g2: LineSegment [constr] StartX=-160.157 StartY=-23.0801 StartZ=0 EndX=-163.771 EndY=-21.9058 EndZ=0
    g3: LineSegment StartX=-163.771 StartY=-21.9058 StartZ=0 EndX=-157.114 EndY=-24.0689 EndZ=0
    g4: LineSegment StartX=-163.771 StartY=-21.9058 StartZ=0 EndX=-168.592 EndY=-36.7423 EndZ=0
    g5: LineSegment StartX=-157.114 StartY=-24.0689 StartZ=0 EndX=-161.935 EndY=-38.9054 EndZ=0
    g6: LineSegment StartX=-168.592 StartY=-36.7423 StartZ=0 EndX=-161.935 EndY=-38.9054 EndZ=0
  constraints (19):
    c: Distance(g0,g-3) = 47.4
    c: Distance(g0) = 15.6
    c: Tangent(g0,g-3)
    c: Coincident(g1,g0)
    c: Coincident(g2,g0)
    c: Distance(g1) = 3.2
    c: Distance(g2) = 3.8
    c: Perpendicular(g0,g1)
    c: Perpendicular(g0,g2)
    c: Coincident(g3,g2)
    c: Coincident(g3,g1)
    c: Equal(g4,g0)
    c: Equal(g5,g0)
    c: Parallel(g4,g0)
    c: Parallel(g5,g0)
    c: Coincident(g4,g2)
    c: Coincident(g5,g1)
    c: Coincident(g6,g4)
    c: Coincident(g6,g5)
FEATURE [Part::Extrusion] Extrude077  label="Extrude077 - scavo_nuovo_driver"
  Base = -> Sketch137
  Dir = (0,-1,2e-16)
  DirMode = 2
  FaceMakerClass = Part::FaceMakerBullseye
  FaceMakerMode = 3
  LengthFwd = 20.8
  LengthRev = 0
  Solid = true
  Symmetric = true
FEATURE [Sketcher::SketchObject] Sketch138  label="scavo_nuovo_driver_alto"
  ArcFitTolerance = 1e-06
  AttachmentSupport = -> [XZ_Plane]
  ExternalGeometry = -> [Sketch]
  FullyConstrained = true
  MakeInternals = false
  MapMode = 5
  Placement = pos=(0,0,0) rot=(1,0,0;1.5708rad)
  sketch-geometry (7):
    g0: LineSegment [constr] StartX=-188.796 StartY=17.7274 StartZ=0 EndX=-187.75 EndY=4.97025 EndZ=0
    g1: LineSegment StartX=-187.75 StartY=4.97025 StartZ=0 EndX=-189.743 EndY=4.8067 EndZ=0
    g2: LineSegment StartX=-187.75 StartY=4.97025 StartZ=0 EndX=-182.766 EndY=5.37913 EndZ=0
    g3: LineSegment StartX=-190.79 StartY=17.5638 StartZ=0 EndX=-189.743 EndY=4.8067 EndZ=0
    g4: LineSegment StartX=-183.813 StartY=18.1363 StartZ=0 EndX=-182.766 EndY=5.37913 EndZ=0
    g5: LineSegment StartX=-190.79 StartY=17.5638 StartZ=0 EndX=-188.796 EndY=17.7274 EndZ=0
    g6: LineSegment StartX=-188.796 StartY=17.7274 StartZ=0 EndX=-183.813 EndY=18.1363 EndZ=0
  constraints (20):
    c: Distance(g0) = 12.8
    c: DistanceY(g-3,g0) = 9
    c: PointOnObject(g0,g-4)
    c: PointOnObject(g0,g-4)
    c: Coincident(g1,g0)
    c: Coincident(g2,g0)
    c: Distance(g1) = 2
    c: Distance(g2) = 5
    c: Perpendicular(g0,g1)
    c: Perpendicular(g0,g2)
    c: Equal(g3,g0)
    c: Parallel(g3,g0)
    c: Coincident(g3,g1)
    c: Equal(g4,g0)
    c: Parallel(g4,g0)
    c: Coincident(g4,g2)
    c: Coincident(g5,g3)
    c: Coincident(g5,g0)
    c: Coincident(g6,g0)
    c: Coincident(g6,g4)
FEATURE [Part::Extrusion] Extrude078  label="Extrude078 - scavo_nuovo_driver_alto"
  Base = -> Sketch138
  Dir = (0,-1,2e-16)
  DirMode = 2
  FaceMakerClass = Part::FaceMakerBullseye
  FaceMakerMode = 3
  LengthFwd = 16.6
  LengthRev = 0
  Solid = true
  Symmetric = true
FEATURE [Sketcher::SketchObject] Sketch139  label="fermi_nuovo_driver_alto"
  ArcFitTolerance = 1e-06
  AttachmentSupport = -> [XZ_Plane]
  ExternalGeometry = -> [Sketch138,Sketch]
  FullyConstrained = true
  MakeInternals = false
  MapMode = 5
  Placement = pos=(0,0,0) rot=(1,0,0;1.5708rad)
  sketch-geometry (17):
    g0: LineSegment [constr] StartX=-188.314 StartY=16.4295 StartZ=0 EndX=-187.885 EndY=13.7638 EndZ=0
    g1: LineSegment [constr] StartX=-187.885 StartY=13.7638 StartZ=0 EndX=-187.456 EndY=11.0981 EndZ=0
    g2: LineSegment StartX=-187.885 StartY=13.7638 StartZ=0 EndX=-187.71 EndY=12.6778 EndZ=0
    g3: LineSegment StartX=-187.885 StartY=13.7638 StartZ=0 EndX=-188.06 EndY=14.8499 EndZ=0
    g4: LineSegment StartX=-187.71 StartY=12.6778 StartZ=0 EndX=-185.538 EndY=13.0274 EndZ=0
    g5: LineSegment StartX=-188.06 StartY=14.8499 StartZ=0 EndX=-185.888 EndY=15.1994 EndZ=0
    g6: LineSegment StartX=-185.888 StartY=15.1994 StartZ=0 EndX=-185.538 EndY=13.0274 EndZ=0
    g7: LineSegment StartX=-187.456 StartY=11.0981 StartZ=0 EndX=-189.035 EndY=10.8439 EndZ=0
    g8: LineSegment StartX=-188.314 StartY=16.4295 StartZ=0 EndX=-189.893 EndY=16.1753 EndZ=0
    g9: LineSegment StartX=-189.893 StartY=16.1753 StartZ=0 EndX=-189.035 EndY=10.8439 EndZ=0
    g10: LineSegment StartX=-187.456 StartY=11.0981 StartZ=0 EndX=-185.284 EndY=11.4477 EndZ=0
    g11: LineSegment StartX=-188.314 StartY=16.4295 StartZ=0 EndX=-186.142 EndY=16.7791 EndZ=0
    g12: LineSegment StartX=-184.308 StartY=15.4537 StartZ=0 EndX=-183.958 EndY=13.2816 EndZ=0
    g13: ArcOfCircle CenterX=-185.888 CenterY=15.1994 CenterZ=0 NormalX=0 NormalY=0 NormalZ=1 AngleXU=0 Radius=1.6 StartAngle=0.15957 EndAngle=1.73037
    g14: GeomPoint [constr] X=-184.562 Y=17.0333 Z=0
    g15: ArcOfCircle CenterX=-185.538 CenterY=13.0274 CenterZ=0 NormalX=0 NormalY=0 NormalZ=1 AngleXU=0 Radius=1.6 StartAngle=4.87196 EndAngle=6.44276
    g16: GeomPoint [constr] X=-183.704 Y=11.7019 Z=0
  constraints (43):
    c: Tangent(g1,g0) = -1.5708
    c: Distance(g0) = 2.7
    c: Equal(g1,g0)
    c: Tangent(g1,g-5)
    c: Coincident(g2,g0)
    c: Coincident(g3,g0)
    c: Distance(g2) = 1.1
    c: Equal(g3,g2)
    c: PointOnObject(g3,g2)
    c: Coincident(g4,g2)
    c: Coincident(g5,g3)
    c: Distance(g4) = 2.2
    c: Equal(g4,g5)
    c: Perpendicular(g1,g4)
    c: Perpendicular(g0,g5)
    c: Coincident(g6,g5)
    c: Coincident(g6,g4)
    c: Coincident(g7,g1)
    c: Coincident(g8,g0)
    c: Distance(g7) = 1.6
    c: Equal(g7,g8)
    c: Perpendicular(g1,g7)
    c: Perpendicular(g8,g0)
    c: Coincident(g9,g8)
    c: Coincident(g9,g7)
    c: Coincident(g10,g1)
    c: Coincident(g11,g0)
    c: Distance(g10,g16) = 3.8
    c: Perpendicular(g1,g10)
    c: Perpendicular(g1,g11)
    c: DistanceY(g0,g-4) = 3.8
    c: PointOnObject(g14,g12)
    c: PointOnObject(g14,g11)
    c: Tangent(g12,g13) = 1.5708
    c: Tangent(g11,g13) = 1.5708
    c: PointOnObject(g16,g12)
    c: PointOnObject(g16,g10)
    c: Tangent(g12,g15) = 1.5708
    c: Tangent(g10,g15) = -1.5708
    c: Equal(g13,g15)
    c: Coincident(g13,g5)
    c: Parallel(g2,g0)
    c: PointOnObject(g0,g-5)
FEATURE [Part::Extrusion] Extrude079  label="Extrude079 - fermi_nuovo_driver_alto"
  Base = -> Sketch139
  Dir = (0,-1,2e-16)
  DirMode = 2
  FaceMakerClass = Part::FaceMakerBullseye
  FaceMakerMode = 3
  LengthFwd = 25.2
  LengthRev = 0
  Solid = true
  Symmetric = true
FEATURE [Sketcher::SketchObject] Sketch140  label="scavo_diodo_nuovo_driver_alto"
  ArcFitTolerance = 1e-06
  AttachmentSupport = -> [XZ_Plane]
  ExternalGeometry = -> [Sketch138]
  FullyConstrained = true
  MakeInternals = false
  MapMode = 5
  Placement = pos=(0,0,0) rot=(1,0,0;1.5708rad)
  sketch-geometry (4):
    g0: LineSegment StartX=-190.79 StartY=17.5638 StartZ=0 EndX=-189.743 EndY=4.8067 EndZ=0
    g1: LineSegment StartX=-193.78 StartY=17.3185 StartZ=0 EndX=-192.733 EndY=4.56137 EndZ=0
    g2: LineSegment StartX=-190.79 StartY=17.5638 StartZ=0 EndX=-193.78 EndY=17.3185 EndZ=0
    g3: LineSegment StartX=-192.733 StartY=4.56137 StartZ=0 EndX=-189.743 EndY=4.8067 EndZ=0
  constraints (11):
    c: Equal(g0,g-3)
    c: Parallel(g0,g-3)
    c: Equal(g1,g-3)
    c: Parallel(g1,g-3)
    c: Coincident(g2,g0)
    c: Distance(g2) = 3
    c: Perpendicular(g0,g2)
    c: Coincident(g1,g2)
    c: Coincident(g3,g1)
    c: Coincident(g3,g0)
    c: Coincident(g0,g-3)
FEATURE [Part::Extrusion] Extrude080  label="Extrude080 - scavo_diodo_nuovo_driver_alto"
  Base = -> Sketch140
  Dir = (0,-1,2e-16)
  DirMode = 2
  FaceMakerClass = Part::FaceMakerBullseye
  FaceMakerMode = 3
  LengthFwd = 4
  LengthRev = 0
  Placement = pos=(0,7.8,0) rot=(0,0,1;0rad)
  Solid = true
  Symmetric = false
FEATURE [Part::MultiFuse] Fusion001
  Refine = true
  Shapes = -> [Cut043,Extrude079]
FEATURE [Part::Cut] Cut044
  Base = -> Fusion001
  Refine = true
  Tool = -> Extrude078
FEATURE [Part::Cut] Cut045
  Base = -> Cut044
  Refine = true
  Tool = -> Extrude080
FEATURE [Sketcher::SketchObject] Sketch141  label="fermi_nuovo_driver"
  ArcFitTolerance = 1e-06
  AttachmentSupport = -> [XZ_Plane]
  ExternalGeometry = -> [Sketch,Sketch137]
  FullyConstrained = true
  MakeInternals = false
  MapMode = 5
  Placement = pos=(0,0,0) rot=(1,0,0;1.5708rad)
  sketch-geometry (17):
    g0: LineSegment [constr] StartX=-157.114 StartY=-24.0689 StartZ=0 EndX=-160.157 EndY=-23.0801 EndZ=0
    g1: LineSegment [constr] StartX=-160.157 StartY=-23.0801 StartZ=0 EndX=-162.939 EndY=-31.6396 EndZ=0
    g2: LineSegment [constr] StartX=-162.939 StartY=-31.6396 StartZ=0 EndX=-164.607 EndY=-36.7753 EndZ=0
    g3: LineSegment StartX=-164.607 StartY=-36.7753 StartZ=0 EndX=-166.7 EndY=-36.0955 EndZ=0
    g4: LineSegment StartX=-167.727 StartY=-34.0793 StartZ=0 EndX=-167.047 EndY=-31.987 EndZ=0
    g5: LineSegment StartX=-165.031 StartY=-30.9598 StartZ=0 EndX=-161.417 EndY=-32.134 EndZ=0
    g6: LineSegment StartX=-161.417 StartY=-32.134 StartZ=0 EndX=-163.086 EndY=-37.2697 EndZ=0
    g7: LineSegment StartX=-164.607 StartY=-36.7753 StartZ=0 EndX=-163.086 EndY=-37.2697 EndZ=0
    g8: LineSegment StartX=-165.525 StartY=-32.4814 StartZ=0 EndX=-166.205 EndY=-34.5738 EndZ=0
    g9: LineSegment StartX=-166.205 StartY=-34.5738 StartZ=0 EndX=-164.113 EndY=-35.2536 EndZ=0
    g10: LineSegment StartX=-164.113 StartY=-35.2536 StartZ=0 EndX=-163.433 EndY=-33.1613 EndZ=0
    g11: LineSegment StartX=-163.433 StartY=-33.1613 StartZ=0 EndX=-165.525 EndY=-32.4814 EndZ=0
    g12: ArcOfCircle CenterX=-165.525 CenterY=-32.4814 CenterZ=0 NormalX=0 NormalY=0 NormalZ=1 AngleXU=0 Radius=1.6 StartAngle=1.25664 EndAngle=2.82743
    g13: GeomPoint [constr] X=-166.553 Y=-30.4653 Z=0
    g14: ArcOfCircle CenterX=-166.205 CenterY=-34.5738 CenterZ=0 NormalX=0 NormalY=0 NormalZ=1 AngleXU=0 Radius=1.6 StartAngle=2.82743 EndAngle=4.39823
    g15: GeomPoint [constr] X=-168.221 Y=-35.601 Z=0
    g16: LineSegment [constr] StartX=-160.157 StartY=-23.0801 StartZ=0 EndX=-164.978 EndY=-37.9166 EndZ=0
  constraints (44):
    c: Coincident(g0,g-4)
    c: PointOnObject(g0,g-3)
    c: Parallel(g0,g-4)
    c: Coincident(g1,g0)
    c: Parallel(g1,g-3)
    c: Coincident(g2,g1)
    c: Distance(g2) = 5.4
    c: Coincident(g3,g2)
    c: Parallel(g2,g-3)
    c: Distance(g15,g13) = 5.4
    c: Perpendicular(g3,g2)
    c: Parallel(g4,g2)
    c: Distance(g5,g13) = 5.4
    c: Distance(g3,g15) = 3.8
    c: Perpendicular(g4,g5)
    c: Coincident(g6,g5)
    c: Distance(g6) = 5.4
    c: Parallel(g6,g4)
    c: Coincident(g7,g2)
    c: Coincident(g7,g6)
    c: Coincident(g8,g9)
    c: Coincident(g9,g10)
    c: Coincident(g10,g11)
    c: Coincident(g11,g8)
    c: Distance(g8,g10) = 2.2
    c: Distance(g9,g11) = 2.2
    c: Perpendicular(g11,g8)
    c: Equal(g8,g10)
    c: Equal(g11,g9)
    c: Tangent(g10,g2)
    c: Distance(g10,g1) = 1.6
    c: PointOnObject(g13,g4)
    c: PointOnObject(g13,g5)
    c: Tangent(g4,g12) = 1.5708
    c: Tangent(g5,g12) = 1.5708
    c: PointOnObject(g15,g4)
    c: Tangent(g4,g14) = 1.5708
    c: Tangent(g3,g14) = 1.5708
    c: Equal(g14,g12)
    c: Coincident(g12,g8)
    c: Coincident(g16,g0)
    c: PointOnObject(g16,g-5)
    c: Parallel(g16,g-3)
    c: Distance(g16,g2) = 1.2
FEATURE [Part::Extrusion] Extrude081  label="Extrude081 - fermi_nuovo_driver"
  Base = -> Sketch141
  Dir = (0,-1,2e-16)
  DirMode = 2
  FaceMakerClass = Part::FaceMakerBullseye
  FaceMakerMode = 3
  LengthFwd = 25.2
  LengthRev = 0
  Solid = true
  Symmetric = true
FEATURE [Part::MultiFuse] Fusion002
  Refine = true
  Shapes = -> [Cut045,Extrude081]
FEATURE [Part::Cut] Cut046
  Base = -> Fusion002
  Refine = true
  Tool = -> Extrude077
FEATURE [Sketcher::SketchObject] Sketch142  label="fermi_rele"
  ArcFitTolerance = 1e-06
  AttachmentSupport = -> [XZ_Plane]
  ExternalGeometry = -> [Sketch,Sketch136]
  FullyConstrained = true
  MakeInternals = false
  MapMode = 5
  Placement = pos=(0,0,0) rot=(1,0,0;1.5708rad)
  sketch-geometry (15):
    g0: LineSegment StartX=-177.245 StartY=-63.3719 StartZ=0 EndX=-177.924 EndY=-65.4642 EndZ=0
    g1: LineSegment StartX=-175.228 StartY=-62.3446 StartZ=0 EndX=-171.614 EndY=-63.5189 EndZ=0
    g2: LineSegment StartX=-171.614 StartY=-63.5189 StartZ=0 EndX=-173.283 EndY=-68.6546 EndZ=0
    g3: LineSegment StartX=-176.897 StartY=-67.4803 StartZ=0 EndX=-173.283 EndY=-68.6546 EndZ=0
    g4: LineSegment StartX=-175.723 StartY=-63.8663 StartZ=0 EndX=-173.631 EndY=-64.5461 EndZ=0
    g5: LineSegment StartX=-175.723 StartY=-63.8663 StartZ=0 EndX=-176.403 EndY=-65.9586 EndZ=0
    g6: LineSegment StartX=-173.631 StartY=-64.5461 StartZ=0 EndX=-174.31 EndY=-66.6385 EndZ=0
    g7: LineSegment StartX=-176.403 StartY=-65.9586 StartZ=0 EndX=-174.31 EndY=-66.6385 EndZ=0
    g8: LineSegment [constr] StartX=-173.631 StartY=-64.5461 StartZ=0 EndX=-173.136 EndY=-63.0245 EndZ=0
    g9: LineSegment [constr] StartX=-173.631 StartY=-64.5461 StartZ=0 EndX=-172.109 EndY=-65.0406 EndZ=0
    g10: LineSegment [constr] StartX=-170.35 StartY=-63.5093 StartZ=0 EndX=-173.013 EndY=-62.644 EndZ=0
    g11: ArcOfCircle CenterX=-175.723 CenterY=-63.8663 CenterZ=0 NormalX=0 NormalY=0 NormalZ=1 AngleXU=0 Radius=1.6 StartAngle=1.25664 EndAngle=2.82743
    g12: GeomPoint [constr] X=-176.75 Y=-61.8502 Z=0
    g13: ArcOfCircle CenterX=-176.403 CenterY=-65.9586 CenterZ=0 NormalX=0 NormalY=0 NormalZ=1 AngleXU=0 Radius=1.6 StartAngle=2.82743 EndAngle=4.39823
    g14: GeomPoint [constr] X=-178.419 Y=-66.9859 Z=0
  constraints (39):
    c: Distance(g14,g12) = 5.4
    c: Distance(g1,g12) = 5.4
    c: Perpendicular(g1,g0)
    c: Coincident(g2,g1)
    c: Parallel(g2,g0)
    c: Coincident(g3,g2)
    c: Parallel(g2,g-3)
    c: Coincident(g5,g4)
    c: Distance(g5) = 2.2
    c: Distance(g4) = 2.2
    c: Perpendicular(g4,g5)
    c: Coincident(g6,g4)
    c: Equal(g6,g5)
    c: Parallel(g6,g5)
    c: Coincident(g7,g5)
    c: Coincident(g7,g6)
    c: Coincident(g8,g4)
    c: Coincident(g9,g4)
    c: Distance(g8) = 1.6
    c: Distance(g9) = 1.6
    c: Parallel(g8,g6)
    c: Parallel(g9,g4)
    c: PointOnObject(g8,g1)
    c: PointOnObject(g9,g2)
    c: Coincident(g10,g-4)
    c: Parallel(g10,g-4)
    c: PointOnObject(g10,g-3)
    c: Tangent(g6,g-3) = 1.5708
    c: Distance(g4,g10) = 2
    c: PointOnObject(g12,g1)
    c: Tangent(g1,g11) = 1.5708
    c: Tangent(g0,g11) = -1.5708
    c: PointOnObject(g14,g3)
    c: PointOnObject(g14,g0)
    c: Tangent(g3,g13) = -1.5708
    c: Tangent(g0,g13) = -1.5708
    c: Equal(g11,g13)
    c: Coincident(g11,g4)
    c: Parallel(g3,g1)
FEATURE [Part::Extrusion] Extrude082  label="Extrude082 - fermi_rele"
  Base = -> Sketch142
  Dir = (0,-1,2e-16)
  DirMode = 2
  FaceMakerClass = Part::FaceMakerBullseye
  FaceMakerMode = 3
  LengthFwd = 25.2
  LengthRev = 0
  Solid = true
  Symmetric = true
FEATURE [Part::MultiFuse] Fusion003
  Refine = true
  Shapes = -> [Cut046,Extrude082]
FEATURE [Part::Cut] Cut047
  Base = -> Fusion003
  Refine = true
  Tool = -> Extrude076
FEATURE [Sketcher::SketchObject] Sketch143  label="foro_passaggio_cavi_led_batteria"
  ArcFitTolerance = 1e-06
  AttachmentSupport = -> [XZ_Plane]
  ExternalGeometry = -> [Sketch,Sketch042,Sketch036]
  FullyConstrained = true
  MakeInternals = false
  MapMode = 5
  Placement = pos=(0,0,0) rot=(1,0,0;1.5708rad)
  sketch-geometry (4):
    g0: LineSegment StartX=-207.775 StartY=-41.3701 StartZ=0 EndX=-213.607 EndY=-53.8767 EndZ=0
    g1: LineSegment StartX=-213.607 StartY=-53.8767 StartZ=0 EndX=-211.843 EndY=-59.5559 EndZ=0
    g2: LineSegment StartX=-207.775 StartY=-41.3701 StartZ=0 EndX=-207.775 EndY=-50.8316 EndZ=0
    g3: LineSegment StartX=-207.775 StartY=-50.8316 StartZ=0 EndX=-211.843 EndY=-59.5559 EndZ=0
  constraints (9):
    c: Coincident(g0,g-3)
    c: PointOnObject(g1,g-6)
    c: Coincident(g1,g0)
    c: Coincident(g2,g0)
    c: Coincident(g2,g-7)
    c: Coincident(g3,g2)
    c: Parallel(g3,g0)
    c: Coincident(g3,g1)
    c: Coincident(g0,g-5)
FEATURE [Part::Extrusion] Extrude083  label="Extrude083 - foro_passaggio_cavi_led_batteria"
  Base = -> Sketch143
  Dir = (0,-1,2e-16)
  DirMode = 2
  FaceMakerClass = Part::FaceMakerBullseye
  FaceMakerMode = 3
  LengthFwd = 6
  LengthRev = 0
  Solid = true
  Symmetric = true
FEATURE [Part::Cut] Cut048
  Base = -> Cut047
  Refine = true
  Tool = -> Extrude083
FEATURE [Sketcher::SketchObject] Sketch144  label="foro_areazione_alimentatore"
  ArcFitTolerance = 1e-06
  AttachmentSupport = -> [XZ_Plane]
  ExternalGeometry = -> [Sketch036]
  FullyConstrained = true
  MakeInternals = false
  MapMode = 5
  Placement = pos=(0,0,0) rot=(1,0,0;1.5708rad)
  sketch-geometry (4):
    g0: LineSegment StartX=-211.843 StartY=-60.3701 StartZ=0 EndX=-207.775 EndY=-60.3701 EndZ=0
    g1: LineSegment StartX=-207.775 StartY=-60.3701 StartZ=0 EndX=-207.775 EndY=-70.3701 EndZ=0
    g2: LineSegment StartX=-211.843 StartY=-60.3701 StartZ=0 EndX=-211.843 EndY=-70.3701 EndZ=0
    g3: LineSegment StartX=-207.775 StartY=-70.3701 StartZ=0 EndX=-211.843 EndY=-70.3701 EndZ=0
  constraints (11):
    c: Horizontal(g0)
    c: Distance(g1) = 10
    c: Coincident(g1,g0)
    c: Tangent(g1,g-3)
    c: PointOnObject(g0,g-4)
    c: Coincident(g2,g0)
    c: PointOnObject(g2,g-4)
    c: Coincident(g3,g1)
    c: Horizontal(g3)
    c: Coincident(g3,g2)
    c: DistanceY(g0,g-3) = 19
FEATURE [Part::Extrusion] Extrude084  label="Extrude084 - foro_areazione_alimentatore"
  Base = -> Sketch144
  Dir = (0,-1,2e-16)
  DirMode = 2
  FaceMakerClass = Part::FaceMakerBullseye
  FaceMakerMode = 3
  LengthFwd = 10
  LengthRev = 0
  Solid = true
  Symmetric = true
FEATURE [Part::Cut] Cut049
  Base = -> Cut048
  Refine = true
  Tool = -> Extrude084
FEATURE [Sketcher::SketchObject] Sketch145  label="foro_per_condesatore"
  ArcFitTolerance = 1e-06
  AttachmentSupport = -> [XZ_Plane]
  ExternalGeometry = -> [Sketch,Sketch139]
  FullyConstrained = true
  MakeInternals = false
  MapMode = 5
  Placement = pos=(0,0,0) rot=(1,0,0;1.5708rad)
  sketch-geometry (1):
    g0: Circle CenterX=-182.345 CenterY=7.02342 CenterZ=0 NormalX=0 NormalY=0 NormalZ=1 AngleXU=0 Radius=5.2
  constraints (3):
    c: Diameter(g0) = 10.4
    c: Tangent(g0,g-3)
    c: Tangent(g0,g-4)
FEATURE [Part::Extrusion] Extrude085  label="Extrude085 - foro_per_condesatore"
  Base = -> Sketch145
  Dir = (0,-1,2e-16)
  DirMode = 2
  FaceMakerClass = Part::FaceMakerBullseye
  FaceMakerMode = 3
  LengthFwd = 25.2
  LengthRev = 0
  Solid = true
  Symmetric = true
FEATURE [Part::Cut] Cut050
  Base = -> Cut049
  Refine = true
  Tool = -> Extrude085
FEATURE [Sketcher::SketchObject] Sketch146  label="scavo_pulsante_6x6_per_led_batteria"
  ArcFitTolerance = 1e-06
  AttachmentSupport = -> [XZ_Plane]
  ExternalGeometry = -> [Sketch016]
  FullyConstrained = true
  MakeInternals = false
  MapMode = 5
  Placement = pos=(0,0,0) rot=(1,0,0;1.5708rad)
  sketch-geometry (5):
    g0: LineSegment StartX=-216.643 StartY=-65.8316 StartZ=0 EndX=-216.643 EndY=-72.8316 EndZ=0
    g1: LineSegment StartX=-216.643 StartY=-72.8316 StartZ=0 EndX=-210.243 EndY=-72.8316 EndZ=0
    g2: LineSegment StartX=-210.243 StartY=-72.8316 StartZ=0 EndX=-210.243 EndY=-65.8316 EndZ=0
    g3: LineSegment StartX=-210.243 StartY=-65.8316 StartZ=0 EndX=-216.643 EndY=-65.8316 EndZ=0
    g4: GeomPoint [constr] X=-213.443 Y=-69.3316 Z=0
  constraints (13):
    c: Coincident(g0,g1)
    c: Coincident(g1,g2)
    c: Coincident(g2,g3)
    c: Coincident(g3,g0)
    c: Vertical(g0)
    c: Vertical(g2)
    c: Horizontal(g1)
    c: Horizontal(g3)
    c: Distance(g0,g2) = 6.4
    c: Distance(g1,g3) = 7
    c: Tangent(g1,g-3)
    c: Symmetric(g0,g2,g4)
    c: Vertical(g-3,g4)
FEATURE [Part::Extrusion] Extrude086  label="Extrude086 - scavo_pulsante_6x6_per_led_batteria"
  Base = -> Sketch146
  Dir = (0,-1,2e-16)
  DirMode = 2
  FaceMakerClass = Part::FaceMakerBullseye
  FaceMakerMode = 3
  LengthFwd = 4
  LengthRev = 0
  Placement = pos=(0,12.6,0) rot=(0,0,1;0rad)
  Solid = true
  Symmetric = false
FEATURE [Sketcher::SketchObject] Sketch147  label="scavo_led_stato_batteria"
  ArcFitTolerance = 1e-06
  AttachmentSupport = -> [XZ_Plane]
  ExternalGeometry = -> [Sketch016]
  FullyConstrained = true
  MakeInternals = false
  MapMode = 5
  Placement = pos=(0,0,0) rot=(1,0,0;1.5708rad)
  sketch-geometry (5):
    g0: LineSegment StartX=-215.843 StartY=-56.2316 StartZ=0 EndX=-215.843 EndY=-65.4316 EndZ=0
    g1: LineSegment StartX=-215.843 StartY=-65.4316 StartZ=0 EndX=-211.043 EndY=-65.4316 EndZ=0
    g2: LineSegment StartX=-211.043 StartY=-65.4316 StartZ=0 EndX=-211.043 EndY=-56.2316 EndZ=0
    g3: LineSegment StartX=-211.043 StartY=-56.2316 StartZ=0 EndX=-215.843 EndY=-56.2316 EndZ=0
    g4: GeomPoint [constr] X=-213.443 Y=-60.8316 Z=0
  constraints (13):
    c: Coincident(g0,g1)
    c: Coincident(g1,g2)
    c: Coincident(g2,g3)
    c: Coincident(g3,g0)
    c: Distance(g0,g2) = 4.8
    c: Distance(g1,g3) = 9.2
    c: Equal(g0,g2)
    c: Equal(g1,g3)
    c: Perpendicular(g3,g0)
    c: DistanceY(g-3,g0) = 11.4
    c: Vertical(g2)
    c: Symmetric(g0,g2,g4)
    c: Vertical(g4,g-3)
FEATURE [Part::Extrusion] Extrude087  label="Extrude087 - scavo_led_stato_batteria"
  Base = -> Sketch147
  Dir = (0,-1,2e-16)
  DirMode = 2
  FaceMakerClass = Part::FaceMakerBullseye
  FaceMakerMode = 3
  LengthFwd = 2.2
  LengthRev = 0
  Placement = pos=(0,12.6,0) rot=(0,0,1;0rad)
  Solid = true
  Symmetric = false
FEATURE [Sketcher::SketchObject] Sketch148
  ArcFitTolerance = 1e-06
  AttachmentSupport = -> [Pad016]
  ExternalGeometry = -> [Pad016]
  FullyConstrained = true
  MakeInternals = false
  MapMode = 5
  Placement = pos=(0,0,-80.4316) rot=(1,0,0;3.14159rad)
  sketch-geometry (8):
    g0: LineSegment StartX=-176.685 StartY=3.6 StartZ=0 EndX=-186.685 EndY=3.6 EndZ=0
    g1: LineSegment StartX=-176.685 StartY=3.6 StartZ=0 EndX=-176.685 EndY=-9e-16 EndZ=0
    g2: LineSegment [constr] StartX=-186.685 StartY=3.6 StartZ=0 EndX=-186.685 EndY=-9e-16 EndZ=0
    g3: ArcOfEllipse CenterX=-186.685 CenterY=-9e-16 CenterZ=0 NormalX=0 NormalY=0 NormalZ=1 MajorRadius=10 MinorRadius=3.6 AngleXU=0 StartAngle=0 EndAngle=1.5708
    g4: LineSegment [constr] StartX=-176.685 StartY=-1e-15 StartZ=0 EndX=-196.685 EndY=-1e-15 EndZ=0
    g5: LineSegment [constr] StartX=-186.685 StartY=3.6 StartZ=0 EndX=-186.685 EndY=-3.6 EndZ=0
    g6: GeomPoint [constr] X=-177.356 Y=-1e-15 Z=0
    g7: GeomPoint [constr] X=-196.015 Y=-1e-15 Z=0
  constraints (13):
    c: Distance(g0) = 10
    c: Coincident(g0,g-5)
    c: PointOnObject(g0,g-3)
    c: Coincident(g1,g0)
    c: Coincident(g1,g-5)
    c: Coincident(g2,g0)
    c: Vertical(g2)
    c: PointOnObject(g2,g-4)
    c: InternalAlignment(g4-g7 -> g3) x4
    c: Coincident(g3,g2)
    c: Coincident(g3,g0)
    c: Coincident(g3,g1)
    c: Horizontal(g4)
FEATURE [PartDesign::SubtractivePipe] SubtractivePipe004
  AuxilleryCurvelinear = true
  AuxillerySpineTangent = false
  BaseFeature = -> Pad016
  Binormal = (0,0,0)
  Mode = 0
  Profile = -> Sketch148
  Refine = true
  Spine = -> Pad016 [Edge253]
  SpineTangent = false
  Suppressed = false
  Transformation = 0
  Transition = 0
FEATURE [Sketcher::SketchObject] Sketch149
  ArcFitTolerance = 1e-06
  AttachmentSupport = -> [Pad016]
  ExternalGeometry = -> [Pad016]
  FullyConstrained = true
  MakeInternals = false
  MapMode = 5
  Placement = pos=(0,0,-80.4316) rot=(1,0,0;3.14159rad)
  sketch-geometry (8):
    g0: LineSegment StartX=-215.932 StartY=3.6 StartZ=0 EndX=-205.932 EndY=3.6 EndZ=0
    g1: LineSegment StartX=-215.932 StartY=3.6 StartZ=0 EndX=-215.932 EndY=-4e-16 EndZ=0
    g2: LineSegment [constr] StartX=-205.932 StartY=3.6 StartZ=0 EndX=-205.932 EndY=-9e-16 EndZ=0
    g3: ArcOfEllipse CenterX=-205.932 CenterY=-1e-15 CenterZ=0 NormalX=0 NormalY=0 NormalZ=1 MajorRadius=10 MinorRadius=3.6 AngleXU=-3.14159 StartAngle=4.71239 EndAngle=6.28319
    g4: LineSegment [constr] StartX=-215.932 StartY=-1e-15 StartZ=0 EndX=-195.932 EndY=-1e-15 EndZ=0
    g5: LineSegment [constr] StartX=-205.932 StartY=-3.6 StartZ=0 EndX=-205.932 EndY=3.6 EndZ=0
    g6: GeomPoint [constr] X=-215.262 Y=-2.1e-15 Z=0
    g7: GeomPoint [constr] X=-196.602 Y=-9e-16 Z=0
  constraints (13):
    c: Distance(g0) = 10
    c: Coincident(g0,g-5)
    c: PointOnObject(g0,g-5)
    c: Coincident(g1,g0)
    c: Coincident(g1,g-4)
    c: Coincident(g2,g0)
    c: Vertical(g2)
    c: PointOnObject(g2,g-3)
    c: InternalAlignment(g4-g7 -> g3) x4
    c: Coincident(g3,g2)
    c: Coincident(g3,g0)
    c: Coincident(g3,g1)
    c: Horizontal(g4)
FEATURE [PartDesign::SubtractivePipe] SubtractivePipe005
  AuxilleryCurvelinear = true
  AuxillerySpineTangent = false
  BaseFeature = -> SubtractivePipe004
  Binormal = (0,0,0)
  Mode = 0
  Profile = -> Sketch149
  Refine = true
  Spine = -> Pad016 [Edge251,Edge256,Edge255]
  SpineTangent = false
  Suppressed = false
  Transformation = 0
  Transition = 0
FEATURE [PartDesign::SubtractiveLoft] SubtractiveLoft002
  BaseFeature = -> SubtractivePipe005
  Closed = false
  Profile = -> Sketch129
  Refine = true
  Ruled = false
  Sections = -> [Sketch130]
  Suppressed = false
FEATURE [PartDesign::SubtractiveLoft] SubtractiveLoft003
  BaseFeature = -> SubtractiveLoft002
  Closed = false
  Profile = -> Clone2D001
  Refine = true
  Ruled = false
  Sections = -> [Sketch131]
  Suppressed = false
FEATURE [PartDesign::Chamfer] Chamfer010
  Angle = 45
  Base = -> SubtractiveLoft003 [Edge203,Edge204,Edge202,Edge201,Edge195]
  BaseFeature = -> SubtractiveLoft003
  ChamferType = 0
  FlipDirection = false
  Refine = true
  Size = 1.5
  Size2 = 1
  SupportTransform = false
  Suppressed = false
  UseAllEdges = false
FEATURE [PartDesign::Chamfer] Chamfer011
  Angle = 45
  Base = -> Chamfer010 [Edge15]
  BaseFeature = -> Chamfer010
  ChamferType = 0
  FlipDirection = false
  Refine = true
  Size = 1.6
  Size2 = 1
  SupportTransform = false
  Suppressed = false
  UseAllEdges = false
FEATURE [PartDesign::Chamfer] Chamfer012
  Angle = 45
  Base = -> Chamfer011 [Edge10]
  BaseFeature = -> Chamfer011
  ChamferType = 0
  FlipDirection = false
  Refine = true
  Size = 3.5
  Size2 = 1
  SupportTransform = false
  Suppressed = false
  UseAllEdges = false
FEATURE [PartDesign::Chamfer] Chamfer013
  Angle = 45
  Base = -> Chamfer012 [Edge94]
  BaseFeature = -> Chamfer012
  ChamferType = 0
  FlipDirection = false
  Refine = true
  Size = 1.9
  Size2 = 1
  SupportTransform = false
  Suppressed = false
  UseAllEdges = false
FEATURE [PartDesign::Fillet] Fillet007
  Base = -> Chamfer013 [Edge83]
  BaseFeature = -> Chamfer013
  Radius = 1.1
  Refine = true
  SupportTransform = false
  Suppressed = false
  UseAllEdges = false
FEATURE [PartDesign::Fillet] Fillet008
  Base = -> Fillet007 [Edge75]
  BaseFeature = -> Fillet007
  Radius = 1.9
  Refine = true
  SupportTransform = false
  Suppressed = false
  UseAllEdges = false
FEATURE [PartDesign::Pocket] Pocket011
  BaseFeature = -> Fillet008
  Direction = (0,1,-2e-16)
  Length = 0.8
  Length2 = 5
  Profile = -> Sketch132
  ReferenceAxis = -> Sketch132 [N_Axis]
  Refine = true
  Suppressed = false
  Type = 0
FEATURE [PartDesign::Pocket] Pocket012
  BaseFeature = -> Pocket011
  Direction = (0,1,0)
  Length = 1
  Length2 = 5
  Profile = -> ShapeString
  ReferenceAxis = -> ShapeString [N_Axis]
  Refine = true
  Suppressed = false
  Type = 0
FEATURE [Sketcher::SketchObject] Sketch150
  ArcFitTolerance = 1e-06
  AttachmentSupport = -> [Pad008]
  ExternalGeometry = -> [Pad008]
  FullyConstrained = true
  MakeInternals = false
  MapMode = 5
  Placement = pos=(0,3.6,0) rot=(0,0.707107,0.707107;3.14159rad)
  sketch-geometry (7):
    g0: LineSegment [constr] StartX=210.343 StartY=-66.0316 StartZ=0 EndX=210.343 EndY=-72.8316 EndZ=0
    g1: LineSegment [constr] StartX=210.343 StartY=-72.8316 StartZ=0 EndX=216.543 EndY=-72.8316 EndZ=0
    g2: LineSegment [constr] StartX=216.543 StartY=-72.8316 StartZ=0 EndX=216.543 EndY=-66.0316 EndZ=0
    g3: LineSegment [constr] StartX=216.543 StartY=-66.0316 StartZ=0 EndX=210.343 EndY=-66.0316 EndZ=0
    g4: LineSegment [constr] StartX=210.343 StartY=-72.8316 StartZ=0 EndX=216.543 EndY=-66.0316 EndZ=0
    g5: LineSegment [constr] StartX=210.343 StartY=-66.0316 StartZ=0 EndX=213.443 EndY=-69.4316 EndZ=0
    g6: Circle CenterX=213.443 CenterY=-69.4316 CenterZ=0 NormalX=0 NormalY=0 NormalZ=1 AngleXU=0 Radius=2
  constraints (18):
    c: Coincident(g0,g1)
    c: Coincident(g1,g2)
    c: Coincident(g2,g3)
    c: Coincident(g3,g0)
    c: Vertical(g0)
    c: Vertical(g2)
    c: Horizontal(g1)
    c: Horizontal(g3)
    c: Distance(g0,g2) = 6.2
    c: Distance(g1,g3) = 6.8
    c: DistanceY(g-3,g1) = 4
    c: Coincident(g4,g0)
    c: Coincident(g4,g2)
    c: Coincident(g5,g0)
    c: Symmetric(g0,g2,g5)
    c: Diameter(g6) = 4
    c: Coincident(g6,g5)
    c: Vertical(g5,g-3)
FEATURE [Sketcher::SketchObject] Sketch151
  ArcFitTolerance = 1e-06
  AttachmentSupport = -> [Pad008]
  ExternalGeometry = -> [Pad008]
  FullyConstrained = true
  MakeInternals = false
  MapMode = 5
  Placement = pos=(0,3.6,0) rot=(0,0.707107,0.707107;3.14159rad)
  sketch-geometry (10):
    g0: LineSegment [constr] StartX=211.143 StartY=-56.2316 StartZ=0 EndX=211.143 EndY=-65.4316 EndZ=0
    g1: LineSegment [constr] StartX=211.143 StartY=-65.4316 StartZ=0 EndX=215.743 EndY=-65.4316 EndZ=0
    g2: LineSegment [constr] StartX=215.743 StartY=-65.4316 StartZ=0 EndX=215.743 EndY=-56.2316 EndZ=0
    g3: LineSegment [constr] StartX=215.743 StartY=-56.2316 StartZ=0 EndX=211.143 EndY=-56.2316 EndZ=0
    g4: LineSegment StartX=212.243 StartY=-63.8316 StartZ=0 EndX=214.643 EndY=-63.8316 EndZ=0
    g5: LineSegment StartX=214.643 StartY=-63.8316 StartZ=0 EndX=214.643 EndY=-57.0316 EndZ=0
    g6: LineSegment StartX=214.643 StartY=-57.0316 StartZ=0 EndX=212.243 EndY=-57.0316 EndZ=0
    g7: LineSegment StartX=212.243 StartY=-57.0316 StartZ=0 EndX=212.243 EndY=-63.8316 EndZ=0
    g8: GeomPoint [constr] X=213.443 Y=-60.4316 Z=0
    g9: GeomPoint [constr] X=213.443 Y=-60.8316 Z=0
  constraints (26):
    c: Coincident(g0,g1)
    c: Coincident(g1,g2)
    c: Coincident(g2,g3)
    c: Coincident(g3,g0)
    c: Vertical(g0)
    c: Vertical(g2)
    c: Horizontal(g1)
    c: Horizontal(g3)
    c: Distance(g0,g2) = 4.6
    c: Distance(g1,g3) = 9.2
    c: DistanceY(g-3,g1) = 11.4
    c: Coincident(g4,g5)
    c: Coincident(g5,g6)
    c: Coincident(g6,g7)
    c: Coincident(g7,g4)
    c: Horizontal(g4)
    c: Horizontal(g6)
    c: Vertical(g5)
    c: Vertical(g7)
    c: Symmetric(g6,g4,g8)
    c: Distance(g5,g7) = 2.4
    c: Distance(g4,g6) = 6.8
    c: Symmetric(g2,g0,g9)
    c: Vertical(g8,g9)
    c: DistanceY(g1,g4) = 1.6
    c: Vertical(g9,g-3)
FEATURE [PartDesign::Pocket] Pocket019
  BaseFeature = -> Pocket013
  Direction = (0,-1,2e-16)
  Length = 3.6
  Length2 = 5
  Profile = -> Sketch151
  ReferenceAxis = -> Sketch151 [N_Axis]
  Refine = true
  Suppressed = false
  Type = 0
FEATURE [PartDesign::Pocket] Pocket018
  BaseFeature = -> Pocket019
  Direction = (0,-1,2e-16)
  Length = 3.6
  Length2 = 5
  Profile = -> Sketch150
  ReferenceAxis = -> Sketch150 [N_Axis]
  Refine = true
  Suppressed = false
  Type = 0
FEATURE [PartDesign::Point] DatumPoint
  AttacherType = Attacher::AttachEnginePoint
  AttachmentSupport = -> [Sketch150]
  MapMode = 36
  Placement = pos=(-213.443,3.6,-69.4316) rot=(0,1,0;3.14159rad)
FEATURE [PartDesign::Plane] DatumPlane002
  AttachmentSupport = -> [DatumPoint]
  Length = 260.281
  MapMode = 1
  Placement = pos=(-213.443,3.6,-69.4316) rot=(0,0,1;0rad)
  ResizeMode = 0
  Width = 71.8377
FEATURE [Sketcher::SketchObject] Sketch152
  ArcFitTolerance = 1e-06
  AttachmentSupport = -> [DatumPlane002]
  ExternalGeometry = -> [Sketch150]
  FullyConstrained = true
  MakeInternals = false
  MapMode = 5
  Placement = pos=(-213.443,3.6,-69.4316) rot=(0,0,1;0rad)
  sketch-geometry (7):
    g0: LineSegment StartX=0 StartY=0 StartZ=0 EndX=-4 EndY=5.1e-15 EndZ=0
    g1: ArcOfEllipse CenterX=0 CenterY=0 CenterZ=0 NormalX=0 NormalY=0 NormalZ=1 MajorRadius=4 MinorRadius=3.6 AngleXU=3.14159 StartAngle=2e-16 EndAngle=1.5708
    g2: LineSegment [constr] StartX=-4 StartY=9e-16 StartZ=0 EndX=4 EndY=-9e-16 EndZ=0
    g3: LineSegment [constr] StartX=0 StartY=-3.6 StartZ=0 EndX=0 EndY=3.6 EndZ=0
    g4: GeomPoint [constr] X=-1.74356 Y=2.5e-15 Z=0
    g5: GeomPoint [constr] X=1.74356 Y=-2e-15 Z=0
    g6: LineSegment StartX=0 StartY=0 StartZ=0 EndX=-5.5e-15 EndY=-3.6 EndZ=0
  constraints (11):
    c: PointOnObject(g1,g-2)
    c: Distance(g0) = 4
    c: PointOnObject(g0,g-1)
    c: InternalAlignment(g2-g5 -> g1) x4
    c: Coincident(g1,g0)
    c: Vertical(g3)
    c: Coincident(g1,g-1)
    c: Distance(g6) = 3.6
    c: Coincident(g6,g1)
    c: Coincident(g1,g6)
    c: Coincident(g0,g1)
FEATURE [PartDesign::Groove] Groove
  Angle = 360
  Angle2 = 60
  Axis = (0,1,0)
  Base = (-213.443,3.6,-69.4316)
  BaseFeature = -> Pocket018
  Profile = -> Sketch152
  ReferenceAxis = -> Sketch152 [V_Axis]
  Refine = true
  Reversed = true
  Suppressed = false
  Type = 0
FEATURE [PartDesign::Body] Body006  label="lato SX"
  AllowCompound = false
  Group = -> [Binder,Pad019,Chamfer015,Pocket002,Sketch133,Sketch091,Pad005,Sketch092,Pocket001,Sketch093,Sketch094,Pad006,Sketch095,Pad007,Sketch096,Pad008,Sketch097,Pad009,Chamfer005,Pocket004,Sketch098,Pad010,Chamfer006,Pocket003,SubtractivePipe,SubtractivePipe001,Sketch099,Sketch106,Sketch107,Sketch108,Clone2D,Sketch109,SubtractiveLoft,SubtractiveLoft001,Sketch110,Sketch111,Sketch112,Chamfer016,Chamfer017,+15 more]
  Origin = -> Origin006
  Tip = -> Groove
FEATURE [Sketcher::SketchObject] Sketch153  label="ripieno_per_sostegno_led_batteria"
  ArcFitTolerance = 1e-06
  AttachmentSupport = -> [XZ_Plane]
  ExternalGeometry = -> [Sketch036]
  FullyConstrained = true
  MakeInternals = false
  MapMode = 5
  Placement = pos=(0,0,0) rot=(1,0,0;1.5708rad)
  sketch-geometry (4):
    g0: LineSegment StartX=-217.343 StartY=-54.5944 StartZ=0 EndX=-217.343 EndY=-63.1944 EndZ=0
    g1: LineSegment StartX=-217.343 StartY=-63.1944 StartZ=0 EndX=-211.843 EndY=-63.1944 EndZ=0
    g2: LineSegment StartX=-211.843 StartY=-63.1944 StartZ=0 EndX=-211.843 EndY=-54.5944 EndZ=0
    g3: LineSegment StartX=-211.843 StartY=-54.5944 StartZ=0 EndX=-217.343 EndY=-54.5944 EndZ=0
  constraints (11):
    c: Coincident(g0,g1)
    c: Coincident(g1,g2)
    c: Coincident(g2,g3)
    c: Coincident(g3,g0)
    c: Vertical(g0)
    c: Horizontal(g1)
    c: Horizontal(g3)
    c: Tangent(g2,g-3)
    c: DistanceY(g2,g-3) = 4.5
    c: DistanceX(g3,g3) = 5.5
    c: DistanceY(g0,g0) = 8.6
FEATURE [PartDesign::Body] Body  label="Struttura pistola"
  AllowCompound = false
  Group = -> [Sketch,Sketch002,Sketch004,DatumPlane,Sketch005,DatumPlane001,CopyCut,Sketch008,Sketch009,Sketch010,Sketch011,Sketch012,Sketch013,Sketch014,Sketch015,Sketch016,Sketch017,Sketch018,Sketch019,Sketch020,Sketch022,Sketch023,Sketch024,Sketch025,Sketch026,Sketch027,Sketch029,Sketch030,Sketch031,Sketch032,Sketch033,Sketch034,Sketch035,Sketch036,Sketch037,Sketch038,Sketch039,Sketch040,Sketch041,Sketch042,+28 more]
  Origin = -> Origin
FEATURE [Part::Extrusion] Extrude088  label="Extrude088 - ripieno_per_sostegno_led_batteria"
  Base = -> Sketch153
  Dir = (0,-1,2e-16)
  DirMode = 2
  FaceMakerClass = Part::FaceMakerBullseye
  FaceMakerMode = 3
  LengthFwd = 4
  LengthRev = 0
  Placement = pos=(0,12.6,0) rot=(0,0,1;0rad)
  Solid = true
  Symmetric = false
FEATURE [Part::MultiFuse] Fusion004
  Refine = true
  Shapes = -> [Cut050,Extrude088]
FEATURE [Part::Cut] Cut051
  Base = -> Fusion004
  Refine = true
  Tool = -> Extrude087
FEATURE [Part::Cut] Cut052
  Base = -> Cut051
  Refine = true
  Tool = -> Extrude086
FEATURE [Sketcher::SketchObject] Sketch154
  ArcFitTolerance = 1e-06
  AttachmentSupport = -> [Pad016]
  ExternalGeometry = -> [Binder001]
  FullyConstrained = true
  MakeInternals = false
  MapMode = 5
  Placement = pos=(0,-3.6,0) rot=(1,0,0;1.5708rad)
  sketch-geometry (25):
    g0: LineSegment StartX=-214.643 StartY=-72.4316 StartZ=0 EndX=-212.243 EndY=-72.4316 EndZ=0
    g1: LineSegment StartX=-212.243 StartY=-72.4316 StartZ=0 EndX=-212.243 EndY=-71.2316 EndZ=0
    g2: LineSegment StartX=-212.243 StartY=-71.2316 StartZ=0 EndX=-214.643 EndY=-71.2316 EndZ=0
    g3: LineSegment StartX=-214.643 StartY=-71.2316 StartZ=0 EndX=-214.643 EndY=-72.4316 EndZ=0
    g4: GeomPoint [constr] X=-213.443 Y=-71.8316 Z=0
    g5: LineSegment StartX=-214.643 StartY=-69.6316 StartZ=0 EndX=-212.243 EndY=-69.6316 EndZ=0
    g6: LineSegment StartX=-212.243 StartY=-69.6316 StartZ=0 EndX=-212.243 EndY=-68.4316 EndZ=0
    g7: LineSegment StartX=-212.243 StartY=-68.4316 StartZ=0 EndX=-214.643 EndY=-68.4316 EndZ=0
    g8: LineSegment StartX=-214.643 StartY=-68.4316 StartZ=0 EndX=-214.643 EndY=-69.6316 EndZ=0
    g9: GeomPoint [constr] X=-213.443 Y=-69.0316 Z=0
    g10: LineSegment StartX=-214.643 StartY=-66.8316 StartZ=0 EndX=-212.243 EndY=-66.8316 EndZ=0
    g11: LineSegment StartX=-212.243 StartY=-66.8316 StartZ=0 EndX=-212.243 EndY=-65.6316 EndZ=0
    g12: LineSegment StartX=-212.243 StartY=-65.6316 StartZ=0 EndX=-214.643 EndY=-65.6316 EndZ=0
    g13: LineSegment StartX=-214.643 StartY=-65.6316 StartZ=0 EndX=-214.643 EndY=-66.8316 EndZ=0
    g14: GeomPoint [constr] X=-213.443 Y=-66.2316 Z=0
    g15: LineSegment StartX=-214.643 StartY=-64.0316 StartZ=0 EndX=-212.243 EndY=-64.0316 EndZ=0
    g16: LineSegment StartX=-212.243 StartY=-64.0316 StartZ=0 EndX=-212.243 EndY=-62.8316 EndZ=0
    g17: LineSegment StartX=-212.243 StartY=-62.8316 StartZ=0 EndX=-214.643 EndY=-62.8316 EndZ=0
    g18: LineSegment StartX=-214.643 StartY=-62.8316 StartZ=0 EndX=-214.643 EndY=-64.0316 EndZ=0
    g19: GeomPoint [constr] X=-213.443 Y=-63.4316 Z=0
    g20: LineSegment StartX=-214.643 StartY=-61.2316 StartZ=0 EndX=-212.243 EndY=-61.2316 EndZ=0
    g21: LineSegment StartX=-212.243 StartY=-61.2316 StartZ=0 EndX=-212.243 EndY=-60.0316 EndZ=0
    g22: LineSegment StartX=-212.243 StartY=-60.0316 StartZ=0 EndX=-214.643 EndY=-60.0316 EndZ=0
    g23: LineSegment StartX=-214.643 StartY=-60.0316 StartZ=0 EndX=-214.643 EndY=-61.2316 EndZ=0
    g24: GeomPoint [constr] X=-213.443 Y=-60.6316 Z=0
  constraints (65):
    c: Coincident(g0,g1)
    c: Coincident(g1,g2)
    c: Coincident(g2,g3)
    c: Coincident(g3,g0)
    c: Horizontal(g0)
    c: Horizontal(g2)
    c: Vertical(g1)
    c: Vertical(g3)
    c: Symmetric(g2,g0,g4)
    c: Distance(g1,g3) = 2.4
    c: Distance(g0,g2) = 1.2
    c: Coincident(g5,g6)
    c: Coincident(g6,g7)
    c: Coincident(g7,g8)
    c: Coincident(g8,g5)
    c: Horizontal(g5)
    c: Horizontal(g7)
    c: Vertical(g6)
    c: Vertical(g8)
    c: Symmetric(g7,g5,g9)
    c: Distance(g6,g8) = 2.4
    c: Distance(g5,g7) = 1.2
    c: Coincident(g10,g11)
    c: Coincident(g11,g12)
    c: Coincident(g12,g13)
    c: Coincident(g13,g10)
    c: Horizontal(g10)
    c: Horizontal(g12)
    c: Vertical(g11)
    c: Vertical(g13)
    c: Symmetric(g12,g10,g14)
    c: Distance(g11,g13) = 2.4
    c: Distance(g10,g12) = 1.2
    c: Coincident(g15,g16)
    c: Coincident(g16,g17)
    c: Coincident(g17,g18)
    c: Coincident(g18,g15)
    c: Horizontal(g15)
    c: Horizontal(g17)
    c: Vertical(g16)
    c: Vertical(g18)
    c: Symmetric(g17,g15,g19)
    c: Distance(g16,g18) = 2.4
    c: Distance(g15,g17) = 1.2
    c: Vertical(g4,g-3)
    c: Vertical(g9,g-3)
    c: Vertical(g14,g-3)
    c: Vertical(g19,g-3)
    c: DistanceY(g-3,g4) = 5
    c: DistanceY(g4,g9) = 2.8
    c: DistanceY(g9,g14) = 2.8
    c: DistanceY(g14,g19) = 2.8
    c: Coincident(g20,g21)
    c: Coincident(g21,g22)
    c: Coincident(g22,g23)
    c: Coincident(g23,g20)
    c: Horizontal(g20)
    c: Horizontal(g22)
    c: Vertical(g21)
    c: Vertical(g23)
    c: Symmetric(g22,g20,g24)
    c: Distance(g21,g23) = 2.4
    c: Distance(g20,g22) = 1.2
    c: DistanceY(g19,g24) = 2.8
    c: Vertical(g-3,g24)
FEATURE [PartDesign::Pocket] Pocket020
  BaseFeature = -> Pocket012
  Direction = (0,1,-2e-16)
  Length = 3.6
  Length2 = 5
  Profile = -> Sketch154
  ReferenceAxis = -> Sketch154 [N_Axis]
  Refine = true
  Suppressed = false
  Type = 0
FEATURE [PartDesign::Body] Body007  label="lato DX"
  AllowCompound = false
  Group = -> [Binder001,Sketch114,Pad011,Chamfer014,Sketch115,Pocket006,Sketch116,Pad012,Sketch117,Pocket007,Sketch118,Pad013,Sketch119,Pocket008,Pad017,Chamfer009,Pocket009,Sketch123,Sketch120,Pad014,Pad018,Chamfer008,Pocket010,Sketch121,Pad015,Sketch122,Pad016,SubtractivePipe004,SubtractivePipe005,Sketch149,Sketch148,Sketch124,Sketch125,Sketch126,Sketch129,Sketch130,Clone2D001,Sketch131,SubtractiveLoft002,+13 more]
  Origin = -> Origin007
  Tip = -> Pocket020
note: 2 file-system paths scrubbed to <path> (originals preserved in the JSON sidecar)
